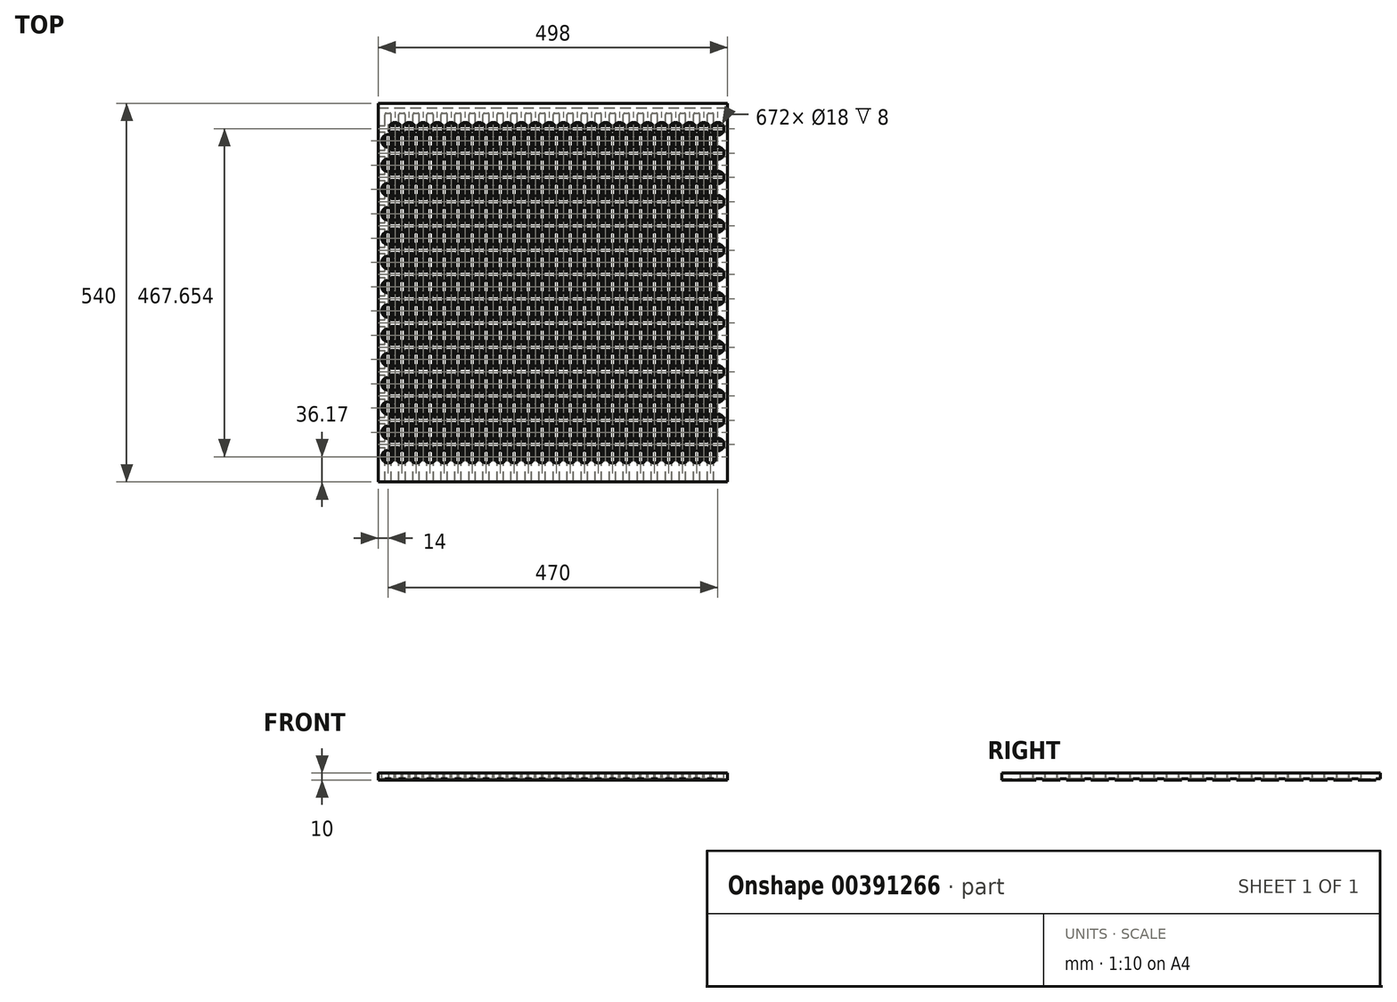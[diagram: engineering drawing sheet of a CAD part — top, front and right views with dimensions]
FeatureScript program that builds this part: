
annotation { "Feature Type Name" : "Feature", "Feature Type Description" : "" }
export const myFeature = defineFeature(function(context is Context, id is Id, definition is map)
    precondition{}
    {
        {
            var Q0;
            Q0=qCreatedBy(makeId("Top.planeOp"),FACE);
            var sketch = newSketch(context, id + "F0", { "sketchPlane" : qUnion([Q0])});
            skCircle(sketch, "E0", {"center": v(0, 0) * mm, "radius": 9 * mm});
            skCircle(sketch, "E1.1.0.0", {"center": v(20, 0) * mm, "radius": 9 * mm});
            skCircle(sketch, "E1.2.0.0", {"center": v(40, 0) * mm, "radius": 9 * mm});
            skCircle(sketch, "E1.3.0.0", {"center": v(60, 0) * mm, "radius": 9 * mm});
            skCircle(sketch, "E1.4.0.0", {"center": v(80, 0) * mm, "radius": 9 * mm});
            skCircle(sketch, "E1.5.0.0", {"center": v(100, 0) * mm, "radius": 9 * mm});
            skCircle(sketch, "E1.6.0.0", {"center": v(120, 0) * mm, "radius": 9 * mm});
            skCircle(sketch, "E1.7.0.0", {"center": v(140, 0) * mm, "radius": 9 * mm});
            skCircle(sketch, "E1.8.0.0", {"center": v(160, 0) * mm, "radius": 9 * mm});
            skCircle(sketch, "E1.9.0.0", {"center": v(180, 0) * mm, "radius": 9 * mm});
            skCircle(sketch, "E1.10.0.0", {"center": v(200, 0) * mm, "radius": 9 * mm});
            skCircle(sketch, "E1.11.0.0", {"center": v(220, 0) * mm, "radius": 9 * mm});
            skCircle(sketch, "E1.12.0.0", {"center": v(240, 0) * mm, "radius": 9 * mm});
            skCircle(sketch, "E1.13.0.0", {"center": v(260, 0) * mm, "radius": 9 * mm});
            skCircle(sketch, "E1.14.0.0", {"center": v(280, 0) * mm, "radius": 9 * mm});
            skCircle(sketch, "E1.15.0.0", {"center": v(300, 0) * mm, "radius": 9 * mm});
            skCircle(sketch, "E1.16.0.0", {"center": v(320, 0) * mm, "radius": 9 * mm});
            skCircle(sketch, "E1.17.0.0", {"center": v(340, 0) * mm, "radius": 9 * mm});
            skCircle(sketch, "E1.18.0.0", {"center": v(360, 0) * mm, "radius": 9 * mm});
            skCircle(sketch, "E1.19.0.0", {"center": v(380, 0) * mm, "radius": 9 * mm});
            skCircle(sketch, "E1.20.0.0", {"center": v(400, 0) * mm, "radius": 9 * mm});
            skCircle(sketch, "E1.21.0.0", {"center": v(420, 0) * mm, "radius": 9 * mm});
            skCircle(sketch, "E1.22.0.0", {"center": v(440, 0) * mm, "radius": 9 * mm});
            skCircle(sketch, "E1.23.0.0", {"center": v(460, 0) * mm, "radius": 9 * mm});
            skLineSegment(sketch, "E1.direction1", {"start": v(0, 0) * mm, "end": v(20, 0) * mm, "construction": true});
            skCircle(sketch, "E2", {"center": v(10, 17.32) * mm, "radius": 9 * mm});
            skCircle(sketch, "E3.1.0.0", {"center": v(30, 17.32) * mm, "radius": 9 * mm});
            skCircle(sketch, "E3.2.0.0", {"center": v(50, 17.32) * mm, "radius": 9 * mm});
            skCircle(sketch, "E3.3.0.0", {"center": v(70, 17.32) * mm, "radius": 9 * mm});
            skCircle(sketch, "E3.4.0.0", {"center": v(90, 17.32) * mm, "radius": 9 * mm});
            skCircle(sketch, "E3.5.0.0", {"center": v(110, 17.32) * mm, "radius": 9 * mm});
            skCircle(sketch, "E3.6.0.0", {"center": v(130, 17.32) * mm, "radius": 9 * mm});
            skCircle(sketch, "E3.7.0.0", {"center": v(150, 17.32) * mm, "radius": 9 * mm});
            skCircle(sketch, "E3.8.0.0", {"center": v(170, 17.32) * mm, "radius": 9 * mm});
            skCircle(sketch, "E3.9.0.0", {"center": v(190, 17.32) * mm, "radius": 9 * mm});
            skCircle(sketch, "E3.10.0.0", {"center": v(210, 17.32) * mm, "radius": 9 * mm});
            skCircle(sketch, "E3.11.0.0", {"center": v(230, 17.32) * mm, "radius": 9 * mm});
            skCircle(sketch, "E3.12.0.0", {"center": v(250, 17.32) * mm, "radius": 9 * mm});
            skCircle(sketch, "E3.13.0.0", {"center": v(270, 17.32) * mm, "radius": 9 * mm});
            skCircle(sketch, "E3.14.0.0", {"center": v(290, 17.32) * mm, "radius": 9 * mm});
            skCircle(sketch, "E3.15.0.0", {"center": v(310, 17.32) * mm, "radius": 9 * mm});
            skCircle(sketch, "E3.16.0.0", {"center": v(330, 17.32) * mm, "radius": 9 * mm});
            skCircle(sketch, "E3.17.0.0", {"center": v(350, 17.32) * mm, "radius": 9 * mm});
            skCircle(sketch, "E3.18.0.0", {"center": v(370, 17.32) * mm, "radius": 9 * mm});
            skCircle(sketch, "E3.19.0.0", {"center": v(390, 17.32) * mm, "radius": 9 * mm});
            skCircle(sketch, "E3.20.0.0", {"center": v(410, 17.32) * mm, "radius": 9 * mm});
            skCircle(sketch, "E3.21.0.0", {"center": v(430, 17.32) * mm, "radius": 9 * mm});
            skCircle(sketch, "E3.22.0.0", {"center": v(450, 17.32) * mm, "radius": 9 * mm});
            skCircle(sketch, "E3.23.0.0", {"center": v(470, 17.32) * mm, "radius": 9 * mm});
            skLineSegment(sketch, "E3.direction1", {"start": v(10, 17.32) * mm, "end": v(30, 17.32) * mm, "construction": true});
            skCircle(sketch, "E4.0.1.0", {"center": v(280, 34.64) * mm, "radius": 9 * mm});
            skCircle(sketch, "E4.0.1.1", {"center": v(260, 34.64) * mm, "radius": 9 * mm});
            skCircle(sketch, "E4.0.1.2", {"center": v(130, 51.96) * mm, "radius": 9 * mm});
            skCircle(sketch, "E4.0.1.3", {"center": v(60, 34.64) * mm, "radius": 9 * mm});
            skCircle(sketch, "E4.0.1.4", {"center": v(80, 34.64) * mm, "radius": 9 * mm});
            skCircle(sketch, "E4.0.1.5", {"center": v(100, 34.64) * mm, "radius": 9 * mm});
            skCircle(sketch, "E4.0.1.6", {"center": v(350, 51.96) * mm, "radius": 9 * mm});
            skCircle(sketch, "E4.0.1.7", {"center": v(0, 34.64) * mm, "radius": 9 * mm});
            skCircle(sketch, "E4.0.1.8", {"center": v(120, 34.64) * mm, "radius": 9 * mm});
            skCircle(sketch, "E4.0.1.9", {"center": v(30, 51.96) * mm, "radius": 9 * mm});
            skCircle(sketch, "E4.0.1.10", {"center": v(380, 34.64) * mm, "radius": 9 * mm});
            skCircle(sketch, "E4.0.1.11", {"center": v(140, 34.64) * mm, "radius": 9 * mm});
            skCircle(sketch, "E4.0.1.12", {"center": v(450, 51.96) * mm, "radius": 9 * mm});
            skCircle(sketch, "E4.0.1.13", {"center": v(160, 34.64) * mm, "radius": 9 * mm});
            skCircle(sketch, "E4.0.1.14", {"center": v(300, 34.64) * mm, "radius": 9 * mm});
            skCircle(sketch, "E4.0.1.15", {"center": v(40, 34.64) * mm, "radius": 9 * mm});
            skCircle(sketch, "E4.0.1.16", {"center": v(210, 51.96) * mm, "radius": 9 * mm});
            skCircle(sketch, "E4.0.1.17", {"center": v(330, 51.96) * mm, "radius": 9 * mm});
            skCircle(sketch, "E4.0.1.18", {"center": v(270, 51.96) * mm, "radius": 9 * mm});
            skCircle(sketch, "E4.0.1.19", {"center": v(440, 34.64) * mm, "radius": 9 * mm});
            skCircle(sketch, "E4.0.1.20", {"center": v(110, 51.96) * mm, "radius": 9 * mm});
            skCircle(sketch, "E4.0.1.21", {"center": v(250, 51.96) * mm, "radius": 9 * mm});
            skCircle(sketch, "E4.0.1.22", {"center": v(180, 34.64) * mm, "radius": 9 * mm});
            skCircle(sketch, "E4.0.1.23", {"center": v(430, 51.96) * mm, "radius": 9 * mm});
            skCircle(sketch, "E4.0.1.24", {"center": v(200, 34.64) * mm, "radius": 9 * mm});
            skCircle(sketch, "E4.0.1.25", {"center": v(420, 34.64) * mm, "radius": 9 * mm});
            skCircle(sketch, "E4.0.1.26", {"center": v(70, 51.96) * mm, "radius": 9 * mm});
            skCircle(sketch, "E4.0.1.27", {"center": v(390, 51.96) * mm, "radius": 9 * mm});
            skCircle(sketch, "E4.0.1.28", {"center": v(220, 34.64) * mm, "radius": 9 * mm});
            skCircle(sketch, "E4.0.1.29", {"center": v(190, 51.96) * mm, "radius": 9 * mm});
            skCircle(sketch, "E4.0.1.30", {"center": v(90, 51.96) * mm, "radius": 9 * mm});
            skCircle(sketch, "E4.0.1.31", {"center": v(230, 51.96) * mm, "radius": 9 * mm});
            skCircle(sketch, "E4.0.1.32", {"center": v(150, 51.96) * mm, "radius": 9 * mm});
            skCircle(sketch, "E4.0.1.33", {"center": v(470, 51.96) * mm, "radius": 9 * mm});
            skCircle(sketch, "E4.0.1.34", {"center": v(410, 51.96) * mm, "radius": 9 * mm});
            skCircle(sketch, "E4.0.1.35", {"center": v(50, 51.96) * mm, "radius": 9 * mm});
            skCircle(sketch, "E4.0.1.36", {"center": v(400, 34.64) * mm, "radius": 9 * mm});
            skCircle(sketch, "E4.0.1.37", {"center": v(240, 34.64) * mm, "radius": 9 * mm});
            skCircle(sketch, "E4.0.1.38", {"center": v(320, 34.64) * mm, "radius": 9 * mm});
            skCircle(sketch, "E4.0.1.39", {"center": v(370, 51.96) * mm, "radius": 9 * mm});
            skCircle(sketch, "E4.0.1.40", {"center": v(10, 51.96) * mm, "radius": 9 * mm});
            skCircle(sketch, "E4.0.1.41", {"center": v(290, 51.96) * mm, "radius": 9 * mm});
            skCircle(sketch, "E4.0.1.42", {"center": v(360, 34.64) * mm, "radius": 9 * mm});
            skCircle(sketch, "E4.0.1.43", {"center": v(460, 34.64) * mm, "radius": 9 * mm});
            skCircle(sketch, "E4.0.1.44", {"center": v(310, 51.96) * mm, "radius": 9 * mm});
            skCircle(sketch, "E4.0.1.45", {"center": v(340, 34.64) * mm, "radius": 9 * mm});
            skCircle(sketch, "E4.0.1.46", {"center": v(170, 51.96) * mm, "radius": 9 * mm});
            skCircle(sketch, "E4.0.1.47", {"center": v(20, 34.64) * mm, "radius": 9 * mm});
            skLineSegment(sketch, "E4.0.1.48", {"start": v(0, 34.64) * mm, "end": v(20, 34.64) * mm, "construction": true});
            skLineSegment(sketch, "E4.0.1.49", {"start": v(10, 51.96) * mm, "end": v(30, 51.96) * mm, "construction": true});
            skCircle(sketch, "E4.0.2.0", {"center": v(280, 69.28) * mm, "radius": 9 * mm});
            skCircle(sketch, "E4.0.2.1", {"center": v(260, 69.28) * mm, "radius": 9 * mm});
            skCircle(sketch, "E4.0.2.2", {"center": v(130, 86.6) * mm, "radius": 9 * mm});
            skCircle(sketch, "E4.0.2.3", {"center": v(60, 69.28) * mm, "radius": 9 * mm});
            skCircle(sketch, "E4.0.2.4", {"center": v(80, 69.28) * mm, "radius": 9 * mm});
            skCircle(sketch, "E4.0.2.5", {"center": v(100, 69.28) * mm, "radius": 9 * mm});
            skCircle(sketch, "E4.0.2.6", {"center": v(350, 86.6) * mm, "radius": 9 * mm});
            skCircle(sketch, "E4.0.2.7", {"center": v(0, 69.28) * mm, "radius": 9 * mm});
            skCircle(sketch, "E4.0.2.8", {"center": v(120, 69.28) * mm, "radius": 9 * mm});
            skCircle(sketch, "E4.0.2.9", {"center": v(30, 86.6) * mm, "radius": 9 * mm});
            skCircle(sketch, "E4.0.2.10", {"center": v(380, 69.28) * mm, "radius": 9 * mm});
            skCircle(sketch, "E4.0.2.11", {"center": v(140, 69.28) * mm, "radius": 9 * mm});
            skCircle(sketch, "E4.0.2.12", {"center": v(450, 86.6) * mm, "radius": 9 * mm});
            skCircle(sketch, "E4.0.2.13", {"center": v(160, 69.28) * mm, "radius": 9 * mm});
            skCircle(sketch, "E4.0.2.14", {"center": v(300, 69.28) * mm, "radius": 9 * mm});
            skCircle(sketch, "E4.0.2.15", {"center": v(40, 69.28) * mm, "radius": 9 * mm});
            skCircle(sketch, "E4.0.2.16", {"center": v(210, 86.6) * mm, "radius": 9 * mm});
            skCircle(sketch, "E4.0.2.17", {"center": v(330, 86.6) * mm, "radius": 9 * mm});
            skCircle(sketch, "E4.0.2.18", {"center": v(270, 86.6) * mm, "radius": 9 * mm});
            skCircle(sketch, "E4.0.2.19", {"center": v(440, 69.28) * mm, "radius": 9 * mm});
            skCircle(sketch, "E4.0.2.20", {"center": v(110, 86.6) * mm, "radius": 9 * mm});
            skCircle(sketch, "E4.0.2.21", {"center": v(250, 86.6) * mm, "radius": 9 * mm});
            skCircle(sketch, "E4.0.2.22", {"center": v(180, 69.28) * mm, "radius": 9 * mm});
            skCircle(sketch, "E4.0.2.23", {"center": v(430, 86.6) * mm, "radius": 9 * mm});
            skCircle(sketch, "E4.0.2.24", {"center": v(200, 69.28) * mm, "radius": 9 * mm});
            skCircle(sketch, "E4.0.2.25", {"center": v(420, 69.28) * mm, "radius": 9 * mm});
            skCircle(sketch, "E4.0.2.26", {"center": v(70, 86.6) * mm, "radius": 9 * mm});
            skCircle(sketch, "E4.0.2.27", {"center": v(390, 86.6) * mm, "radius": 9 * mm});
            skCircle(sketch, "E4.0.2.28", {"center": v(220, 69.28) * mm, "radius": 9 * mm});
            skCircle(sketch, "E4.0.2.29", {"center": v(190, 86.6) * mm, "radius": 9 * mm});
            skCircle(sketch, "E4.0.2.30", {"center": v(90, 86.6) * mm, "radius": 9 * mm});
            skCircle(sketch, "E4.0.2.31", {"center": v(230, 86.6) * mm, "radius": 9 * mm});
            skCircle(sketch, "E4.0.2.32", {"center": v(150, 86.6) * mm, "radius": 9 * mm});
            skCircle(sketch, "E4.0.2.33", {"center": v(470, 86.6) * mm, "radius": 9 * mm});
            skCircle(sketch, "E4.0.2.34", {"center": v(410, 86.6) * mm, "radius": 9 * mm});
            skCircle(sketch, "E4.0.2.35", {"center": v(50, 86.6) * mm, "radius": 9 * mm});
            skCircle(sketch, "E4.0.2.36", {"center": v(400, 69.28) * mm, "radius": 9 * mm});
            skCircle(sketch, "E4.0.2.37", {"center": v(240, 69.28) * mm, "radius": 9 * mm});
            skCircle(sketch, "E4.0.2.38", {"center": v(320, 69.28) * mm, "radius": 9 * mm});
            skCircle(sketch, "E4.0.2.39", {"center": v(370, 86.6) * mm, "radius": 9 * mm});
            skCircle(sketch, "E4.0.2.40", {"center": v(10, 86.6) * mm, "radius": 9 * mm});
            skCircle(sketch, "E4.0.2.41", {"center": v(290, 86.6) * mm, "radius": 9 * mm});
            skCircle(sketch, "E4.0.2.42", {"center": v(360, 69.28) * mm, "radius": 9 * mm});
            skCircle(sketch, "E4.0.2.43", {"center": v(460, 69.28) * mm, "radius": 9 * mm});
            skCircle(sketch, "E4.0.2.44", {"center": v(310, 86.6) * mm, "radius": 9 * mm});
            skCircle(sketch, "E4.0.2.45", {"center": v(340, 69.28) * mm, "radius": 9 * mm});
            skCircle(sketch, "E4.0.2.46", {"center": v(170, 86.6) * mm, "radius": 9 * mm});
            skCircle(sketch, "E4.0.2.47", {"center": v(20, 69.28) * mm, "radius": 9 * mm});
            skLineSegment(sketch, "E4.0.2.48", {"start": v(0, 69.28) * mm, "end": v(20, 69.28) * mm, "construction": true});
            skLineSegment(sketch, "E4.0.2.49", {"start": v(10, 86.6) * mm, "end": v(30, 86.6) * mm, "construction": true});
            skCircle(sketch, "E4.0.3.0", {"center": v(280, 103.92) * mm, "radius": 9 * mm});
            skCircle(sketch, "E4.0.3.1", {"center": v(260, 103.92) * mm, "radius": 9 * mm});
            skCircle(sketch, "E4.0.3.2", {"center": v(130, 121.24) * mm, "radius": 9 * mm});
            skCircle(sketch, "E4.0.3.3", {"center": v(60, 103.92) * mm, "radius": 9 * mm});
            skCircle(sketch, "E4.0.3.4", {"center": v(80, 103.92) * mm, "radius": 9 * mm});
            skCircle(sketch, "E4.0.3.5", {"center": v(100, 103.92) * mm, "radius": 9 * mm});
            skCircle(sketch, "E4.0.3.6", {"center": v(350, 121.24) * mm, "radius": 9 * mm});
            skCircle(sketch, "E4.0.3.7", {"center": v(0, 103.92) * mm, "radius": 9 * mm});
            skCircle(sketch, "E4.0.3.8", {"center": v(120, 103.92) * mm, "radius": 9 * mm});
            skCircle(sketch, "E4.0.3.9", {"center": v(30, 121.24) * mm, "radius": 9 * mm});
            skCircle(sketch, "E4.0.3.10", {"center": v(380, 103.92) * mm, "radius": 9 * mm});
            skCircle(sketch, "E4.0.3.11", {"center": v(140, 103.92) * mm, "radius": 9 * mm});
            skCircle(sketch, "E4.0.3.12", {"center": v(450, 121.24) * mm, "radius": 9 * mm});
            skCircle(sketch, "E4.0.3.13", {"center": v(160, 103.92) * mm, "radius": 9 * mm});
            skCircle(sketch, "E4.0.3.14", {"center": v(300, 103.92) * mm, "radius": 9 * mm});
            skCircle(sketch, "E4.0.3.15", {"center": v(40, 103.92) * mm, "radius": 9 * mm});
            skCircle(sketch, "E4.0.3.16", {"center": v(210, 121.24) * mm, "radius": 9 * mm});
            skCircle(sketch, "E4.0.3.17", {"center": v(330, 121.24) * mm, "radius": 9 * mm});
            skCircle(sketch, "E4.0.3.18", {"center": v(270, 121.24) * mm, "radius": 9 * mm});
            skCircle(sketch, "E4.0.3.19", {"center": v(440, 103.92) * mm, "radius": 9 * mm});
            skCircle(sketch, "E4.0.3.20", {"center": v(110, 121.24) * mm, "radius": 9 * mm});
            skCircle(sketch, "E4.0.3.21", {"center": v(250, 121.24) * mm, "radius": 9 * mm});
            skCircle(sketch, "E4.0.3.22", {"center": v(180, 103.92) * mm, "radius": 9 * mm});
            skCircle(sketch, "E4.0.3.23", {"center": v(430, 121.24) * mm, "radius": 9 * mm});
            skCircle(sketch, "E4.0.3.24", {"center": v(200, 103.92) * mm, "radius": 9 * mm});
            skCircle(sketch, "E4.0.3.25", {"center": v(420, 103.92) * mm, "radius": 9 * mm});
            skCircle(sketch, "E4.0.3.26", {"center": v(70, 121.24) * mm, "radius": 9 * mm});
            skCircle(sketch, "E4.0.3.27", {"center": v(390, 121.24) * mm, "radius": 9 * mm});
            skCircle(sketch, "E4.0.3.28", {"center": v(220, 103.92) * mm, "radius": 9 * mm});
            skCircle(sketch, "E4.0.3.29", {"center": v(190, 121.24) * mm, "radius": 9 * mm});
            skCircle(sketch, "E4.0.3.30", {"center": v(90, 121.24) * mm, "radius": 9 * mm});
            skCircle(sketch, "E4.0.3.31", {"center": v(230, 121.24) * mm, "radius": 9 * mm});
            skCircle(sketch, "E4.0.3.32", {"center": v(150, 121.24) * mm, "radius": 9 * mm});
            skCircle(sketch, "E4.0.3.33", {"center": v(470, 121.24) * mm, "radius": 9 * mm});
            skCircle(sketch, "E4.0.3.34", {"center": v(410, 121.24) * mm, "radius": 9 * mm});
            skCircle(sketch, "E4.0.3.35", {"center": v(50, 121.24) * mm, "radius": 9 * mm});
            skCircle(sketch, "E4.0.3.36", {"center": v(400, 103.92) * mm, "radius": 9 * mm});
            skCircle(sketch, "E4.0.3.37", {"center": v(240, 103.92) * mm, "radius": 9 * mm});
            skCircle(sketch, "E4.0.3.38", {"center": v(320, 103.92) * mm, "radius": 9 * mm});
            skCircle(sketch, "E4.0.3.39", {"center": v(370, 121.24) * mm, "radius": 9 * mm});
            skCircle(sketch, "E4.0.3.40", {"center": v(10, 121.24) * mm, "radius": 9 * mm});
            skCircle(sketch, "E4.0.3.41", {"center": v(290, 121.24) * mm, "radius": 9 * mm});
            skCircle(sketch, "E4.0.3.42", {"center": v(360, 103.92) * mm, "radius": 9 * mm});
            skCircle(sketch, "E4.0.3.43", {"center": v(460, 103.92) * mm, "radius": 9 * mm});
            skCircle(sketch, "E4.0.3.44", {"center": v(310, 121.24) * mm, "radius": 9 * mm});
            skCircle(sketch, "E4.0.3.45", {"center": v(340, 103.92) * mm, "radius": 9 * mm});
            skCircle(sketch, "E4.0.3.46", {"center": v(170, 121.24) * mm, "radius": 9 * mm});
            skCircle(sketch, "E4.0.3.47", {"center": v(20, 103.92) * mm, "radius": 9 * mm});
            skLineSegment(sketch, "E4.0.3.48", {"start": v(0, 103.92) * mm, "end": v(20, 103.92) * mm, "construction": true});
            skLineSegment(sketch, "E4.0.3.49", {"start": v(10, 121.24) * mm, "end": v(30, 121.24) * mm, "construction": true});
            skCircle(sketch, "E4.0.4.0", {"center": v(280, 138.56) * mm, "radius": 9 * mm});
            skCircle(sketch, "E4.0.4.1", {"center": v(260, 138.56) * mm, "radius": 9 * mm});
            skCircle(sketch, "E4.0.4.2", {"center": v(130, 155.88) * mm, "radius": 9 * mm});
            skCircle(sketch, "E4.0.4.3", {"center": v(60, 138.56) * mm, "radius": 9 * mm});
            skCircle(sketch, "E4.0.4.4", {"center": v(80, 138.56) * mm, "radius": 9 * mm});
            skCircle(sketch, "E4.0.4.5", {"center": v(100, 138.56) * mm, "radius": 9 * mm});
            skCircle(sketch, "E4.0.4.6", {"center": v(350, 155.88) * mm, "radius": 9 * mm});
            skCircle(sketch, "E4.0.4.7", {"center": v(0, 138.56) * mm, "radius": 9 * mm});
            skCircle(sketch, "E4.0.4.8", {"center": v(120, 138.56) * mm, "radius": 9 * mm});
            skCircle(sketch, "E4.0.4.9", {"center": v(30, 155.88) * mm, "radius": 9 * mm});
            skCircle(sketch, "E4.0.4.10", {"center": v(380, 138.56) * mm, "radius": 9 * mm});
            skCircle(sketch, "E4.0.4.11", {"center": v(140, 138.56) * mm, "radius": 9 * mm});
            skCircle(sketch, "E4.0.4.12", {"center": v(450, 155.88) * mm, "radius": 9 * mm});
            skCircle(sketch, "E4.0.4.13", {"center": v(160, 138.56) * mm, "radius": 9 * mm});
            skCircle(sketch, "E4.0.4.14", {"center": v(300, 138.56) * mm, "radius": 9 * mm});
            skCircle(sketch, "E4.0.4.15", {"center": v(40, 138.56) * mm, "radius": 9 * mm});
            skCircle(sketch, "E4.0.4.16", {"center": v(210, 155.88) * mm, "radius": 9 * mm});
            skCircle(sketch, "E4.0.4.17", {"center": v(330, 155.88) * mm, "radius": 9 * mm});
            skCircle(sketch, "E4.0.4.18", {"center": v(270, 155.88) * mm, "radius": 9 * mm});
            skCircle(sketch, "E4.0.4.19", {"center": v(440, 138.56) * mm, "radius": 9 * mm});
            skCircle(sketch, "E4.0.4.20", {"center": v(110, 155.88) * mm, "radius": 9 * mm});
            skCircle(sketch, "E4.0.4.21", {"center": v(250, 155.88) * mm, "radius": 9 * mm});
            skCircle(sketch, "E4.0.4.22", {"center": v(180, 138.56) * mm, "radius": 9 * mm});
            skCircle(sketch, "E4.0.4.23", {"center": v(430, 155.88) * mm, "radius": 9 * mm});
            skCircle(sketch, "E4.0.4.24", {"center": v(200, 138.56) * mm, "radius": 9 * mm});
            skCircle(sketch, "E4.0.4.25", {"center": v(420, 138.56) * mm, "radius": 9 * mm});
            skCircle(sketch, "E4.0.4.26", {"center": v(70, 155.88) * mm, "radius": 9 * mm});
            skCircle(sketch, "E4.0.4.27", {"center": v(390, 155.88) * mm, "radius": 9 * mm});
            skCircle(sketch, "E4.0.4.28", {"center": v(220, 138.56) * mm, "radius": 9 * mm});
            skCircle(sketch, "E4.0.4.29", {"center": v(190, 155.88) * mm, "radius": 9 * mm});
            skCircle(sketch, "E4.0.4.30", {"center": v(90, 155.88) * mm, "radius": 9 * mm});
            skCircle(sketch, "E4.0.4.31", {"center": v(230, 155.88) * mm, "radius": 9 * mm});
            skCircle(sketch, "E4.0.4.32", {"center": v(150, 155.88) * mm, "radius": 9 * mm});
            skCircle(sketch, "E4.0.4.33", {"center": v(470, 155.88) * mm, "radius": 9 * mm});
            skCircle(sketch, "E4.0.4.34", {"center": v(410, 155.88) * mm, "radius": 9 * mm});
            skCircle(sketch, "E4.0.4.35", {"center": v(50, 155.88) * mm, "radius": 9 * mm});
            skCircle(sketch, "E4.0.4.36", {"center": v(400, 138.56) * mm, "radius": 9 * mm});
            skCircle(sketch, "E4.0.4.37", {"center": v(240, 138.56) * mm, "radius": 9 * mm});
            skCircle(sketch, "E4.0.4.38", {"center": v(320, 138.56) * mm, "radius": 9 * mm});
            skCircle(sketch, "E4.0.4.39", {"center": v(370, 155.88) * mm, "radius": 9 * mm});
            skCircle(sketch, "E4.0.4.40", {"center": v(10, 155.88) * mm, "radius": 9 * mm});
            skCircle(sketch, "E4.0.4.41", {"center": v(290, 155.88) * mm, "radius": 9 * mm});
            skCircle(sketch, "E4.0.4.42", {"center": v(360, 138.56) * mm, "radius": 9 * mm});
            skCircle(sketch, "E4.0.4.43", {"center": v(460, 138.56) * mm, "radius": 9 * mm});
            skCircle(sketch, "E4.0.4.44", {"center": v(310, 155.88) * mm, "radius": 9 * mm});
            skCircle(sketch, "E4.0.4.45", {"center": v(340, 138.56) * mm, "radius": 9 * mm});
            skCircle(sketch, "E4.0.4.46", {"center": v(170, 155.88) * mm, "radius": 9 * mm});
            skCircle(sketch, "E4.0.4.47", {"center": v(20, 138.56) * mm, "radius": 9 * mm});
            skLineSegment(sketch, "E4.0.4.48", {"start": v(0, 138.56) * mm, "end": v(20, 138.56) * mm, "construction": true});
            skLineSegment(sketch, "E4.0.4.49", {"start": v(10, 155.88) * mm, "end": v(30, 155.88) * mm, "construction": true});
            skCircle(sketch, "E4.0.5.0", {"center": v(280, 173.2) * mm, "radius": 9 * mm});
            skCircle(sketch, "E4.0.5.1", {"center": v(260, 173.2) * mm, "radius": 9 * mm});
            skCircle(sketch, "E4.0.5.2", {"center": v(130, 190.53) * mm, "radius": 9 * mm});
            skCircle(sketch, "E4.0.5.3", {"center": v(60, 173.2) * mm, "radius": 9 * mm});
            skCircle(sketch, "E4.0.5.4", {"center": v(80, 173.2) * mm, "radius": 9 * mm});
            skCircle(sketch, "E4.0.5.5", {"center": v(100, 173.2) * mm, "radius": 9 * mm});
            skCircle(sketch, "E4.0.5.6", {"center": v(350, 190.53) * mm, "radius": 9 * mm});
            skCircle(sketch, "E4.0.5.7", {"center": v(0, 173.2) * mm, "radius": 9 * mm});
            skCircle(sketch, "E4.0.5.8", {"center": v(120, 173.2) * mm, "radius": 9 * mm});
            skCircle(sketch, "E4.0.5.9", {"center": v(30, 190.53) * mm, "radius": 9 * mm});
            skCircle(sketch, "E4.0.5.10", {"center": v(380, 173.2) * mm, "radius": 9 * mm});
            skCircle(sketch, "E4.0.5.11", {"center": v(140, 173.2) * mm, "radius": 9 * mm});
            skCircle(sketch, "E4.0.5.12", {"center": v(450, 190.53) * mm, "radius": 9 * mm});
            skCircle(sketch, "E4.0.5.13", {"center": v(160, 173.2) * mm, "radius": 9 * mm});
            skCircle(sketch, "E4.0.5.14", {"center": v(300, 173.2) * mm, "radius": 9 * mm});
            skCircle(sketch, "E4.0.5.15", {"center": v(40, 173.2) * mm, "radius": 9 * mm});
            skCircle(sketch, "E4.0.5.16", {"center": v(210, 190.53) * mm, "radius": 9 * mm});
            skCircle(sketch, "E4.0.5.17", {"center": v(330, 190.53) * mm, "radius": 9 * mm});
            skCircle(sketch, "E4.0.5.18", {"center": v(270, 190.53) * mm, "radius": 9 * mm});
            skCircle(sketch, "E4.0.5.19", {"center": v(440, 173.2) * mm, "radius": 9 * mm});
            skCircle(sketch, "E4.0.5.20", {"center": v(110, 190.53) * mm, "radius": 9 * mm});
            skCircle(sketch, "E4.0.5.21", {"center": v(250, 190.53) * mm, "radius": 9 * mm});
            skCircle(sketch, "E4.0.5.22", {"center": v(180, 173.2) * mm, "radius": 9 * mm});
            skCircle(sketch, "E4.0.5.23", {"center": v(430, 190.53) * mm, "radius": 9 * mm});
            skCircle(sketch, "E4.0.5.24", {"center": v(200, 173.2) * mm, "radius": 9 * mm});
            skCircle(sketch, "E4.0.5.25", {"center": v(420, 173.2) * mm, "radius": 9 * mm});
            skCircle(sketch, "E4.0.5.26", {"center": v(70, 190.53) * mm, "radius": 9 * mm});
            skCircle(sketch, "E4.0.5.27", {"center": v(390, 190.53) * mm, "radius": 9 * mm});
            skCircle(sketch, "E4.0.5.28", {"center": v(220, 173.2) * mm, "radius": 9 * mm});
            skCircle(sketch, "E4.0.5.29", {"center": v(190, 190.53) * mm, "radius": 9 * mm});
            skCircle(sketch, "E4.0.5.30", {"center": v(90, 190.53) * mm, "radius": 9 * mm});
            skCircle(sketch, "E4.0.5.31", {"center": v(230, 190.53) * mm, "radius": 9 * mm});
            skCircle(sketch, "E4.0.5.32", {"center": v(150, 190.53) * mm, "radius": 9 * mm});
            skCircle(sketch, "E4.0.5.33", {"center": v(470, 190.53) * mm, "radius": 9 * mm});
            skCircle(sketch, "E4.0.5.34", {"center": v(410, 190.53) * mm, "radius": 9 * mm});
            skCircle(sketch, "E4.0.5.35", {"center": v(50, 190.53) * mm, "radius": 9 * mm});
            skCircle(sketch, "E4.0.5.36", {"center": v(400, 173.2) * mm, "radius": 9 * mm});
            skCircle(sketch, "E4.0.5.37", {"center": v(240, 173.2) * mm, "radius": 9 * mm});
            skCircle(sketch, "E4.0.5.38", {"center": v(320, 173.2) * mm, "radius": 9 * mm});
            skCircle(sketch, "E4.0.5.39", {"center": v(370, 190.53) * mm, "radius": 9 * mm});
            skCircle(sketch, "E4.0.5.40", {"center": v(10, 190.53) * mm, "radius": 9 * mm});
            skCircle(sketch, "E4.0.5.41", {"center": v(290, 190.53) * mm, "radius": 9 * mm});
            skCircle(sketch, "E4.0.5.42", {"center": v(360, 173.2) * mm, "radius": 9 * mm});
            skCircle(sketch, "E4.0.5.43", {"center": v(460, 173.2) * mm, "radius": 9 * mm});
            skCircle(sketch, "E4.0.5.44", {"center": v(310, 190.53) * mm, "radius": 9 * mm});
            skCircle(sketch, "E4.0.5.45", {"center": v(340, 173.2) * mm, "radius": 9 * mm});
            skCircle(sketch, "E4.0.5.46", {"center": v(170, 190.53) * mm, "radius": 9 * mm});
            skCircle(sketch, "E4.0.5.47", {"center": v(20, 173.2) * mm, "radius": 9 * mm});
            skLineSegment(sketch, "E4.0.5.48", {"start": v(0, 173.2) * mm, "end": v(20, 173.2) * mm, "construction": true});
            skLineSegment(sketch, "E4.0.5.49", {"start": v(10, 190.53) * mm, "end": v(30, 190.53) * mm, "construction": true});
            skCircle(sketch, "E4.0.6.0", {"center": v(280, 207.85) * mm, "radius": 9 * mm});
            skCircle(sketch, "E4.0.6.1", {"center": v(260, 207.85) * mm, "radius": 9 * mm});
            skCircle(sketch, "E4.0.6.2", {"center": v(130, 225.17) * mm, "radius": 9 * mm});
            skCircle(sketch, "E4.0.6.3", {"center": v(60, 207.85) * mm, "radius": 9 * mm});
            skCircle(sketch, "E4.0.6.4", {"center": v(80, 207.85) * mm, "radius": 9 * mm});
            skCircle(sketch, "E4.0.6.5", {"center": v(100, 207.85) * mm, "radius": 9 * mm});
            skCircle(sketch, "E4.0.6.6", {"center": v(350, 225.17) * mm, "radius": 9 * mm});
            skCircle(sketch, "E4.0.6.7", {"center": v(0, 207.85) * mm, "radius": 9 * mm});
            skCircle(sketch, "E4.0.6.8", {"center": v(120, 207.85) * mm, "radius": 9 * mm});
            skCircle(sketch, "E4.0.6.9", {"center": v(30, 225.17) * mm, "radius": 9 * mm});
            skCircle(sketch, "E4.0.6.10", {"center": v(380, 207.85) * mm, "radius": 9 * mm});
            skCircle(sketch, "E4.0.6.11", {"center": v(140, 207.85) * mm, "radius": 9 * mm});
            skCircle(sketch, "E4.0.6.12", {"center": v(450, 225.17) * mm, "radius": 9 * mm});
            skCircle(sketch, "E4.0.6.13", {"center": v(160, 207.85) * mm, "radius": 9 * mm});
            skCircle(sketch, "E4.0.6.14", {"center": v(300, 207.85) * mm, "radius": 9 * mm});
            skCircle(sketch, "E4.0.6.15", {"center": v(40, 207.85) * mm, "radius": 9 * mm});
            skCircle(sketch, "E4.0.6.16", {"center": v(210, 225.17) * mm, "radius": 9 * mm});
            skCircle(sketch, "E4.0.6.17", {"center": v(330, 225.17) * mm, "radius": 9 * mm});
            skCircle(sketch, "E4.0.6.18", {"center": v(270, 225.17) * mm, "radius": 9 * mm});
            skCircle(sketch, "E4.0.6.19", {"center": v(440, 207.85) * mm, "radius": 9 * mm});
            skCircle(sketch, "E4.0.6.20", {"center": v(110, 225.17) * mm, "radius": 9 * mm});
            skCircle(sketch, "E4.0.6.21", {"center": v(250, 225.17) * mm, "radius": 9 * mm});
            skCircle(sketch, "E4.0.6.22", {"center": v(180, 207.85) * mm, "radius": 9 * mm});
            skCircle(sketch, "E4.0.6.23", {"center": v(430, 225.17) * mm, "radius": 9 * mm});
            skCircle(sketch, "E4.0.6.24", {"center": v(200, 207.85) * mm, "radius": 9 * mm});
            skCircle(sketch, "E4.0.6.25", {"center": v(420, 207.85) * mm, "radius": 9 * mm});
            skCircle(sketch, "E4.0.6.26", {"center": v(70, 225.17) * mm, "radius": 9 * mm});
            skCircle(sketch, "E4.0.6.27", {"center": v(390, 225.17) * mm, "radius": 9 * mm});
            skCircle(sketch, "E4.0.6.28", {"center": v(220, 207.85) * mm, "radius": 9 * mm});
            skCircle(sketch, "E4.0.6.29", {"center": v(190, 225.17) * mm, "radius": 9 * mm});
            skCircle(sketch, "E4.0.6.30", {"center": v(90, 225.17) * mm, "radius": 9 * mm});
            skCircle(sketch, "E4.0.6.31", {"center": v(230, 225.17) * mm, "radius": 9 * mm});
            skCircle(sketch, "E4.0.6.32", {"center": v(150, 225.17) * mm, "radius": 9 * mm});
            skCircle(sketch, "E4.0.6.33", {"center": v(470, 225.17) * mm, "radius": 9 * mm});
            skCircle(sketch, "E4.0.6.34", {"center": v(410, 225.17) * mm, "radius": 9 * mm});
            skCircle(sketch, "E4.0.6.35", {"center": v(50, 225.17) * mm, "radius": 9 * mm});
            skCircle(sketch, "E4.0.6.36", {"center": v(400, 207.85) * mm, "radius": 9 * mm});
            skCircle(sketch, "E4.0.6.37", {"center": v(240, 207.85) * mm, "radius": 9 * mm});
            skCircle(sketch, "E4.0.6.38", {"center": v(320, 207.85) * mm, "radius": 9 * mm});
            skCircle(sketch, "E4.0.6.39", {"center": v(370, 225.17) * mm, "radius": 9 * mm});
            skCircle(sketch, "E4.0.6.40", {"center": v(10, 225.17) * mm, "radius": 9 * mm});
            skCircle(sketch, "E4.0.6.41", {"center": v(290, 225.17) * mm, "radius": 9 * mm});
            skCircle(sketch, "E4.0.6.42", {"center": v(360, 207.85) * mm, "radius": 9 * mm});
            skCircle(sketch, "E4.0.6.43", {"center": v(460, 207.85) * mm, "radius": 9 * mm});
            skCircle(sketch, "E4.0.6.44", {"center": v(310, 225.17) * mm, "radius": 9 * mm});
            skCircle(sketch, "E4.0.6.45", {"center": v(340, 207.85) * mm, "radius": 9 * mm});
            skCircle(sketch, "E4.0.6.46", {"center": v(170, 225.17) * mm, "radius": 9 * mm});
            skCircle(sketch, "E4.0.6.47", {"center": v(20, 207.85) * mm, "radius": 9 * mm});
            skLineSegment(sketch, "E4.0.6.48", {"start": v(0, 207.85) * mm, "end": v(20, 207.85) * mm, "construction": true});
            skLineSegment(sketch, "E4.0.6.49", {"start": v(10, 225.17) * mm, "end": v(30, 225.17) * mm, "construction": true});
            skCircle(sketch, "E4.0.7.0", {"center": v(280, 242.49) * mm, "radius": 9 * mm});
            skCircle(sketch, "E4.0.7.1", {"center": v(260, 242.49) * mm, "radius": 9 * mm});
            skCircle(sketch, "E4.0.7.2", {"center": v(130, 259.8) * mm, "radius": 9 * mm});
            skCircle(sketch, "E4.0.7.3", {"center": v(60, 242.49) * mm, "radius": 9 * mm});
            skCircle(sketch, "E4.0.7.4", {"center": v(80, 242.49) * mm, "radius": 9 * mm});
            skCircle(sketch, "E4.0.7.5", {"center": v(100, 242.49) * mm, "radius": 9 * mm});
            skCircle(sketch, "E4.0.7.6", {"center": v(350, 259.8) * mm, "radius": 9 * mm});
            skCircle(sketch, "E4.0.7.7", {"center": v(0, 242.49) * mm, "radius": 9 * mm});
            skCircle(sketch, "E4.0.7.8", {"center": v(120, 242.49) * mm, "radius": 9 * mm});
            skCircle(sketch, "E4.0.7.9", {"center": v(30, 259.8) * mm, "radius": 9 * mm});
            skCircle(sketch, "E4.0.7.10", {"center": v(380, 242.49) * mm, "radius": 9 * mm});
            skCircle(sketch, "E4.0.7.11", {"center": v(140, 242.49) * mm, "radius": 9 * mm});
            skCircle(sketch, "E4.0.7.12", {"center": v(450, 259.8) * mm, "radius": 9 * mm});
            skCircle(sketch, "E4.0.7.13", {"center": v(160, 242.49) * mm, "radius": 9 * mm});
            skCircle(sketch, "E4.0.7.14", {"center": v(300, 242.49) * mm, "radius": 9 * mm});
            skCircle(sketch, "E4.0.7.15", {"center": v(40, 242.49) * mm, "radius": 9 * mm});
            skCircle(sketch, "E4.0.7.16", {"center": v(210, 259.8) * mm, "radius": 9 * mm});
            skCircle(sketch, "E4.0.7.17", {"center": v(330, 259.8) * mm, "radius": 9 * mm});
            skCircle(sketch, "E4.0.7.18", {"center": v(270, 259.8) * mm, "radius": 9 * mm});
            skCircle(sketch, "E4.0.7.19", {"center": v(440, 242.49) * mm, "radius": 9 * mm});
            skCircle(sketch, "E4.0.7.20", {"center": v(110, 259.8) * mm, "radius": 9 * mm});
            skCircle(sketch, "E4.0.7.21", {"center": v(250, 259.8) * mm, "radius": 9 * mm});
            skCircle(sketch, "E4.0.7.22", {"center": v(180, 242.49) * mm, "radius": 9 * mm});
            skCircle(sketch, "E4.0.7.23", {"center": v(430, 259.8) * mm, "radius": 9 * mm});
            skCircle(sketch, "E4.0.7.24", {"center": v(200, 242.49) * mm, "radius": 9 * mm});
            skCircle(sketch, "E4.0.7.25", {"center": v(420, 242.49) * mm, "radius": 9 * mm});
            skCircle(sketch, "E4.0.7.26", {"center": v(70, 259.8) * mm, "radius": 9 * mm});
            skCircle(sketch, "E4.0.7.27", {"center": v(390, 259.8) * mm, "radius": 9 * mm});
            skCircle(sketch, "E4.0.7.28", {"center": v(220, 242.49) * mm, "radius": 9 * mm});
            skCircle(sketch, "E4.0.7.29", {"center": v(190, 259.8) * mm, "radius": 9 * mm});
            skCircle(sketch, "E4.0.7.30", {"center": v(90, 259.8) * mm, "radius": 9 * mm});
            skCircle(sketch, "E4.0.7.31", {"center": v(230, 259.8) * mm, "radius": 9 * mm});
            skCircle(sketch, "E4.0.7.32", {"center": v(150, 259.8) * mm, "radius": 9 * mm});
            skCircle(sketch, "E4.0.7.33", {"center": v(470, 259.8) * mm, "radius": 9 * mm});
            skCircle(sketch, "E4.0.7.34", {"center": v(410, 259.8) * mm, "radius": 9 * mm});
            skCircle(sketch, "E4.0.7.35", {"center": v(50, 259.8) * mm, "radius": 9 * mm});
            skCircle(sketch, "E4.0.7.36", {"center": v(400, 242.49) * mm, "radius": 9 * mm});
            skCircle(sketch, "E4.0.7.37", {"center": v(240, 242.49) * mm, "radius": 9 * mm});
            skCircle(sketch, "E4.0.7.38", {"center": v(320, 242.49) * mm, "radius": 9 * mm});
            skCircle(sketch, "E4.0.7.39", {"center": v(370, 259.8) * mm, "radius": 9 * mm});
            skCircle(sketch, "E4.0.7.40", {"center": v(10, 259.8) * mm, "radius": 9 * mm});
            skCircle(sketch, "E4.0.7.41", {"center": v(290, 259.8) * mm, "radius": 9 * mm});
            skCircle(sketch, "E4.0.7.42", {"center": v(360, 242.49) * mm, "radius": 9 * mm});
            skCircle(sketch, "E4.0.7.43", {"center": v(460, 242.49) * mm, "radius": 9 * mm});
            skCircle(sketch, "E4.0.7.44", {"center": v(310, 259.8) * mm, "radius": 9 * mm});
            skCircle(sketch, "E4.0.7.45", {"center": v(340, 242.49) * mm, "radius": 9 * mm});
            skCircle(sketch, "E4.0.7.46", {"center": v(170, 259.8) * mm, "radius": 9 * mm});
            skCircle(sketch, "E4.0.7.47", {"center": v(20, 242.49) * mm, "radius": 9 * mm});
            skLineSegment(sketch, "E4.0.7.48", {"start": v(0, 242.49) * mm, "end": v(20, 242.49) * mm, "construction": true});
            skLineSegment(sketch, "E4.0.7.49", {"start": v(10, 259.8) * mm, "end": v(30, 259.8) * mm, "construction": true});
            skCircle(sketch, "E4.0.8.0", {"center": v(280, 277.13) * mm, "radius": 9 * mm});
            skCircle(sketch, "E4.0.8.1", {"center": v(260, 277.13) * mm, "radius": 9 * mm});
            skCircle(sketch, "E4.0.8.2", {"center": v(130, 294.45) * mm, "radius": 9 * mm});
            skCircle(sketch, "E4.0.8.3", {"center": v(60, 277.13) * mm, "radius": 9 * mm});
            skCircle(sketch, "E4.0.8.4", {"center": v(80, 277.13) * mm, "radius": 9 * mm});
            skCircle(sketch, "E4.0.8.5", {"center": v(100, 277.13) * mm, "radius": 9 * mm});
            skCircle(sketch, "E4.0.8.6", {"center": v(350, 294.45) * mm, "radius": 9 * mm});
            skCircle(sketch, "E4.0.8.7", {"center": v(0, 277.13) * mm, "radius": 9 * mm});
            skCircle(sketch, "E4.0.8.8", {"center": v(120, 277.13) * mm, "radius": 9 * mm});
            skCircle(sketch, "E4.0.8.9", {"center": v(30, 294.45) * mm, "radius": 9 * mm});
            skCircle(sketch, "E4.0.8.10", {"center": v(380, 277.13) * mm, "radius": 9 * mm});
            skCircle(sketch, "E4.0.8.11", {"center": v(140, 277.13) * mm, "radius": 9 * mm});
            skCircle(sketch, "E4.0.8.12", {"center": v(450, 294.45) * mm, "radius": 9 * mm});
            skCircle(sketch, "E4.0.8.13", {"center": v(160, 277.13) * mm, "radius": 9 * mm});
            skCircle(sketch, "E4.0.8.14", {"center": v(300, 277.13) * mm, "radius": 9 * mm});
            skCircle(sketch, "E4.0.8.15", {"center": v(40, 277.13) * mm, "radius": 9 * mm});
            skCircle(sketch, "E4.0.8.16", {"center": v(210, 294.45) * mm, "radius": 9 * mm});
            skCircle(sketch, "E4.0.8.17", {"center": v(330, 294.45) * mm, "radius": 9 * mm});
            skCircle(sketch, "E4.0.8.18", {"center": v(270, 294.45) * mm, "radius": 9 * mm});
            skCircle(sketch, "E4.0.8.19", {"center": v(440, 277.13) * mm, "radius": 9 * mm});
            skCircle(sketch, "E4.0.8.20", {"center": v(110, 294.45) * mm, "radius": 9 * mm});
            skCircle(sketch, "E4.0.8.21", {"center": v(250, 294.45) * mm, "radius": 9 * mm});
            skCircle(sketch, "E4.0.8.22", {"center": v(180, 277.13) * mm, "radius": 9 * mm});
            skCircle(sketch, "E4.0.8.23", {"center": v(430, 294.45) * mm, "radius": 9 * mm});
            skCircle(sketch, "E4.0.8.24", {"center": v(200, 277.13) * mm, "radius": 9 * mm});
            skCircle(sketch, "E4.0.8.25", {"center": v(420, 277.13) * mm, "radius": 9 * mm});
            skCircle(sketch, "E4.0.8.26", {"center": v(70, 294.45) * mm, "radius": 9 * mm});
            skCircle(sketch, "E4.0.8.27", {"center": v(390, 294.45) * mm, "radius": 9 * mm});
            skCircle(sketch, "E4.0.8.28", {"center": v(220, 277.13) * mm, "radius": 9 * mm});
            skCircle(sketch, "E4.0.8.29", {"center": v(190, 294.45) * mm, "radius": 9 * mm});
            skCircle(sketch, "E4.0.8.30", {"center": v(90, 294.45) * mm, "radius": 9 * mm});
            skCircle(sketch, "E4.0.8.31", {"center": v(230, 294.45) * mm, "radius": 9 * mm});
            skCircle(sketch, "E4.0.8.32", {"center": v(150, 294.45) * mm, "radius": 9 * mm});
            skCircle(sketch, "E4.0.8.33", {"center": v(470, 294.45) * mm, "radius": 9 * mm});
            skCircle(sketch, "E4.0.8.34", {"center": v(410, 294.45) * mm, "radius": 9 * mm});
            skCircle(sketch, "E4.0.8.35", {"center": v(50, 294.45) * mm, "radius": 9 * mm});
            skCircle(sketch, "E4.0.8.36", {"center": v(400, 277.13) * mm, "radius": 9 * mm});
            skCircle(sketch, "E4.0.8.37", {"center": v(240, 277.13) * mm, "radius": 9 * mm});
            skCircle(sketch, "E4.0.8.38", {"center": v(320, 277.13) * mm, "radius": 9 * mm});
            skCircle(sketch, "E4.0.8.39", {"center": v(370, 294.45) * mm, "radius": 9 * mm});
            skCircle(sketch, "E4.0.8.40", {"center": v(10, 294.45) * mm, "radius": 9 * mm});
            skCircle(sketch, "E4.0.8.41", {"center": v(290, 294.45) * mm, "radius": 9 * mm});
            skCircle(sketch, "E4.0.8.42", {"center": v(360, 277.13) * mm, "radius": 9 * mm});
            skCircle(sketch, "E4.0.8.43", {"center": v(460, 277.13) * mm, "radius": 9 * mm});
            skCircle(sketch, "E4.0.8.44", {"center": v(310, 294.45) * mm, "radius": 9 * mm});
            skCircle(sketch, "E4.0.8.45", {"center": v(340, 277.13) * mm, "radius": 9 * mm});
            skCircle(sketch, "E4.0.8.46", {"center": v(170, 294.45) * mm, "radius": 9 * mm});
            skCircle(sketch, "E4.0.8.47", {"center": v(20, 277.13) * mm, "radius": 9 * mm});
            skLineSegment(sketch, "E4.0.8.48", {"start": v(0, 277.13) * mm, "end": v(20, 277.13) * mm, "construction": true});
            skLineSegment(sketch, "E4.0.8.49", {"start": v(10, 294.45) * mm, "end": v(30, 294.45) * mm, "construction": true});
            skCircle(sketch, "E4.0.9.0", {"center": v(280, 311.77) * mm, "radius": 9 * mm});
            skCircle(sketch, "E4.0.9.1", {"center": v(260, 311.77) * mm, "radius": 9 * mm});
            skCircle(sketch, "E4.0.9.2", {"center": v(130, 329.09) * mm, "radius": 9 * mm});
            skCircle(sketch, "E4.0.9.3", {"center": v(60, 311.77) * mm, "radius": 9 * mm});
            skCircle(sketch, "E4.0.9.4", {"center": v(80, 311.77) * mm, "radius": 9 * mm});
            skCircle(sketch, "E4.0.9.5", {"center": v(100, 311.77) * mm, "radius": 9 * mm});
            skCircle(sketch, "E4.0.9.6", {"center": v(350, 329.09) * mm, "radius": 9 * mm});
            skCircle(sketch, "E4.0.9.7", {"center": v(0, 311.77) * mm, "radius": 9 * mm});
            skCircle(sketch, "E4.0.9.8", {"center": v(120, 311.77) * mm, "radius": 9 * mm});
            skCircle(sketch, "E4.0.9.9", {"center": v(30, 329.09) * mm, "radius": 9 * mm});
            skCircle(sketch, "E4.0.9.10", {"center": v(380, 311.77) * mm, "radius": 9 * mm});
            skCircle(sketch, "E4.0.9.11", {"center": v(140, 311.77) * mm, "radius": 9 * mm});
            skCircle(sketch, "E4.0.9.12", {"center": v(450, 329.09) * mm, "radius": 9 * mm});
            skCircle(sketch, "E4.0.9.13", {"center": v(160, 311.77) * mm, "radius": 9 * mm});
            skCircle(sketch, "E4.0.9.14", {"center": v(300, 311.77) * mm, "radius": 9 * mm});
            skCircle(sketch, "E4.0.9.15", {"center": v(40, 311.77) * mm, "radius": 9 * mm});
            skCircle(sketch, "E4.0.9.16", {"center": v(210, 329.09) * mm, "radius": 9 * mm});
            skCircle(sketch, "E4.0.9.17", {"center": v(330, 329.09) * mm, "radius": 9 * mm});
            skCircle(sketch, "E4.0.9.18", {"center": v(270, 329.09) * mm, "radius": 9 * mm});
            skCircle(sketch, "E4.0.9.19", {"center": v(440, 311.77) * mm, "radius": 9 * mm});
            skCircle(sketch, "E4.0.9.20", {"center": v(110, 329.09) * mm, "radius": 9 * mm});
            skCircle(sketch, "E4.0.9.21", {"center": v(250, 329.09) * mm, "radius": 9 * mm});
            skCircle(sketch, "E4.0.9.22", {"center": v(180, 311.77) * mm, "radius": 9 * mm});
            skCircle(sketch, "E4.0.9.23", {"center": v(430, 329.09) * mm, "radius": 9 * mm});
            skCircle(sketch, "E4.0.9.24", {"center": v(200, 311.77) * mm, "radius": 9 * mm});
            skCircle(sketch, "E4.0.9.25", {"center": v(420, 311.77) * mm, "radius": 9 * mm});
            skCircle(sketch, "E4.0.9.26", {"center": v(70, 329.09) * mm, "radius": 9 * mm});
            skCircle(sketch, "E4.0.9.27", {"center": v(390, 329.09) * mm, "radius": 9 * mm});
            skCircle(sketch, "E4.0.9.28", {"center": v(220, 311.77) * mm, "radius": 9 * mm});
            skCircle(sketch, "E4.0.9.29", {"center": v(190, 329.09) * mm, "radius": 9 * mm});
            skCircle(sketch, "E4.0.9.30", {"center": v(90, 329.09) * mm, "radius": 9 * mm});
            skCircle(sketch, "E4.0.9.31", {"center": v(230, 329.09) * mm, "radius": 9 * mm});
            skCircle(sketch, "E4.0.9.32", {"center": v(150, 329.09) * mm, "radius": 9 * mm});
            skCircle(sketch, "E4.0.9.33", {"center": v(470, 329.09) * mm, "radius": 9 * mm});
            skCircle(sketch, "E4.0.9.34", {"center": v(410, 329.09) * mm, "radius": 9 * mm});
            skCircle(sketch, "E4.0.9.35", {"center": v(50, 329.09) * mm, "radius": 9 * mm});
            skCircle(sketch, "E4.0.9.36", {"center": v(400, 311.77) * mm, "radius": 9 * mm});
            skCircle(sketch, "E4.0.9.37", {"center": v(240, 311.77) * mm, "radius": 9 * mm});
            skCircle(sketch, "E4.0.9.38", {"center": v(320, 311.77) * mm, "radius": 9 * mm});
            skCircle(sketch, "E4.0.9.39", {"center": v(370, 329.09) * mm, "radius": 9 * mm});
            skCircle(sketch, "E4.0.9.40", {"center": v(10, 329.09) * mm, "radius": 9 * mm});
            skCircle(sketch, "E4.0.9.41", {"center": v(290, 329.09) * mm, "radius": 9 * mm});
            skCircle(sketch, "E4.0.9.42", {"center": v(360, 311.77) * mm, "radius": 9 * mm});
            skCircle(sketch, "E4.0.9.43", {"center": v(460, 311.77) * mm, "radius": 9 * mm});
            skCircle(sketch, "E4.0.9.44", {"center": v(310, 329.09) * mm, "radius": 9 * mm});
            skCircle(sketch, "E4.0.9.45", {"center": v(340, 311.77) * mm, "radius": 9 * mm});
            skCircle(sketch, "E4.0.9.46", {"center": v(170, 329.09) * mm, "radius": 9 * mm});
            skCircle(sketch, "E4.0.9.47", {"center": v(20, 311.77) * mm, "radius": 9 * mm});
            skLineSegment(sketch, "E4.0.9.48", {"start": v(0, 311.77) * mm, "end": v(20, 311.77) * mm, "construction": true});
            skLineSegment(sketch, "E4.0.9.49", {"start": v(10, 329.09) * mm, "end": v(30, 329.09) * mm, "construction": true});
            skCircle(sketch, "E4.0.10.0", {"center": v(280, 346.41) * mm, "radius": 9 * mm});
            skCircle(sketch, "E4.0.10.1", {"center": v(260, 346.41) * mm, "radius": 9 * mm});
            skCircle(sketch, "E4.0.10.2", {"center": v(130, 363.73) * mm, "radius": 9 * mm});
            skCircle(sketch, "E4.0.10.3", {"center": v(60, 346.41) * mm, "radius": 9 * mm});
            skCircle(sketch, "E4.0.10.4", {"center": v(80, 346.41) * mm, "radius": 9 * mm});
            skCircle(sketch, "E4.0.10.5", {"center": v(100, 346.41) * mm, "radius": 9 * mm});
            skCircle(sketch, "E4.0.10.6", {"center": v(350, 363.73) * mm, "radius": 9 * mm});
            skCircle(sketch, "E4.0.10.7", {"center": v(0, 346.41) * mm, "radius": 9 * mm});
            skCircle(sketch, "E4.0.10.8", {"center": v(120, 346.41) * mm, "radius": 9 * mm});
            skCircle(sketch, "E4.0.10.9", {"center": v(30, 363.73) * mm, "radius": 9 * mm});
            skCircle(sketch, "E4.0.10.10", {"center": v(380, 346.41) * mm, "radius": 9 * mm});
            skCircle(sketch, "E4.0.10.11", {"center": v(140, 346.41) * mm, "radius": 9 * mm});
            skCircle(sketch, "E4.0.10.12", {"center": v(450, 363.73) * mm, "radius": 9 * mm});
            skCircle(sketch, "E4.0.10.13", {"center": v(160, 346.41) * mm, "radius": 9 * mm});
            skCircle(sketch, "E4.0.10.14", {"center": v(300, 346.41) * mm, "radius": 9 * mm});
            skCircle(sketch, "E4.0.10.15", {"center": v(40, 346.41) * mm, "radius": 9 * mm});
            skCircle(sketch, "E4.0.10.16", {"center": v(210, 363.73) * mm, "radius": 9 * mm});
            skCircle(sketch, "E4.0.10.17", {"center": v(330, 363.73) * mm, "radius": 9 * mm});
            skCircle(sketch, "E4.0.10.18", {"center": v(270, 363.73) * mm, "radius": 9 * mm});
            skCircle(sketch, "E4.0.10.19", {"center": v(440, 346.41) * mm, "radius": 9 * mm});
            skCircle(sketch, "E4.0.10.20", {"center": v(110, 363.73) * mm, "radius": 9 * mm});
            skCircle(sketch, "E4.0.10.21", {"center": v(250, 363.73) * mm, "radius": 9 * mm});
            skCircle(sketch, "E4.0.10.22", {"center": v(180, 346.41) * mm, "radius": 9 * mm});
            skCircle(sketch, "E4.0.10.23", {"center": v(430, 363.73) * mm, "radius": 9 * mm});
            skCircle(sketch, "E4.0.10.24", {"center": v(200, 346.41) * mm, "radius": 9 * mm});
            skCircle(sketch, "E4.0.10.25", {"center": v(420, 346.41) * mm, "radius": 9 * mm});
            skCircle(sketch, "E4.0.10.26", {"center": v(70, 363.73) * mm, "radius": 9 * mm});
            skCircle(sketch, "E4.0.10.27", {"center": v(390, 363.73) * mm, "radius": 9 * mm});
            skCircle(sketch, "E4.0.10.28", {"center": v(220, 346.41) * mm, "radius": 9 * mm});
            skCircle(sketch, "E4.0.10.29", {"center": v(190, 363.73) * mm, "radius": 9 * mm});
            skCircle(sketch, "E4.0.10.30", {"center": v(90, 363.73) * mm, "radius": 9 * mm});
            skCircle(sketch, "E4.0.10.31", {"center": v(230, 363.73) * mm, "radius": 9 * mm});
            skCircle(sketch, "E4.0.10.32", {"center": v(150, 363.73) * mm, "radius": 9 * mm});
            skCircle(sketch, "E4.0.10.33", {"center": v(470, 363.73) * mm, "radius": 9 * mm});
            skCircle(sketch, "E4.0.10.34", {"center": v(410, 363.73) * mm, "radius": 9 * mm});
            skCircle(sketch, "E4.0.10.35", {"center": v(50, 363.73) * mm, "radius": 9 * mm});
            skCircle(sketch, "E4.0.10.36", {"center": v(400, 346.41) * mm, "radius": 9 * mm});
            skCircle(sketch, "E4.0.10.37", {"center": v(240, 346.41) * mm, "radius": 9 * mm});
            skCircle(sketch, "E4.0.10.38", {"center": v(320, 346.41) * mm, "radius": 9 * mm});
            skCircle(sketch, "E4.0.10.39", {"center": v(370, 363.73) * mm, "radius": 9 * mm});
            skCircle(sketch, "E4.0.10.40", {"center": v(10, 363.73) * mm, "radius": 9 * mm});
            skCircle(sketch, "E4.0.10.41", {"center": v(290, 363.73) * mm, "radius": 9 * mm});
            skCircle(sketch, "E4.0.10.42", {"center": v(360, 346.41) * mm, "radius": 9 * mm});
            skCircle(sketch, "E4.0.10.43", {"center": v(460, 346.41) * mm, "radius": 9 * mm});
            skCircle(sketch, "E4.0.10.44", {"center": v(310, 363.73) * mm, "radius": 9 * mm});
            skCircle(sketch, "E4.0.10.45", {"center": v(340, 346.41) * mm, "radius": 9 * mm});
            skCircle(sketch, "E4.0.10.46", {"center": v(170, 363.73) * mm, "radius": 9 * mm});
            skCircle(sketch, "E4.0.10.47", {"center": v(20, 346.41) * mm, "radius": 9 * mm});
            skLineSegment(sketch, "E4.0.10.48", {"start": v(0, 346.41) * mm, "end": v(20, 346.41) * mm, "construction": true});
            skLineSegment(sketch, "E4.0.10.49", {"start": v(10, 363.73) * mm, "end": v(30, 363.73) * mm, "construction": true});
            skCircle(sketch, "E4.0.11.0", {"center": v(280, 381.05) * mm, "radius": 9 * mm});
            skCircle(sketch, "E4.0.11.1", {"center": v(260, 381.05) * mm, "radius": 9 * mm});
            skCircle(sketch, "E4.0.11.2", {"center": v(130, 398.37) * mm, "radius": 9 * mm});
            skCircle(sketch, "E4.0.11.3", {"center": v(60, 381.05) * mm, "radius": 9 * mm});
            skCircle(sketch, "E4.0.11.4", {"center": v(80, 381.05) * mm, "radius": 9 * mm});
            skCircle(sketch, "E4.0.11.5", {"center": v(100, 381.05) * mm, "radius": 9 * mm});
            skCircle(sketch, "E4.0.11.6", {"center": v(350, 398.37) * mm, "radius": 9 * mm});
            skCircle(sketch, "E4.0.11.7", {"center": v(0, 381.05) * mm, "radius": 9 * mm});
            skCircle(sketch, "E4.0.11.8", {"center": v(120, 381.05) * mm, "radius": 9 * mm});
            skCircle(sketch, "E4.0.11.9", {"center": v(30, 398.37) * mm, "radius": 9 * mm});
            skCircle(sketch, "E4.0.11.10", {"center": v(380, 381.05) * mm, "radius": 9 * mm});
            skCircle(sketch, "E4.0.11.11", {"center": v(140, 381.05) * mm, "radius": 9 * mm});
            skCircle(sketch, "E4.0.11.12", {"center": v(450, 398.37) * mm, "radius": 9 * mm});
            skCircle(sketch, "E4.0.11.13", {"center": v(160, 381.05) * mm, "radius": 9 * mm});
            skCircle(sketch, "E4.0.11.14", {"center": v(300, 381.05) * mm, "radius": 9 * mm});
            skCircle(sketch, "E4.0.11.15", {"center": v(40, 381.05) * mm, "radius": 9 * mm});
            skCircle(sketch, "E4.0.11.16", {"center": v(210, 398.37) * mm, "radius": 9 * mm});
            skCircle(sketch, "E4.0.11.17", {"center": v(330, 398.37) * mm, "radius": 9 * mm});
            skCircle(sketch, "E4.0.11.18", {"center": v(270, 398.37) * mm, "radius": 9 * mm});
            skCircle(sketch, "E4.0.11.19", {"center": v(440, 381.05) * mm, "radius": 9 * mm});
            skCircle(sketch, "E4.0.11.20", {"center": v(110, 398.37) * mm, "radius": 9 * mm});
            skCircle(sketch, "E4.0.11.21", {"center": v(250, 398.37) * mm, "radius": 9 * mm});
            skCircle(sketch, "E4.0.11.22", {"center": v(180, 381.05) * mm, "radius": 9 * mm});
            skCircle(sketch, "E4.0.11.23", {"center": v(430, 398.37) * mm, "radius": 9 * mm});
            skCircle(sketch, "E4.0.11.24", {"center": v(200, 381.05) * mm, "radius": 9 * mm});
            skCircle(sketch, "E4.0.11.25", {"center": v(420, 381.05) * mm, "radius": 9 * mm});
            skCircle(sketch, "E4.0.11.26", {"center": v(70, 398.37) * mm, "radius": 9 * mm});
            skCircle(sketch, "E4.0.11.27", {"center": v(390, 398.37) * mm, "radius": 9 * mm});
            skCircle(sketch, "E4.0.11.28", {"center": v(220, 381.05) * mm, "radius": 9 * mm});
            skCircle(sketch, "E4.0.11.29", {"center": v(190, 398.37) * mm, "radius": 9 * mm});
            skCircle(sketch, "E4.0.11.30", {"center": v(90, 398.37) * mm, "radius": 9 * mm});
            skCircle(sketch, "E4.0.11.31", {"center": v(230, 398.37) * mm, "radius": 9 * mm});
            skCircle(sketch, "E4.0.11.32", {"center": v(150, 398.37) * mm, "radius": 9 * mm});
            skCircle(sketch, "E4.0.11.33", {"center": v(470, 398.37) * mm, "radius": 9 * mm});
            skCircle(sketch, "E4.0.11.34", {"center": v(410, 398.37) * mm, "radius": 9 * mm});
            skCircle(sketch, "E4.0.11.35", {"center": v(50, 398.37) * mm, "radius": 9 * mm});
            skCircle(sketch, "E4.0.11.36", {"center": v(400, 381.05) * mm, "radius": 9 * mm});
            skCircle(sketch, "E4.0.11.37", {"center": v(240, 381.05) * mm, "radius": 9 * mm});
            skCircle(sketch, "E4.0.11.38", {"center": v(320, 381.05) * mm, "radius": 9 * mm});
            skCircle(sketch, "E4.0.11.39", {"center": v(370, 398.37) * mm, "radius": 9 * mm});
            skCircle(sketch, "E4.0.11.40", {"center": v(10, 398.37) * mm, "radius": 9 * mm});
            skCircle(sketch, "E4.0.11.41", {"center": v(290, 398.37) * mm, "radius": 9 * mm});
            skCircle(sketch, "E4.0.11.42", {"center": v(360, 381.05) * mm, "radius": 9 * mm});
            skCircle(sketch, "E4.0.11.43", {"center": v(460, 381.05) * mm, "radius": 9 * mm});
            skCircle(sketch, "E4.0.11.44", {"center": v(310, 398.37) * mm, "radius": 9 * mm});
            skCircle(sketch, "E4.0.11.45", {"center": v(340, 381.05) * mm, "radius": 9 * mm});
            skCircle(sketch, "E4.0.11.46", {"center": v(170, 398.37) * mm, "radius": 9 * mm});
            skCircle(sketch, "E4.0.11.47", {"center": v(20, 381.05) * mm, "radius": 9 * mm});
            skLineSegment(sketch, "E4.0.11.48", {"start": v(0, 381.05) * mm, "end": v(20, 381.05) * mm, "construction": true});
            skLineSegment(sketch, "E4.0.11.49", {"start": v(10, 398.37) * mm, "end": v(30, 398.37) * mm, "construction": true});
            skCircle(sketch, "E4.0.12.0", {"center": v(280, 415.7) * mm, "radius": 9 * mm});
            skCircle(sketch, "E4.0.12.1", {"center": v(260, 415.7) * mm, "radius": 9 * mm});
            skCircle(sketch, "E4.0.12.2", {"center": v(130, 433.01) * mm, "radius": 9 * mm});
            skCircle(sketch, "E4.0.12.3", {"center": v(60, 415.7) * mm, "radius": 9 * mm});
            skCircle(sketch, "E4.0.12.4", {"center": v(80, 415.7) * mm, "radius": 9 * mm});
            skCircle(sketch, "E4.0.12.5", {"center": v(100, 415.7) * mm, "radius": 9 * mm});
            skCircle(sketch, "E4.0.12.6", {"center": v(350, 433.01) * mm, "radius": 9 * mm});
            skCircle(sketch, "E4.0.12.7", {"center": v(0, 415.7) * mm, "radius": 9 * mm});
            skCircle(sketch, "E4.0.12.8", {"center": v(120, 415.7) * mm, "radius": 9 * mm});
            skCircle(sketch, "E4.0.12.9", {"center": v(30, 433.01) * mm, "radius": 9 * mm});
            skCircle(sketch, "E4.0.12.10", {"center": v(380, 415.7) * mm, "radius": 9 * mm});
            skCircle(sketch, "E4.0.12.11", {"center": v(140, 415.7) * mm, "radius": 9 * mm});
            skCircle(sketch, "E4.0.12.12", {"center": v(450, 433.01) * mm, "radius": 9 * mm});
            skCircle(sketch, "E4.0.12.13", {"center": v(160, 415.7) * mm, "radius": 9 * mm});
            skCircle(sketch, "E4.0.12.14", {"center": v(300, 415.7) * mm, "radius": 9 * mm});
            skCircle(sketch, "E4.0.12.15", {"center": v(40, 415.7) * mm, "radius": 9 * mm});
            skCircle(sketch, "E4.0.12.16", {"center": v(210, 433.01) * mm, "radius": 9 * mm});
            skCircle(sketch, "E4.0.12.17", {"center": v(330, 433.01) * mm, "radius": 9 * mm});
            skCircle(sketch, "E4.0.12.18", {"center": v(270, 433.01) * mm, "radius": 9 * mm});
            skCircle(sketch, "E4.0.12.19", {"center": v(440, 415.7) * mm, "radius": 9 * mm});
            skCircle(sketch, "E4.0.12.20", {"center": v(110, 433.01) * mm, "radius": 9 * mm});
            skCircle(sketch, "E4.0.12.21", {"center": v(250, 433.01) * mm, "radius": 9 * mm});
            skCircle(sketch, "E4.0.12.22", {"center": v(180, 415.7) * mm, "radius": 9 * mm});
            skCircle(sketch, "E4.0.12.23", {"center": v(430, 433.01) * mm, "radius": 9 * mm});
            skCircle(sketch, "E4.0.12.24", {"center": v(200, 415.7) * mm, "radius": 9 * mm});
            skCircle(sketch, "E4.0.12.25", {"center": v(420, 415.7) * mm, "radius": 9 * mm});
            skCircle(sketch, "E4.0.12.26", {"center": v(70, 433.01) * mm, "radius": 9 * mm});
            skCircle(sketch, "E4.0.12.27", {"center": v(390, 433.01) * mm, "radius": 9 * mm});
            skCircle(sketch, "E4.0.12.28", {"center": v(220, 415.7) * mm, "radius": 9 * mm});
            skCircle(sketch, "E4.0.12.29", {"center": v(190, 433.01) * mm, "radius": 9 * mm});
            skCircle(sketch, "E4.0.12.30", {"center": v(90, 433.01) * mm, "radius": 9 * mm});
            skCircle(sketch, "E4.0.12.31", {"center": v(230, 433.01) * mm, "radius": 9 * mm});
            skCircle(sketch, "E4.0.12.32", {"center": v(150, 433.01) * mm, "radius": 9 * mm});
            skCircle(sketch, "E4.0.12.33", {"center": v(470, 433.01) * mm, "radius": 9 * mm});
            skCircle(sketch, "E4.0.12.34", {"center": v(410, 433.01) * mm, "radius": 9 * mm});
            skCircle(sketch, "E4.0.12.35", {"center": v(50, 433.01) * mm, "radius": 9 * mm});
            skCircle(sketch, "E4.0.12.36", {"center": v(400, 415.7) * mm, "radius": 9 * mm});
            skCircle(sketch, "E4.0.12.37", {"center": v(240, 415.7) * mm, "radius": 9 * mm});
            skCircle(sketch, "E4.0.12.38", {"center": v(320, 415.7) * mm, "radius": 9 * mm});
            skCircle(sketch, "E4.0.12.39", {"center": v(370, 433.01) * mm, "radius": 9 * mm});
            skCircle(sketch, "E4.0.12.40", {"center": v(10, 433.01) * mm, "radius": 9 * mm});
            skCircle(sketch, "E4.0.12.41", {"center": v(290, 433.01) * mm, "radius": 9 * mm});
            skCircle(sketch, "E4.0.12.42", {"center": v(360, 415.7) * mm, "radius": 9 * mm});
            skCircle(sketch, "E4.0.12.43", {"center": v(460, 415.7) * mm, "radius": 9 * mm});
            skCircle(sketch, "E4.0.12.44", {"center": v(310, 433.01) * mm, "radius": 9 * mm});
            skCircle(sketch, "E4.0.12.45", {"center": v(340, 415.7) * mm, "radius": 9 * mm});
            skCircle(sketch, "E4.0.12.46", {"center": v(170, 433.01) * mm, "radius": 9 * mm});
            skCircle(sketch, "E4.0.12.47", {"center": v(20, 415.7) * mm, "radius": 9 * mm});
            skLineSegment(sketch, "E4.0.12.48", {"start": v(0, 415.7) * mm, "end": v(20, 415.7) * mm, "construction": true});
            skLineSegment(sketch, "E4.0.12.49", {"start": v(10, 433.01) * mm, "end": v(30, 433.01) * mm, "construction": true});
            skCircle(sketch, "E4.0.13.0", {"center": v(280, 450.33) * mm, "radius": 9 * mm});
            skCircle(sketch, "E4.0.13.1", {"center": v(260, 450.33) * mm, "radius": 9 * mm});
            skCircle(sketch, "E4.0.13.2", {"center": v(130, 467.65) * mm, "radius": 9 * mm});
            skCircle(sketch, "E4.0.13.3", {"center": v(60, 450.33) * mm, "radius": 9 * mm});
            skCircle(sketch, "E4.0.13.4", {"center": v(80, 450.33) * mm, "radius": 9 * mm});
            skCircle(sketch, "E4.0.13.5", {"center": v(100, 450.33) * mm, "radius": 9 * mm});
            skCircle(sketch, "E4.0.13.6", {"center": v(350, 467.65) * mm, "radius": 9 * mm});
            skCircle(sketch, "E4.0.13.7", {"center": v(0, 450.33) * mm, "radius": 9 * mm});
            skCircle(sketch, "E4.0.13.8", {"center": v(120, 450.33) * mm, "radius": 9 * mm});
            skCircle(sketch, "E4.0.13.9", {"center": v(30, 467.65) * mm, "radius": 9 * mm});
            skCircle(sketch, "E4.0.13.10", {"center": v(380, 450.33) * mm, "radius": 9 * mm});
            skCircle(sketch, "E4.0.13.11", {"center": v(140, 450.33) * mm, "radius": 9 * mm});
            skCircle(sketch, "E4.0.13.12", {"center": v(450, 467.65) * mm, "radius": 9 * mm});
            skCircle(sketch, "E4.0.13.13", {"center": v(160, 450.33) * mm, "radius": 9 * mm});
            skCircle(sketch, "E4.0.13.14", {"center": v(300, 450.33) * mm, "radius": 9 * mm});
            skCircle(sketch, "E4.0.13.15", {"center": v(40, 450.33) * mm, "radius": 9 * mm});
            skCircle(sketch, "E4.0.13.16", {"center": v(210, 467.65) * mm, "radius": 9 * mm});
            skCircle(sketch, "E4.0.13.17", {"center": v(330, 467.65) * mm, "radius": 9 * mm});
            skCircle(sketch, "E4.0.13.18", {"center": v(270, 467.65) * mm, "radius": 9 * mm});
            skCircle(sketch, "E4.0.13.19", {"center": v(440, 450.33) * mm, "radius": 9 * mm});
            skCircle(sketch, "E4.0.13.20", {"center": v(110, 467.65) * mm, "radius": 9 * mm});
            skCircle(sketch, "E4.0.13.21", {"center": v(250, 467.65) * mm, "radius": 9 * mm});
            skCircle(sketch, "E4.0.13.22", {"center": v(180, 450.33) * mm, "radius": 9 * mm});
            skCircle(sketch, "E4.0.13.23", {"center": v(430, 467.65) * mm, "radius": 9 * mm});
            skCircle(sketch, "E4.0.13.24", {"center": v(200, 450.33) * mm, "radius": 9 * mm});
            skCircle(sketch, "E4.0.13.25", {"center": v(420, 450.33) * mm, "radius": 9 * mm});
            skCircle(sketch, "E4.0.13.26", {"center": v(70, 467.65) * mm, "radius": 9 * mm});
            skCircle(sketch, "E4.0.13.27", {"center": v(390, 467.65) * mm, "radius": 9 * mm});
            skCircle(sketch, "E4.0.13.28", {"center": v(220, 450.33) * mm, "radius": 9 * mm});
            skCircle(sketch, "E4.0.13.29", {"center": v(190, 467.65) * mm, "radius": 9 * mm});
            skCircle(sketch, "E4.0.13.30", {"center": v(90, 467.65) * mm, "radius": 9 * mm});
            skCircle(sketch, "E4.0.13.31", {"center": v(230, 467.65) * mm, "radius": 9 * mm});
            skCircle(sketch, "E4.0.13.32", {"center": v(150, 467.65) * mm, "radius": 9 * mm});
            skCircle(sketch, "E4.0.13.33", {"center": v(470, 467.65) * mm, "radius": 9 * mm});
            skCircle(sketch, "E4.0.13.34", {"center": v(410, 467.65) * mm, "radius": 9 * mm});
            skCircle(sketch, "E4.0.13.35", {"center": v(50, 467.65) * mm, "radius": 9 * mm});
            skCircle(sketch, "E4.0.13.36", {"center": v(400, 450.33) * mm, "radius": 9 * mm});
            skCircle(sketch, "E4.0.13.37", {"center": v(240, 450.33) * mm, "radius": 9 * mm});
            skCircle(sketch, "E4.0.13.38", {"center": v(320, 450.33) * mm, "radius": 9 * mm});
            skCircle(sketch, "E4.0.13.39", {"center": v(370, 467.65) * mm, "radius": 9 * mm});
            skCircle(sketch, "E4.0.13.40", {"center": v(10, 467.65) * mm, "radius": 9 * mm});
            skCircle(sketch, "E4.0.13.41", {"center": v(290, 467.65) * mm, "radius": 9 * mm});
            skCircle(sketch, "E4.0.13.42", {"center": v(360, 450.33) * mm, "radius": 9 * mm});
            skCircle(sketch, "E4.0.13.43", {"center": v(460, 450.33) * mm, "radius": 9 * mm});
            skCircle(sketch, "E4.0.13.44", {"center": v(310, 467.65) * mm, "radius": 9 * mm});
            skCircle(sketch, "E4.0.13.45", {"center": v(340, 450.33) * mm, "radius": 9 * mm});
            skCircle(sketch, "E4.0.13.46", {"center": v(170, 467.65) * mm, "radius": 9 * mm});
            skCircle(sketch, "E4.0.13.47", {"center": v(20, 450.33) * mm, "radius": 9 * mm});
            skLineSegment(sketch, "E4.0.13.48", {"start": v(0, 450.33) * mm, "end": v(20, 450.33) * mm, "construction": true});
            skLineSegment(sketch, "E4.0.13.49", {"start": v(10, 467.65) * mm, "end": v(30, 467.65) * mm, "construction": true});
            skLineSegment(sketch, "E4.direction1", {"start": v(0, 0) * mm, "end": v(25, 0) * mm, "construction": true});
            skLineSegment(sketch, "E4.direction2", {"start": v(0, 0) * mm, "end": v(0, 34.64) * mm, "construction": true});
            skLineSegment(sketch, "E5.bottom", {"start": v(470, 467.65) * mm, "end": v(0, 467.65) * mm, "construction": true});
            skLineSegment(sketch, "E5.top", {"start": v(470, 0) * mm, "end": v(0, 0) * mm, "construction": true});
            skLineSegment(sketch, "E5.left", {"start": v(470, 467.65) * mm, "end": v(470, 0) * mm, "construction": true});
            skLineSegment(sketch, "E5.right", {"start": v(0, 467.65) * mm, "end": v(0, 0) * mm, "construction": true});
            skLineSegment(sketch, "E6", {"start": v(0, 0) * mm, "end": v(470, 467.65) * mm, "construction": true});
            skLineSegment(sketch, "E7", {"start": v(0, 467.65) * mm, "end": v(470, 0) * mm, "construction": true});
            skPoint(sketch, "E8", {"position": v(235, 233.83) * mm});
            skSolve(sketch);
        }
        {
            var Q0;
            Q0=qCreatedBy(makeId("Top.planeOp"),FACE);
            var sketch = newSketch(context, id + "F1", { "sketchPlane" : qUnion([Q0])});
            skLineSegment(sketch, "E9.bottom", {"start": v(-14, 503.83) * mm, "end": v(484, 503.83) * mm});
            skLineSegment(sketch, "E9.top", {"start": v(-14, -36.17) * mm, "end": v(484, -36.17) * mm});
            skLineSegment(sketch, "E9.left", {"start": v(-14, 503.83) * mm, "end": v(-14, -36.17) * mm});
            skLineSegment(sketch, "E9.right", {"start": v(484, 503.83) * mm, "end": v(484, -36.17) * mm});
            skLineSegment(sketch, "E10", {"start": v(-14, 503.83) * mm, "end": v(484, -36.17) * mm, "construction": true});
            skLineSegment(sketch, "E11", {"start": v(484, 503.83) * mm, "end": v(-14, -36.17) * mm, "construction": true});
            skPoint(sketch, "E12", {"position": v(235, 233.83) * mm});
            skSolve(sketch);
        }
        {
            var Q0;
            Q0=qSketchRegion(id+"F1",true);
            extrude(context, id + "F2", {"entities" : qUnion([Q0]), "oppositeDirection" : true, "depth" : 10 * mm});
        }
        {
            var Q0;
            Q0=qSketchRegion(id+"F0",true);
            extrude(context, id + "F3", {"entities" : qUnion([Q0]), "operationType" : NewBodyOperationType.REMOVE, "oppositeDirection" : true, "depth" : 8 * mm});
        }
        {
            var Q0;
            Q0=makeQuery(id+"F2.opExtrude","CAP_FACE",FACE,{"disambiguationData":[OSD([sQuery(id+"F1.wireOp",EDGE,"E9.bottom"),sQuery(id+"F1.wireOp",EDGE,"E9.top"),sQuery(id+"F1.wireOp",EDGE,"E9.left"),sQuery(id+"F1.wireOp",EDGE,"E9.right")])],"isStart":false});
            var sketch = newSketch(context, id + "F4", { "sketchPlane" : qUnion([Q0])});
            skLineSegment(sketch, "E13.bottom", {"start": v(-14, -12.82) * mm, "end": v(484, -12.82) * mm});
            skLineSegment(sketch, "E13.top", {"start": v(-14, -21.82) * mm, "end": v(484, -21.82) * mm});
            skLineSegment(sketch, "E13.left", {"start": v(-14, -12.82) * mm, "end": v(-14, -21.82) * mm});
            skLineSegment(sketch, "E13.right", {"start": v(484, -12.82) * mm, "end": v(484, -21.82) * mm});
            skLineSegment(sketch, "E14.0.1.0", {"start": v(-14, -47.46) * mm, "end": v(484, -47.46) * mm});
            skLineSegment(sketch, "E14.0.1.1", {"start": v(-14, -56.46) * mm, "end": v(484, -56.46) * mm});
            skLineSegment(sketch, "E14.0.1.2", {"start": v(-14, -47.46) * mm, "end": v(-14, -56.46) * mm});
            skLineSegment(sketch, "E14.0.1.3", {"start": v(484, -47.46) * mm, "end": v(484, -56.46) * mm});
            skLineSegment(sketch, "E14.0.2.0", {"start": v(-14, -82.1) * mm, "end": v(484, -82.1) * mm});
            skLineSegment(sketch, "E14.0.2.1", {"start": v(-14, -91.1) * mm, "end": v(484, -91.1) * mm});
            skLineSegment(sketch, "E14.0.2.2", {"start": v(-14, -82.1) * mm, "end": v(-14, -91.1) * mm});
            skLineSegment(sketch, "E14.0.2.3", {"start": v(484, -82.1) * mm, "end": v(484, -91.1) * mm});
            skLineSegment(sketch, "E14.0.3.0", {"start": v(-14, -116.74) * mm, "end": v(484, -116.74) * mm});
            skLineSegment(sketch, "E14.0.3.1", {"start": v(-14, -125.74) * mm, "end": v(484, -125.74) * mm});
            skLineSegment(sketch, "E14.0.3.2", {"start": v(-14, -116.74) * mm, "end": v(-14, -125.74) * mm});
            skLineSegment(sketch, "E14.0.3.3", {"start": v(484, -116.74) * mm, "end": v(484, -125.74) * mm});
            skLineSegment(sketch, "E14.0.4.0", {"start": v(-14, -151.38) * mm, "end": v(484, -151.38) * mm});
            skLineSegment(sketch, "E14.0.4.1", {"start": v(-14, -160.38) * mm, "end": v(484, -160.38) * mm});
            skLineSegment(sketch, "E14.0.4.2", {"start": v(-14, -151.38) * mm, "end": v(-14, -160.38) * mm});
            skLineSegment(sketch, "E14.0.4.3", {"start": v(484, -151.38) * mm, "end": v(484, -160.38) * mm});
            skLineSegment(sketch, "E14.0.5.0", {"start": v(-14, -186.03) * mm, "end": v(484, -186.03) * mm});
            skLineSegment(sketch, "E14.0.5.1", {"start": v(-14, -195.03) * mm, "end": v(484, -195.03) * mm});
            skLineSegment(sketch, "E14.0.5.2", {"start": v(-14, -186.03) * mm, "end": v(-14, -195.03) * mm});
            skLineSegment(sketch, "E14.0.5.3", {"start": v(484, -186.03) * mm, "end": v(484, -195.03) * mm});
            skLineSegment(sketch, "E14.0.6.0", {"start": v(-14, -220.67) * mm, "end": v(484, -220.67) * mm});
            skLineSegment(sketch, "E14.0.6.1", {"start": v(-14, -229.67) * mm, "end": v(484, -229.67) * mm});
            skLineSegment(sketch, "E14.0.6.2", {"start": v(-14, -220.67) * mm, "end": v(-14, -229.67) * mm});
            skLineSegment(sketch, "E14.0.6.3", {"start": v(484, -220.67) * mm, "end": v(484, -229.67) * mm});
            skLineSegment(sketch, "E14.0.7.0", {"start": v(-14, -255.3) * mm, "end": v(484, -255.3) * mm});
            skLineSegment(sketch, "E14.0.7.1", {"start": v(-14, -264.3) * mm, "end": v(484, -264.3) * mm});
            skLineSegment(sketch, "E14.0.7.2", {"start": v(-14, -255.3) * mm, "end": v(-14, -264.3) * mm});
            skLineSegment(sketch, "E14.0.7.3", {"start": v(484, -255.3) * mm, "end": v(484, -264.3) * mm});
            skLineSegment(sketch, "E14.0.8.0", {"start": v(-14, -289.95) * mm, "end": v(484, -289.95) * mm});
            skLineSegment(sketch, "E14.0.8.1", {"start": v(-14, -298.95) * mm, "end": v(484, -298.95) * mm});
            skLineSegment(sketch, "E14.0.8.2", {"start": v(-14, -289.95) * mm, "end": v(-14, -298.95) * mm});
            skLineSegment(sketch, "E14.0.8.3", {"start": v(484, -289.95) * mm, "end": v(484, -298.95) * mm});
            skLineSegment(sketch, "E14.0.9.0", {"start": v(-14, -324.59) * mm, "end": v(484, -324.59) * mm});
            skLineSegment(sketch, "E14.0.9.1", {"start": v(-14, -333.59) * mm, "end": v(484, -333.59) * mm});
            skLineSegment(sketch, "E14.0.9.2", {"start": v(-14, -324.59) * mm, "end": v(-14, -333.59) * mm});
            skLineSegment(sketch, "E14.0.9.3", {"start": v(484, -324.59) * mm, "end": v(484, -333.59) * mm});
            skLineSegment(sketch, "E14.0.10.0", {"start": v(-14, -359.23) * mm, "end": v(484, -359.23) * mm});
            skLineSegment(sketch, "E14.0.10.1", {"start": v(-14, -368.23) * mm, "end": v(484, -368.23) * mm});
            skLineSegment(sketch, "E14.0.10.2", {"start": v(-14, -359.23) * mm, "end": v(-14, -368.23) * mm});
            skLineSegment(sketch, "E14.0.10.3", {"start": v(484, -359.23) * mm, "end": v(484, -368.23) * mm});
            skLineSegment(sketch, "E14.0.11.0", {"start": v(-14, -393.87) * mm, "end": v(484, -393.87) * mm});
            skLineSegment(sketch, "E14.0.11.1", {"start": v(-14, -402.87) * mm, "end": v(484, -402.87) * mm});
            skLineSegment(sketch, "E14.0.11.2", {"start": v(-14, -393.87) * mm, "end": v(-14, -402.87) * mm});
            skLineSegment(sketch, "E14.0.11.3", {"start": v(484, -393.87) * mm, "end": v(484, -402.87) * mm});
            skLineSegment(sketch, "E14.0.12.0", {"start": v(-14, -428.51) * mm, "end": v(484, -428.51) * mm});
            skLineSegment(sketch, "E14.0.12.1", {"start": v(-14, -437.51) * mm, "end": v(484, -437.51) * mm});
            skLineSegment(sketch, "E14.0.12.2", {"start": v(-14, -428.51) * mm, "end": v(-14, -437.51) * mm});
            skLineSegment(sketch, "E14.0.12.3", {"start": v(484, -428.51) * mm, "end": v(484, -437.51) * mm});
            skLineSegment(sketch, "E14.0.13.0", {"start": v(-14, -463.15) * mm, "end": v(484, -463.15) * mm});
            skLineSegment(sketch, "E14.0.13.1", {"start": v(-14, -472.15) * mm, "end": v(484, -472.15) * mm});
            skLineSegment(sketch, "E14.0.13.2", {"start": v(-14, -463.15) * mm, "end": v(-14, -472.15) * mm});
            skLineSegment(sketch, "E14.0.13.3", {"start": v(484, -463.15) * mm, "end": v(484, -472.15) * mm});
            skLineSegment(sketch, "E14.0.14.0", {"start": v(-14, -497.8) * mm, "end": v(484, -497.8) * mm});
            skLineSegment(sketch, "E14.0.14.1", {"start": v(-14, -506.8) * mm, "end": v(484, -506.8) * mm});
            skLineSegment(sketch, "E14.0.14.2", {"start": v(-14, -497.8) * mm, "end": v(-14, -506.8) * mm});
            skLineSegment(sketch, "E14.0.14.3", {"start": v(484, -497.8) * mm, "end": v(484, -506.8) * mm});
            skLineSegment(sketch, "E14.direction1", {"start": v(-14, -21.82) * mm, "end": v(5, -21.82) * mm, "construction": true});
            skLineSegment(sketch, "E14.direction2", {"start": v(-14, -21.82) * mm, "end": v(-14, -56.46) * mm, "construction": true});
            skSolve(sketch);
        }
        {
            var Q0;
            Q0=qSketchRegion(id+"F4",true);
            extrude(context, id + "F5", {"entities" : qUnion([Q0]), "operationType" : NewBodyOperationType.REMOVE, "oppositeDirection" : true, "depth" : 2 * mm});
        }
        {
            var Q0;
            {var subQ0=sQuery(id+"F1.wireOp",EDGE,"E9.top");var subQ1=sQuery(id+"F1.wireOp",EDGE,"E9.left");var subQ2=sQuery(id+"F1.wireOp",EDGE,"E9.right");Q0=makeQuery(id+"F5.boolean.opBoolean","SPLIT",FACE,{"disambiguationData":[TD([makeQuery(id+"F2.opExtrude","SWEPT_FACE",FACE,{"disambiguationData":[OSD([subQ0])]})])],"derivedFrom":makeQuery(id+"F2.opExtrude","CAP_FACE",FACE,{"disambiguationData":[OSD([sQuery(id+"F1.wireOp",EDGE,"E9.bottom"),subQ0,subQ1,subQ2])],"isStart":false})});}
            var sketch = newSketch(context, id + "F6", { "sketchPlane" : qUnion([Q0])});
            skLineSegment(sketch, "E15.bottom", {"start": v(-4.5, 36.17) * mm, "end": v(4.5, 36.17) * mm});
            skLineSegment(sketch, "E15.top", {"start": v(-2.5, -5) * mm, "end": v(2.5, -5) * mm});
            skLineSegment(sketch, "E15.left", {"start": v(-4.5, 36.17) * mm, "end": v(-4.5, -3) * mm});
            skLineSegment(sketch, "E15.right", {"start": v(4.5, 36.17) * mm, "end": v(4.5, -3) * mm});
            skPoint(sketch, "E16.visualSharp", {"position": v(-4.5, -5) * mm});
            skArc(sketch, "E16.filletArc", {"start": v(-4.5, -3) * mm, "mid": v(-3.91, -4.41) * mm, "end": v(-2.5, -5) * mm});
            skPoint(sketch, "E17.visualSharp", {"position": v(4.5, -5) * mm});
            skArc(sketch, "E17.filletArc", {"start": v(2.5, -5) * mm, "mid": v(3.91, -4.41) * mm, "end": v(4.5, -3) * mm});
            skPoint(sketch, "E18.0.1.0", {"position": v(-4.5, -39.64) * mm});
            skLineSegment(sketch, "E18.0.1.1", {"start": v(4.5, 1.53) * mm, "end": v(4.5, -37.64) * mm});
            skPoint(sketch, "E18.0.1.2", {"position": v(4.5, -39.64) * mm});
            skLineSegment(sketch, "E18.0.1.3", {"start": v(-4.5, 1.53) * mm, "end": v(4.5, 1.53) * mm});
            skLineSegment(sketch, "E18.0.1.4", {"start": v(-2.5, -39.64) * mm, "end": v(2.5, -39.64) * mm});
            skLineSegment(sketch, "E18.0.1.5", {"start": v(-4.5, 1.53) * mm, "end": v(-4.5, -37.64) * mm});
            skArc(sketch, "E18.0.1.6", {"start": v(2.5, -39.64) * mm, "mid": v(3.91, -39.06) * mm, "end": v(4.5, -37.64) * mm});
            skArc(sketch, "E18.0.1.7", {"start": v(-4.5, -37.64) * mm, "mid": v(-3.91, -39.06) * mm, "end": v(-2.5, -39.64) * mm});
            skPoint(sketch, "E18.0.2.0", {"position": v(-4.5, -74.28) * mm});
            skLineSegment(sketch, "E18.0.2.1", {"start": v(4.5, -33.1) * mm, "end": v(4.5, -72.28) * mm});
            skPoint(sketch, "E18.0.2.2", {"position": v(4.5, -74.28) * mm});
            skLineSegment(sketch, "E18.0.2.3", {"start": v(-4.5, -33.1) * mm, "end": v(4.5, -33.1) * mm});
            skLineSegment(sketch, "E18.0.2.4", {"start": v(-2.5, -74.28) * mm, "end": v(2.5, -74.28) * mm});
            skLineSegment(sketch, "E18.0.2.5", {"start": v(-4.5, -33.1) * mm, "end": v(-4.5, -72.28) * mm});
            skArc(sketch, "E18.0.2.6", {"start": v(2.5, -74.28) * mm, "mid": v(3.91, -73.7) * mm, "end": v(4.5, -72.28) * mm});
            skArc(sketch, "E18.0.2.7", {"start": v(-4.5, -72.28) * mm, "mid": v(-3.91, -73.7) * mm, "end": v(-2.5, -74.28) * mm});
            skPoint(sketch, "E18.0.3.0", {"position": v(-4.5, -108.92) * mm});
            skLineSegment(sketch, "E18.0.3.1", {"start": v(4.5, -67.75) * mm, "end": v(4.5, -106.92) * mm});
            skPoint(sketch, "E18.0.3.2", {"position": v(4.5, -108.92) * mm});
            skLineSegment(sketch, "E18.0.3.3", {"start": v(-4.5, -67.75) * mm, "end": v(4.5, -67.75) * mm});
            skLineSegment(sketch, "E18.0.3.4", {"start": v(-2.5, -108.92) * mm, "end": v(2.5, -108.92) * mm});
            skLineSegment(sketch, "E18.0.3.5", {"start": v(-4.5, -67.75) * mm, "end": v(-4.5, -106.92) * mm});
            skArc(sketch, "E18.0.3.6", {"start": v(2.5, -108.92) * mm, "mid": v(3.91, -108.34) * mm, "end": v(4.5, -106.92) * mm});
            skArc(sketch, "E18.0.3.7", {"start": v(-4.5, -106.92) * mm, "mid": v(-3.91, -108.34) * mm, "end": v(-2.5, -108.92) * mm});
            skPoint(sketch, "E18.0.4.0", {"position": v(-4.5, -143.56) * mm});
            skLineSegment(sketch, "E18.0.4.1", {"start": v(4.5, -102.4) * mm, "end": v(4.5, -141.56) * mm});
            skPoint(sketch, "E18.0.4.2", {"position": v(4.5, -143.56) * mm});
            skLineSegment(sketch, "E18.0.4.3", {"start": v(-4.5, -102.4) * mm, "end": v(4.5, -102.4) * mm});
            skLineSegment(sketch, "E18.0.4.4", {"start": v(-2.5, -143.56) * mm, "end": v(2.5, -143.56) * mm});
            skLineSegment(sketch, "E18.0.4.5", {"start": v(-4.5, -102.4) * mm, "end": v(-4.5, -141.56) * mm});
            skArc(sketch, "E18.0.4.6", {"start": v(2.5, -143.56) * mm, "mid": v(3.91, -142.98) * mm, "end": v(4.5, -141.56) * mm});
            skArc(sketch, "E18.0.4.7", {"start": v(-4.5, -141.56) * mm, "mid": v(-3.91, -142.98) * mm, "end": v(-2.5, -143.56) * mm});
            skPoint(sketch, "E18.0.5.0", {"position": v(-4.5, -178.2) * mm});
            skLineSegment(sketch, "E18.0.5.1", {"start": v(4.5, -137.03) * mm, "end": v(4.5, -176.2) * mm});
            skPoint(sketch, "E18.0.5.2", {"position": v(4.5, -178.2) * mm});
            skLineSegment(sketch, "E18.0.5.3", {"start": v(-4.5, -137.03) * mm, "end": v(4.5, -137.03) * mm});
            skLineSegment(sketch, "E18.0.5.4", {"start": v(-2.5, -178.2) * mm, "end": v(2.5, -178.2) * mm});
            skLineSegment(sketch, "E18.0.5.5", {"start": v(-4.5, -137.03) * mm, "end": v(-4.5, -176.2) * mm});
            skArc(sketch, "E18.0.5.6", {"start": v(2.5, -178.2) * mm, "mid": v(3.91, -177.62) * mm, "end": v(4.5, -176.2) * mm});
            skArc(sketch, "E18.0.5.7", {"start": v(-4.5, -176.2) * mm, "mid": v(-3.91, -177.62) * mm, "end": v(-2.5, -178.2) * mm});
            skPoint(sketch, "E18.0.6.0", {"position": v(-4.5, -212.85) * mm});
            skLineSegment(sketch, "E18.0.6.1", {"start": v(4.5, -171.67) * mm, "end": v(4.5, -210.85) * mm});
            skPoint(sketch, "E18.0.6.2", {"position": v(4.5, -212.85) * mm});
            skLineSegment(sketch, "E18.0.6.3", {"start": v(-4.5, -171.67) * mm, "end": v(4.5, -171.67) * mm});
            skLineSegment(sketch, "E18.0.6.4", {"start": v(-2.5, -212.85) * mm, "end": v(2.5, -212.85) * mm});
            skLineSegment(sketch, "E18.0.6.5", {"start": v(-4.5, -171.67) * mm, "end": v(-4.5, -210.85) * mm});
            skArc(sketch, "E18.0.6.6", {"start": v(2.5, -212.85) * mm, "mid": v(3.91, -212.26) * mm, "end": v(4.5, -210.85) * mm});
            skArc(sketch, "E18.0.6.7", {"start": v(-4.5, -210.85) * mm, "mid": v(-3.91, -212.26) * mm, "end": v(-2.5, -212.85) * mm});
            skPoint(sketch, "E18.0.7.0", {"position": v(-4.5, -247.49) * mm});
            skLineSegment(sketch, "E18.0.7.1", {"start": v(4.5, -206.31) * mm, "end": v(4.5, -245.49) * mm});
            skPoint(sketch, "E18.0.7.2", {"position": v(4.5, -247.49) * mm});
            skLineSegment(sketch, "E18.0.7.3", {"start": v(-4.5, -206.31) * mm, "end": v(4.5, -206.31) * mm});
            skLineSegment(sketch, "E18.0.7.4", {"start": v(-2.5, -247.49) * mm, "end": v(2.5, -247.49) * mm});
            skLineSegment(sketch, "E18.0.7.5", {"start": v(-4.5, -206.31) * mm, "end": v(-4.5, -245.49) * mm});
            skArc(sketch, "E18.0.7.6", {"start": v(2.5, -247.49) * mm, "mid": v(3.91, -246.9) * mm, "end": v(4.5, -245.49) * mm});
            skArc(sketch, "E18.0.7.7", {"start": v(-4.5, -245.49) * mm, "mid": v(-3.91, -246.9) * mm, "end": v(-2.5, -247.49) * mm});
            skPoint(sketch, "E18.0.8.0", {"position": v(-4.5, -282.13) * mm});
            skLineSegment(sketch, "E18.0.8.1", {"start": v(4.5, -240.95) * mm, "end": v(4.5, -280.13) * mm});
            skPoint(sketch, "E18.0.8.2", {"position": v(4.5, -282.13) * mm});
            skLineSegment(sketch, "E18.0.8.3", {"start": v(-4.5, -240.95) * mm, "end": v(4.5, -240.95) * mm});
            skLineSegment(sketch, "E18.0.8.4", {"start": v(-2.5, -282.13) * mm, "end": v(2.5, -282.13) * mm});
            skLineSegment(sketch, "E18.0.8.5", {"start": v(-4.5, -240.95) * mm, "end": v(-4.5, -280.13) * mm});
            skArc(sketch, "E18.0.8.6", {"start": v(2.5, -282.13) * mm, "mid": v(3.91, -281.54) * mm, "end": v(4.5, -280.13) * mm});
            skArc(sketch, "E18.0.8.7", {"start": v(-4.5, -280.13) * mm, "mid": v(-3.91, -281.54) * mm, "end": v(-2.5, -282.13) * mm});
            skPoint(sketch, "E18.0.9.0", {"position": v(-4.5, -316.77) * mm});
            skLineSegment(sketch, "E18.0.9.1", {"start": v(4.5, -275.6) * mm, "end": v(4.5, -314.77) * mm});
            skPoint(sketch, "E18.0.9.2", {"position": v(4.5, -316.77) * mm});
            skLineSegment(sketch, "E18.0.9.3", {"start": v(-4.5, -275.6) * mm, "end": v(4.5, -275.6) * mm});
            skLineSegment(sketch, "E18.0.9.4", {"start": v(-2.5, -316.77) * mm, "end": v(2.5, -316.77) * mm});
            skLineSegment(sketch, "E18.0.9.5", {"start": v(-4.5, -275.6) * mm, "end": v(-4.5, -314.77) * mm});
            skArc(sketch, "E18.0.9.6", {"start": v(2.5, -316.77) * mm, "mid": v(3.91, -316.18) * mm, "end": v(4.5, -314.77) * mm});
            skArc(sketch, "E18.0.9.7", {"start": v(-4.5, -314.77) * mm, "mid": v(-3.91, -316.18) * mm, "end": v(-2.5, -316.77) * mm});
            skPoint(sketch, "E18.0.10.0", {"position": v(-4.5, -351.41) * mm});
            skLineSegment(sketch, "E18.0.10.1", {"start": v(4.5, -310.24) * mm, "end": v(4.5, -349.41) * mm});
            skPoint(sketch, "E18.0.10.2", {"position": v(4.5, -351.41) * mm});
            skLineSegment(sketch, "E18.0.10.3", {"start": v(-4.5, -310.24) * mm, "end": v(4.5, -310.24) * mm});
            skLineSegment(sketch, "E18.0.10.4", {"start": v(-2.5, -351.41) * mm, "end": v(2.5, -351.41) * mm});
            skLineSegment(sketch, "E18.0.10.5", {"start": v(-4.5, -310.24) * mm, "end": v(-4.5, -349.41) * mm});
            skArc(sketch, "E18.0.10.6", {"start": v(2.5, -351.41) * mm, "mid": v(3.91, -350.82) * mm, "end": v(4.5, -349.41) * mm});
            skArc(sketch, "E18.0.10.7", {"start": v(-4.5, -349.41) * mm, "mid": v(-3.91, -350.82) * mm, "end": v(-2.5, -351.41) * mm});
            skPoint(sketch, "E18.0.11.0", {"position": v(-4.5, -386.05) * mm});
            skLineSegment(sketch, "E18.0.11.1", {"start": v(4.5, -344.88) * mm, "end": v(4.5, -384.05) * mm});
            skPoint(sketch, "E18.0.11.2", {"position": v(4.5, -386.05) * mm});
            skLineSegment(sketch, "E18.0.11.3", {"start": v(-4.5, -344.88) * mm, "end": v(4.5, -344.88) * mm});
            skLineSegment(sketch, "E18.0.11.4", {"start": v(-2.5, -386.05) * mm, "end": v(2.5, -386.05) * mm});
            skLineSegment(sketch, "E18.0.11.5", {"start": v(-4.5, -344.88) * mm, "end": v(-4.5, -384.05) * mm});
            skArc(sketch, "E18.0.11.6", {"start": v(2.5, -386.05) * mm, "mid": v(3.91, -385.47) * mm, "end": v(4.5, -384.05) * mm});
            skArc(sketch, "E18.0.11.7", {"start": v(-4.5, -384.05) * mm, "mid": v(-3.91, -385.47) * mm, "end": v(-2.5, -386.05) * mm});
            skPoint(sketch, "E18.0.12.0", {"position": v(-4.5, -420.7) * mm});
            skLineSegment(sketch, "E18.0.12.1", {"start": v(4.5, -379.52) * mm, "end": v(4.5, -418.7) * mm});
            skPoint(sketch, "E18.0.12.2", {"position": v(4.5, -420.7) * mm});
            skLineSegment(sketch, "E18.0.12.3", {"start": v(-4.5, -379.52) * mm, "end": v(4.5, -379.52) * mm});
            skLineSegment(sketch, "E18.0.12.4", {"start": v(-2.5, -420.7) * mm, "end": v(2.5, -420.7) * mm});
            skLineSegment(sketch, "E18.0.12.5", {"start": v(-4.5, -379.52) * mm, "end": v(-4.5, -418.7) * mm});
            skArc(sketch, "E18.0.12.6", {"start": v(2.5, -420.7) * mm, "mid": v(3.91, -420.1) * mm, "end": v(4.5, -418.7) * mm});
            skArc(sketch, "E18.0.12.7", {"start": v(-4.5, -418.7) * mm, "mid": v(-3.91, -420.1) * mm, "end": v(-2.5, -420.7) * mm});
            skPoint(sketch, "E18.0.13.0", {"position": v(-4.5, -455.33) * mm});
            skLineSegment(sketch, "E18.0.13.1", {"start": v(4.5, -414.16) * mm, "end": v(4.5, -453.33) * mm});
            skPoint(sketch, "E18.0.13.2", {"position": v(4.5, -455.33) * mm});
            skLineSegment(sketch, "E18.0.13.3", {"start": v(-4.5, -414.16) * mm, "end": v(4.5, -414.16) * mm});
            skLineSegment(sketch, "E18.0.13.4", {"start": v(-2.5, -455.33) * mm, "end": v(2.5, -455.33) * mm});
            skLineSegment(sketch, "E18.0.13.5", {"start": v(-4.5, -414.16) * mm, "end": v(-4.5, -453.33) * mm});
            skArc(sketch, "E18.0.13.6", {"start": v(2.5, -455.33) * mm, "mid": v(3.91, -454.75) * mm, "end": v(4.5, -453.33) * mm});
            skArc(sketch, "E18.0.13.7", {"start": v(-4.5, -453.33) * mm, "mid": v(-3.91, -454.75) * mm, "end": v(-2.5, -455.33) * mm});
            skPoint(sketch, "E18.0.14.0", {"position": v(-4.5, -489.97) * mm});
            skLineSegment(sketch, "E18.0.14.1", {"start": v(4.5, -448.8) * mm, "end": v(4.5, -487.97) * mm});
            skPoint(sketch, "E18.0.14.2", {"position": v(4.5, -489.97) * mm});
            skLineSegment(sketch, "E18.0.14.3", {"start": v(-4.5, -448.8) * mm, "end": v(4.5, -448.8) * mm});
            skLineSegment(sketch, "E18.0.14.4", {"start": v(-2.5, -489.97) * mm, "end": v(2.5, -489.97) * mm});
            skLineSegment(sketch, "E18.0.14.5", {"start": v(-4.5, -448.8) * mm, "end": v(-4.5, -487.97) * mm});
            skArc(sketch, "E18.0.14.6", {"start": v(2.5, -489.97) * mm, "mid": v(3.91, -489.39) * mm, "end": v(4.5, -487.97) * mm});
            skArc(sketch, "E18.0.14.7", {"start": v(-4.5, -487.97) * mm, "mid": v(-3.91, -489.39) * mm, "end": v(-2.5, -489.97) * mm});
            skPoint(sketch, "E18.1.0.0", {"position": v(15.5, -5) * mm});
            skLineSegment(sketch, "E18.1.0.1", {"start": v(24.5, 36.17) * mm, "end": v(24.5, -3) * mm});
            skPoint(sketch, "E18.1.0.2", {"position": v(24.5, -5) * mm});
            skLineSegment(sketch, "E18.1.0.3", {"start": v(15.5, 36.17) * mm, "end": v(24.5, 36.17) * mm});
            skLineSegment(sketch, "E18.1.0.4", {"start": v(17.5, -5) * mm, "end": v(22.5, -5) * mm});
            skLineSegment(sketch, "E18.1.0.5", {"start": v(15.5, 36.17) * mm, "end": v(15.5, -3) * mm});
            skArc(sketch, "E18.1.0.6", {"start": v(22.5, -5) * mm, "mid": v(23.91, -4.41) * mm, "end": v(24.5, -3) * mm});
            skArc(sketch, "E18.1.0.7", {"start": v(15.5, -3) * mm, "mid": v(16.09, -4.41) * mm, "end": v(17.5, -5) * mm});
            skPoint(sketch, "E18.1.1.0", {"position": v(15.5, -39.64) * mm});
            skLineSegment(sketch, "E18.1.1.1", {"start": v(24.5, 1.53) * mm, "end": v(24.5, -37.64) * mm});
            skPoint(sketch, "E18.1.1.2", {"position": v(24.5, -39.64) * mm});
            skLineSegment(sketch, "E18.1.1.3", {"start": v(15.5, 1.53) * mm, "end": v(24.5, 1.53) * mm});
            skLineSegment(sketch, "E18.1.1.4", {"start": v(17.5, -39.64) * mm, "end": v(22.5, -39.64) * mm});
            skLineSegment(sketch, "E18.1.1.5", {"start": v(15.5, 1.53) * mm, "end": v(15.5, -37.64) * mm});
            skArc(sketch, "E18.1.1.6", {"start": v(22.5, -39.64) * mm, "mid": v(23.91, -39.06) * mm, "end": v(24.5, -37.64) * mm});
            skArc(sketch, "E18.1.1.7", {"start": v(15.5, -37.64) * mm, "mid": v(16.09, -39.06) * mm, "end": v(17.5, -39.64) * mm});
            skPoint(sketch, "E18.1.2.0", {"position": v(15.5, -74.28) * mm});
            skLineSegment(sketch, "E18.1.2.1", {"start": v(24.5, -33.1) * mm, "end": v(24.5, -72.28) * mm});
            skPoint(sketch, "E18.1.2.2", {"position": v(24.5, -74.28) * mm});
            skLineSegment(sketch, "E18.1.2.3", {"start": v(15.5, -33.1) * mm, "end": v(24.5, -33.1) * mm});
            skLineSegment(sketch, "E18.1.2.4", {"start": v(17.5, -74.28) * mm, "end": v(22.5, -74.28) * mm});
            skLineSegment(sketch, "E18.1.2.5", {"start": v(15.5, -33.1) * mm, "end": v(15.5, -72.28) * mm});
            skArc(sketch, "E18.1.2.6", {"start": v(22.5, -74.28) * mm, "mid": v(23.91, -73.7) * mm, "end": v(24.5, -72.28) * mm});
            skArc(sketch, "E18.1.2.7", {"start": v(15.5, -72.28) * mm, "mid": v(16.09, -73.7) * mm, "end": v(17.5, -74.28) * mm});
            skPoint(sketch, "E18.1.3.0", {"position": v(15.5, -108.92) * mm});
            skLineSegment(sketch, "E18.1.3.1", {"start": v(24.5, -67.75) * mm, "end": v(24.5, -106.92) * mm});
            skPoint(sketch, "E18.1.3.2", {"position": v(24.5, -108.92) * mm});
            skLineSegment(sketch, "E18.1.3.3", {"start": v(15.5, -67.75) * mm, "end": v(24.5, -67.75) * mm});
            skLineSegment(sketch, "E18.1.3.4", {"start": v(17.5, -108.92) * mm, "end": v(22.5, -108.92) * mm});
            skLineSegment(sketch, "E18.1.3.5", {"start": v(15.5, -67.75) * mm, "end": v(15.5, -106.92) * mm});
            skArc(sketch, "E18.1.3.6", {"start": v(22.5, -108.92) * mm, "mid": v(23.91, -108.34) * mm, "end": v(24.5, -106.92) * mm});
            skArc(sketch, "E18.1.3.7", {"start": v(15.5, -106.92) * mm, "mid": v(16.09, -108.34) * mm, "end": v(17.5, -108.92) * mm});
            skPoint(sketch, "E18.1.4.0", {"position": v(15.5, -143.56) * mm});
            skLineSegment(sketch, "E18.1.4.1", {"start": v(24.5, -102.4) * mm, "end": v(24.5, -141.56) * mm});
            skPoint(sketch, "E18.1.4.2", {"position": v(24.5, -143.56) * mm});
            skLineSegment(sketch, "E18.1.4.3", {"start": v(15.5, -102.4) * mm, "end": v(24.5, -102.4) * mm});
            skLineSegment(sketch, "E18.1.4.4", {"start": v(17.5, -143.56) * mm, "end": v(22.5, -143.56) * mm});
            skLineSegment(sketch, "E18.1.4.5", {"start": v(15.5, -102.4) * mm, "end": v(15.5, -141.56) * mm});
            skArc(sketch, "E18.1.4.6", {"start": v(22.5, -143.56) * mm, "mid": v(23.91, -142.98) * mm, "end": v(24.5, -141.56) * mm});
            skArc(sketch, "E18.1.4.7", {"start": v(15.5, -141.56) * mm, "mid": v(16.09, -142.98) * mm, "end": v(17.5, -143.56) * mm});
            skPoint(sketch, "E18.1.5.0", {"position": v(15.5, -178.2) * mm});
            skLineSegment(sketch, "E18.1.5.1", {"start": v(24.5, -137.03) * mm, "end": v(24.5, -176.2) * mm});
            skPoint(sketch, "E18.1.5.2", {"position": v(24.5, -178.2) * mm});
            skLineSegment(sketch, "E18.1.5.3", {"start": v(15.5, -137.03) * mm, "end": v(24.5, -137.03) * mm});
            skLineSegment(sketch, "E18.1.5.4", {"start": v(17.5, -178.2) * mm, "end": v(22.5, -178.2) * mm});
            skLineSegment(sketch, "E18.1.5.5", {"start": v(15.5, -137.03) * mm, "end": v(15.5, -176.2) * mm});
            skArc(sketch, "E18.1.5.6", {"start": v(22.5, -178.2) * mm, "mid": v(23.91, -177.62) * mm, "end": v(24.5, -176.2) * mm});
            skArc(sketch, "E18.1.5.7", {"start": v(15.5, -176.2) * mm, "mid": v(16.09, -177.62) * mm, "end": v(17.5, -178.2) * mm});
            skPoint(sketch, "E18.1.6.0", {"position": v(15.5, -212.85) * mm});
            skLineSegment(sketch, "E18.1.6.1", {"start": v(24.5, -171.67) * mm, "end": v(24.5, -210.85) * mm});
            skPoint(sketch, "E18.1.6.2", {"position": v(24.5, -212.85) * mm});
            skLineSegment(sketch, "E18.1.6.3", {"start": v(15.5, -171.67) * mm, "end": v(24.5, -171.67) * mm});
            skLineSegment(sketch, "E18.1.6.4", {"start": v(17.5, -212.85) * mm, "end": v(22.5, -212.85) * mm});
            skLineSegment(sketch, "E18.1.6.5", {"start": v(15.5, -171.67) * mm, "end": v(15.5, -210.85) * mm});
            skArc(sketch, "E18.1.6.6", {"start": v(22.5, -212.85) * mm, "mid": v(23.91, -212.26) * mm, "end": v(24.5, -210.85) * mm});
            skArc(sketch, "E18.1.6.7", {"start": v(15.5, -210.85) * mm, "mid": v(16.09, -212.26) * mm, "end": v(17.5, -212.85) * mm});
            skPoint(sketch, "E18.1.7.0", {"position": v(15.5, -247.49) * mm});
            skLineSegment(sketch, "E18.1.7.1", {"start": v(24.5, -206.31) * mm, "end": v(24.5, -245.49) * mm});
            skPoint(sketch, "E18.1.7.2", {"position": v(24.5, -247.49) * mm});
            skLineSegment(sketch, "E18.1.7.3", {"start": v(15.5, -206.31) * mm, "end": v(24.5, -206.31) * mm});
            skLineSegment(sketch, "E18.1.7.4", {"start": v(17.5, -247.49) * mm, "end": v(22.5, -247.49) * mm});
            skLineSegment(sketch, "E18.1.7.5", {"start": v(15.5, -206.31) * mm, "end": v(15.5, -245.49) * mm});
            skArc(sketch, "E18.1.7.6", {"start": v(22.5, -247.49) * mm, "mid": v(23.91, -246.9) * mm, "end": v(24.5, -245.49) * mm});
            skArc(sketch, "E18.1.7.7", {"start": v(15.5, -245.49) * mm, "mid": v(16.09, -246.9) * mm, "end": v(17.5, -247.49) * mm});
            skPoint(sketch, "E18.1.8.0", {"position": v(15.5, -282.13) * mm});
            skLineSegment(sketch, "E18.1.8.1", {"start": v(24.5, -240.95) * mm, "end": v(24.5, -280.13) * mm});
            skPoint(sketch, "E18.1.8.2", {"position": v(24.5, -282.13) * mm});
            skLineSegment(sketch, "E18.1.8.3", {"start": v(15.5, -240.95) * mm, "end": v(24.5, -240.95) * mm});
            skLineSegment(sketch, "E18.1.8.4", {"start": v(17.5, -282.13) * mm, "end": v(22.5, -282.13) * mm});
            skLineSegment(sketch, "E18.1.8.5", {"start": v(15.5, -240.95) * mm, "end": v(15.5, -280.13) * mm});
            skArc(sketch, "E18.1.8.6", {"start": v(22.5, -282.13) * mm, "mid": v(23.91, -281.54) * mm, "end": v(24.5, -280.13) * mm});
            skArc(sketch, "E18.1.8.7", {"start": v(15.5, -280.13) * mm, "mid": v(16.09, -281.54) * mm, "end": v(17.5, -282.13) * mm});
            skPoint(sketch, "E18.1.9.0", {"position": v(15.5, -316.77) * mm});
            skLineSegment(sketch, "E18.1.9.1", {"start": v(24.5, -275.6) * mm, "end": v(24.5, -314.77) * mm});
            skPoint(sketch, "E18.1.9.2", {"position": v(24.5, -316.77) * mm});
            skLineSegment(sketch, "E18.1.9.3", {"start": v(15.5, -275.6) * mm, "end": v(24.5, -275.6) * mm});
            skLineSegment(sketch, "E18.1.9.4", {"start": v(17.5, -316.77) * mm, "end": v(22.5, -316.77) * mm});
            skLineSegment(sketch, "E18.1.9.5", {"start": v(15.5, -275.6) * mm, "end": v(15.5, -314.77) * mm});
            skArc(sketch, "E18.1.9.6", {"start": v(22.5, -316.77) * mm, "mid": v(23.91, -316.18) * mm, "end": v(24.5, -314.77) * mm});
            skArc(sketch, "E18.1.9.7", {"start": v(15.5, -314.77) * mm, "mid": v(16.09, -316.18) * mm, "end": v(17.5, -316.77) * mm});
            skPoint(sketch, "E18.1.10.0", {"position": v(15.5, -351.41) * mm});
            skLineSegment(sketch, "E18.1.10.1", {"start": v(24.5, -310.24) * mm, "end": v(24.5, -349.41) * mm});
            skPoint(sketch, "E18.1.10.2", {"position": v(24.5, -351.41) * mm});
            skLineSegment(sketch, "E18.1.10.3", {"start": v(15.5, -310.24) * mm, "end": v(24.5, -310.24) * mm});
            skLineSegment(sketch, "E18.1.10.4", {"start": v(17.5, -351.41) * mm, "end": v(22.5, -351.41) * mm});
            skLineSegment(sketch, "E18.1.10.5", {"start": v(15.5, -310.24) * mm, "end": v(15.5, -349.41) * mm});
            skArc(sketch, "E18.1.10.6", {"start": v(22.5, -351.41) * mm, "mid": v(23.91, -350.82) * mm, "end": v(24.5, -349.41) * mm});
            skArc(sketch, "E18.1.10.7", {"start": v(15.5, -349.41) * mm, "mid": v(16.09, -350.82) * mm, "end": v(17.5, -351.41) * mm});
            skPoint(sketch, "E18.1.11.0", {"position": v(15.5, -386.05) * mm});
            skLineSegment(sketch, "E18.1.11.1", {"start": v(24.5, -344.88) * mm, "end": v(24.5, -384.05) * mm});
            skPoint(sketch, "E18.1.11.2", {"position": v(24.5, -386.05) * mm});
            skLineSegment(sketch, "E18.1.11.3", {"start": v(15.5, -344.88) * mm, "end": v(24.5, -344.88) * mm});
            skLineSegment(sketch, "E18.1.11.4", {"start": v(17.5, -386.05) * mm, "end": v(22.5, -386.05) * mm});
            skLineSegment(sketch, "E18.1.11.5", {"start": v(15.5, -344.88) * mm, "end": v(15.5, -384.05) * mm});
            skArc(sketch, "E18.1.11.6", {"start": v(22.5, -386.05) * mm, "mid": v(23.91, -385.47) * mm, "end": v(24.5, -384.05) * mm});
            skArc(sketch, "E18.1.11.7", {"start": v(15.5, -384.05) * mm, "mid": v(16.09, -385.47) * mm, "end": v(17.5, -386.05) * mm});
            skPoint(sketch, "E18.1.12.0", {"position": v(15.5, -420.7) * mm});
            skLineSegment(sketch, "E18.1.12.1", {"start": v(24.5, -379.52) * mm, "end": v(24.5, -418.7) * mm});
            skPoint(sketch, "E18.1.12.2", {"position": v(24.5, -420.7) * mm});
            skLineSegment(sketch, "E18.1.12.3", {"start": v(15.5, -379.52) * mm, "end": v(24.5, -379.52) * mm});
            skLineSegment(sketch, "E18.1.12.4", {"start": v(17.5, -420.7) * mm, "end": v(22.5, -420.7) * mm});
            skLineSegment(sketch, "E18.1.12.5", {"start": v(15.5, -379.52) * mm, "end": v(15.5, -418.7) * mm});
            skArc(sketch, "E18.1.12.6", {"start": v(22.5, -420.7) * mm, "mid": v(23.91, -420.1) * mm, "end": v(24.5, -418.7) * mm});
            skArc(sketch, "E18.1.12.7", {"start": v(15.5, -418.7) * mm, "mid": v(16.09, -420.1) * mm, "end": v(17.5, -420.7) * mm});
            skPoint(sketch, "E18.1.13.0", {"position": v(15.5, -455.33) * mm});
            skLineSegment(sketch, "E18.1.13.1", {"start": v(24.5, -414.16) * mm, "end": v(24.5, -453.33) * mm});
            skPoint(sketch, "E18.1.13.2", {"position": v(24.5, -455.33) * mm});
            skLineSegment(sketch, "E18.1.13.3", {"start": v(15.5, -414.16) * mm, "end": v(24.5, -414.16) * mm});
            skLineSegment(sketch, "E18.1.13.4", {"start": v(17.5, -455.33) * mm, "end": v(22.5, -455.33) * mm});
            skLineSegment(sketch, "E18.1.13.5", {"start": v(15.5, -414.16) * mm, "end": v(15.5, -453.33) * mm});
            skArc(sketch, "E18.1.13.6", {"start": v(22.5, -455.33) * mm, "mid": v(23.91, -454.75) * mm, "end": v(24.5, -453.33) * mm});
            skArc(sketch, "E18.1.13.7", {"start": v(15.5, -453.33) * mm, "mid": v(16.09, -454.75) * mm, "end": v(17.5, -455.33) * mm});
            skPoint(sketch, "E18.1.14.0", {"position": v(15.5, -489.97) * mm});
            skLineSegment(sketch, "E18.1.14.1", {"start": v(24.5, -448.8) * mm, "end": v(24.5, -487.97) * mm});
            skPoint(sketch, "E18.1.14.2", {"position": v(24.5, -489.97) * mm});
            skLineSegment(sketch, "E18.1.14.3", {"start": v(15.5, -448.8) * mm, "end": v(24.5, -448.8) * mm});
            skLineSegment(sketch, "E18.1.14.4", {"start": v(17.5, -489.97) * mm, "end": v(22.5, -489.97) * mm});
            skLineSegment(sketch, "E18.1.14.5", {"start": v(15.5, -448.8) * mm, "end": v(15.5, -487.97) * mm});
            skArc(sketch, "E18.1.14.6", {"start": v(22.5, -489.97) * mm, "mid": v(23.91, -489.39) * mm, "end": v(24.5, -487.97) * mm});
            skArc(sketch, "E18.1.14.7", {"start": v(15.5, -487.97) * mm, "mid": v(16.09, -489.39) * mm, "end": v(17.5, -489.97) * mm});
            skPoint(sketch, "E18.2.0.0", {"position": v(35.5, -5) * mm});
            skLineSegment(sketch, "E18.2.0.1", {"start": v(44.5, 36.17) * mm, "end": v(44.5, -3) * mm});
            skPoint(sketch, "E18.2.0.2", {"position": v(44.5, -5) * mm});
            skLineSegment(sketch, "E18.2.0.3", {"start": v(35.5, 36.17) * mm, "end": v(44.5, 36.17) * mm});
            skLineSegment(sketch, "E18.2.0.4", {"start": v(37.5, -5) * mm, "end": v(42.5, -5) * mm});
            skLineSegment(sketch, "E18.2.0.5", {"start": v(35.5, 36.17) * mm, "end": v(35.5, -3) * mm});
            skArc(sketch, "E18.2.0.6", {"start": v(42.5, -5) * mm, "mid": v(43.91, -4.41) * mm, "end": v(44.5, -3) * mm});
            skArc(sketch, "E18.2.0.7", {"start": v(35.5, -3) * mm, "mid": v(36.09, -4.41) * mm, "end": v(37.5, -5) * mm});
            skPoint(sketch, "E18.2.1.0", {"position": v(35.5, -39.64) * mm});
            skLineSegment(sketch, "E18.2.1.1", {"start": v(44.5, 1.53) * mm, "end": v(44.5, -37.64) * mm});
            skPoint(sketch, "E18.2.1.2", {"position": v(44.5, -39.64) * mm});
            skLineSegment(sketch, "E18.2.1.3", {"start": v(35.5, 1.53) * mm, "end": v(44.5, 1.53) * mm});
            skLineSegment(sketch, "E18.2.1.4", {"start": v(37.5, -39.64) * mm, "end": v(42.5, -39.64) * mm});
            skLineSegment(sketch, "E18.2.1.5", {"start": v(35.5, 1.53) * mm, "end": v(35.5, -37.64) * mm});
            skArc(sketch, "E18.2.1.6", {"start": v(42.5, -39.64) * mm, "mid": v(43.91, -39.06) * mm, "end": v(44.5, -37.64) * mm});
            skArc(sketch, "E18.2.1.7", {"start": v(35.5, -37.64) * mm, "mid": v(36.09, -39.06) * mm, "end": v(37.5, -39.64) * mm});
            skPoint(sketch, "E18.2.2.0", {"position": v(35.5, -74.28) * mm});
            skLineSegment(sketch, "E18.2.2.1", {"start": v(44.5, -33.1) * mm, "end": v(44.5, -72.28) * mm});
            skPoint(sketch, "E18.2.2.2", {"position": v(44.5, -74.28) * mm});
            skLineSegment(sketch, "E18.2.2.3", {"start": v(35.5, -33.1) * mm, "end": v(44.5, -33.1) * mm});
            skLineSegment(sketch, "E18.2.2.4", {"start": v(37.5, -74.28) * mm, "end": v(42.5, -74.28) * mm});
            skLineSegment(sketch, "E18.2.2.5", {"start": v(35.5, -33.1) * mm, "end": v(35.5, -72.28) * mm});
            skArc(sketch, "E18.2.2.6", {"start": v(42.5, -74.28) * mm, "mid": v(43.91, -73.7) * mm, "end": v(44.5, -72.28) * mm});
            skArc(sketch, "E18.2.2.7", {"start": v(35.5, -72.28) * mm, "mid": v(36.09, -73.7) * mm, "end": v(37.5, -74.28) * mm});
            skPoint(sketch, "E18.2.3.0", {"position": v(35.5, -108.92) * mm});
            skLineSegment(sketch, "E18.2.3.1", {"start": v(44.5, -67.75) * mm, "end": v(44.5, -106.92) * mm});
            skPoint(sketch, "E18.2.3.2", {"position": v(44.5, -108.92) * mm});
            skLineSegment(sketch, "E18.2.3.3", {"start": v(35.5, -67.75) * mm, "end": v(44.5, -67.75) * mm});
            skLineSegment(sketch, "E18.2.3.4", {"start": v(37.5, -108.92) * mm, "end": v(42.5, -108.92) * mm});
            skLineSegment(sketch, "E18.2.3.5", {"start": v(35.5, -67.75) * mm, "end": v(35.5, -106.92) * mm});
            skArc(sketch, "E18.2.3.6", {"start": v(42.5, -108.92) * mm, "mid": v(43.91, -108.34) * mm, "end": v(44.5, -106.92) * mm});
            skArc(sketch, "E18.2.3.7", {"start": v(35.5, -106.92) * mm, "mid": v(36.09, -108.34) * mm, "end": v(37.5, -108.92) * mm});
            skPoint(sketch, "E18.2.4.0", {"position": v(35.5, -143.56) * mm});
            skLineSegment(sketch, "E18.2.4.1", {"start": v(44.5, -102.4) * mm, "end": v(44.5, -141.56) * mm});
            skPoint(sketch, "E18.2.4.2", {"position": v(44.5, -143.56) * mm});
            skLineSegment(sketch, "E18.2.4.3", {"start": v(35.5, -102.4) * mm, "end": v(44.5, -102.4) * mm});
            skLineSegment(sketch, "E18.2.4.4", {"start": v(37.5, -143.56) * mm, "end": v(42.5, -143.56) * mm});
            skLineSegment(sketch, "E18.2.4.5", {"start": v(35.5, -102.4) * mm, "end": v(35.5, -141.56) * mm});
            skArc(sketch, "E18.2.4.6", {"start": v(42.5, -143.56) * mm, "mid": v(43.91, -142.98) * mm, "end": v(44.5, -141.56) * mm});
            skArc(sketch, "E18.2.4.7", {"start": v(35.5, -141.56) * mm, "mid": v(36.09, -142.98) * mm, "end": v(37.5, -143.56) * mm});
            skPoint(sketch, "E18.2.5.0", {"position": v(35.5, -178.2) * mm});
            skLineSegment(sketch, "E18.2.5.1", {"start": v(44.5, -137.03) * mm, "end": v(44.5, -176.2) * mm});
            skPoint(sketch, "E18.2.5.2", {"position": v(44.5, -178.2) * mm});
            skLineSegment(sketch, "E18.2.5.3", {"start": v(35.5, -137.03) * mm, "end": v(44.5, -137.03) * mm});
            skLineSegment(sketch, "E18.2.5.4", {"start": v(37.5, -178.2) * mm, "end": v(42.5, -178.2) * mm});
            skLineSegment(sketch, "E18.2.5.5", {"start": v(35.5, -137.03) * mm, "end": v(35.5, -176.2) * mm});
            skArc(sketch, "E18.2.5.6", {"start": v(42.5, -178.2) * mm, "mid": v(43.91, -177.62) * mm, "end": v(44.5, -176.2) * mm});
            skArc(sketch, "E18.2.5.7", {"start": v(35.5, -176.2) * mm, "mid": v(36.09, -177.62) * mm, "end": v(37.5, -178.2) * mm});
            skPoint(sketch, "E18.2.6.0", {"position": v(35.5, -212.85) * mm});
            skLineSegment(sketch, "E18.2.6.1", {"start": v(44.5, -171.67) * mm, "end": v(44.5, -210.85) * mm});
            skPoint(sketch, "E18.2.6.2", {"position": v(44.5, -212.85) * mm});
            skLineSegment(sketch, "E18.2.6.3", {"start": v(35.5, -171.67) * mm, "end": v(44.5, -171.67) * mm});
            skLineSegment(sketch, "E18.2.6.4", {"start": v(37.5, -212.85) * mm, "end": v(42.5, -212.85) * mm});
            skLineSegment(sketch, "E18.2.6.5", {"start": v(35.5, -171.67) * mm, "end": v(35.5, -210.85) * mm});
            skArc(sketch, "E18.2.6.6", {"start": v(42.5, -212.85) * mm, "mid": v(43.91, -212.26) * mm, "end": v(44.5, -210.85) * mm});
            skArc(sketch, "E18.2.6.7", {"start": v(35.5, -210.85) * mm, "mid": v(36.09, -212.26) * mm, "end": v(37.5, -212.85) * mm});
            skPoint(sketch, "E18.2.7.0", {"position": v(35.5, -247.49) * mm});
            skLineSegment(sketch, "E18.2.7.1", {"start": v(44.5, -206.31) * mm, "end": v(44.5, -245.49) * mm});
            skPoint(sketch, "E18.2.7.2", {"position": v(44.5, -247.49) * mm});
            skLineSegment(sketch, "E18.2.7.3", {"start": v(35.5, -206.31) * mm, "end": v(44.5, -206.31) * mm});
            skLineSegment(sketch, "E18.2.7.4", {"start": v(37.5, -247.49) * mm, "end": v(42.5, -247.49) * mm});
            skLineSegment(sketch, "E18.2.7.5", {"start": v(35.5, -206.31) * mm, "end": v(35.5, -245.49) * mm});
            skArc(sketch, "E18.2.7.6", {"start": v(42.5, -247.49) * mm, "mid": v(43.91, -246.9) * mm, "end": v(44.5, -245.49) * mm});
            skArc(sketch, "E18.2.7.7", {"start": v(35.5, -245.49) * mm, "mid": v(36.09, -246.9) * mm, "end": v(37.5, -247.49) * mm});
            skPoint(sketch, "E18.2.8.0", {"position": v(35.5, -282.13) * mm});
            skLineSegment(sketch, "E18.2.8.1", {"start": v(44.5, -240.95) * mm, "end": v(44.5, -280.13) * mm});
            skPoint(sketch, "E18.2.8.2", {"position": v(44.5, -282.13) * mm});
            skLineSegment(sketch, "E18.2.8.3", {"start": v(35.5, -240.95) * mm, "end": v(44.5, -240.95) * mm});
            skLineSegment(sketch, "E18.2.8.4", {"start": v(37.5, -282.13) * mm, "end": v(42.5, -282.13) * mm});
            skLineSegment(sketch, "E18.2.8.5", {"start": v(35.5, -240.95) * mm, "end": v(35.5, -280.13) * mm});
            skArc(sketch, "E18.2.8.6", {"start": v(42.5, -282.13) * mm, "mid": v(43.91, -281.54) * mm, "end": v(44.5, -280.13) * mm});
            skArc(sketch, "E18.2.8.7", {"start": v(35.5, -280.13) * mm, "mid": v(36.09, -281.54) * mm, "end": v(37.5, -282.13) * mm});
            skPoint(sketch, "E18.2.9.0", {"position": v(35.5, -316.77) * mm});
            skLineSegment(sketch, "E18.2.9.1", {"start": v(44.5, -275.6) * mm, "end": v(44.5, -314.77) * mm});
            skPoint(sketch, "E18.2.9.2", {"position": v(44.5, -316.77) * mm});
            skLineSegment(sketch, "E18.2.9.3", {"start": v(35.5, -275.6) * mm, "end": v(44.5, -275.6) * mm});
            skLineSegment(sketch, "E18.2.9.4", {"start": v(37.5, -316.77) * mm, "end": v(42.5, -316.77) * mm});
            skLineSegment(sketch, "E18.2.9.5", {"start": v(35.5, -275.6) * mm, "end": v(35.5, -314.77) * mm});
            skArc(sketch, "E18.2.9.6", {"start": v(42.5, -316.77) * mm, "mid": v(43.91, -316.18) * mm, "end": v(44.5, -314.77) * mm});
            skArc(sketch, "E18.2.9.7", {"start": v(35.5, -314.77) * mm, "mid": v(36.09, -316.18) * mm, "end": v(37.5, -316.77) * mm});
            skPoint(sketch, "E18.2.10.0", {"position": v(35.5, -351.41) * mm});
            skLineSegment(sketch, "E18.2.10.1", {"start": v(44.5, -310.24) * mm, "end": v(44.5, -349.41) * mm});
            skPoint(sketch, "E18.2.10.2", {"position": v(44.5, -351.41) * mm});
            skLineSegment(sketch, "E18.2.10.3", {"start": v(35.5, -310.24) * mm, "end": v(44.5, -310.24) * mm});
            skLineSegment(sketch, "E18.2.10.4", {"start": v(37.5, -351.41) * mm, "end": v(42.5, -351.41) * mm});
            skLineSegment(sketch, "E18.2.10.5", {"start": v(35.5, -310.24) * mm, "end": v(35.5, -349.41) * mm});
            skArc(sketch, "E18.2.10.6", {"start": v(42.5, -351.41) * mm, "mid": v(43.91, -350.82) * mm, "end": v(44.5, -349.41) * mm});
            skArc(sketch, "E18.2.10.7", {"start": v(35.5, -349.41) * mm, "mid": v(36.09, -350.82) * mm, "end": v(37.5, -351.41) * mm});
            skPoint(sketch, "E18.2.11.0", {"position": v(35.5, -386.05) * mm});
            skLineSegment(sketch, "E18.2.11.1", {"start": v(44.5, -344.88) * mm, "end": v(44.5, -384.05) * mm});
            skPoint(sketch, "E18.2.11.2", {"position": v(44.5, -386.05) * mm});
            skLineSegment(sketch, "E18.2.11.3", {"start": v(35.5, -344.88) * mm, "end": v(44.5, -344.88) * mm});
            skLineSegment(sketch, "E18.2.11.4", {"start": v(37.5, -386.05) * mm, "end": v(42.5, -386.05) * mm});
            skLineSegment(sketch, "E18.2.11.5", {"start": v(35.5, -344.88) * mm, "end": v(35.5, -384.05) * mm});
            skArc(sketch, "E18.2.11.6", {"start": v(42.5, -386.05) * mm, "mid": v(43.91, -385.47) * mm, "end": v(44.5, -384.05) * mm});
            skArc(sketch, "E18.2.11.7", {"start": v(35.5, -384.05) * mm, "mid": v(36.09, -385.47) * mm, "end": v(37.5, -386.05) * mm});
            skPoint(sketch, "E18.2.12.0", {"position": v(35.5, -420.7) * mm});
            skLineSegment(sketch, "E18.2.12.1", {"start": v(44.5, -379.52) * mm, "end": v(44.5, -418.7) * mm});
            skPoint(sketch, "E18.2.12.2", {"position": v(44.5, -420.7) * mm});
            skLineSegment(sketch, "E18.2.12.3", {"start": v(35.5, -379.52) * mm, "end": v(44.5, -379.52) * mm});
            skLineSegment(sketch, "E18.2.12.4", {"start": v(37.5, -420.7) * mm, "end": v(42.5, -420.7) * mm});
            skLineSegment(sketch, "E18.2.12.5", {"start": v(35.5, -379.52) * mm, "end": v(35.5, -418.7) * mm});
            skArc(sketch, "E18.2.12.6", {"start": v(42.5, -420.7) * mm, "mid": v(43.91, -420.1) * mm, "end": v(44.5, -418.7) * mm});
            skArc(sketch, "E18.2.12.7", {"start": v(35.5, -418.7) * mm, "mid": v(36.09, -420.1) * mm, "end": v(37.5, -420.7) * mm});
            skPoint(sketch, "E18.2.13.0", {"position": v(35.5, -455.33) * mm});
            skLineSegment(sketch, "E18.2.13.1", {"start": v(44.5, -414.16) * mm, "end": v(44.5, -453.33) * mm});
            skPoint(sketch, "E18.2.13.2", {"position": v(44.5, -455.33) * mm});
            skLineSegment(sketch, "E18.2.13.3", {"start": v(35.5, -414.16) * mm, "end": v(44.5, -414.16) * mm});
            skLineSegment(sketch, "E18.2.13.4", {"start": v(37.5, -455.33) * mm, "end": v(42.5, -455.33) * mm});
            skLineSegment(sketch, "E18.2.13.5", {"start": v(35.5, -414.16) * mm, "end": v(35.5, -453.33) * mm});
            skArc(sketch, "E18.2.13.6", {"start": v(42.5, -455.33) * mm, "mid": v(43.91, -454.75) * mm, "end": v(44.5, -453.33) * mm});
            skArc(sketch, "E18.2.13.7", {"start": v(35.5, -453.33) * mm, "mid": v(36.09, -454.75) * mm, "end": v(37.5, -455.33) * mm});
            skPoint(sketch, "E18.2.14.0", {"position": v(35.5, -489.97) * mm});
            skLineSegment(sketch, "E18.2.14.1", {"start": v(44.5, -448.8) * mm, "end": v(44.5, -487.97) * mm});
            skPoint(sketch, "E18.2.14.2", {"position": v(44.5, -489.97) * mm});
            skLineSegment(sketch, "E18.2.14.3", {"start": v(35.5, -448.8) * mm, "end": v(44.5, -448.8) * mm});
            skLineSegment(sketch, "E18.2.14.4", {"start": v(37.5, -489.97) * mm, "end": v(42.5, -489.97) * mm});
            skLineSegment(sketch, "E18.2.14.5", {"start": v(35.5, -448.8) * mm, "end": v(35.5, -487.97) * mm});
            skArc(sketch, "E18.2.14.6", {"start": v(42.5, -489.97) * mm, "mid": v(43.91, -489.39) * mm, "end": v(44.5, -487.97) * mm});
            skArc(sketch, "E18.2.14.7", {"start": v(35.5, -487.97) * mm, "mid": v(36.09, -489.39) * mm, "end": v(37.5, -489.97) * mm});
            skLineSegment(sketch, "E18.direction1", {"start": v(-4.5, -5) * mm, "end": v(15.5, -5) * mm, "construction": true});
            skLineSegment(sketch, "E18.direction2", {"start": v(-4.5, -5) * mm, "end": v(-4.5, -39.64) * mm, "construction": true});
            skPoint(sketch, "E19.0.3.0", {"position": v(55.5, -5) * mm});
            skLineSegment(sketch, "E19.1.3.0", {"start": v(64.5, 36.17) * mm, "end": v(64.5, -3) * mm});
            skPoint(sketch, "E19.4.3.0", {"position": v(64.5, -5) * mm});
            skLineSegment(sketch, "E19.5.3.0", {"start": v(55.5, 36.17) * mm, "end": v(64.5, 36.17) * mm});
            skLineSegment(sketch, "E19.8.3.0", {"start": v(57.5, -5) * mm, "end": v(62.5, -5) * mm});
            skLineSegment(sketch, "E19.11.3.0", {"start": v(55.5, 36.17) * mm, "end": v(55.5, -3) * mm});
            skArc(sketch, "E19.14.3.0", {"start": v(62.5, -5) * mm, "mid": v(63.91, -4.41) * mm, "end": v(64.5, -3) * mm});
            skArc(sketch, "E19.18.3.0", {"start": v(55.5, -3) * mm, "mid": v(56.09, -4.41) * mm, "end": v(57.5, -5) * mm});
            skPoint(sketch, "E19.0.3.1", {"position": v(55.5, -39.64) * mm});
            skLineSegment(sketch, "E19.1.3.1", {"start": v(64.5, 1.53) * mm, "end": v(64.5, -37.64) * mm});
            skPoint(sketch, "E19.4.3.1", {"position": v(64.5, -39.64) * mm});
            skLineSegment(sketch, "E19.5.3.1", {"start": v(55.5, 1.53) * mm, "end": v(64.5, 1.53) * mm});
            skLineSegment(sketch, "E19.8.3.1", {"start": v(57.5, -39.64) * mm, "end": v(62.5, -39.64) * mm});
            skLineSegment(sketch, "E19.11.3.1", {"start": v(55.5, 1.53) * mm, "end": v(55.5, -37.64) * mm});
            skArc(sketch, "E19.14.3.1", {"start": v(62.5, -39.64) * mm, "mid": v(63.91, -39.06) * mm, "end": v(64.5, -37.64) * mm});
            skArc(sketch, "E19.18.3.1", {"start": v(55.5, -37.64) * mm, "mid": v(56.09, -39.06) * mm, "end": v(57.5, -39.64) * mm});
            skPoint(sketch, "E19.0.3.2", {"position": v(55.5, -74.28) * mm});
            skLineSegment(sketch, "E19.1.3.2", {"start": v(64.5, -33.1) * mm, "end": v(64.5, -72.28) * mm});
            skPoint(sketch, "E19.4.3.2", {"position": v(64.5, -74.28) * mm});
            skLineSegment(sketch, "E19.5.3.2", {"start": v(55.5, -33.1) * mm, "end": v(64.5, -33.1) * mm});
            skLineSegment(sketch, "E19.8.3.2", {"start": v(57.5, -74.28) * mm, "end": v(62.5, -74.28) * mm});
            skLineSegment(sketch, "E19.11.3.2", {"start": v(55.5, -33.1) * mm, "end": v(55.5, -72.28) * mm});
            skArc(sketch, "E19.14.3.2", {"start": v(62.5, -74.28) * mm, "mid": v(63.91, -73.7) * mm, "end": v(64.5, -72.28) * mm});
            skArc(sketch, "E19.18.3.2", {"start": v(55.5, -72.28) * mm, "mid": v(56.09, -73.7) * mm, "end": v(57.5, -74.28) * mm});
            skPoint(sketch, "E19.0.3.3", {"position": v(55.5, -108.92) * mm});
            skLineSegment(sketch, "E19.1.3.3", {"start": v(64.5, -67.75) * mm, "end": v(64.5, -106.92) * mm});
            skPoint(sketch, "E19.4.3.3", {"position": v(64.5, -108.92) * mm});
            skLineSegment(sketch, "E19.5.3.3", {"start": v(55.5, -67.75) * mm, "end": v(64.5, -67.75) * mm});
            skLineSegment(sketch, "E19.8.3.3", {"start": v(57.5, -108.92) * mm, "end": v(62.5, -108.92) * mm});
            skLineSegment(sketch, "E19.11.3.3", {"start": v(55.5, -67.75) * mm, "end": v(55.5, -106.92) * mm});
            skArc(sketch, "E19.14.3.3", {"start": v(62.5, -108.92) * mm, "mid": v(63.91, -108.34) * mm, "end": v(64.5, -106.92) * mm});
            skArc(sketch, "E19.18.3.3", {"start": v(55.5, -106.92) * mm, "mid": v(56.09, -108.34) * mm, "end": v(57.5, -108.92) * mm});
            skPoint(sketch, "E19.0.3.4", {"position": v(55.5, -143.56) * mm});
            skLineSegment(sketch, "E19.1.3.4", {"start": v(64.5, -102.4) * mm, "end": v(64.5, -141.56) * mm});
            skPoint(sketch, "E19.4.3.4", {"position": v(64.5, -143.56) * mm});
            skLineSegment(sketch, "E19.5.3.4", {"start": v(55.5, -102.4) * mm, "end": v(64.5, -102.4) * mm});
            skLineSegment(sketch, "E19.8.3.4", {"start": v(57.5, -143.56) * mm, "end": v(62.5, -143.56) * mm});
            skLineSegment(sketch, "E19.11.3.4", {"start": v(55.5, -102.4) * mm, "end": v(55.5, -141.56) * mm});
            skArc(sketch, "E19.14.3.4", {"start": v(62.5, -143.56) * mm, "mid": v(63.91, -142.98) * mm, "end": v(64.5, -141.56) * mm});
            skArc(sketch, "E19.18.3.4", {"start": v(55.5, -141.56) * mm, "mid": v(56.09, -142.98) * mm, "end": v(57.5, -143.56) * mm});
            skPoint(sketch, "E19.0.3.5", {"position": v(55.5, -178.2) * mm});
            skLineSegment(sketch, "E19.1.3.5", {"start": v(64.5, -137.03) * mm, "end": v(64.5, -176.2) * mm});
            skPoint(sketch, "E19.4.3.5", {"position": v(64.5, -178.2) * mm});
            skLineSegment(sketch, "E19.5.3.5", {"start": v(55.5, -137.03) * mm, "end": v(64.5, -137.03) * mm});
            skLineSegment(sketch, "E19.8.3.5", {"start": v(57.5, -178.2) * mm, "end": v(62.5, -178.2) * mm});
            skLineSegment(sketch, "E19.11.3.5", {"start": v(55.5, -137.03) * mm, "end": v(55.5, -176.2) * mm});
            skArc(sketch, "E19.14.3.5", {"start": v(62.5, -178.2) * mm, "mid": v(63.91, -177.62) * mm, "end": v(64.5, -176.2) * mm});
            skArc(sketch, "E19.18.3.5", {"start": v(55.5, -176.2) * mm, "mid": v(56.09, -177.62) * mm, "end": v(57.5, -178.2) * mm});
            skPoint(sketch, "E19.0.3.6", {"position": v(55.5, -212.85) * mm});
            skLineSegment(sketch, "E19.1.3.6", {"start": v(64.5, -171.67) * mm, "end": v(64.5, -210.85) * mm});
            skPoint(sketch, "E19.4.3.6", {"position": v(64.5, -212.85) * mm});
            skLineSegment(sketch, "E19.5.3.6", {"start": v(55.5, -171.67) * mm, "end": v(64.5, -171.67) * mm});
            skLineSegment(sketch, "E19.8.3.6", {"start": v(57.5, -212.85) * mm, "end": v(62.5, -212.85) * mm});
            skLineSegment(sketch, "E19.11.3.6", {"start": v(55.5, -171.67) * mm, "end": v(55.5, -210.85) * mm});
            skArc(sketch, "E19.14.3.6", {"start": v(62.5, -212.85) * mm, "mid": v(63.91, -212.26) * mm, "end": v(64.5, -210.85) * mm});
            skArc(sketch, "E19.18.3.6", {"start": v(55.5, -210.85) * mm, "mid": v(56.09, -212.26) * mm, "end": v(57.5, -212.85) * mm});
            skPoint(sketch, "E19.0.3.7", {"position": v(55.5, -247.49) * mm});
            skLineSegment(sketch, "E19.1.3.7", {"start": v(64.5, -206.31) * mm, "end": v(64.5, -245.49) * mm});
            skPoint(sketch, "E19.4.3.7", {"position": v(64.5, -247.49) * mm});
            skLineSegment(sketch, "E19.5.3.7", {"start": v(55.5, -206.31) * mm, "end": v(64.5, -206.31) * mm});
            skLineSegment(sketch, "E19.8.3.7", {"start": v(57.5, -247.49) * mm, "end": v(62.5, -247.49) * mm});
            skLineSegment(sketch, "E19.11.3.7", {"start": v(55.5, -206.31) * mm, "end": v(55.5, -245.49) * mm});
            skArc(sketch, "E19.14.3.7", {"start": v(62.5, -247.49) * mm, "mid": v(63.91, -246.9) * mm, "end": v(64.5, -245.49) * mm});
            skArc(sketch, "E19.18.3.7", {"start": v(55.5, -245.49) * mm, "mid": v(56.09, -246.9) * mm, "end": v(57.5, -247.49) * mm});
            skPoint(sketch, "E19.0.3.8", {"position": v(55.5, -282.13) * mm});
            skLineSegment(sketch, "E19.1.3.8", {"start": v(64.5, -240.95) * mm, "end": v(64.5, -280.13) * mm});
            skPoint(sketch, "E19.4.3.8", {"position": v(64.5, -282.13) * mm});
            skLineSegment(sketch, "E19.5.3.8", {"start": v(55.5, -240.95) * mm, "end": v(64.5, -240.95) * mm});
            skLineSegment(sketch, "E19.8.3.8", {"start": v(57.5, -282.13) * mm, "end": v(62.5, -282.13) * mm});
            skLineSegment(sketch, "E19.11.3.8", {"start": v(55.5, -240.95) * mm, "end": v(55.5, -280.13) * mm});
            skArc(sketch, "E19.14.3.8", {"start": v(62.5, -282.13) * mm, "mid": v(63.91, -281.54) * mm, "end": v(64.5, -280.13) * mm});
            skArc(sketch, "E19.18.3.8", {"start": v(55.5, -280.13) * mm, "mid": v(56.09, -281.54) * mm, "end": v(57.5, -282.13) * mm});
            skPoint(sketch, "E19.0.3.9", {"position": v(55.5, -316.77) * mm});
            skLineSegment(sketch, "E19.1.3.9", {"start": v(64.5, -275.6) * mm, "end": v(64.5, -314.77) * mm});
            skPoint(sketch, "E19.4.3.9", {"position": v(64.5, -316.77) * mm});
            skLineSegment(sketch, "E19.5.3.9", {"start": v(55.5, -275.6) * mm, "end": v(64.5, -275.6) * mm});
            skLineSegment(sketch, "E19.8.3.9", {"start": v(57.5, -316.77) * mm, "end": v(62.5, -316.77) * mm});
            skLineSegment(sketch, "E19.11.3.9", {"start": v(55.5, -275.6) * mm, "end": v(55.5, -314.77) * mm});
            skArc(sketch, "E19.14.3.9", {"start": v(62.5, -316.77) * mm, "mid": v(63.91, -316.18) * mm, "end": v(64.5, -314.77) * mm});
            skArc(sketch, "E19.18.3.9", {"start": v(55.5, -314.77) * mm, "mid": v(56.09, -316.18) * mm, "end": v(57.5, -316.77) * mm});
            skPoint(sketch, "E19.0.3.10", {"position": v(55.5, -351.41) * mm});
            skLineSegment(sketch, "E19.1.3.10", {"start": v(64.5, -310.24) * mm, "end": v(64.5, -349.41) * mm});
            skPoint(sketch, "E19.4.3.10", {"position": v(64.5, -351.41) * mm});
            skLineSegment(sketch, "E19.5.3.10", {"start": v(55.5, -310.24) * mm, "end": v(64.5, -310.24) * mm});
            skLineSegment(sketch, "E19.8.3.10", {"start": v(57.5, -351.41) * mm, "end": v(62.5, -351.41) * mm});
            skLineSegment(sketch, "E19.11.3.10", {"start": v(55.5, -310.24) * mm, "end": v(55.5, -349.41) * mm});
            skArc(sketch, "E19.14.3.10", {"start": v(62.5, -351.41) * mm, "mid": v(63.91, -350.82) * mm, "end": v(64.5, -349.41) * mm});
            skArc(sketch, "E19.18.3.10", {"start": v(55.5, -349.41) * mm, "mid": v(56.09, -350.82) * mm, "end": v(57.5, -351.41) * mm});
            skPoint(sketch, "E19.0.3.11", {"position": v(55.5, -386.05) * mm});
            skLineSegment(sketch, "E19.1.3.11", {"start": v(64.5, -344.88) * mm, "end": v(64.5, -384.05) * mm});
            skPoint(sketch, "E19.4.3.11", {"position": v(64.5, -386.05) * mm});
            skLineSegment(sketch, "E19.5.3.11", {"start": v(55.5, -344.88) * mm, "end": v(64.5, -344.88) * mm});
            skLineSegment(sketch, "E19.8.3.11", {"start": v(57.5, -386.05) * mm, "end": v(62.5, -386.05) * mm});
            skLineSegment(sketch, "E19.11.3.11", {"start": v(55.5, -344.88) * mm, "end": v(55.5, -384.05) * mm});
            skArc(sketch, "E19.14.3.11", {"start": v(62.5, -386.05) * mm, "mid": v(63.91, -385.47) * mm, "end": v(64.5, -384.05) * mm});
            skArc(sketch, "E19.18.3.11", {"start": v(55.5, -384.05) * mm, "mid": v(56.09, -385.47) * mm, "end": v(57.5, -386.05) * mm});
            skPoint(sketch, "E19.0.3.12", {"position": v(55.5, -420.7) * mm});
            skLineSegment(sketch, "E19.1.3.12", {"start": v(64.5, -379.52) * mm, "end": v(64.5, -418.7) * mm});
            skPoint(sketch, "E19.4.3.12", {"position": v(64.5, -420.7) * mm});
            skLineSegment(sketch, "E19.5.3.12", {"start": v(55.5, -379.52) * mm, "end": v(64.5, -379.52) * mm});
            skLineSegment(sketch, "E19.8.3.12", {"start": v(57.5, -420.7) * mm, "end": v(62.5, -420.7) * mm});
            skLineSegment(sketch, "E19.11.3.12", {"start": v(55.5, -379.52) * mm, "end": v(55.5, -418.7) * mm});
            skArc(sketch, "E19.14.3.12", {"start": v(62.5, -420.7) * mm, "mid": v(63.91, -420.1) * mm, "end": v(64.5, -418.7) * mm});
            skArc(sketch, "E19.18.3.12", {"start": v(55.5, -418.7) * mm, "mid": v(56.09, -420.1) * mm, "end": v(57.5, -420.7) * mm});
            skPoint(sketch, "E19.0.3.13", {"position": v(55.5, -455.33) * mm});
            skLineSegment(sketch, "E19.1.3.13", {"start": v(64.5, -414.16) * mm, "end": v(64.5, -453.33) * mm});
            skPoint(sketch, "E19.4.3.13", {"position": v(64.5, -455.33) * mm});
            skLineSegment(sketch, "E19.5.3.13", {"start": v(55.5, -414.16) * mm, "end": v(64.5, -414.16) * mm});
            skLineSegment(sketch, "E19.8.3.13", {"start": v(57.5, -455.33) * mm, "end": v(62.5, -455.33) * mm});
            skLineSegment(sketch, "E19.11.3.13", {"start": v(55.5, -414.16) * mm, "end": v(55.5, -453.33) * mm});
            skArc(sketch, "E19.14.3.13", {"start": v(62.5, -455.33) * mm, "mid": v(63.91, -454.75) * mm, "end": v(64.5, -453.33) * mm});
            skArc(sketch, "E19.18.3.13", {"start": v(55.5, -453.33) * mm, "mid": v(56.09, -454.75) * mm, "end": v(57.5, -455.33) * mm});
            skPoint(sketch, "E19.0.3.14", {"position": v(55.5, -489.97) * mm});
            skLineSegment(sketch, "E19.1.3.14", {"start": v(64.5, -448.8) * mm, "end": v(64.5, -487.97) * mm});
            skPoint(sketch, "E19.4.3.14", {"position": v(64.5, -489.97) * mm});
            skLineSegment(sketch, "E19.5.3.14", {"start": v(55.5, -448.8) * mm, "end": v(64.5, -448.8) * mm});
            skLineSegment(sketch, "E19.8.3.14", {"start": v(57.5, -489.97) * mm, "end": v(62.5, -489.97) * mm});
            skLineSegment(sketch, "E19.11.3.14", {"start": v(55.5, -448.8) * mm, "end": v(55.5, -487.97) * mm});
            skArc(sketch, "E19.14.3.14", {"start": v(62.5, -489.97) * mm, "mid": v(63.91, -489.39) * mm, "end": v(64.5, -487.97) * mm});
            skArc(sketch, "E19.18.3.14", {"start": v(55.5, -487.97) * mm, "mid": v(56.09, -489.39) * mm, "end": v(57.5, -489.97) * mm});
            skPoint(sketch, "E19.0.4.0", {"position": v(75.5, -5) * mm});
            skLineSegment(sketch, "E19.1.4.0", {"start": v(84.5, 36.17) * mm, "end": v(84.5, -3) * mm});
            skPoint(sketch, "E19.4.4.0", {"position": v(84.5, -5) * mm});
            skLineSegment(sketch, "E19.5.4.0", {"start": v(75.5, 36.17) * mm, "end": v(84.5, 36.17) * mm});
            skLineSegment(sketch, "E19.8.4.0", {"start": v(77.5, -5) * mm, "end": v(82.5, -5) * mm});
            skLineSegment(sketch, "E19.11.4.0", {"start": v(75.5, 36.17) * mm, "end": v(75.5, -3) * mm});
            skArc(sketch, "E19.14.4.0", {"start": v(82.5, -5) * mm, "mid": v(83.91, -4.41) * mm, "end": v(84.5, -3) * mm});
            skArc(sketch, "E19.18.4.0", {"start": v(75.5, -3) * mm, "mid": v(76.09, -4.41) * mm, "end": v(77.5, -5) * mm});
            skPoint(sketch, "E19.0.4.1", {"position": v(75.5, -39.64) * mm});
            skLineSegment(sketch, "E19.1.4.1", {"start": v(84.5, 1.53) * mm, "end": v(84.5, -37.64) * mm});
            skPoint(sketch, "E19.4.4.1", {"position": v(84.5, -39.64) * mm});
            skLineSegment(sketch, "E19.5.4.1", {"start": v(75.5, 1.53) * mm, "end": v(84.5, 1.53) * mm});
            skLineSegment(sketch, "E19.8.4.1", {"start": v(77.5, -39.64) * mm, "end": v(82.5, -39.64) * mm});
            skLineSegment(sketch, "E19.11.4.1", {"start": v(75.5, 1.53) * mm, "end": v(75.5, -37.64) * mm});
            skArc(sketch, "E19.14.4.1", {"start": v(82.5, -39.64) * mm, "mid": v(83.91, -39.06) * mm, "end": v(84.5, -37.64) * mm});
            skArc(sketch, "E19.18.4.1", {"start": v(75.5, -37.64) * mm, "mid": v(76.09, -39.06) * mm, "end": v(77.5, -39.64) * mm});
            skPoint(sketch, "E19.0.4.2", {"position": v(75.5, -74.28) * mm});
            skLineSegment(sketch, "E19.1.4.2", {"start": v(84.5, -33.1) * mm, "end": v(84.5, -72.28) * mm});
            skPoint(sketch, "E19.4.4.2", {"position": v(84.5, -74.28) * mm});
            skLineSegment(sketch, "E19.5.4.2", {"start": v(75.5, -33.1) * mm, "end": v(84.5, -33.1) * mm});
            skLineSegment(sketch, "E19.8.4.2", {"start": v(77.5, -74.28) * mm, "end": v(82.5, -74.28) * mm});
            skLineSegment(sketch, "E19.11.4.2", {"start": v(75.5, -33.1) * mm, "end": v(75.5, -72.28) * mm});
            skArc(sketch, "E19.14.4.2", {"start": v(82.5, -74.28) * mm, "mid": v(83.91, -73.7) * mm, "end": v(84.5, -72.28) * mm});
            skArc(sketch, "E19.18.4.2", {"start": v(75.5, -72.28) * mm, "mid": v(76.09, -73.7) * mm, "end": v(77.5, -74.28) * mm});
            skPoint(sketch, "E19.0.4.3", {"position": v(75.5, -108.92) * mm});
            skLineSegment(sketch, "E19.1.4.3", {"start": v(84.5, -67.75) * mm, "end": v(84.5, -106.92) * mm});
            skPoint(sketch, "E19.4.4.3", {"position": v(84.5, -108.92) * mm});
            skLineSegment(sketch, "E19.5.4.3", {"start": v(75.5, -67.75) * mm, "end": v(84.5, -67.75) * mm});
            skLineSegment(sketch, "E19.8.4.3", {"start": v(77.5, -108.92) * mm, "end": v(82.5, -108.92) * mm});
            skLineSegment(sketch, "E19.11.4.3", {"start": v(75.5, -67.75) * mm, "end": v(75.5, -106.92) * mm});
            skArc(sketch, "E19.14.4.3", {"start": v(82.5, -108.92) * mm, "mid": v(83.91, -108.34) * mm, "end": v(84.5, -106.92) * mm});
            skArc(sketch, "E19.18.4.3", {"start": v(75.5, -106.92) * mm, "mid": v(76.09, -108.34) * mm, "end": v(77.5, -108.92) * mm});
            skPoint(sketch, "E19.0.4.4", {"position": v(75.5, -143.56) * mm});
            skLineSegment(sketch, "E19.1.4.4", {"start": v(84.5, -102.4) * mm, "end": v(84.5, -141.56) * mm});
            skPoint(sketch, "E19.4.4.4", {"position": v(84.5, -143.56) * mm});
            skLineSegment(sketch, "E19.5.4.4", {"start": v(75.5, -102.4) * mm, "end": v(84.5, -102.4) * mm});
            skLineSegment(sketch, "E19.8.4.4", {"start": v(77.5, -143.56) * mm, "end": v(82.5, -143.56) * mm});
            skLineSegment(sketch, "E19.11.4.4", {"start": v(75.5, -102.4) * mm, "end": v(75.5, -141.56) * mm});
            skArc(sketch, "E19.14.4.4", {"start": v(82.5, -143.56) * mm, "mid": v(83.91, -142.98) * mm, "end": v(84.5, -141.56) * mm});
            skArc(sketch, "E19.18.4.4", {"start": v(75.5, -141.56) * mm, "mid": v(76.09, -142.98) * mm, "end": v(77.5, -143.56) * mm});
            skPoint(sketch, "E19.0.4.5", {"position": v(75.5, -178.2) * mm});
            skLineSegment(sketch, "E19.1.4.5", {"start": v(84.5, -137.03) * mm, "end": v(84.5, -176.2) * mm});
            skPoint(sketch, "E19.4.4.5", {"position": v(84.5, -178.2) * mm});
            skLineSegment(sketch, "E19.5.4.5", {"start": v(75.5, -137.03) * mm, "end": v(84.5, -137.03) * mm});
            skLineSegment(sketch, "E19.8.4.5", {"start": v(77.5, -178.2) * mm, "end": v(82.5, -178.2) * mm});
            skLineSegment(sketch, "E19.11.4.5", {"start": v(75.5, -137.03) * mm, "end": v(75.5, -176.2) * mm});
            skArc(sketch, "E19.14.4.5", {"start": v(82.5, -178.2) * mm, "mid": v(83.91, -177.62) * mm, "end": v(84.5, -176.2) * mm});
            skArc(sketch, "E19.18.4.5", {"start": v(75.5, -176.2) * mm, "mid": v(76.09, -177.62) * mm, "end": v(77.5, -178.2) * mm});
            skPoint(sketch, "E19.0.4.6", {"position": v(75.5, -212.85) * mm});
            skLineSegment(sketch, "E19.1.4.6", {"start": v(84.5, -171.67) * mm, "end": v(84.5, -210.85) * mm});
            skPoint(sketch, "E19.4.4.6", {"position": v(84.5, -212.85) * mm});
            skLineSegment(sketch, "E19.5.4.6", {"start": v(75.5, -171.67) * mm, "end": v(84.5, -171.67) * mm});
            skLineSegment(sketch, "E19.8.4.6", {"start": v(77.5, -212.85) * mm, "end": v(82.5, -212.85) * mm});
            skLineSegment(sketch, "E19.11.4.6", {"start": v(75.5, -171.67) * mm, "end": v(75.5, -210.85) * mm});
            skArc(sketch, "E19.14.4.6", {"start": v(82.5, -212.85) * mm, "mid": v(83.91, -212.26) * mm, "end": v(84.5, -210.85) * mm});
            skArc(sketch, "E19.18.4.6", {"start": v(75.5, -210.85) * mm, "mid": v(76.09, -212.26) * mm, "end": v(77.5, -212.85) * mm});
            skPoint(sketch, "E19.0.4.7", {"position": v(75.5, -247.49) * mm});
            skLineSegment(sketch, "E19.1.4.7", {"start": v(84.5, -206.31) * mm, "end": v(84.5, -245.49) * mm});
            skPoint(sketch, "E19.4.4.7", {"position": v(84.5, -247.49) * mm});
            skLineSegment(sketch, "E19.5.4.7", {"start": v(75.5, -206.31) * mm, "end": v(84.5, -206.31) * mm});
            skLineSegment(sketch, "E19.8.4.7", {"start": v(77.5, -247.49) * mm, "end": v(82.5, -247.49) * mm});
            skLineSegment(sketch, "E19.11.4.7", {"start": v(75.5, -206.31) * mm, "end": v(75.5, -245.49) * mm});
            skArc(sketch, "E19.14.4.7", {"start": v(82.5, -247.49) * mm, "mid": v(83.91, -246.9) * mm, "end": v(84.5, -245.49) * mm});
            skArc(sketch, "E19.18.4.7", {"start": v(75.5, -245.49) * mm, "mid": v(76.09, -246.9) * mm, "end": v(77.5, -247.49) * mm});
            skPoint(sketch, "E19.0.4.8", {"position": v(75.5, -282.13) * mm});
            skLineSegment(sketch, "E19.1.4.8", {"start": v(84.5, -240.95) * mm, "end": v(84.5, -280.13) * mm});
            skPoint(sketch, "E19.4.4.8", {"position": v(84.5, -282.13) * mm});
            skLineSegment(sketch, "E19.5.4.8", {"start": v(75.5, -240.95) * mm, "end": v(84.5, -240.95) * mm});
            skLineSegment(sketch, "E19.8.4.8", {"start": v(77.5, -282.13) * mm, "end": v(82.5, -282.13) * mm});
            skLineSegment(sketch, "E19.11.4.8", {"start": v(75.5, -240.95) * mm, "end": v(75.5, -280.13) * mm});
            skArc(sketch, "E19.14.4.8", {"start": v(82.5, -282.13) * mm, "mid": v(83.91, -281.54) * mm, "end": v(84.5, -280.13) * mm});
            skArc(sketch, "E19.18.4.8", {"start": v(75.5, -280.13) * mm, "mid": v(76.09, -281.54) * mm, "end": v(77.5, -282.13) * mm});
            skPoint(sketch, "E19.0.4.9", {"position": v(75.5, -316.77) * mm});
            skLineSegment(sketch, "E19.1.4.9", {"start": v(84.5, -275.6) * mm, "end": v(84.5, -314.77) * mm});
            skPoint(sketch, "E19.4.4.9", {"position": v(84.5, -316.77) * mm});
            skLineSegment(sketch, "E19.5.4.9", {"start": v(75.5, -275.6) * mm, "end": v(84.5, -275.6) * mm});
            skLineSegment(sketch, "E19.8.4.9", {"start": v(77.5, -316.77) * mm, "end": v(82.5, -316.77) * mm});
            skLineSegment(sketch, "E19.11.4.9", {"start": v(75.5, -275.6) * mm, "end": v(75.5, -314.77) * mm});
            skArc(sketch, "E19.14.4.9", {"start": v(82.5, -316.77) * mm, "mid": v(83.91, -316.18) * mm, "end": v(84.5, -314.77) * mm});
            skArc(sketch, "E19.18.4.9", {"start": v(75.5, -314.77) * mm, "mid": v(76.09, -316.18) * mm, "end": v(77.5, -316.77) * mm});
            skPoint(sketch, "E19.0.4.10", {"position": v(75.5, -351.41) * mm});
            skLineSegment(sketch, "E19.1.4.10", {"start": v(84.5, -310.24) * mm, "end": v(84.5, -349.41) * mm});
            skPoint(sketch, "E19.4.4.10", {"position": v(84.5, -351.41) * mm});
            skLineSegment(sketch, "E19.5.4.10", {"start": v(75.5, -310.24) * mm, "end": v(84.5, -310.24) * mm});
            skLineSegment(sketch, "E19.8.4.10", {"start": v(77.5, -351.41) * mm, "end": v(82.5, -351.41) * mm});
            skLineSegment(sketch, "E19.11.4.10", {"start": v(75.5, -310.24) * mm, "end": v(75.5, -349.41) * mm});
            skArc(sketch, "E19.14.4.10", {"start": v(82.5, -351.41) * mm, "mid": v(83.91, -350.82) * mm, "end": v(84.5, -349.41) * mm});
            skArc(sketch, "E19.18.4.10", {"start": v(75.5, -349.41) * mm, "mid": v(76.09, -350.82) * mm, "end": v(77.5, -351.41) * mm});
            skPoint(sketch, "E19.0.4.11", {"position": v(75.5, -386.05) * mm});
            skLineSegment(sketch, "E19.1.4.11", {"start": v(84.5, -344.88) * mm, "end": v(84.5, -384.05) * mm});
            skPoint(sketch, "E19.4.4.11", {"position": v(84.5, -386.05) * mm});
            skLineSegment(sketch, "E19.5.4.11", {"start": v(75.5, -344.88) * mm, "end": v(84.5, -344.88) * mm});
            skLineSegment(sketch, "E19.8.4.11", {"start": v(77.5, -386.05) * mm, "end": v(82.5, -386.05) * mm});
            skLineSegment(sketch, "E19.11.4.11", {"start": v(75.5, -344.88) * mm, "end": v(75.5, -384.05) * mm});
            skArc(sketch, "E19.14.4.11", {"start": v(82.5, -386.05) * mm, "mid": v(83.91, -385.47) * mm, "end": v(84.5, -384.05) * mm});
            skArc(sketch, "E19.18.4.11", {"start": v(75.5, -384.05) * mm, "mid": v(76.09, -385.47) * mm, "end": v(77.5, -386.05) * mm});
            skPoint(sketch, "E19.0.4.12", {"position": v(75.5, -420.7) * mm});
            skLineSegment(sketch, "E19.1.4.12", {"start": v(84.5, -379.52) * mm, "end": v(84.5, -418.7) * mm});
            skPoint(sketch, "E19.4.4.12", {"position": v(84.5, -420.7) * mm});
            skLineSegment(sketch, "E19.5.4.12", {"start": v(75.5, -379.52) * mm, "end": v(84.5, -379.52) * mm});
            skLineSegment(sketch, "E19.8.4.12", {"start": v(77.5, -420.7) * mm, "end": v(82.5, -420.7) * mm});
            skLineSegment(sketch, "E19.11.4.12", {"start": v(75.5, -379.52) * mm, "end": v(75.5, -418.7) * mm});
            skArc(sketch, "E19.14.4.12", {"start": v(82.5, -420.7) * mm, "mid": v(83.91, -420.1) * mm, "end": v(84.5, -418.7) * mm});
            skArc(sketch, "E19.18.4.12", {"start": v(75.5, -418.7) * mm, "mid": v(76.09, -420.1) * mm, "end": v(77.5, -420.7) * mm});
            skPoint(sketch, "E19.0.4.13", {"position": v(75.5, -455.33) * mm});
            skLineSegment(sketch, "E19.1.4.13", {"start": v(84.5, -414.16) * mm, "end": v(84.5, -453.33) * mm});
            skPoint(sketch, "E19.4.4.13", {"position": v(84.5, -455.33) * mm});
            skLineSegment(sketch, "E19.5.4.13", {"start": v(75.5, -414.16) * mm, "end": v(84.5, -414.16) * mm});
            skLineSegment(sketch, "E19.8.4.13", {"start": v(77.5, -455.33) * mm, "end": v(82.5, -455.33) * mm});
            skLineSegment(sketch, "E19.11.4.13", {"start": v(75.5, -414.16) * mm, "end": v(75.5, -453.33) * mm});
            skArc(sketch, "E19.14.4.13", {"start": v(82.5, -455.33) * mm, "mid": v(83.91, -454.75) * mm, "end": v(84.5, -453.33) * mm});
            skArc(sketch, "E19.18.4.13", {"start": v(75.5, -453.33) * mm, "mid": v(76.09, -454.75) * mm, "end": v(77.5, -455.33) * mm});
            skPoint(sketch, "E19.0.4.14", {"position": v(75.5, -489.97) * mm});
            skLineSegment(sketch, "E19.1.4.14", {"start": v(84.5, -448.8) * mm, "end": v(84.5, -487.97) * mm});
            skPoint(sketch, "E19.4.4.14", {"position": v(84.5, -489.97) * mm});
            skLineSegment(sketch, "E19.5.4.14", {"start": v(75.5, -448.8) * mm, "end": v(84.5, -448.8) * mm});
            skLineSegment(sketch, "E19.8.4.14", {"start": v(77.5, -489.97) * mm, "end": v(82.5, -489.97) * mm});
            skLineSegment(sketch, "E19.11.4.14", {"start": v(75.5, -448.8) * mm, "end": v(75.5, -487.97) * mm});
            skArc(sketch, "E19.14.4.14", {"start": v(82.5, -489.97) * mm, "mid": v(83.91, -489.39) * mm, "end": v(84.5, -487.97) * mm});
            skArc(sketch, "E19.18.4.14", {"start": v(75.5, -487.97) * mm, "mid": v(76.09, -489.39) * mm, "end": v(77.5, -489.97) * mm});
            skPoint(sketch, "E19.0.5.0", {"position": v(95.5, -5) * mm});
            skLineSegment(sketch, "E19.1.5.0", {"start": v(104.5, 36.17) * mm, "end": v(104.5, -3) * mm});
            skPoint(sketch, "E19.4.5.0", {"position": v(104.5, -5) * mm});
            skLineSegment(sketch, "E19.5.5.0", {"start": v(95.5, 36.17) * mm, "end": v(104.5, 36.17) * mm});
            skLineSegment(sketch, "E19.8.5.0", {"start": v(97.5, -5) * mm, "end": v(102.5, -5) * mm});
            skLineSegment(sketch, "E19.11.5.0", {"start": v(95.5, 36.17) * mm, "end": v(95.5, -3) * mm});
            skArc(sketch, "E19.14.5.0", {"start": v(102.5, -5) * mm, "mid": v(103.91, -4.41) * mm, "end": v(104.5, -3) * mm});
            skArc(sketch, "E19.18.5.0", {"start": v(95.5, -3) * mm, "mid": v(96.09, -4.41) * mm, "end": v(97.5, -5) * mm});
            skPoint(sketch, "E19.0.5.1", {"position": v(95.5, -39.64) * mm});
            skLineSegment(sketch, "E19.1.5.1", {"start": v(104.5, 1.53) * mm, "end": v(104.5, -37.64) * mm});
            skPoint(sketch, "E19.4.5.1", {"position": v(104.5, -39.64) * mm});
            skLineSegment(sketch, "E19.5.5.1", {"start": v(95.5, 1.53) * mm, "end": v(104.5, 1.53) * mm});
            skLineSegment(sketch, "E19.8.5.1", {"start": v(97.5, -39.64) * mm, "end": v(102.5, -39.64) * mm});
            skLineSegment(sketch, "E19.11.5.1", {"start": v(95.5, 1.53) * mm, "end": v(95.5, -37.64) * mm});
            skArc(sketch, "E19.14.5.1", {"start": v(102.5, -39.64) * mm, "mid": v(103.91, -39.06) * mm, "end": v(104.5, -37.64) * mm});
            skArc(sketch, "E19.18.5.1", {"start": v(95.5, -37.64) * mm, "mid": v(96.09, -39.06) * mm, "end": v(97.5, -39.64) * mm});
            skPoint(sketch, "E19.0.5.2", {"position": v(95.5, -74.28) * mm});
            skLineSegment(sketch, "E19.1.5.2", {"start": v(104.5, -33.1) * mm, "end": v(104.5, -72.28) * mm});
            skPoint(sketch, "E19.4.5.2", {"position": v(104.5, -74.28) * mm});
            skLineSegment(sketch, "E19.5.5.2", {"start": v(95.5, -33.1) * mm, "end": v(104.5, -33.1) * mm});
            skLineSegment(sketch, "E19.8.5.2", {"start": v(97.5, -74.28) * mm, "end": v(102.5, -74.28) * mm});
            skLineSegment(sketch, "E19.11.5.2", {"start": v(95.5, -33.1) * mm, "end": v(95.5, -72.28) * mm});
            skArc(sketch, "E19.14.5.2", {"start": v(102.5, -74.28) * mm, "mid": v(103.91, -73.7) * mm, "end": v(104.5, -72.28) * mm});
            skArc(sketch, "E19.18.5.2", {"start": v(95.5, -72.28) * mm, "mid": v(96.09, -73.7) * mm, "end": v(97.5, -74.28) * mm});
            skPoint(sketch, "E19.0.5.3", {"position": v(95.5, -108.92) * mm});
            skLineSegment(sketch, "E19.1.5.3", {"start": v(104.5, -67.75) * mm, "end": v(104.5, -106.92) * mm});
            skPoint(sketch, "E19.4.5.3", {"position": v(104.5, -108.92) * mm});
            skLineSegment(sketch, "E19.5.5.3", {"start": v(95.5, -67.75) * mm, "end": v(104.5, -67.75) * mm});
            skLineSegment(sketch, "E19.8.5.3", {"start": v(97.5, -108.92) * mm, "end": v(102.5, -108.92) * mm});
            skLineSegment(sketch, "E19.11.5.3", {"start": v(95.5, -67.75) * mm, "end": v(95.5, -106.92) * mm});
            skArc(sketch, "E19.14.5.3", {"start": v(102.5, -108.92) * mm, "mid": v(103.91, -108.34) * mm, "end": v(104.5, -106.92) * mm});
            skArc(sketch, "E19.18.5.3", {"start": v(95.5, -106.92) * mm, "mid": v(96.09, -108.34) * mm, "end": v(97.5, -108.92) * mm});
            skPoint(sketch, "E19.0.5.4", {"position": v(95.5, -143.56) * mm});
            skLineSegment(sketch, "E19.1.5.4", {"start": v(104.5, -102.4) * mm, "end": v(104.5, -141.56) * mm});
            skPoint(sketch, "E19.4.5.4", {"position": v(104.5, -143.56) * mm});
            skLineSegment(sketch, "E19.5.5.4", {"start": v(95.5, -102.4) * mm, "end": v(104.5, -102.4) * mm});
            skLineSegment(sketch, "E19.8.5.4", {"start": v(97.5, -143.56) * mm, "end": v(102.5, -143.56) * mm});
            skLineSegment(sketch, "E19.11.5.4", {"start": v(95.5, -102.4) * mm, "end": v(95.5, -141.56) * mm});
            skArc(sketch, "E19.14.5.4", {"start": v(102.5, -143.56) * mm, "mid": v(103.91, -142.98) * mm, "end": v(104.5, -141.56) * mm});
            skArc(sketch, "E19.18.5.4", {"start": v(95.5, -141.56) * mm, "mid": v(96.09, -142.98) * mm, "end": v(97.5, -143.56) * mm});
            skPoint(sketch, "E19.0.5.5", {"position": v(95.5, -178.2) * mm});
            skLineSegment(sketch, "E19.1.5.5", {"start": v(104.5, -137.03) * mm, "end": v(104.5, -176.2) * mm});
            skPoint(sketch, "E19.4.5.5", {"position": v(104.5, -178.2) * mm});
            skLineSegment(sketch, "E19.5.5.5", {"start": v(95.5, -137.03) * mm, "end": v(104.5, -137.03) * mm});
            skLineSegment(sketch, "E19.8.5.5", {"start": v(97.5, -178.2) * mm, "end": v(102.5, -178.2) * mm});
            skLineSegment(sketch, "E19.11.5.5", {"start": v(95.5, -137.03) * mm, "end": v(95.5, -176.2) * mm});
            skArc(sketch, "E19.14.5.5", {"start": v(102.5, -178.2) * mm, "mid": v(103.91, -177.62) * mm, "end": v(104.5, -176.2) * mm});
            skArc(sketch, "E19.18.5.5", {"start": v(95.5, -176.2) * mm, "mid": v(96.09, -177.62) * mm, "end": v(97.5, -178.2) * mm});
            skPoint(sketch, "E19.0.5.6", {"position": v(95.5, -212.85) * mm});
            skLineSegment(sketch, "E19.1.5.6", {"start": v(104.5, -171.67) * mm, "end": v(104.5, -210.85) * mm});
            skPoint(sketch, "E19.4.5.6", {"position": v(104.5, -212.85) * mm});
            skLineSegment(sketch, "E19.5.5.6", {"start": v(95.5, -171.67) * mm, "end": v(104.5, -171.67) * mm});
            skLineSegment(sketch, "E19.8.5.6", {"start": v(97.5, -212.85) * mm, "end": v(102.5, -212.85) * mm});
            skLineSegment(sketch, "E19.11.5.6", {"start": v(95.5, -171.67) * mm, "end": v(95.5, -210.85) * mm});
            skArc(sketch, "E19.14.5.6", {"start": v(102.5, -212.85) * mm, "mid": v(103.91, -212.26) * mm, "end": v(104.5, -210.85) * mm});
            skArc(sketch, "E19.18.5.6", {"start": v(95.5, -210.85) * mm, "mid": v(96.09, -212.26) * mm, "end": v(97.5, -212.85) * mm});
            skPoint(sketch, "E19.0.5.7", {"position": v(95.5, -247.49) * mm});
            skLineSegment(sketch, "E19.1.5.7", {"start": v(104.5, -206.31) * mm, "end": v(104.5, -245.49) * mm});
            skPoint(sketch, "E19.4.5.7", {"position": v(104.5, -247.49) * mm});
            skLineSegment(sketch, "E19.5.5.7", {"start": v(95.5, -206.31) * mm, "end": v(104.5, -206.31) * mm});
            skLineSegment(sketch, "E19.8.5.7", {"start": v(97.5, -247.49) * mm, "end": v(102.5, -247.49) * mm});
            skLineSegment(sketch, "E19.11.5.7", {"start": v(95.5, -206.31) * mm, "end": v(95.5, -245.49) * mm});
            skArc(sketch, "E19.14.5.7", {"start": v(102.5, -247.49) * mm, "mid": v(103.91, -246.9) * mm, "end": v(104.5, -245.49) * mm});
            skArc(sketch, "E19.18.5.7", {"start": v(95.5, -245.49) * mm, "mid": v(96.09, -246.9) * mm, "end": v(97.5, -247.49) * mm});
            skPoint(sketch, "E19.0.5.8", {"position": v(95.5, -282.13) * mm});
            skLineSegment(sketch, "E19.1.5.8", {"start": v(104.5, -240.95) * mm, "end": v(104.5, -280.13) * mm});
            skPoint(sketch, "E19.4.5.8", {"position": v(104.5, -282.13) * mm});
            skLineSegment(sketch, "E19.5.5.8", {"start": v(95.5, -240.95) * mm, "end": v(104.5, -240.95) * mm});
            skLineSegment(sketch, "E19.8.5.8", {"start": v(97.5, -282.13) * mm, "end": v(102.5, -282.13) * mm});
            skLineSegment(sketch, "E19.11.5.8", {"start": v(95.5, -240.95) * mm, "end": v(95.5, -280.13) * mm});
            skArc(sketch, "E19.14.5.8", {"start": v(102.5, -282.13) * mm, "mid": v(103.91, -281.54) * mm, "end": v(104.5, -280.13) * mm});
            skArc(sketch, "E19.18.5.8", {"start": v(95.5, -280.13) * mm, "mid": v(96.09, -281.54) * mm, "end": v(97.5, -282.13) * mm});
            skPoint(sketch, "E19.0.5.9", {"position": v(95.5, -316.77) * mm});
            skLineSegment(sketch, "E19.1.5.9", {"start": v(104.5, -275.6) * mm, "end": v(104.5, -314.77) * mm});
            skPoint(sketch, "E19.4.5.9", {"position": v(104.5, -316.77) * mm});
            skLineSegment(sketch, "E19.5.5.9", {"start": v(95.5, -275.6) * mm, "end": v(104.5, -275.6) * mm});
            skLineSegment(sketch, "E19.8.5.9", {"start": v(97.5, -316.77) * mm, "end": v(102.5, -316.77) * mm});
            skLineSegment(sketch, "E19.11.5.9", {"start": v(95.5, -275.6) * mm, "end": v(95.5, -314.77) * mm});
            skArc(sketch, "E19.14.5.9", {"start": v(102.5, -316.77) * mm, "mid": v(103.91, -316.18) * mm, "end": v(104.5, -314.77) * mm});
            skArc(sketch, "E19.18.5.9", {"start": v(95.5, -314.77) * mm, "mid": v(96.09, -316.18) * mm, "end": v(97.5, -316.77) * mm});
            skPoint(sketch, "E19.0.5.10", {"position": v(95.5, -351.41) * mm});
            skLineSegment(sketch, "E19.1.5.10", {"start": v(104.5, -310.24) * mm, "end": v(104.5, -349.41) * mm});
            skPoint(sketch, "E19.4.5.10", {"position": v(104.5, -351.41) * mm});
            skLineSegment(sketch, "E19.5.5.10", {"start": v(95.5, -310.24) * mm, "end": v(104.5, -310.24) * mm});
            skLineSegment(sketch, "E19.8.5.10", {"start": v(97.5, -351.41) * mm, "end": v(102.5, -351.41) * mm});
            skLineSegment(sketch, "E19.11.5.10", {"start": v(95.5, -310.24) * mm, "end": v(95.5, -349.41) * mm});
            skArc(sketch, "E19.14.5.10", {"start": v(102.5, -351.41) * mm, "mid": v(103.91, -350.82) * mm, "end": v(104.5, -349.41) * mm});
            skArc(sketch, "E19.18.5.10", {"start": v(95.5, -349.41) * mm, "mid": v(96.09, -350.82) * mm, "end": v(97.5, -351.41) * mm});
            skPoint(sketch, "E19.0.5.11", {"position": v(95.5, -386.05) * mm});
            skLineSegment(sketch, "E19.1.5.11", {"start": v(104.5, -344.88) * mm, "end": v(104.5, -384.05) * mm});
            skPoint(sketch, "E19.4.5.11", {"position": v(104.5, -386.05) * mm});
            skLineSegment(sketch, "E19.5.5.11", {"start": v(95.5, -344.88) * mm, "end": v(104.5, -344.88) * mm});
            skLineSegment(sketch, "E19.8.5.11", {"start": v(97.5, -386.05) * mm, "end": v(102.5, -386.05) * mm});
            skLineSegment(sketch, "E19.11.5.11", {"start": v(95.5, -344.88) * mm, "end": v(95.5, -384.05) * mm});
            skArc(sketch, "E19.14.5.11", {"start": v(102.5, -386.05) * mm, "mid": v(103.91, -385.47) * mm, "end": v(104.5, -384.05) * mm});
            skArc(sketch, "E19.18.5.11", {"start": v(95.5, -384.05) * mm, "mid": v(96.09, -385.47) * mm, "end": v(97.5, -386.05) * mm});
            skPoint(sketch, "E19.0.5.12", {"position": v(95.5, -420.7) * mm});
            skLineSegment(sketch, "E19.1.5.12", {"start": v(104.5, -379.52) * mm, "end": v(104.5, -418.7) * mm});
            skPoint(sketch, "E19.4.5.12", {"position": v(104.5, -420.7) * mm});
            skLineSegment(sketch, "E19.5.5.12", {"start": v(95.5, -379.52) * mm, "end": v(104.5, -379.52) * mm});
            skLineSegment(sketch, "E19.8.5.12", {"start": v(97.5, -420.7) * mm, "end": v(102.5, -420.7) * mm});
            skLineSegment(sketch, "E19.11.5.12", {"start": v(95.5, -379.52) * mm, "end": v(95.5, -418.7) * mm});
            skArc(sketch, "E19.14.5.12", {"start": v(102.5, -420.7) * mm, "mid": v(103.91, -420.1) * mm, "end": v(104.5, -418.7) * mm});
            skArc(sketch, "E19.18.5.12", {"start": v(95.5, -418.7) * mm, "mid": v(96.09, -420.1) * mm, "end": v(97.5, -420.7) * mm});
            skPoint(sketch, "E19.0.5.13", {"position": v(95.5, -455.33) * mm});
            skLineSegment(sketch, "E19.1.5.13", {"start": v(104.5, -414.16) * mm, "end": v(104.5, -453.33) * mm});
            skPoint(sketch, "E19.4.5.13", {"position": v(104.5, -455.33) * mm});
            skLineSegment(sketch, "E19.5.5.13", {"start": v(95.5, -414.16) * mm, "end": v(104.5, -414.16) * mm});
            skLineSegment(sketch, "E19.8.5.13", {"start": v(97.5, -455.33) * mm, "end": v(102.5, -455.33) * mm});
            skLineSegment(sketch, "E19.11.5.13", {"start": v(95.5, -414.16) * mm, "end": v(95.5, -453.33) * mm});
            skArc(sketch, "E19.14.5.13", {"start": v(102.5, -455.33) * mm, "mid": v(103.91, -454.75) * mm, "end": v(104.5, -453.33) * mm});
            skArc(sketch, "E19.18.5.13", {"start": v(95.5, -453.33) * mm, "mid": v(96.09, -454.75) * mm, "end": v(97.5, -455.33) * mm});
            skPoint(sketch, "E19.0.5.14", {"position": v(95.5, -489.97) * mm});
            skLineSegment(sketch, "E19.1.5.14", {"start": v(104.5, -448.8) * mm, "end": v(104.5, -487.97) * mm});
            skPoint(sketch, "E19.4.5.14", {"position": v(104.5, -489.97) * mm});
            skLineSegment(sketch, "E19.5.5.14", {"start": v(95.5, -448.8) * mm, "end": v(104.5, -448.8) * mm});
            skLineSegment(sketch, "E19.8.5.14", {"start": v(97.5, -489.97) * mm, "end": v(102.5, -489.97) * mm});
            skLineSegment(sketch, "E19.11.5.14", {"start": v(95.5, -448.8) * mm, "end": v(95.5, -487.97) * mm});
            skArc(sketch, "E19.14.5.14", {"start": v(102.5, -489.97) * mm, "mid": v(103.91, -489.39) * mm, "end": v(104.5, -487.97) * mm});
            skArc(sketch, "E19.18.5.14", {"start": v(95.5, -487.97) * mm, "mid": v(96.09, -489.39) * mm, "end": v(97.5, -489.97) * mm});
            skPoint(sketch, "E19.0.6.0", {"position": v(115.5, -5) * mm});
            skLineSegment(sketch, "E19.1.6.0", {"start": v(124.5, 36.17) * mm, "end": v(124.5, -3) * mm});
            skPoint(sketch, "E19.4.6.0", {"position": v(124.5, -5) * mm});
            skLineSegment(sketch, "E19.5.6.0", {"start": v(115.5, 36.17) * mm, "end": v(124.5, 36.17) * mm});
            skLineSegment(sketch, "E19.8.6.0", {"start": v(117.5, -5) * mm, "end": v(122.5, -5) * mm});
            skLineSegment(sketch, "E19.11.6.0", {"start": v(115.5, 36.17) * mm, "end": v(115.5, -3) * mm});
            skArc(sketch, "E19.14.6.0", {"start": v(122.5, -5) * mm, "mid": v(123.91, -4.41) * mm, "end": v(124.5, -3) * mm});
            skArc(sketch, "E19.18.6.0", {"start": v(115.5, -3) * mm, "mid": v(116.09, -4.41) * mm, "end": v(117.5, -5) * mm});
            skPoint(sketch, "E19.0.6.1", {"position": v(115.5, -39.64) * mm});
            skLineSegment(sketch, "E19.1.6.1", {"start": v(124.5, 1.53) * mm, "end": v(124.5, -37.64) * mm});
            skPoint(sketch, "E19.4.6.1", {"position": v(124.5, -39.64) * mm});
            skLineSegment(sketch, "E19.5.6.1", {"start": v(115.5, 1.53) * mm, "end": v(124.5, 1.53) * mm});
            skLineSegment(sketch, "E19.8.6.1", {"start": v(117.5, -39.64) * mm, "end": v(122.5, -39.64) * mm});
            skLineSegment(sketch, "E19.11.6.1", {"start": v(115.5, 1.53) * mm, "end": v(115.5, -37.64) * mm});
            skArc(sketch, "E19.14.6.1", {"start": v(122.5, -39.64) * mm, "mid": v(123.91, -39.06) * mm, "end": v(124.5, -37.64) * mm});
            skArc(sketch, "E19.18.6.1", {"start": v(115.5, -37.64) * mm, "mid": v(116.09, -39.06) * mm, "end": v(117.5, -39.64) * mm});
            skPoint(sketch, "E19.0.6.2", {"position": v(115.5, -74.28) * mm});
            skLineSegment(sketch, "E19.1.6.2", {"start": v(124.5, -33.1) * mm, "end": v(124.5, -72.28) * mm});
            skPoint(sketch, "E19.4.6.2", {"position": v(124.5, -74.28) * mm});
            skLineSegment(sketch, "E19.5.6.2", {"start": v(115.5, -33.1) * mm, "end": v(124.5, -33.1) * mm});
            skLineSegment(sketch, "E19.8.6.2", {"start": v(117.5, -74.28) * mm, "end": v(122.5, -74.28) * mm});
            skLineSegment(sketch, "E19.11.6.2", {"start": v(115.5, -33.1) * mm, "end": v(115.5, -72.28) * mm});
            skArc(sketch, "E19.14.6.2", {"start": v(122.5, -74.28) * mm, "mid": v(123.91, -73.7) * mm, "end": v(124.5, -72.28) * mm});
            skArc(sketch, "E19.18.6.2", {"start": v(115.5, -72.28) * mm, "mid": v(116.09, -73.7) * mm, "end": v(117.5, -74.28) * mm});
            skPoint(sketch, "E19.0.6.3", {"position": v(115.5, -108.92) * mm});
            skLineSegment(sketch, "E19.1.6.3", {"start": v(124.5, -67.75) * mm, "end": v(124.5, -106.92) * mm});
            skPoint(sketch, "E19.4.6.3", {"position": v(124.5, -108.92) * mm});
            skLineSegment(sketch, "E19.5.6.3", {"start": v(115.5, -67.75) * mm, "end": v(124.5, -67.75) * mm});
            skLineSegment(sketch, "E19.8.6.3", {"start": v(117.5, -108.92) * mm, "end": v(122.5, -108.92) * mm});
            skLineSegment(sketch, "E19.11.6.3", {"start": v(115.5, -67.75) * mm, "end": v(115.5, -106.92) * mm});
            skArc(sketch, "E19.14.6.3", {"start": v(122.5, -108.92) * mm, "mid": v(123.91, -108.34) * mm, "end": v(124.5, -106.92) * mm});
            skArc(sketch, "E19.18.6.3", {"start": v(115.5, -106.92) * mm, "mid": v(116.09, -108.34) * mm, "end": v(117.5, -108.92) * mm});
            skPoint(sketch, "E19.0.6.4", {"position": v(115.5, -143.56) * mm});
            skLineSegment(sketch, "E19.1.6.4", {"start": v(124.5, -102.4) * mm, "end": v(124.5, -141.56) * mm});
            skPoint(sketch, "E19.4.6.4", {"position": v(124.5, -143.56) * mm});
            skLineSegment(sketch, "E19.5.6.4", {"start": v(115.5, -102.4) * mm, "end": v(124.5, -102.4) * mm});
            skLineSegment(sketch, "E19.8.6.4", {"start": v(117.5, -143.56) * mm, "end": v(122.5, -143.56) * mm});
            skLineSegment(sketch, "E19.11.6.4", {"start": v(115.5, -102.4) * mm, "end": v(115.5, -141.56) * mm});
            skArc(sketch, "E19.14.6.4", {"start": v(122.5, -143.56) * mm, "mid": v(123.91, -142.98) * mm, "end": v(124.5, -141.56) * mm});
            skArc(sketch, "E19.18.6.4", {"start": v(115.5, -141.56) * mm, "mid": v(116.09, -142.98) * mm, "end": v(117.5, -143.56) * mm});
            skPoint(sketch, "E19.0.6.5", {"position": v(115.5, -178.2) * mm});
            skLineSegment(sketch, "E19.1.6.5", {"start": v(124.5, -137.03) * mm, "end": v(124.5, -176.2) * mm});
            skPoint(sketch, "E19.4.6.5", {"position": v(124.5, -178.2) * mm});
            skLineSegment(sketch, "E19.5.6.5", {"start": v(115.5, -137.03) * mm, "end": v(124.5, -137.03) * mm});
            skLineSegment(sketch, "E19.8.6.5", {"start": v(117.5, -178.2) * mm, "end": v(122.5, -178.2) * mm});
            skLineSegment(sketch, "E19.11.6.5", {"start": v(115.5, -137.03) * mm, "end": v(115.5, -176.2) * mm});
            skArc(sketch, "E19.14.6.5", {"start": v(122.5, -178.2) * mm, "mid": v(123.91, -177.62) * mm, "end": v(124.5, -176.2) * mm});
            skArc(sketch, "E19.18.6.5", {"start": v(115.5, -176.2) * mm, "mid": v(116.09, -177.62) * mm, "end": v(117.5, -178.2) * mm});
            skPoint(sketch, "E19.0.6.6", {"position": v(115.5, -212.85) * mm});
            skLineSegment(sketch, "E19.1.6.6", {"start": v(124.5, -171.67) * mm, "end": v(124.5, -210.85) * mm});
            skPoint(sketch, "E19.4.6.6", {"position": v(124.5, -212.85) * mm});
            skLineSegment(sketch, "E19.5.6.6", {"start": v(115.5, -171.67) * mm, "end": v(124.5, -171.67) * mm});
            skLineSegment(sketch, "E19.8.6.6", {"start": v(117.5, -212.85) * mm, "end": v(122.5, -212.85) * mm});
            skLineSegment(sketch, "E19.11.6.6", {"start": v(115.5, -171.67) * mm, "end": v(115.5, -210.85) * mm});
            skArc(sketch, "E19.14.6.6", {"start": v(122.5, -212.85) * mm, "mid": v(123.91, -212.26) * mm, "end": v(124.5, -210.85) * mm});
            skArc(sketch, "E19.18.6.6", {"start": v(115.5, -210.85) * mm, "mid": v(116.09, -212.26) * mm, "end": v(117.5, -212.85) * mm});
            skPoint(sketch, "E19.0.6.7", {"position": v(115.5, -247.49) * mm});
            skLineSegment(sketch, "E19.1.6.7", {"start": v(124.5, -206.31) * mm, "end": v(124.5, -245.49) * mm});
            skPoint(sketch, "E19.4.6.7", {"position": v(124.5, -247.49) * mm});
            skLineSegment(sketch, "E19.5.6.7", {"start": v(115.5, -206.31) * mm, "end": v(124.5, -206.31) * mm});
            skLineSegment(sketch, "E19.8.6.7", {"start": v(117.5, -247.49) * mm, "end": v(122.5, -247.49) * mm});
            skLineSegment(sketch, "E19.11.6.7", {"start": v(115.5, -206.31) * mm, "end": v(115.5, -245.49) * mm});
            skArc(sketch, "E19.14.6.7", {"start": v(122.5, -247.49) * mm, "mid": v(123.91, -246.9) * mm, "end": v(124.5, -245.49) * mm});
            skArc(sketch, "E19.18.6.7", {"start": v(115.5, -245.49) * mm, "mid": v(116.09, -246.9) * mm, "end": v(117.5, -247.49) * mm});
            skPoint(sketch, "E19.0.6.8", {"position": v(115.5, -282.13) * mm});
            skLineSegment(sketch, "E19.1.6.8", {"start": v(124.5, -240.95) * mm, "end": v(124.5, -280.13) * mm});
            skPoint(sketch, "E19.4.6.8", {"position": v(124.5, -282.13) * mm});
            skLineSegment(sketch, "E19.5.6.8", {"start": v(115.5, -240.95) * mm, "end": v(124.5, -240.95) * mm});
            skLineSegment(sketch, "E19.8.6.8", {"start": v(117.5, -282.13) * mm, "end": v(122.5, -282.13) * mm});
            skLineSegment(sketch, "E19.11.6.8", {"start": v(115.5, -240.95) * mm, "end": v(115.5, -280.13) * mm});
            skArc(sketch, "E19.14.6.8", {"start": v(122.5, -282.13) * mm, "mid": v(123.91, -281.54) * mm, "end": v(124.5, -280.13) * mm});
            skArc(sketch, "E19.18.6.8", {"start": v(115.5, -280.13) * mm, "mid": v(116.09, -281.54) * mm, "end": v(117.5, -282.13) * mm});
            skPoint(sketch, "E19.0.6.9", {"position": v(115.5, -316.77) * mm});
            skLineSegment(sketch, "E19.1.6.9", {"start": v(124.5, -275.6) * mm, "end": v(124.5, -314.77) * mm});
            skPoint(sketch, "E19.4.6.9", {"position": v(124.5, -316.77) * mm});
            skLineSegment(sketch, "E19.5.6.9", {"start": v(115.5, -275.6) * mm, "end": v(124.5, -275.6) * mm});
            skLineSegment(sketch, "E19.8.6.9", {"start": v(117.5, -316.77) * mm, "end": v(122.5, -316.77) * mm});
            skLineSegment(sketch, "E19.11.6.9", {"start": v(115.5, -275.6) * mm, "end": v(115.5, -314.77) * mm});
            skArc(sketch, "E19.14.6.9", {"start": v(122.5, -316.77) * mm, "mid": v(123.91, -316.18) * mm, "end": v(124.5, -314.77) * mm});
            skArc(sketch, "E19.18.6.9", {"start": v(115.5, -314.77) * mm, "mid": v(116.09, -316.18) * mm, "end": v(117.5, -316.77) * mm});
            skPoint(sketch, "E19.0.6.10", {"position": v(115.5, -351.41) * mm});
            skLineSegment(sketch, "E19.1.6.10", {"start": v(124.5, -310.24) * mm, "end": v(124.5, -349.41) * mm});
            skPoint(sketch, "E19.4.6.10", {"position": v(124.5, -351.41) * mm});
            skLineSegment(sketch, "E19.5.6.10", {"start": v(115.5, -310.24) * mm, "end": v(124.5, -310.24) * mm});
            skLineSegment(sketch, "E19.8.6.10", {"start": v(117.5, -351.41) * mm, "end": v(122.5, -351.41) * mm});
            skLineSegment(sketch, "E19.11.6.10", {"start": v(115.5, -310.24) * mm, "end": v(115.5, -349.41) * mm});
            skArc(sketch, "E19.14.6.10", {"start": v(122.5, -351.41) * mm, "mid": v(123.91, -350.82) * mm, "end": v(124.5, -349.41) * mm});
            skArc(sketch, "E19.18.6.10", {"start": v(115.5, -349.41) * mm, "mid": v(116.09, -350.82) * mm, "end": v(117.5, -351.41) * mm});
            skPoint(sketch, "E19.0.6.11", {"position": v(115.5, -386.05) * mm});
            skLineSegment(sketch, "E19.1.6.11", {"start": v(124.5, -344.88) * mm, "end": v(124.5, -384.05) * mm});
            skPoint(sketch, "E19.4.6.11", {"position": v(124.5, -386.05) * mm});
            skLineSegment(sketch, "E19.5.6.11", {"start": v(115.5, -344.88) * mm, "end": v(124.5, -344.88) * mm});
            skLineSegment(sketch, "E19.8.6.11", {"start": v(117.5, -386.05) * mm, "end": v(122.5, -386.05) * mm});
            skLineSegment(sketch, "E19.11.6.11", {"start": v(115.5, -344.88) * mm, "end": v(115.5, -384.05) * mm});
            skArc(sketch, "E19.14.6.11", {"start": v(122.5, -386.05) * mm, "mid": v(123.91, -385.47) * mm, "end": v(124.5, -384.05) * mm});
            skArc(sketch, "E19.18.6.11", {"start": v(115.5, -384.05) * mm, "mid": v(116.09, -385.47) * mm, "end": v(117.5, -386.05) * mm});
            skPoint(sketch, "E19.0.6.12", {"position": v(115.5, -420.7) * mm});
            skLineSegment(sketch, "E19.1.6.12", {"start": v(124.5, -379.52) * mm, "end": v(124.5, -418.7) * mm});
            skPoint(sketch, "E19.4.6.12", {"position": v(124.5, -420.7) * mm});
            skLineSegment(sketch, "E19.5.6.12", {"start": v(115.5, -379.52) * mm, "end": v(124.5, -379.52) * mm});
            skLineSegment(sketch, "E19.8.6.12", {"start": v(117.5, -420.7) * mm, "end": v(122.5, -420.7) * mm});
            skLineSegment(sketch, "E19.11.6.12", {"start": v(115.5, -379.52) * mm, "end": v(115.5, -418.7) * mm});
            skArc(sketch, "E19.14.6.12", {"start": v(122.5, -420.7) * mm, "mid": v(123.91, -420.1) * mm, "end": v(124.5, -418.7) * mm});
            skArc(sketch, "E19.18.6.12", {"start": v(115.5, -418.7) * mm, "mid": v(116.09, -420.1) * mm, "end": v(117.5, -420.7) * mm});
            skPoint(sketch, "E19.0.6.13", {"position": v(115.5, -455.33) * mm});
            skLineSegment(sketch, "E19.1.6.13", {"start": v(124.5, -414.16) * mm, "end": v(124.5, -453.33) * mm});
            skPoint(sketch, "E19.4.6.13", {"position": v(124.5, -455.33) * mm});
            skLineSegment(sketch, "E19.5.6.13", {"start": v(115.5, -414.16) * mm, "end": v(124.5, -414.16) * mm});
            skLineSegment(sketch, "E19.8.6.13", {"start": v(117.5, -455.33) * mm, "end": v(122.5, -455.33) * mm});
            skLineSegment(sketch, "E19.11.6.13", {"start": v(115.5, -414.16) * mm, "end": v(115.5, -453.33) * mm});
            skArc(sketch, "E19.14.6.13", {"start": v(122.5, -455.33) * mm, "mid": v(123.91, -454.75) * mm, "end": v(124.5, -453.33) * mm});
            skArc(sketch, "E19.18.6.13", {"start": v(115.5, -453.33) * mm, "mid": v(116.09, -454.75) * mm, "end": v(117.5, -455.33) * mm});
            skPoint(sketch, "E19.0.6.14", {"position": v(115.5, -489.97) * mm});
            skLineSegment(sketch, "E19.1.6.14", {"start": v(124.5, -448.8) * mm, "end": v(124.5, -487.97) * mm});
            skPoint(sketch, "E19.4.6.14", {"position": v(124.5, -489.97) * mm});
            skLineSegment(sketch, "E19.5.6.14", {"start": v(115.5, -448.8) * mm, "end": v(124.5, -448.8) * mm});
            skLineSegment(sketch, "E19.8.6.14", {"start": v(117.5, -489.97) * mm, "end": v(122.5, -489.97) * mm});
            skLineSegment(sketch, "E19.11.6.14", {"start": v(115.5, -448.8) * mm, "end": v(115.5, -487.97) * mm});
            skArc(sketch, "E19.14.6.14", {"start": v(122.5, -489.97) * mm, "mid": v(123.91, -489.39) * mm, "end": v(124.5, -487.97) * mm});
            skArc(sketch, "E19.18.6.14", {"start": v(115.5, -487.97) * mm, "mid": v(116.09, -489.39) * mm, "end": v(117.5, -489.97) * mm});
            skPoint(sketch, "E19.0.7.0", {"position": v(135.5, -5) * mm});
            skLineSegment(sketch, "E19.1.7.0", {"start": v(144.5, 36.17) * mm, "end": v(144.5, -3) * mm});
            skPoint(sketch, "E19.4.7.0", {"position": v(144.5, -5) * mm});
            skLineSegment(sketch, "E19.5.7.0", {"start": v(135.5, 36.17) * mm, "end": v(144.5, 36.17) * mm});
            skLineSegment(sketch, "E19.8.7.0", {"start": v(137.5, -5) * mm, "end": v(142.5, -5) * mm});
            skLineSegment(sketch, "E19.11.7.0", {"start": v(135.5, 36.17) * mm, "end": v(135.5, -3) * mm});
            skArc(sketch, "E19.14.7.0", {"start": v(142.5, -5) * mm, "mid": v(143.91, -4.41) * mm, "end": v(144.5, -3) * mm});
            skArc(sketch, "E19.18.7.0", {"start": v(135.5, -3) * mm, "mid": v(136.09, -4.41) * mm, "end": v(137.5, -5) * mm});
            skPoint(sketch, "E19.0.7.1", {"position": v(135.5, -39.64) * mm});
            skLineSegment(sketch, "E19.1.7.1", {"start": v(144.5, 1.53) * mm, "end": v(144.5, -37.64) * mm});
            skPoint(sketch, "E19.4.7.1", {"position": v(144.5, -39.64) * mm});
            skLineSegment(sketch, "E19.5.7.1", {"start": v(135.5, 1.53) * mm, "end": v(144.5, 1.53) * mm});
            skLineSegment(sketch, "E19.8.7.1", {"start": v(137.5, -39.64) * mm, "end": v(142.5, -39.64) * mm});
            skLineSegment(sketch, "E19.11.7.1", {"start": v(135.5, 1.53) * mm, "end": v(135.5, -37.64) * mm});
            skArc(sketch, "E19.14.7.1", {"start": v(142.5, -39.64) * mm, "mid": v(143.91, -39.06) * mm, "end": v(144.5, -37.64) * mm});
            skArc(sketch, "E19.18.7.1", {"start": v(135.5, -37.64) * mm, "mid": v(136.09, -39.06) * mm, "end": v(137.5, -39.64) * mm});
            skPoint(sketch, "E19.0.7.2", {"position": v(135.5, -74.28) * mm});
            skLineSegment(sketch, "E19.1.7.2", {"start": v(144.5, -33.1) * mm, "end": v(144.5, -72.28) * mm});
            skPoint(sketch, "E19.4.7.2", {"position": v(144.5, -74.28) * mm});
            skLineSegment(sketch, "E19.5.7.2", {"start": v(135.5, -33.1) * mm, "end": v(144.5, -33.1) * mm});
            skLineSegment(sketch, "E19.8.7.2", {"start": v(137.5, -74.28) * mm, "end": v(142.5, -74.28) * mm});
            skLineSegment(sketch, "E19.11.7.2", {"start": v(135.5, -33.1) * mm, "end": v(135.5, -72.28) * mm});
            skArc(sketch, "E19.14.7.2", {"start": v(142.5, -74.28) * mm, "mid": v(143.91, -73.7) * mm, "end": v(144.5, -72.28) * mm});
            skArc(sketch, "E19.18.7.2", {"start": v(135.5, -72.28) * mm, "mid": v(136.09, -73.7) * mm, "end": v(137.5, -74.28) * mm});
            skPoint(sketch, "E19.0.7.3", {"position": v(135.5, -108.92) * mm});
            skLineSegment(sketch, "E19.1.7.3", {"start": v(144.5, -67.75) * mm, "end": v(144.5, -106.92) * mm});
            skPoint(sketch, "E19.4.7.3", {"position": v(144.5, -108.92) * mm});
            skLineSegment(sketch, "E19.5.7.3", {"start": v(135.5, -67.75) * mm, "end": v(144.5, -67.75) * mm});
            skLineSegment(sketch, "E19.8.7.3", {"start": v(137.5, -108.92) * mm, "end": v(142.5, -108.92) * mm});
            skLineSegment(sketch, "E19.11.7.3", {"start": v(135.5, -67.75) * mm, "end": v(135.5, -106.92) * mm});
            skArc(sketch, "E19.14.7.3", {"start": v(142.5, -108.92) * mm, "mid": v(143.91, -108.34) * mm, "end": v(144.5, -106.92) * mm});
            skArc(sketch, "E19.18.7.3", {"start": v(135.5, -106.92) * mm, "mid": v(136.09, -108.34) * mm, "end": v(137.5, -108.92) * mm});
            skPoint(sketch, "E19.0.7.4", {"position": v(135.5, -143.56) * mm});
            skLineSegment(sketch, "E19.1.7.4", {"start": v(144.5, -102.4) * mm, "end": v(144.5, -141.56) * mm});
            skPoint(sketch, "E19.4.7.4", {"position": v(144.5, -143.56) * mm});
            skLineSegment(sketch, "E19.5.7.4", {"start": v(135.5, -102.4) * mm, "end": v(144.5, -102.4) * mm});
            skLineSegment(sketch, "E19.8.7.4", {"start": v(137.5, -143.56) * mm, "end": v(142.5, -143.56) * mm});
            skLineSegment(sketch, "E19.11.7.4", {"start": v(135.5, -102.4) * mm, "end": v(135.5, -141.56) * mm});
            skArc(sketch, "E19.14.7.4", {"start": v(142.5, -143.56) * mm, "mid": v(143.91, -142.98) * mm, "end": v(144.5, -141.56) * mm});
            skArc(sketch, "E19.18.7.4", {"start": v(135.5, -141.56) * mm, "mid": v(136.09, -142.98) * mm, "end": v(137.5, -143.56) * mm});
            skPoint(sketch, "E19.0.7.5", {"position": v(135.5, -178.2) * mm});
            skLineSegment(sketch, "E19.1.7.5", {"start": v(144.5, -137.03) * mm, "end": v(144.5, -176.2) * mm});
            skPoint(sketch, "E19.4.7.5", {"position": v(144.5, -178.2) * mm});
            skLineSegment(sketch, "E19.5.7.5", {"start": v(135.5, -137.03) * mm, "end": v(144.5, -137.03) * mm});
            skLineSegment(sketch, "E19.8.7.5", {"start": v(137.5, -178.2) * mm, "end": v(142.5, -178.2) * mm});
            skLineSegment(sketch, "E19.11.7.5", {"start": v(135.5, -137.03) * mm, "end": v(135.5, -176.2) * mm});
            skArc(sketch, "E19.14.7.5", {"start": v(142.5, -178.2) * mm, "mid": v(143.91, -177.62) * mm, "end": v(144.5, -176.2) * mm});
            skArc(sketch, "E19.18.7.5", {"start": v(135.5, -176.2) * mm, "mid": v(136.09, -177.62) * mm, "end": v(137.5, -178.2) * mm});
            skPoint(sketch, "E19.0.7.6", {"position": v(135.5, -212.85) * mm});
            skLineSegment(sketch, "E19.1.7.6", {"start": v(144.5, -171.67) * mm, "end": v(144.5, -210.85) * mm});
            skPoint(sketch, "E19.4.7.6", {"position": v(144.5, -212.85) * mm});
            skLineSegment(sketch, "E19.5.7.6", {"start": v(135.5, -171.67) * mm, "end": v(144.5, -171.67) * mm});
            skLineSegment(sketch, "E19.8.7.6", {"start": v(137.5, -212.85) * mm, "end": v(142.5, -212.85) * mm});
            skLineSegment(sketch, "E19.11.7.6", {"start": v(135.5, -171.67) * mm, "end": v(135.5, -210.85) * mm});
            skArc(sketch, "E19.14.7.6", {"start": v(142.5, -212.85) * mm, "mid": v(143.91, -212.26) * mm, "end": v(144.5, -210.85) * mm});
            skArc(sketch, "E19.18.7.6", {"start": v(135.5, -210.85) * mm, "mid": v(136.09, -212.26) * mm, "end": v(137.5, -212.85) * mm});
            skPoint(sketch, "E19.0.7.7", {"position": v(135.5, -247.49) * mm});
            skLineSegment(sketch, "E19.1.7.7", {"start": v(144.5, -206.31) * mm, "end": v(144.5, -245.49) * mm});
            skPoint(sketch, "E19.4.7.7", {"position": v(144.5, -247.49) * mm});
            skLineSegment(sketch, "E19.5.7.7", {"start": v(135.5, -206.31) * mm, "end": v(144.5, -206.31) * mm});
            skLineSegment(sketch, "E19.8.7.7", {"start": v(137.5, -247.49) * mm, "end": v(142.5, -247.49) * mm});
            skLineSegment(sketch, "E19.11.7.7", {"start": v(135.5, -206.31) * mm, "end": v(135.5, -245.49) * mm});
            skArc(sketch, "E19.14.7.7", {"start": v(142.5, -247.49) * mm, "mid": v(143.91, -246.9) * mm, "end": v(144.5, -245.49) * mm});
            skArc(sketch, "E19.18.7.7", {"start": v(135.5, -245.49) * mm, "mid": v(136.09, -246.9) * mm, "end": v(137.5, -247.49) * mm});
            skPoint(sketch, "E19.0.7.8", {"position": v(135.5, -282.13) * mm});
            skLineSegment(sketch, "E19.1.7.8", {"start": v(144.5, -240.95) * mm, "end": v(144.5, -280.13) * mm});
            skPoint(sketch, "E19.4.7.8", {"position": v(144.5, -282.13) * mm});
            skLineSegment(sketch, "E19.5.7.8", {"start": v(135.5, -240.95) * mm, "end": v(144.5, -240.95) * mm});
            skLineSegment(sketch, "E19.8.7.8", {"start": v(137.5, -282.13) * mm, "end": v(142.5, -282.13) * mm});
            skLineSegment(sketch, "E19.11.7.8", {"start": v(135.5, -240.95) * mm, "end": v(135.5, -280.13) * mm});
            skArc(sketch, "E19.14.7.8", {"start": v(142.5, -282.13) * mm, "mid": v(143.91, -281.54) * mm, "end": v(144.5, -280.13) * mm});
            skArc(sketch, "E19.18.7.8", {"start": v(135.5, -280.13) * mm, "mid": v(136.09, -281.54) * mm, "end": v(137.5, -282.13) * mm});
            skPoint(sketch, "E19.0.7.9", {"position": v(135.5, -316.77) * mm});
            skLineSegment(sketch, "E19.1.7.9", {"start": v(144.5, -275.6) * mm, "end": v(144.5, -314.77) * mm});
            skPoint(sketch, "E19.4.7.9", {"position": v(144.5, -316.77) * mm});
            skLineSegment(sketch, "E19.5.7.9", {"start": v(135.5, -275.6) * mm, "end": v(144.5, -275.6) * mm});
            skLineSegment(sketch, "E19.8.7.9", {"start": v(137.5, -316.77) * mm, "end": v(142.5, -316.77) * mm});
            skLineSegment(sketch, "E19.11.7.9", {"start": v(135.5, -275.6) * mm, "end": v(135.5, -314.77) * mm});
            skArc(sketch, "E19.14.7.9", {"start": v(142.5, -316.77) * mm, "mid": v(143.91, -316.18) * mm, "end": v(144.5, -314.77) * mm});
            skArc(sketch, "E19.18.7.9", {"start": v(135.5, -314.77) * mm, "mid": v(136.09, -316.18) * mm, "end": v(137.5, -316.77) * mm});
            skPoint(sketch, "E19.0.7.10", {"position": v(135.5, -351.41) * mm});
            skLineSegment(sketch, "E19.1.7.10", {"start": v(144.5, -310.24) * mm, "end": v(144.5, -349.41) * mm});
            skPoint(sketch, "E19.4.7.10", {"position": v(144.5, -351.41) * mm});
            skLineSegment(sketch, "E19.5.7.10", {"start": v(135.5, -310.24) * mm, "end": v(144.5, -310.24) * mm});
            skLineSegment(sketch, "E19.8.7.10", {"start": v(137.5, -351.41) * mm, "end": v(142.5, -351.41) * mm});
            skLineSegment(sketch, "E19.11.7.10", {"start": v(135.5, -310.24) * mm, "end": v(135.5, -349.41) * mm});
            skArc(sketch, "E19.14.7.10", {"start": v(142.5, -351.41) * mm, "mid": v(143.91, -350.82) * mm, "end": v(144.5, -349.41) * mm});
            skArc(sketch, "E19.18.7.10", {"start": v(135.5, -349.41) * mm, "mid": v(136.09, -350.82) * mm, "end": v(137.5, -351.41) * mm});
            skPoint(sketch, "E19.0.7.11", {"position": v(135.5, -386.05) * mm});
            skLineSegment(sketch, "E19.1.7.11", {"start": v(144.5, -344.88) * mm, "end": v(144.5, -384.05) * mm});
            skPoint(sketch, "E19.4.7.11", {"position": v(144.5, -386.05) * mm});
            skLineSegment(sketch, "E19.5.7.11", {"start": v(135.5, -344.88) * mm, "end": v(144.5, -344.88) * mm});
            skLineSegment(sketch, "E19.8.7.11", {"start": v(137.5, -386.05) * mm, "end": v(142.5, -386.05) * mm});
            skLineSegment(sketch, "E19.11.7.11", {"start": v(135.5, -344.88) * mm, "end": v(135.5, -384.05) * mm});
            skArc(sketch, "E19.14.7.11", {"start": v(142.5, -386.05) * mm, "mid": v(143.91, -385.47) * mm, "end": v(144.5, -384.05) * mm});
            skArc(sketch, "E19.18.7.11", {"start": v(135.5, -384.05) * mm, "mid": v(136.09, -385.47) * mm, "end": v(137.5, -386.05) * mm});
            skPoint(sketch, "E19.0.7.12", {"position": v(135.5, -420.7) * mm});
            skLineSegment(sketch, "E19.1.7.12", {"start": v(144.5, -379.52) * mm, "end": v(144.5, -418.7) * mm});
            skPoint(sketch, "E19.4.7.12", {"position": v(144.5, -420.7) * mm});
            skLineSegment(sketch, "E19.5.7.12", {"start": v(135.5, -379.52) * mm, "end": v(144.5, -379.52) * mm});
            skLineSegment(sketch, "E19.8.7.12", {"start": v(137.5, -420.7) * mm, "end": v(142.5, -420.7) * mm});
            skLineSegment(sketch, "E19.11.7.12", {"start": v(135.5, -379.52) * mm, "end": v(135.5, -418.7) * mm});
            skArc(sketch, "E19.14.7.12", {"start": v(142.5, -420.7) * mm, "mid": v(143.91, -420.1) * mm, "end": v(144.5, -418.7) * mm});
            skArc(sketch, "E19.18.7.12", {"start": v(135.5, -418.7) * mm, "mid": v(136.09, -420.1) * mm, "end": v(137.5, -420.7) * mm});
            skPoint(sketch, "E19.0.7.13", {"position": v(135.5, -455.33) * mm});
            skLineSegment(sketch, "E19.1.7.13", {"start": v(144.5, -414.16) * mm, "end": v(144.5, -453.33) * mm});
            skPoint(sketch, "E19.4.7.13", {"position": v(144.5, -455.33) * mm});
            skLineSegment(sketch, "E19.5.7.13", {"start": v(135.5, -414.16) * mm, "end": v(144.5, -414.16) * mm});
            skLineSegment(sketch, "E19.8.7.13", {"start": v(137.5, -455.33) * mm, "end": v(142.5, -455.33) * mm});
            skLineSegment(sketch, "E19.11.7.13", {"start": v(135.5, -414.16) * mm, "end": v(135.5, -453.33) * mm});
            skArc(sketch, "E19.14.7.13", {"start": v(142.5, -455.33) * mm, "mid": v(143.91, -454.75) * mm, "end": v(144.5, -453.33) * mm});
            skArc(sketch, "E19.18.7.13", {"start": v(135.5, -453.33) * mm, "mid": v(136.09, -454.75) * mm, "end": v(137.5, -455.33) * mm});
            skPoint(sketch, "E19.0.7.14", {"position": v(135.5, -489.97) * mm});
            skLineSegment(sketch, "E19.1.7.14", {"start": v(144.5, -448.8) * mm, "end": v(144.5, -487.97) * mm});
            skPoint(sketch, "E19.4.7.14", {"position": v(144.5, -489.97) * mm});
            skLineSegment(sketch, "E19.5.7.14", {"start": v(135.5, -448.8) * mm, "end": v(144.5, -448.8) * mm});
            skLineSegment(sketch, "E19.8.7.14", {"start": v(137.5, -489.97) * mm, "end": v(142.5, -489.97) * mm});
            skLineSegment(sketch, "E19.11.7.14", {"start": v(135.5, -448.8) * mm, "end": v(135.5, -487.97) * mm});
            skArc(sketch, "E19.14.7.14", {"start": v(142.5, -489.97) * mm, "mid": v(143.91, -489.39) * mm, "end": v(144.5, -487.97) * mm});
            skArc(sketch, "E19.18.7.14", {"start": v(135.5, -487.97) * mm, "mid": v(136.09, -489.39) * mm, "end": v(137.5, -489.97) * mm});
            skPoint(sketch, "E19.0.8.0", {"position": v(155.5, -5) * mm});
            skLineSegment(sketch, "E19.1.8.0", {"start": v(164.5, 36.17) * mm, "end": v(164.5, -3) * mm});
            skPoint(sketch, "E19.4.8.0", {"position": v(164.5, -5) * mm});
            skLineSegment(sketch, "E19.5.8.0", {"start": v(155.5, 36.17) * mm, "end": v(164.5, 36.17) * mm});
            skLineSegment(sketch, "E19.8.8.0", {"start": v(157.5, -5) * mm, "end": v(162.5, -5) * mm});
            skLineSegment(sketch, "E19.11.8.0", {"start": v(155.5, 36.17) * mm, "end": v(155.5, -3) * mm});
            skArc(sketch, "E19.14.8.0", {"start": v(162.5, -5) * mm, "mid": v(163.91, -4.41) * mm, "end": v(164.5, -3) * mm});
            skArc(sketch, "E19.18.8.0", {"start": v(155.5, -3) * mm, "mid": v(156.09, -4.41) * mm, "end": v(157.5, -5) * mm});
            skPoint(sketch, "E19.0.8.1", {"position": v(155.5, -39.64) * mm});
            skLineSegment(sketch, "E19.1.8.1", {"start": v(164.5, 1.53) * mm, "end": v(164.5, -37.64) * mm});
            skPoint(sketch, "E19.4.8.1", {"position": v(164.5, -39.64) * mm});
            skLineSegment(sketch, "E19.5.8.1", {"start": v(155.5, 1.53) * mm, "end": v(164.5, 1.53) * mm});
            skLineSegment(sketch, "E19.8.8.1", {"start": v(157.5, -39.64) * mm, "end": v(162.5, -39.64) * mm});
            skLineSegment(sketch, "E19.11.8.1", {"start": v(155.5, 1.53) * mm, "end": v(155.5, -37.64) * mm});
            skArc(sketch, "E19.14.8.1", {"start": v(162.5, -39.64) * mm, "mid": v(163.91, -39.06) * mm, "end": v(164.5, -37.64) * mm});
            skArc(sketch, "E19.18.8.1", {"start": v(155.5, -37.64) * mm, "mid": v(156.09, -39.06) * mm, "end": v(157.5, -39.64) * mm});
            skPoint(sketch, "E19.0.8.2", {"position": v(155.5, -74.28) * mm});
            skLineSegment(sketch, "E19.1.8.2", {"start": v(164.5, -33.1) * mm, "end": v(164.5, -72.28) * mm});
            skPoint(sketch, "E19.4.8.2", {"position": v(164.5, -74.28) * mm});
            skLineSegment(sketch, "E19.5.8.2", {"start": v(155.5, -33.1) * mm, "end": v(164.5, -33.1) * mm});
            skLineSegment(sketch, "E19.8.8.2", {"start": v(157.5, -74.28) * mm, "end": v(162.5, -74.28) * mm});
            skLineSegment(sketch, "E19.11.8.2", {"start": v(155.5, -33.1) * mm, "end": v(155.5, -72.28) * mm});
            skArc(sketch, "E19.14.8.2", {"start": v(162.5, -74.28) * mm, "mid": v(163.91, -73.7) * mm, "end": v(164.5, -72.28) * mm});
            skArc(sketch, "E19.18.8.2", {"start": v(155.5, -72.28) * mm, "mid": v(156.09, -73.7) * mm, "end": v(157.5, -74.28) * mm});
            skPoint(sketch, "E19.0.8.3", {"position": v(155.5, -108.92) * mm});
            skLineSegment(sketch, "E19.1.8.3", {"start": v(164.5, -67.75) * mm, "end": v(164.5, -106.92) * mm});
            skPoint(sketch, "E19.4.8.3", {"position": v(164.5, -108.92) * mm});
            skLineSegment(sketch, "E19.5.8.3", {"start": v(155.5, -67.75) * mm, "end": v(164.5, -67.75) * mm});
            skLineSegment(sketch, "E19.8.8.3", {"start": v(157.5, -108.92) * mm, "end": v(162.5, -108.92) * mm});
            skLineSegment(sketch, "E19.11.8.3", {"start": v(155.5, -67.75) * mm, "end": v(155.5, -106.92) * mm});
            skArc(sketch, "E19.14.8.3", {"start": v(162.5, -108.92) * mm, "mid": v(163.91, -108.34) * mm, "end": v(164.5, -106.92) * mm});
            skArc(sketch, "E19.18.8.3", {"start": v(155.5, -106.92) * mm, "mid": v(156.09, -108.34) * mm, "end": v(157.5, -108.92) * mm});
            skPoint(sketch, "E19.0.8.4", {"position": v(155.5, -143.56) * mm});
            skLineSegment(sketch, "E19.1.8.4", {"start": v(164.5, -102.4) * mm, "end": v(164.5, -141.56) * mm});
            skPoint(sketch, "E19.4.8.4", {"position": v(164.5, -143.56) * mm});
            skLineSegment(sketch, "E19.5.8.4", {"start": v(155.5, -102.4) * mm, "end": v(164.5, -102.4) * mm});
            skLineSegment(sketch, "E19.8.8.4", {"start": v(157.5, -143.56) * mm, "end": v(162.5, -143.56) * mm});
            skLineSegment(sketch, "E19.11.8.4", {"start": v(155.5, -102.4) * mm, "end": v(155.5, -141.56) * mm});
            skArc(sketch, "E19.14.8.4", {"start": v(162.5, -143.56) * mm, "mid": v(163.91, -142.98) * mm, "end": v(164.5, -141.56) * mm});
            skArc(sketch, "E19.18.8.4", {"start": v(155.5, -141.56) * mm, "mid": v(156.09, -142.98) * mm, "end": v(157.5, -143.56) * mm});
            skPoint(sketch, "E19.0.8.5", {"position": v(155.5, -178.2) * mm});
            skLineSegment(sketch, "E19.1.8.5", {"start": v(164.5, -137.03) * mm, "end": v(164.5, -176.2) * mm});
            skPoint(sketch, "E19.4.8.5", {"position": v(164.5, -178.2) * mm});
            skLineSegment(sketch, "E19.5.8.5", {"start": v(155.5, -137.03) * mm, "end": v(164.5, -137.03) * mm});
            skLineSegment(sketch, "E19.8.8.5", {"start": v(157.5, -178.2) * mm, "end": v(162.5, -178.2) * mm});
            skLineSegment(sketch, "E19.11.8.5", {"start": v(155.5, -137.03) * mm, "end": v(155.5, -176.2) * mm});
            skArc(sketch, "E19.14.8.5", {"start": v(162.5, -178.2) * mm, "mid": v(163.91, -177.62) * mm, "end": v(164.5, -176.2) * mm});
            skArc(sketch, "E19.18.8.5", {"start": v(155.5, -176.2) * mm, "mid": v(156.09, -177.62) * mm, "end": v(157.5, -178.2) * mm});
            skPoint(sketch, "E19.0.8.6", {"position": v(155.5, -212.85) * mm});
            skLineSegment(sketch, "E19.1.8.6", {"start": v(164.5, -171.67) * mm, "end": v(164.5, -210.85) * mm});
            skPoint(sketch, "E19.4.8.6", {"position": v(164.5, -212.85) * mm});
            skLineSegment(sketch, "E19.5.8.6", {"start": v(155.5, -171.67) * mm, "end": v(164.5, -171.67) * mm});
            skLineSegment(sketch, "E19.8.8.6", {"start": v(157.5, -212.85) * mm, "end": v(162.5, -212.85) * mm});
            skLineSegment(sketch, "E19.11.8.6", {"start": v(155.5, -171.67) * mm, "end": v(155.5, -210.85) * mm});
            skArc(sketch, "E19.14.8.6", {"start": v(162.5, -212.85) * mm, "mid": v(163.91, -212.26) * mm, "end": v(164.5, -210.85) * mm});
            skArc(sketch, "E19.18.8.6", {"start": v(155.5, -210.85) * mm, "mid": v(156.09, -212.26) * mm, "end": v(157.5, -212.85) * mm});
            skPoint(sketch, "E19.0.8.7", {"position": v(155.5, -247.49) * mm});
            skLineSegment(sketch, "E19.1.8.7", {"start": v(164.5, -206.31) * mm, "end": v(164.5, -245.49) * mm});
            skPoint(sketch, "E19.4.8.7", {"position": v(164.5, -247.49) * mm});
            skLineSegment(sketch, "E19.5.8.7", {"start": v(155.5, -206.31) * mm, "end": v(164.5, -206.31) * mm});
            skLineSegment(sketch, "E19.8.8.7", {"start": v(157.5, -247.49) * mm, "end": v(162.5, -247.49) * mm});
            skLineSegment(sketch, "E19.11.8.7", {"start": v(155.5, -206.31) * mm, "end": v(155.5, -245.49) * mm});
            skArc(sketch, "E19.14.8.7", {"start": v(162.5, -247.49) * mm, "mid": v(163.91, -246.9) * mm, "end": v(164.5, -245.49) * mm});
            skArc(sketch, "E19.18.8.7", {"start": v(155.5, -245.49) * mm, "mid": v(156.09, -246.9) * mm, "end": v(157.5, -247.49) * mm});
            skPoint(sketch, "E19.0.8.8", {"position": v(155.5, -282.13) * mm});
            skLineSegment(sketch, "E19.1.8.8", {"start": v(164.5, -240.95) * mm, "end": v(164.5, -280.13) * mm});
            skPoint(sketch, "E19.4.8.8", {"position": v(164.5, -282.13) * mm});
            skLineSegment(sketch, "E19.5.8.8", {"start": v(155.5, -240.95) * mm, "end": v(164.5, -240.95) * mm});
            skLineSegment(sketch, "E19.8.8.8", {"start": v(157.5, -282.13) * mm, "end": v(162.5, -282.13) * mm});
            skLineSegment(sketch, "E19.11.8.8", {"start": v(155.5, -240.95) * mm, "end": v(155.5, -280.13) * mm});
            skArc(sketch, "E19.14.8.8", {"start": v(162.5, -282.13) * mm, "mid": v(163.91, -281.54) * mm, "end": v(164.5, -280.13) * mm});
            skArc(sketch, "E19.18.8.8", {"start": v(155.5, -280.13) * mm, "mid": v(156.09, -281.54) * mm, "end": v(157.5, -282.13) * mm});
            skPoint(sketch, "E19.0.8.9", {"position": v(155.5, -316.77) * mm});
            skLineSegment(sketch, "E19.1.8.9", {"start": v(164.5, -275.6) * mm, "end": v(164.5, -314.77) * mm});
            skPoint(sketch, "E19.4.8.9", {"position": v(164.5, -316.77) * mm});
            skLineSegment(sketch, "E19.5.8.9", {"start": v(155.5, -275.6) * mm, "end": v(164.5, -275.6) * mm});
            skLineSegment(sketch, "E19.8.8.9", {"start": v(157.5, -316.77) * mm, "end": v(162.5, -316.77) * mm});
            skLineSegment(sketch, "E19.11.8.9", {"start": v(155.5, -275.6) * mm, "end": v(155.5, -314.77) * mm});
            skArc(sketch, "E19.14.8.9", {"start": v(162.5, -316.77) * mm, "mid": v(163.91, -316.18) * mm, "end": v(164.5, -314.77) * mm});
            skArc(sketch, "E19.18.8.9", {"start": v(155.5, -314.77) * mm, "mid": v(156.09, -316.18) * mm, "end": v(157.5, -316.77) * mm});
            skPoint(sketch, "E19.0.8.10", {"position": v(155.5, -351.41) * mm});
            skLineSegment(sketch, "E19.1.8.10", {"start": v(164.5, -310.24) * mm, "end": v(164.5, -349.41) * mm});
            skPoint(sketch, "E19.4.8.10", {"position": v(164.5, -351.41) * mm});
            skLineSegment(sketch, "E19.5.8.10", {"start": v(155.5, -310.24) * mm, "end": v(164.5, -310.24) * mm});
            skLineSegment(sketch, "E19.8.8.10", {"start": v(157.5, -351.41) * mm, "end": v(162.5, -351.41) * mm});
            skLineSegment(sketch, "E19.11.8.10", {"start": v(155.5, -310.24) * mm, "end": v(155.5, -349.41) * mm});
            skArc(sketch, "E19.14.8.10", {"start": v(162.5, -351.41) * mm, "mid": v(163.91, -350.82) * mm, "end": v(164.5, -349.41) * mm});
            skArc(sketch, "E19.18.8.10", {"start": v(155.5, -349.41) * mm, "mid": v(156.09, -350.82) * mm, "end": v(157.5, -351.41) * mm});
            skPoint(sketch, "E19.0.8.11", {"position": v(155.5, -386.05) * mm});
            skLineSegment(sketch, "E19.1.8.11", {"start": v(164.5, -344.88) * mm, "end": v(164.5, -384.05) * mm});
            skPoint(sketch, "E19.4.8.11", {"position": v(164.5, -386.05) * mm});
            skLineSegment(sketch, "E19.5.8.11", {"start": v(155.5, -344.88) * mm, "end": v(164.5, -344.88) * mm});
            skLineSegment(sketch, "E19.8.8.11", {"start": v(157.5, -386.05) * mm, "end": v(162.5, -386.05) * mm});
            skLineSegment(sketch, "E19.11.8.11", {"start": v(155.5, -344.88) * mm, "end": v(155.5, -384.05) * mm});
            skArc(sketch, "E19.14.8.11", {"start": v(162.5, -386.05) * mm, "mid": v(163.91, -385.47) * mm, "end": v(164.5, -384.05) * mm});
            skArc(sketch, "E19.18.8.11", {"start": v(155.5, -384.05) * mm, "mid": v(156.09, -385.47) * mm, "end": v(157.5, -386.05) * mm});
            skPoint(sketch, "E19.0.8.12", {"position": v(155.5, -420.7) * mm});
            skLineSegment(sketch, "E19.1.8.12", {"start": v(164.5, -379.52) * mm, "end": v(164.5, -418.7) * mm});
            skPoint(sketch, "E19.4.8.12", {"position": v(164.5, -420.7) * mm});
            skLineSegment(sketch, "E19.5.8.12", {"start": v(155.5, -379.52) * mm, "end": v(164.5, -379.52) * mm});
            skLineSegment(sketch, "E19.8.8.12", {"start": v(157.5, -420.7) * mm, "end": v(162.5, -420.7) * mm});
            skLineSegment(sketch, "E19.11.8.12", {"start": v(155.5, -379.52) * mm, "end": v(155.5, -418.7) * mm});
            skArc(sketch, "E19.14.8.12", {"start": v(162.5, -420.7) * mm, "mid": v(163.91, -420.1) * mm, "end": v(164.5, -418.7) * mm});
            skArc(sketch, "E19.18.8.12", {"start": v(155.5, -418.7) * mm, "mid": v(156.09, -420.1) * mm, "end": v(157.5, -420.7) * mm});
            skPoint(sketch, "E19.0.8.13", {"position": v(155.5, -455.33) * mm});
            skLineSegment(sketch, "E19.1.8.13", {"start": v(164.5, -414.16) * mm, "end": v(164.5, -453.33) * mm});
            skPoint(sketch, "E19.4.8.13", {"position": v(164.5, -455.33) * mm});
            skLineSegment(sketch, "E19.5.8.13", {"start": v(155.5, -414.16) * mm, "end": v(164.5, -414.16) * mm});
            skLineSegment(sketch, "E19.8.8.13", {"start": v(157.5, -455.33) * mm, "end": v(162.5, -455.33) * mm});
            skLineSegment(sketch, "E19.11.8.13", {"start": v(155.5, -414.16) * mm, "end": v(155.5, -453.33) * mm});
            skArc(sketch, "E19.14.8.13", {"start": v(162.5, -455.33) * mm, "mid": v(163.91, -454.75) * mm, "end": v(164.5, -453.33) * mm});
            skArc(sketch, "E19.18.8.13", {"start": v(155.5, -453.33) * mm, "mid": v(156.09, -454.75) * mm, "end": v(157.5, -455.33) * mm});
            skPoint(sketch, "E19.0.8.14", {"position": v(155.5, -489.97) * mm});
            skLineSegment(sketch, "E19.1.8.14", {"start": v(164.5, -448.8) * mm, "end": v(164.5, -487.97) * mm});
            skPoint(sketch, "E19.4.8.14", {"position": v(164.5, -489.97) * mm});
            skLineSegment(sketch, "E19.5.8.14", {"start": v(155.5, -448.8) * mm, "end": v(164.5, -448.8) * mm});
            skLineSegment(sketch, "E19.8.8.14", {"start": v(157.5, -489.97) * mm, "end": v(162.5, -489.97) * mm});
            skLineSegment(sketch, "E19.11.8.14", {"start": v(155.5, -448.8) * mm, "end": v(155.5, -487.97) * mm});
            skArc(sketch, "E19.14.8.14", {"start": v(162.5, -489.97) * mm, "mid": v(163.91, -489.39) * mm, "end": v(164.5, -487.97) * mm});
            skArc(sketch, "E19.18.8.14", {"start": v(155.5, -487.97) * mm, "mid": v(156.09, -489.39) * mm, "end": v(157.5, -489.97) * mm});
            skPoint(sketch, "E19.0.9.0", {"position": v(175.5, -5) * mm});
            skLineSegment(sketch, "E19.1.9.0", {"start": v(184.5, 36.17) * mm, "end": v(184.5, -3) * mm});
            skPoint(sketch, "E19.4.9.0", {"position": v(184.5, -5) * mm});
            skLineSegment(sketch, "E19.5.9.0", {"start": v(175.5, 36.17) * mm, "end": v(184.5, 36.17) * mm});
            skLineSegment(sketch, "E19.8.9.0", {"start": v(177.5, -5) * mm, "end": v(182.5, -5) * mm});
            skLineSegment(sketch, "E19.11.9.0", {"start": v(175.5, 36.17) * mm, "end": v(175.5, -3) * mm});
            skArc(sketch, "E19.14.9.0", {"start": v(182.5, -5) * mm, "mid": v(183.91, -4.41) * mm, "end": v(184.5, -3) * mm});
            skArc(sketch, "E19.18.9.0", {"start": v(175.5, -3) * mm, "mid": v(176.09, -4.41) * mm, "end": v(177.5, -5) * mm});
            skPoint(sketch, "E19.0.9.1", {"position": v(175.5, -39.64) * mm});
            skLineSegment(sketch, "E19.1.9.1", {"start": v(184.5, 1.53) * mm, "end": v(184.5, -37.64) * mm});
            skPoint(sketch, "E19.4.9.1", {"position": v(184.5, -39.64) * mm});
            skLineSegment(sketch, "E19.5.9.1", {"start": v(175.5, 1.53) * mm, "end": v(184.5, 1.53) * mm});
            skLineSegment(sketch, "E19.8.9.1", {"start": v(177.5, -39.64) * mm, "end": v(182.5, -39.64) * mm});
            skLineSegment(sketch, "E19.11.9.1", {"start": v(175.5, 1.53) * mm, "end": v(175.5, -37.64) * mm});
            skArc(sketch, "E19.14.9.1", {"start": v(182.5, -39.64) * mm, "mid": v(183.91, -39.06) * mm, "end": v(184.5, -37.64) * mm});
            skArc(sketch, "E19.18.9.1", {"start": v(175.5, -37.64) * mm, "mid": v(176.09, -39.06) * mm, "end": v(177.5, -39.64) * mm});
            skPoint(sketch, "E19.0.9.2", {"position": v(175.5, -74.28) * mm});
            skLineSegment(sketch, "E19.1.9.2", {"start": v(184.5, -33.1) * mm, "end": v(184.5, -72.28) * mm});
            skPoint(sketch, "E19.4.9.2", {"position": v(184.5, -74.28) * mm});
            skLineSegment(sketch, "E19.5.9.2", {"start": v(175.5, -33.1) * mm, "end": v(184.5, -33.1) * mm});
            skLineSegment(sketch, "E19.8.9.2", {"start": v(177.5, -74.28) * mm, "end": v(182.5, -74.28) * mm});
            skLineSegment(sketch, "E19.11.9.2", {"start": v(175.5, -33.1) * mm, "end": v(175.5, -72.28) * mm});
            skArc(sketch, "E19.14.9.2", {"start": v(182.5, -74.28) * mm, "mid": v(183.91, -73.7) * mm, "end": v(184.5, -72.28) * mm});
            skArc(sketch, "E19.18.9.2", {"start": v(175.5, -72.28) * mm, "mid": v(176.09, -73.7) * mm, "end": v(177.5, -74.28) * mm});
            skPoint(sketch, "E19.0.9.3", {"position": v(175.5, -108.92) * mm});
            skLineSegment(sketch, "E19.1.9.3", {"start": v(184.5, -67.75) * mm, "end": v(184.5, -106.92) * mm});
            skPoint(sketch, "E19.4.9.3", {"position": v(184.5, -108.92) * mm});
            skLineSegment(sketch, "E19.5.9.3", {"start": v(175.5, -67.75) * mm, "end": v(184.5, -67.75) * mm});
            skLineSegment(sketch, "E19.8.9.3", {"start": v(177.5, -108.92) * mm, "end": v(182.5, -108.92) * mm});
            skLineSegment(sketch, "E19.11.9.3", {"start": v(175.5, -67.75) * mm, "end": v(175.5, -106.92) * mm});
            skArc(sketch, "E19.14.9.3", {"start": v(182.5, -108.92) * mm, "mid": v(183.91, -108.34) * mm, "end": v(184.5, -106.92) * mm});
            skArc(sketch, "E19.18.9.3", {"start": v(175.5, -106.92) * mm, "mid": v(176.09, -108.34) * mm, "end": v(177.5, -108.92) * mm});
            skPoint(sketch, "E19.0.9.4", {"position": v(175.5, -143.56) * mm});
            skLineSegment(sketch, "E19.1.9.4", {"start": v(184.5, -102.4) * mm, "end": v(184.5, -141.56) * mm});
            skPoint(sketch, "E19.4.9.4", {"position": v(184.5, -143.56) * mm});
            skLineSegment(sketch, "E19.5.9.4", {"start": v(175.5, -102.4) * mm, "end": v(184.5, -102.4) * mm});
            skLineSegment(sketch, "E19.8.9.4", {"start": v(177.5, -143.56) * mm, "end": v(182.5, -143.56) * mm});
            skLineSegment(sketch, "E19.11.9.4", {"start": v(175.5, -102.4) * mm, "end": v(175.5, -141.56) * mm});
            skArc(sketch, "E19.14.9.4", {"start": v(182.5, -143.56) * mm, "mid": v(183.91, -142.98) * mm, "end": v(184.5, -141.56) * mm});
            skArc(sketch, "E19.18.9.4", {"start": v(175.5, -141.56) * mm, "mid": v(176.09, -142.98) * mm, "end": v(177.5, -143.56) * mm});
            skPoint(sketch, "E19.0.9.5", {"position": v(175.5, -178.2) * mm});
            skLineSegment(sketch, "E19.1.9.5", {"start": v(184.5, -137.03) * mm, "end": v(184.5, -176.2) * mm});
            skPoint(sketch, "E19.4.9.5", {"position": v(184.5, -178.2) * mm});
            skLineSegment(sketch, "E19.5.9.5", {"start": v(175.5, -137.03) * mm, "end": v(184.5, -137.03) * mm});
            skLineSegment(sketch, "E19.8.9.5", {"start": v(177.5, -178.2) * mm, "end": v(182.5, -178.2) * mm});
            skLineSegment(sketch, "E19.11.9.5", {"start": v(175.5, -137.03) * mm, "end": v(175.5, -176.2) * mm});
            skArc(sketch, "E19.14.9.5", {"start": v(182.5, -178.2) * mm, "mid": v(183.91, -177.62) * mm, "end": v(184.5, -176.2) * mm});
            skArc(sketch, "E19.18.9.5", {"start": v(175.5, -176.2) * mm, "mid": v(176.09, -177.62) * mm, "end": v(177.5, -178.2) * mm});
            skPoint(sketch, "E19.0.9.6", {"position": v(175.5, -212.85) * mm});
            skLineSegment(sketch, "E19.1.9.6", {"start": v(184.5, -171.67) * mm, "end": v(184.5, -210.85) * mm});
            skPoint(sketch, "E19.4.9.6", {"position": v(184.5, -212.85) * mm});
            skLineSegment(sketch, "E19.5.9.6", {"start": v(175.5, -171.67) * mm, "end": v(184.5, -171.67) * mm});
            skLineSegment(sketch, "E19.8.9.6", {"start": v(177.5, -212.85) * mm, "end": v(182.5, -212.85) * mm});
            skLineSegment(sketch, "E19.11.9.6", {"start": v(175.5, -171.67) * mm, "end": v(175.5, -210.85) * mm});
            skArc(sketch, "E19.14.9.6", {"start": v(182.5, -212.85) * mm, "mid": v(183.91, -212.26) * mm, "end": v(184.5, -210.85) * mm});
            skArc(sketch, "E19.18.9.6", {"start": v(175.5, -210.85) * mm, "mid": v(176.09, -212.26) * mm, "end": v(177.5, -212.85) * mm});
            skPoint(sketch, "E19.0.9.7", {"position": v(175.5, -247.49) * mm});
            skLineSegment(sketch, "E19.1.9.7", {"start": v(184.5, -206.31) * mm, "end": v(184.5, -245.49) * mm});
            skPoint(sketch, "E19.4.9.7", {"position": v(184.5, -247.49) * mm});
            skLineSegment(sketch, "E19.5.9.7", {"start": v(175.5, -206.31) * mm, "end": v(184.5, -206.31) * mm});
            skLineSegment(sketch, "E19.8.9.7", {"start": v(177.5, -247.49) * mm, "end": v(182.5, -247.49) * mm});
            skLineSegment(sketch, "E19.11.9.7", {"start": v(175.5, -206.31) * mm, "end": v(175.5, -245.49) * mm});
            skArc(sketch, "E19.14.9.7", {"start": v(182.5, -247.49) * mm, "mid": v(183.91, -246.9) * mm, "end": v(184.5, -245.49) * mm});
            skArc(sketch, "E19.18.9.7", {"start": v(175.5, -245.49) * mm, "mid": v(176.09, -246.9) * mm, "end": v(177.5, -247.49) * mm});
            skPoint(sketch, "E19.0.9.8", {"position": v(175.5, -282.13) * mm});
            skLineSegment(sketch, "E19.1.9.8", {"start": v(184.5, -240.95) * mm, "end": v(184.5, -280.13) * mm});
            skPoint(sketch, "E19.4.9.8", {"position": v(184.5, -282.13) * mm});
            skLineSegment(sketch, "E19.5.9.8", {"start": v(175.5, -240.95) * mm, "end": v(184.5, -240.95) * mm});
            skLineSegment(sketch, "E19.8.9.8", {"start": v(177.5, -282.13) * mm, "end": v(182.5, -282.13) * mm});
            skLineSegment(sketch, "E19.11.9.8", {"start": v(175.5, -240.95) * mm, "end": v(175.5, -280.13) * mm});
            skArc(sketch, "E19.14.9.8", {"start": v(182.5, -282.13) * mm, "mid": v(183.91, -281.54) * mm, "end": v(184.5, -280.13) * mm});
            skArc(sketch, "E19.18.9.8", {"start": v(175.5, -280.13) * mm, "mid": v(176.09, -281.54) * mm, "end": v(177.5, -282.13) * mm});
            skPoint(sketch, "E19.0.9.9", {"position": v(175.5, -316.77) * mm});
            skLineSegment(sketch, "E19.1.9.9", {"start": v(184.5, -275.6) * mm, "end": v(184.5, -314.77) * mm});
            skPoint(sketch, "E19.4.9.9", {"position": v(184.5, -316.77) * mm});
            skLineSegment(sketch, "E19.5.9.9", {"start": v(175.5, -275.6) * mm, "end": v(184.5, -275.6) * mm});
            skLineSegment(sketch, "E19.8.9.9", {"start": v(177.5, -316.77) * mm, "end": v(182.5, -316.77) * mm});
            skLineSegment(sketch, "E19.11.9.9", {"start": v(175.5, -275.6) * mm, "end": v(175.5, -314.77) * mm});
            skArc(sketch, "E19.14.9.9", {"start": v(182.5, -316.77) * mm, "mid": v(183.91, -316.18) * mm, "end": v(184.5, -314.77) * mm});
            skArc(sketch, "E19.18.9.9", {"start": v(175.5, -314.77) * mm, "mid": v(176.09, -316.18) * mm, "end": v(177.5, -316.77) * mm});
            skPoint(sketch, "E19.0.9.10", {"position": v(175.5, -351.41) * mm});
            skLineSegment(sketch, "E19.1.9.10", {"start": v(184.5, -310.24) * mm, "end": v(184.5, -349.41) * mm});
            skPoint(sketch, "E19.4.9.10", {"position": v(184.5, -351.41) * mm});
            skLineSegment(sketch, "E19.5.9.10", {"start": v(175.5, -310.24) * mm, "end": v(184.5, -310.24) * mm});
            skLineSegment(sketch, "E19.8.9.10", {"start": v(177.5, -351.41) * mm, "end": v(182.5, -351.41) * mm});
            skLineSegment(sketch, "E19.11.9.10", {"start": v(175.5, -310.24) * mm, "end": v(175.5, -349.41) * mm});
            skArc(sketch, "E19.14.9.10", {"start": v(182.5, -351.41) * mm, "mid": v(183.91, -350.82) * mm, "end": v(184.5, -349.41) * mm});
            skArc(sketch, "E19.18.9.10", {"start": v(175.5, -349.41) * mm, "mid": v(176.09, -350.82) * mm, "end": v(177.5, -351.41) * mm});
            skPoint(sketch, "E19.0.9.11", {"position": v(175.5, -386.05) * mm});
            skLineSegment(sketch, "E19.1.9.11", {"start": v(184.5, -344.88) * mm, "end": v(184.5, -384.05) * mm});
            skPoint(sketch, "E19.4.9.11", {"position": v(184.5, -386.05) * mm});
            skLineSegment(sketch, "E19.5.9.11", {"start": v(175.5, -344.88) * mm, "end": v(184.5, -344.88) * mm});
            skLineSegment(sketch, "E19.8.9.11", {"start": v(177.5, -386.05) * mm, "end": v(182.5, -386.05) * mm});
            skLineSegment(sketch, "E19.11.9.11", {"start": v(175.5, -344.88) * mm, "end": v(175.5, -384.05) * mm});
            skArc(sketch, "E19.14.9.11", {"start": v(182.5, -386.05) * mm, "mid": v(183.91, -385.47) * mm, "end": v(184.5, -384.05) * mm});
            skArc(sketch, "E19.18.9.11", {"start": v(175.5, -384.05) * mm, "mid": v(176.09, -385.47) * mm, "end": v(177.5, -386.05) * mm});
            skPoint(sketch, "E19.0.9.12", {"position": v(175.5, -420.7) * mm});
            skLineSegment(sketch, "E19.1.9.12", {"start": v(184.5, -379.52) * mm, "end": v(184.5, -418.7) * mm});
            skPoint(sketch, "E19.4.9.12", {"position": v(184.5, -420.7) * mm});
            skLineSegment(sketch, "E19.5.9.12", {"start": v(175.5, -379.52) * mm, "end": v(184.5, -379.52) * mm});
            skLineSegment(sketch, "E19.8.9.12", {"start": v(177.5, -420.7) * mm, "end": v(182.5, -420.7) * mm});
            skLineSegment(sketch, "E19.11.9.12", {"start": v(175.5, -379.52) * mm, "end": v(175.5, -418.7) * mm});
            skArc(sketch, "E19.14.9.12", {"start": v(182.5, -420.7) * mm, "mid": v(183.91, -420.1) * mm, "end": v(184.5, -418.7) * mm});
            skArc(sketch, "E19.18.9.12", {"start": v(175.5, -418.7) * mm, "mid": v(176.09, -420.1) * mm, "end": v(177.5, -420.7) * mm});
            skPoint(sketch, "E19.0.9.13", {"position": v(175.5, -455.33) * mm});
            skLineSegment(sketch, "E19.1.9.13", {"start": v(184.5, -414.16) * mm, "end": v(184.5, -453.33) * mm});
            skPoint(sketch, "E19.4.9.13", {"position": v(184.5, -455.33) * mm});
            skLineSegment(sketch, "E19.5.9.13", {"start": v(175.5, -414.16) * mm, "end": v(184.5, -414.16) * mm});
            skLineSegment(sketch, "E19.8.9.13", {"start": v(177.5, -455.33) * mm, "end": v(182.5, -455.33) * mm});
            skLineSegment(sketch, "E19.11.9.13", {"start": v(175.5, -414.16) * mm, "end": v(175.5, -453.33) * mm});
            skArc(sketch, "E19.14.9.13", {"start": v(182.5, -455.33) * mm, "mid": v(183.91, -454.75) * mm, "end": v(184.5, -453.33) * mm});
            skArc(sketch, "E19.18.9.13", {"start": v(175.5, -453.33) * mm, "mid": v(176.09, -454.75) * mm, "end": v(177.5, -455.33) * mm});
            skPoint(sketch, "E19.0.9.14", {"position": v(175.5, -489.97) * mm});
            skLineSegment(sketch, "E19.1.9.14", {"start": v(184.5, -448.8) * mm, "end": v(184.5, -487.97) * mm});
            skPoint(sketch, "E19.4.9.14", {"position": v(184.5, -489.97) * mm});
            skLineSegment(sketch, "E19.5.9.14", {"start": v(175.5, -448.8) * mm, "end": v(184.5, -448.8) * mm});
            skLineSegment(sketch, "E19.8.9.14", {"start": v(177.5, -489.97) * mm, "end": v(182.5, -489.97) * mm});
            skLineSegment(sketch, "E19.11.9.14", {"start": v(175.5, -448.8) * mm, "end": v(175.5, -487.97) * mm});
            skArc(sketch, "E19.14.9.14", {"start": v(182.5, -489.97) * mm, "mid": v(183.91, -489.39) * mm, "end": v(184.5, -487.97) * mm});
            skArc(sketch, "E19.18.9.14", {"start": v(175.5, -487.97) * mm, "mid": v(176.09, -489.39) * mm, "end": v(177.5, -489.97) * mm});
            skPoint(sketch, "E19.0.10.0", {"position": v(195.5, -5) * mm});
            skLineSegment(sketch, "E19.1.10.0", {"start": v(204.5, 36.17) * mm, "end": v(204.5, -3) * mm});
            skPoint(sketch, "E19.4.10.0", {"position": v(204.5, -5) * mm});
            skLineSegment(sketch, "E19.5.10.0", {"start": v(195.5, 36.17) * mm, "end": v(204.5, 36.17) * mm});
            skLineSegment(sketch, "E19.8.10.0", {"start": v(197.5, -5) * mm, "end": v(202.5, -5) * mm});
            skLineSegment(sketch, "E19.11.10.0", {"start": v(195.5, 36.17) * mm, "end": v(195.5, -3) * mm});
            skArc(sketch, "E19.14.10.0", {"start": v(202.5, -5) * mm, "mid": v(203.91, -4.41) * mm, "end": v(204.5, -3) * mm});
            skArc(sketch, "E19.18.10.0", {"start": v(195.5, -3) * mm, "mid": v(196.09, -4.41) * mm, "end": v(197.5, -5) * mm});
            skPoint(sketch, "E19.0.10.1", {"position": v(195.5, -39.64) * mm});
            skLineSegment(sketch, "E19.1.10.1", {"start": v(204.5, 1.53) * mm, "end": v(204.5, -37.64) * mm});
            skPoint(sketch, "E19.4.10.1", {"position": v(204.5, -39.64) * mm});
            skLineSegment(sketch, "E19.5.10.1", {"start": v(195.5, 1.53) * mm, "end": v(204.5, 1.53) * mm});
            skLineSegment(sketch, "E19.8.10.1", {"start": v(197.5, -39.64) * mm, "end": v(202.5, -39.64) * mm});
            skLineSegment(sketch, "E19.11.10.1", {"start": v(195.5, 1.53) * mm, "end": v(195.5, -37.64) * mm});
            skArc(sketch, "E19.14.10.1", {"start": v(202.5, -39.64) * mm, "mid": v(203.91, -39.06) * mm, "end": v(204.5, -37.64) * mm});
            skArc(sketch, "E19.18.10.1", {"start": v(195.5, -37.64) * mm, "mid": v(196.09, -39.06) * mm, "end": v(197.5, -39.64) * mm});
            skPoint(sketch, "E19.0.10.2", {"position": v(195.5, -74.28) * mm});
            skLineSegment(sketch, "E19.1.10.2", {"start": v(204.5, -33.1) * mm, "end": v(204.5, -72.28) * mm});
            skPoint(sketch, "E19.4.10.2", {"position": v(204.5, -74.28) * mm});
            skLineSegment(sketch, "E19.5.10.2", {"start": v(195.5, -33.1) * mm, "end": v(204.5, -33.1) * mm});
            skLineSegment(sketch, "E19.8.10.2", {"start": v(197.5, -74.28) * mm, "end": v(202.5, -74.28) * mm});
            skLineSegment(sketch, "E19.11.10.2", {"start": v(195.5, -33.1) * mm, "end": v(195.5, -72.28) * mm});
            skArc(sketch, "E19.14.10.2", {"start": v(202.5, -74.28) * mm, "mid": v(203.91, -73.7) * mm, "end": v(204.5, -72.28) * mm});
            skArc(sketch, "E19.18.10.2", {"start": v(195.5, -72.28) * mm, "mid": v(196.09, -73.7) * mm, "end": v(197.5, -74.28) * mm});
            skPoint(sketch, "E19.0.10.3", {"position": v(195.5, -108.92) * mm});
            skLineSegment(sketch, "E19.1.10.3", {"start": v(204.5, -67.75) * mm, "end": v(204.5, -106.92) * mm});
            skPoint(sketch, "E19.4.10.3", {"position": v(204.5, -108.92) * mm});
            skLineSegment(sketch, "E19.5.10.3", {"start": v(195.5, -67.75) * mm, "end": v(204.5, -67.75) * mm});
            skLineSegment(sketch, "E19.8.10.3", {"start": v(197.5, -108.92) * mm, "end": v(202.5, -108.92) * mm});
            skLineSegment(sketch, "E19.11.10.3", {"start": v(195.5, -67.75) * mm, "end": v(195.5, -106.92) * mm});
            skArc(sketch, "E19.14.10.3", {"start": v(202.5, -108.92) * mm, "mid": v(203.91, -108.34) * mm, "end": v(204.5, -106.92) * mm});
            skArc(sketch, "E19.18.10.3", {"start": v(195.5, -106.92) * mm, "mid": v(196.09, -108.34) * mm, "end": v(197.5, -108.92) * mm});
            skPoint(sketch, "E19.0.10.4", {"position": v(195.5, -143.56) * mm});
            skLineSegment(sketch, "E19.1.10.4", {"start": v(204.5, -102.4) * mm, "end": v(204.5, -141.56) * mm});
            skPoint(sketch, "E19.4.10.4", {"position": v(204.5, -143.56) * mm});
            skLineSegment(sketch, "E19.5.10.4", {"start": v(195.5, -102.4) * mm, "end": v(204.5, -102.4) * mm});
            skLineSegment(sketch, "E19.8.10.4", {"start": v(197.5, -143.56) * mm, "end": v(202.5, -143.56) * mm});
            skLineSegment(sketch, "E19.11.10.4", {"start": v(195.5, -102.4) * mm, "end": v(195.5, -141.56) * mm});
            skArc(sketch, "E19.14.10.4", {"start": v(202.5, -143.56) * mm, "mid": v(203.91, -142.98) * mm, "end": v(204.5, -141.56) * mm});
            skArc(sketch, "E19.18.10.4", {"start": v(195.5, -141.56) * mm, "mid": v(196.09, -142.98) * mm, "end": v(197.5, -143.56) * mm});
            skPoint(sketch, "E19.0.10.5", {"position": v(195.5, -178.2) * mm});
            skLineSegment(sketch, "E19.1.10.5", {"start": v(204.5, -137.03) * mm, "end": v(204.5, -176.2) * mm});
            skPoint(sketch, "E19.4.10.5", {"position": v(204.5, -178.2) * mm});
            skLineSegment(sketch, "E19.5.10.5", {"start": v(195.5, -137.03) * mm, "end": v(204.5, -137.03) * mm});
            skLineSegment(sketch, "E19.8.10.5", {"start": v(197.5, -178.2) * mm, "end": v(202.5, -178.2) * mm});
            skLineSegment(sketch, "E19.11.10.5", {"start": v(195.5, -137.03) * mm, "end": v(195.5, -176.2) * mm});
            skArc(sketch, "E19.14.10.5", {"start": v(202.5, -178.2) * mm, "mid": v(203.91, -177.62) * mm, "end": v(204.5, -176.2) * mm});
            skArc(sketch, "E19.18.10.5", {"start": v(195.5, -176.2) * mm, "mid": v(196.09, -177.62) * mm, "end": v(197.5, -178.2) * mm});
            skPoint(sketch, "E19.0.10.6", {"position": v(195.5, -212.85) * mm});
            skLineSegment(sketch, "E19.1.10.6", {"start": v(204.5, -171.67) * mm, "end": v(204.5, -210.85) * mm});
            skPoint(sketch, "E19.4.10.6", {"position": v(204.5, -212.85) * mm});
            skLineSegment(sketch, "E19.5.10.6", {"start": v(195.5, -171.67) * mm, "end": v(204.5, -171.67) * mm});
            skLineSegment(sketch, "E19.8.10.6", {"start": v(197.5, -212.85) * mm, "end": v(202.5, -212.85) * mm});
            skLineSegment(sketch, "E19.11.10.6", {"start": v(195.5, -171.67) * mm, "end": v(195.5, -210.85) * mm});
            skArc(sketch, "E19.14.10.6", {"start": v(202.5, -212.85) * mm, "mid": v(203.91, -212.26) * mm, "end": v(204.5, -210.85) * mm});
            skArc(sketch, "E19.18.10.6", {"start": v(195.5, -210.85) * mm, "mid": v(196.09, -212.26) * mm, "end": v(197.5, -212.85) * mm});
            skPoint(sketch, "E19.0.10.7", {"position": v(195.5, -247.49) * mm});
            skLineSegment(sketch, "E19.1.10.7", {"start": v(204.5, -206.31) * mm, "end": v(204.5, -245.49) * mm});
            skPoint(sketch, "E19.4.10.7", {"position": v(204.5, -247.49) * mm});
            skLineSegment(sketch, "E19.5.10.7", {"start": v(195.5, -206.31) * mm, "end": v(204.5, -206.31) * mm});
            skLineSegment(sketch, "E19.8.10.7", {"start": v(197.5, -247.49) * mm, "end": v(202.5, -247.49) * mm});
            skLineSegment(sketch, "E19.11.10.7", {"start": v(195.5, -206.31) * mm, "end": v(195.5, -245.49) * mm});
            skArc(sketch, "E19.14.10.7", {"start": v(202.5, -247.49) * mm, "mid": v(203.91, -246.9) * mm, "end": v(204.5, -245.49) * mm});
            skArc(sketch, "E19.18.10.7", {"start": v(195.5, -245.49) * mm, "mid": v(196.09, -246.9) * mm, "end": v(197.5, -247.49) * mm});
            skPoint(sketch, "E19.0.10.8", {"position": v(195.5, -282.13) * mm});
            skLineSegment(sketch, "E19.1.10.8", {"start": v(204.5, -240.95) * mm, "end": v(204.5, -280.13) * mm});
            skPoint(sketch, "E19.4.10.8", {"position": v(204.5, -282.13) * mm});
            skLineSegment(sketch, "E19.5.10.8", {"start": v(195.5, -240.95) * mm, "end": v(204.5, -240.95) * mm});
            skLineSegment(sketch, "E19.8.10.8", {"start": v(197.5, -282.13) * mm, "end": v(202.5, -282.13) * mm});
            skLineSegment(sketch, "E19.11.10.8", {"start": v(195.5, -240.95) * mm, "end": v(195.5, -280.13) * mm});
            skArc(sketch, "E19.14.10.8", {"start": v(202.5, -282.13) * mm, "mid": v(203.91, -281.54) * mm, "end": v(204.5, -280.13) * mm});
            skArc(sketch, "E19.18.10.8", {"start": v(195.5, -280.13) * mm, "mid": v(196.09, -281.54) * mm, "end": v(197.5, -282.13) * mm});
            skPoint(sketch, "E19.0.10.9", {"position": v(195.5, -316.77) * mm});
            skLineSegment(sketch, "E19.1.10.9", {"start": v(204.5, -275.6) * mm, "end": v(204.5, -314.77) * mm});
            skPoint(sketch, "E19.4.10.9", {"position": v(204.5, -316.77) * mm});
            skLineSegment(sketch, "E19.5.10.9", {"start": v(195.5, -275.6) * mm, "end": v(204.5, -275.6) * mm});
            skLineSegment(sketch, "E19.8.10.9", {"start": v(197.5, -316.77) * mm, "end": v(202.5, -316.77) * mm});
            skLineSegment(sketch, "E19.11.10.9", {"start": v(195.5, -275.6) * mm, "end": v(195.5, -314.77) * mm});
            skArc(sketch, "E19.14.10.9", {"start": v(202.5, -316.77) * mm, "mid": v(203.91, -316.18) * mm, "end": v(204.5, -314.77) * mm});
            skArc(sketch, "E19.18.10.9", {"start": v(195.5, -314.77) * mm, "mid": v(196.09, -316.18) * mm, "end": v(197.5, -316.77) * mm});
            skPoint(sketch, "E19.0.10.10", {"position": v(195.5, -351.41) * mm});
            skLineSegment(sketch, "E19.1.10.10", {"start": v(204.5, -310.24) * mm, "end": v(204.5, -349.41) * mm});
            skPoint(sketch, "E19.4.10.10", {"position": v(204.5, -351.41) * mm});
            skLineSegment(sketch, "E19.5.10.10", {"start": v(195.5, -310.24) * mm, "end": v(204.5, -310.24) * mm});
            skLineSegment(sketch, "E19.8.10.10", {"start": v(197.5, -351.41) * mm, "end": v(202.5, -351.41) * mm});
            skLineSegment(sketch, "E19.11.10.10", {"start": v(195.5, -310.24) * mm, "end": v(195.5, -349.41) * mm});
            skArc(sketch, "E19.14.10.10", {"start": v(202.5, -351.41) * mm, "mid": v(203.91, -350.82) * mm, "end": v(204.5, -349.41) * mm});
            skArc(sketch, "E19.18.10.10", {"start": v(195.5, -349.41) * mm, "mid": v(196.09, -350.82) * mm, "end": v(197.5, -351.41) * mm});
            skPoint(sketch, "E19.0.10.11", {"position": v(195.5, -386.05) * mm});
            skLineSegment(sketch, "E19.1.10.11", {"start": v(204.5, -344.88) * mm, "end": v(204.5, -384.05) * mm});
            skPoint(sketch, "E19.4.10.11", {"position": v(204.5, -386.05) * mm});
            skLineSegment(sketch, "E19.5.10.11", {"start": v(195.5, -344.88) * mm, "end": v(204.5, -344.88) * mm});
            skLineSegment(sketch, "E19.8.10.11", {"start": v(197.5, -386.05) * mm, "end": v(202.5, -386.05) * mm});
            skLineSegment(sketch, "E19.11.10.11", {"start": v(195.5, -344.88) * mm, "end": v(195.5, -384.05) * mm});
            skArc(sketch, "E19.14.10.11", {"start": v(202.5, -386.05) * mm, "mid": v(203.91, -385.47) * mm, "end": v(204.5, -384.05) * mm});
            skArc(sketch, "E19.18.10.11", {"start": v(195.5, -384.05) * mm, "mid": v(196.09, -385.47) * mm, "end": v(197.5, -386.05) * mm});
            skPoint(sketch, "E19.0.10.12", {"position": v(195.5, -420.7) * mm});
            skLineSegment(sketch, "E19.1.10.12", {"start": v(204.5, -379.52) * mm, "end": v(204.5, -418.7) * mm});
            skPoint(sketch, "E19.4.10.12", {"position": v(204.5, -420.7) * mm});
            skLineSegment(sketch, "E19.5.10.12", {"start": v(195.5, -379.52) * mm, "end": v(204.5, -379.52) * mm});
            skLineSegment(sketch, "E19.8.10.12", {"start": v(197.5, -420.7) * mm, "end": v(202.5, -420.7) * mm});
            skLineSegment(sketch, "E19.11.10.12", {"start": v(195.5, -379.52) * mm, "end": v(195.5, -418.7) * mm});
            skArc(sketch, "E19.14.10.12", {"start": v(202.5, -420.7) * mm, "mid": v(203.91, -420.1) * mm, "end": v(204.5, -418.7) * mm});
            skArc(sketch, "E19.18.10.12", {"start": v(195.5, -418.7) * mm, "mid": v(196.09, -420.1) * mm, "end": v(197.5, -420.7) * mm});
            skPoint(sketch, "E19.0.10.13", {"position": v(195.5, -455.33) * mm});
            skLineSegment(sketch, "E19.1.10.13", {"start": v(204.5, -414.16) * mm, "end": v(204.5, -453.33) * mm});
            skPoint(sketch, "E19.4.10.13", {"position": v(204.5, -455.33) * mm});
            skLineSegment(sketch, "E19.5.10.13", {"start": v(195.5, -414.16) * mm, "end": v(204.5, -414.16) * mm});
            skLineSegment(sketch, "E19.8.10.13", {"start": v(197.5, -455.33) * mm, "end": v(202.5, -455.33) * mm});
            skLineSegment(sketch, "E19.11.10.13", {"start": v(195.5, -414.16) * mm, "end": v(195.5, -453.33) * mm});
            skArc(sketch, "E19.14.10.13", {"start": v(202.5, -455.33) * mm, "mid": v(203.91, -454.75) * mm, "end": v(204.5, -453.33) * mm});
            skArc(sketch, "E19.18.10.13", {"start": v(195.5, -453.33) * mm, "mid": v(196.09, -454.75) * mm, "end": v(197.5, -455.33) * mm});
            skPoint(sketch, "E19.0.10.14", {"position": v(195.5, -489.97) * mm});
            skLineSegment(sketch, "E19.1.10.14", {"start": v(204.5, -448.8) * mm, "end": v(204.5, -487.97) * mm});
            skPoint(sketch, "E19.4.10.14", {"position": v(204.5, -489.97) * mm});
            skLineSegment(sketch, "E19.5.10.14", {"start": v(195.5, -448.8) * mm, "end": v(204.5, -448.8) * mm});
            skLineSegment(sketch, "E19.8.10.14", {"start": v(197.5, -489.97) * mm, "end": v(202.5, -489.97) * mm});
            skLineSegment(sketch, "E19.11.10.14", {"start": v(195.5, -448.8) * mm, "end": v(195.5, -487.97) * mm});
            skArc(sketch, "E19.14.10.14", {"start": v(202.5, -489.97) * mm, "mid": v(203.91, -489.39) * mm, "end": v(204.5, -487.97) * mm});
            skArc(sketch, "E19.18.10.14", {"start": v(195.5, -487.97) * mm, "mid": v(196.09, -489.39) * mm, "end": v(197.5, -489.97) * mm});
            skPoint(sketch, "E19.0.11.0", {"position": v(215.5, -5) * mm});
            skLineSegment(sketch, "E19.1.11.0", {"start": v(224.5, 36.17) * mm, "end": v(224.5, -3) * mm});
            skPoint(sketch, "E19.4.11.0", {"position": v(224.5, -5) * mm});
            skLineSegment(sketch, "E19.5.11.0", {"start": v(215.5, 36.17) * mm, "end": v(224.5, 36.17) * mm});
            skLineSegment(sketch, "E19.8.11.0", {"start": v(217.5, -5) * mm, "end": v(222.5, -5) * mm});
            skLineSegment(sketch, "E19.11.11.0", {"start": v(215.5, 36.17) * mm, "end": v(215.5, -3) * mm});
            skArc(sketch, "E19.14.11.0", {"start": v(222.5, -5) * mm, "mid": v(223.91, -4.41) * mm, "end": v(224.5, -3) * mm});
            skArc(sketch, "E19.18.11.0", {"start": v(215.5, -3) * mm, "mid": v(216.09, -4.41) * mm, "end": v(217.5, -5) * mm});
            skPoint(sketch, "E19.0.11.1", {"position": v(215.5, -39.64) * mm});
            skLineSegment(sketch, "E19.1.11.1", {"start": v(224.5, 1.53) * mm, "end": v(224.5, -37.64) * mm});
            skPoint(sketch, "E19.4.11.1", {"position": v(224.5, -39.64) * mm});
            skLineSegment(sketch, "E19.5.11.1", {"start": v(215.5, 1.53) * mm, "end": v(224.5, 1.53) * mm});
            skLineSegment(sketch, "E19.8.11.1", {"start": v(217.5, -39.64) * mm, "end": v(222.5, -39.64) * mm});
            skLineSegment(sketch, "E19.11.11.1", {"start": v(215.5, 1.53) * mm, "end": v(215.5, -37.64) * mm});
            skArc(sketch, "E19.14.11.1", {"start": v(222.5, -39.64) * mm, "mid": v(223.91, -39.06) * mm, "end": v(224.5, -37.64) * mm});
            skArc(sketch, "E19.18.11.1", {"start": v(215.5, -37.64) * mm, "mid": v(216.09, -39.06) * mm, "end": v(217.5, -39.64) * mm});
            skPoint(sketch, "E19.0.11.2", {"position": v(215.5, -74.28) * mm});
            skLineSegment(sketch, "E19.1.11.2", {"start": v(224.5, -33.1) * mm, "end": v(224.5, -72.28) * mm});
            skPoint(sketch, "E19.4.11.2", {"position": v(224.5, -74.28) * mm});
            skLineSegment(sketch, "E19.5.11.2", {"start": v(215.5, -33.1) * mm, "end": v(224.5, -33.1) * mm});
            skLineSegment(sketch, "E19.8.11.2", {"start": v(217.5, -74.28) * mm, "end": v(222.5, -74.28) * mm});
            skLineSegment(sketch, "E19.11.11.2", {"start": v(215.5, -33.1) * mm, "end": v(215.5, -72.28) * mm});
            skArc(sketch, "E19.14.11.2", {"start": v(222.5, -74.28) * mm, "mid": v(223.91, -73.7) * mm, "end": v(224.5, -72.28) * mm});
            skArc(sketch, "E19.18.11.2", {"start": v(215.5, -72.28) * mm, "mid": v(216.09, -73.7) * mm, "end": v(217.5, -74.28) * mm});
            skPoint(sketch, "E19.0.11.3", {"position": v(215.5, -108.92) * mm});
            skLineSegment(sketch, "E19.1.11.3", {"start": v(224.5, -67.75) * mm, "end": v(224.5, -106.92) * mm});
            skPoint(sketch, "E19.4.11.3", {"position": v(224.5, -108.92) * mm});
            skLineSegment(sketch, "E19.5.11.3", {"start": v(215.5, -67.75) * mm, "end": v(224.5, -67.75) * mm});
            skLineSegment(sketch, "E19.8.11.3", {"start": v(217.5, -108.92) * mm, "end": v(222.5, -108.92) * mm});
            skLineSegment(sketch, "E19.11.11.3", {"start": v(215.5, -67.75) * mm, "end": v(215.5, -106.92) * mm});
            skArc(sketch, "E19.14.11.3", {"start": v(222.5, -108.92) * mm, "mid": v(223.91, -108.34) * mm, "end": v(224.5, -106.92) * mm});
            skArc(sketch, "E19.18.11.3", {"start": v(215.5, -106.92) * mm, "mid": v(216.09, -108.34) * mm, "end": v(217.5, -108.92) * mm});
            skPoint(sketch, "E19.0.11.4", {"position": v(215.5, -143.56) * mm});
            skLineSegment(sketch, "E19.1.11.4", {"start": v(224.5, -102.4) * mm, "end": v(224.5, -141.56) * mm});
            skPoint(sketch, "E19.4.11.4", {"position": v(224.5, -143.56) * mm});
            skLineSegment(sketch, "E19.5.11.4", {"start": v(215.5, -102.4) * mm, "end": v(224.5, -102.4) * mm});
            skLineSegment(sketch, "E19.8.11.4", {"start": v(217.5, -143.56) * mm, "end": v(222.5, -143.56) * mm});
            skLineSegment(sketch, "E19.11.11.4", {"start": v(215.5, -102.4) * mm, "end": v(215.5, -141.56) * mm});
            skArc(sketch, "E19.14.11.4", {"start": v(222.5, -143.56) * mm, "mid": v(223.91, -142.98) * mm, "end": v(224.5, -141.56) * mm});
            skArc(sketch, "E19.18.11.4", {"start": v(215.5, -141.56) * mm, "mid": v(216.09, -142.98) * mm, "end": v(217.5, -143.56) * mm});
            skPoint(sketch, "E19.0.11.5", {"position": v(215.5, -178.2) * mm});
            skLineSegment(sketch, "E19.1.11.5", {"start": v(224.5, -137.03) * mm, "end": v(224.5, -176.2) * mm});
            skPoint(sketch, "E19.4.11.5", {"position": v(224.5, -178.2) * mm});
            skLineSegment(sketch, "E19.5.11.5", {"start": v(215.5, -137.03) * mm, "end": v(224.5, -137.03) * mm});
            skLineSegment(sketch, "E19.8.11.5", {"start": v(217.5, -178.2) * mm, "end": v(222.5, -178.2) * mm});
            skLineSegment(sketch, "E19.11.11.5", {"start": v(215.5, -137.03) * mm, "end": v(215.5, -176.2) * mm});
            skArc(sketch, "E19.14.11.5", {"start": v(222.5, -178.2) * mm, "mid": v(223.91, -177.62) * mm, "end": v(224.5, -176.2) * mm});
            skArc(sketch, "E19.18.11.5", {"start": v(215.5, -176.2) * mm, "mid": v(216.09, -177.62) * mm, "end": v(217.5, -178.2) * mm});
            skPoint(sketch, "E19.0.11.6", {"position": v(215.5, -212.85) * mm});
            skLineSegment(sketch, "E19.1.11.6", {"start": v(224.5, -171.67) * mm, "end": v(224.5, -210.85) * mm});
            skPoint(sketch, "E19.4.11.6", {"position": v(224.5, -212.85) * mm});
            skLineSegment(sketch, "E19.5.11.6", {"start": v(215.5, -171.67) * mm, "end": v(224.5, -171.67) * mm});
            skLineSegment(sketch, "E19.8.11.6", {"start": v(217.5, -212.85) * mm, "end": v(222.5, -212.85) * mm});
            skLineSegment(sketch, "E19.11.11.6", {"start": v(215.5, -171.67) * mm, "end": v(215.5, -210.85) * mm});
            skArc(sketch, "E19.14.11.6", {"start": v(222.5, -212.85) * mm, "mid": v(223.91, -212.26) * mm, "end": v(224.5, -210.85) * mm});
            skArc(sketch, "E19.18.11.6", {"start": v(215.5, -210.85) * mm, "mid": v(216.09, -212.26) * mm, "end": v(217.5, -212.85) * mm});
            skPoint(sketch, "E19.0.11.7", {"position": v(215.5, -247.49) * mm});
            skLineSegment(sketch, "E19.1.11.7", {"start": v(224.5, -206.31) * mm, "end": v(224.5, -245.49) * mm});
            skPoint(sketch, "E19.4.11.7", {"position": v(224.5, -247.49) * mm});
            skLineSegment(sketch, "E19.5.11.7", {"start": v(215.5, -206.31) * mm, "end": v(224.5, -206.31) * mm});
            skLineSegment(sketch, "E19.8.11.7", {"start": v(217.5, -247.49) * mm, "end": v(222.5, -247.49) * mm});
            skLineSegment(sketch, "E19.11.11.7", {"start": v(215.5, -206.31) * mm, "end": v(215.5, -245.49) * mm});
            skArc(sketch, "E19.14.11.7", {"start": v(222.5, -247.49) * mm, "mid": v(223.91, -246.9) * mm, "end": v(224.5, -245.49) * mm});
            skArc(sketch, "E19.18.11.7", {"start": v(215.5, -245.49) * mm, "mid": v(216.09, -246.9) * mm, "end": v(217.5, -247.49) * mm});
            skPoint(sketch, "E19.0.11.8", {"position": v(215.5, -282.13) * mm});
            skLineSegment(sketch, "E19.1.11.8", {"start": v(224.5, -240.95) * mm, "end": v(224.5, -280.13) * mm});
            skPoint(sketch, "E19.4.11.8", {"position": v(224.5, -282.13) * mm});
            skLineSegment(sketch, "E19.5.11.8", {"start": v(215.5, -240.95) * mm, "end": v(224.5, -240.95) * mm});
            skLineSegment(sketch, "E19.8.11.8", {"start": v(217.5, -282.13) * mm, "end": v(222.5, -282.13) * mm});
            skLineSegment(sketch, "E19.11.11.8", {"start": v(215.5, -240.95) * mm, "end": v(215.5, -280.13) * mm});
            skArc(sketch, "E19.14.11.8", {"start": v(222.5, -282.13) * mm, "mid": v(223.91, -281.54) * mm, "end": v(224.5, -280.13) * mm});
            skArc(sketch, "E19.18.11.8", {"start": v(215.5, -280.13) * mm, "mid": v(216.09, -281.54) * mm, "end": v(217.5, -282.13) * mm});
            skPoint(sketch, "E19.0.11.9", {"position": v(215.5, -316.77) * mm});
            skLineSegment(sketch, "E19.1.11.9", {"start": v(224.5, -275.6) * mm, "end": v(224.5, -314.77) * mm});
            skPoint(sketch, "E19.4.11.9", {"position": v(224.5, -316.77) * mm});
            skLineSegment(sketch, "E19.5.11.9", {"start": v(215.5, -275.6) * mm, "end": v(224.5, -275.6) * mm});
            skLineSegment(sketch, "E19.8.11.9", {"start": v(217.5, -316.77) * mm, "end": v(222.5, -316.77) * mm});
            skLineSegment(sketch, "E19.11.11.9", {"start": v(215.5, -275.6) * mm, "end": v(215.5, -314.77) * mm});
            skArc(sketch, "E19.14.11.9", {"start": v(222.5, -316.77) * mm, "mid": v(223.91, -316.18) * mm, "end": v(224.5, -314.77) * mm});
            skArc(sketch, "E19.18.11.9", {"start": v(215.5, -314.77) * mm, "mid": v(216.09, -316.18) * mm, "end": v(217.5, -316.77) * mm});
            skPoint(sketch, "E19.0.11.10", {"position": v(215.5, -351.41) * mm});
            skLineSegment(sketch, "E19.1.11.10", {"start": v(224.5, -310.24) * mm, "end": v(224.5, -349.41) * mm});
            skPoint(sketch, "E19.4.11.10", {"position": v(224.5, -351.41) * mm});
            skLineSegment(sketch, "E19.5.11.10", {"start": v(215.5, -310.24) * mm, "end": v(224.5, -310.24) * mm});
            skLineSegment(sketch, "E19.8.11.10", {"start": v(217.5, -351.41) * mm, "end": v(222.5, -351.41) * mm});
            skLineSegment(sketch, "E19.11.11.10", {"start": v(215.5, -310.24) * mm, "end": v(215.5, -349.41) * mm});
            skArc(sketch, "E19.14.11.10", {"start": v(222.5, -351.41) * mm, "mid": v(223.91, -350.82) * mm, "end": v(224.5, -349.41) * mm});
            skArc(sketch, "E19.18.11.10", {"start": v(215.5, -349.41) * mm, "mid": v(216.09, -350.82) * mm, "end": v(217.5, -351.41) * mm});
            skPoint(sketch, "E19.0.11.11", {"position": v(215.5, -386.05) * mm});
            skLineSegment(sketch, "E19.1.11.11", {"start": v(224.5, -344.88) * mm, "end": v(224.5, -384.05) * mm});
            skPoint(sketch, "E19.4.11.11", {"position": v(224.5, -386.05) * mm});
            skLineSegment(sketch, "E19.5.11.11", {"start": v(215.5, -344.88) * mm, "end": v(224.5, -344.88) * mm});
            skLineSegment(sketch, "E19.8.11.11", {"start": v(217.5, -386.05) * mm, "end": v(222.5, -386.05) * mm});
            skLineSegment(sketch, "E19.11.11.11", {"start": v(215.5, -344.88) * mm, "end": v(215.5, -384.05) * mm});
            skArc(sketch, "E19.14.11.11", {"start": v(222.5, -386.05) * mm, "mid": v(223.91, -385.47) * mm, "end": v(224.5, -384.05) * mm});
            skArc(sketch, "E19.18.11.11", {"start": v(215.5, -384.05) * mm, "mid": v(216.09, -385.47) * mm, "end": v(217.5, -386.05) * mm});
            skPoint(sketch, "E19.0.11.12", {"position": v(215.5, -420.7) * mm});
            skLineSegment(sketch, "E19.1.11.12", {"start": v(224.5, -379.52) * mm, "end": v(224.5, -418.7) * mm});
            skPoint(sketch, "E19.4.11.12", {"position": v(224.5, -420.7) * mm});
            skLineSegment(sketch, "E19.5.11.12", {"start": v(215.5, -379.52) * mm, "end": v(224.5, -379.52) * mm});
            skLineSegment(sketch, "E19.8.11.12", {"start": v(217.5, -420.7) * mm, "end": v(222.5, -420.7) * mm});
            skLineSegment(sketch, "E19.11.11.12", {"start": v(215.5, -379.52) * mm, "end": v(215.5, -418.7) * mm});
            skArc(sketch, "E19.14.11.12", {"start": v(222.5, -420.7) * mm, "mid": v(223.91, -420.1) * mm, "end": v(224.5, -418.7) * mm});
            skArc(sketch, "E19.18.11.12", {"start": v(215.5, -418.7) * mm, "mid": v(216.09, -420.1) * mm, "end": v(217.5, -420.7) * mm});
            skPoint(sketch, "E19.0.11.13", {"position": v(215.5, -455.33) * mm});
            skLineSegment(sketch, "E19.1.11.13", {"start": v(224.5, -414.16) * mm, "end": v(224.5, -453.33) * mm});
            skPoint(sketch, "E19.4.11.13", {"position": v(224.5, -455.33) * mm});
            skLineSegment(sketch, "E19.5.11.13", {"start": v(215.5, -414.16) * mm, "end": v(224.5, -414.16) * mm});
            skLineSegment(sketch, "E19.8.11.13", {"start": v(217.5, -455.33) * mm, "end": v(222.5, -455.33) * mm});
            skLineSegment(sketch, "E19.11.11.13", {"start": v(215.5, -414.16) * mm, "end": v(215.5, -453.33) * mm});
            skArc(sketch, "E19.14.11.13", {"start": v(222.5, -455.33) * mm, "mid": v(223.91, -454.75) * mm, "end": v(224.5, -453.33) * mm});
            skArc(sketch, "E19.18.11.13", {"start": v(215.5, -453.33) * mm, "mid": v(216.09, -454.75) * mm, "end": v(217.5, -455.33) * mm});
            skPoint(sketch, "E19.0.11.14", {"position": v(215.5, -489.97) * mm});
            skLineSegment(sketch, "E19.1.11.14", {"start": v(224.5, -448.8) * mm, "end": v(224.5, -487.97) * mm});
            skPoint(sketch, "E19.4.11.14", {"position": v(224.5, -489.97) * mm});
            skLineSegment(sketch, "E19.5.11.14", {"start": v(215.5, -448.8) * mm, "end": v(224.5, -448.8) * mm});
            skLineSegment(sketch, "E19.8.11.14", {"start": v(217.5, -489.97) * mm, "end": v(222.5, -489.97) * mm});
            skLineSegment(sketch, "E19.11.11.14", {"start": v(215.5, -448.8) * mm, "end": v(215.5, -487.97) * mm});
            skArc(sketch, "E19.14.11.14", {"start": v(222.5, -489.97) * mm, "mid": v(223.91, -489.39) * mm, "end": v(224.5, -487.97) * mm});
            skArc(sketch, "E19.18.11.14", {"start": v(215.5, -487.97) * mm, "mid": v(216.09, -489.39) * mm, "end": v(217.5, -489.97) * mm});
            skPoint(sketch, "E19.0.12.0", {"position": v(235.5, -5) * mm});
            skLineSegment(sketch, "E19.1.12.0", {"start": v(244.5, 36.17) * mm, "end": v(244.5, -3) * mm});
            skPoint(sketch, "E19.4.12.0", {"position": v(244.5, -5) * mm});
            skLineSegment(sketch, "E19.5.12.0", {"start": v(235.5, 36.17) * mm, "end": v(244.5, 36.17) * mm});
            skLineSegment(sketch, "E19.8.12.0", {"start": v(237.5, -5) * mm, "end": v(242.5, -5) * mm});
            skLineSegment(sketch, "E19.11.12.0", {"start": v(235.5, 36.17) * mm, "end": v(235.5, -3) * mm});
            skArc(sketch, "E19.14.12.0", {"start": v(242.5, -5) * mm, "mid": v(243.91, -4.41) * mm, "end": v(244.5, -3) * mm});
            skArc(sketch, "E19.18.12.0", {"start": v(235.5, -3) * mm, "mid": v(236.09, -4.41) * mm, "end": v(237.5, -5) * mm});
            skPoint(sketch, "E19.0.12.1", {"position": v(235.5, -39.64) * mm});
            skLineSegment(sketch, "E19.1.12.1", {"start": v(244.5, 1.53) * mm, "end": v(244.5, -37.64) * mm});
            skPoint(sketch, "E19.4.12.1", {"position": v(244.5, -39.64) * mm});
            skLineSegment(sketch, "E19.5.12.1", {"start": v(235.5, 1.53) * mm, "end": v(244.5, 1.53) * mm});
            skLineSegment(sketch, "E19.8.12.1", {"start": v(237.5, -39.64) * mm, "end": v(242.5, -39.64) * mm});
            skLineSegment(sketch, "E19.11.12.1", {"start": v(235.5, 1.53) * mm, "end": v(235.5, -37.64) * mm});
            skArc(sketch, "E19.14.12.1", {"start": v(242.5, -39.64) * mm, "mid": v(243.91, -39.06) * mm, "end": v(244.5, -37.64) * mm});
            skArc(sketch, "E19.18.12.1", {"start": v(235.5, -37.64) * mm, "mid": v(236.09, -39.06) * mm, "end": v(237.5, -39.64) * mm});
            skPoint(sketch, "E19.0.12.2", {"position": v(235.5, -74.28) * mm});
            skLineSegment(sketch, "E19.1.12.2", {"start": v(244.5, -33.1) * mm, "end": v(244.5, -72.28) * mm});
            skPoint(sketch, "E19.4.12.2", {"position": v(244.5, -74.28) * mm});
            skLineSegment(sketch, "E19.5.12.2", {"start": v(235.5, -33.1) * mm, "end": v(244.5, -33.1) * mm});
            skLineSegment(sketch, "E19.8.12.2", {"start": v(237.5, -74.28) * mm, "end": v(242.5, -74.28) * mm});
            skLineSegment(sketch, "E19.11.12.2", {"start": v(235.5, -33.1) * mm, "end": v(235.5, -72.28) * mm});
            skArc(sketch, "E19.14.12.2", {"start": v(242.5, -74.28) * mm, "mid": v(243.91, -73.7) * mm, "end": v(244.5, -72.28) * mm});
            skArc(sketch, "E19.18.12.2", {"start": v(235.5, -72.28) * mm, "mid": v(236.09, -73.7) * mm, "end": v(237.5, -74.28) * mm});
            skPoint(sketch, "E19.0.12.3", {"position": v(235.5, -108.92) * mm});
            skLineSegment(sketch, "E19.1.12.3", {"start": v(244.5, -67.75) * mm, "end": v(244.5, -106.92) * mm});
            skPoint(sketch, "E19.4.12.3", {"position": v(244.5, -108.92) * mm});
            skLineSegment(sketch, "E19.5.12.3", {"start": v(235.5, -67.75) * mm, "end": v(244.5, -67.75) * mm});
            skLineSegment(sketch, "E19.8.12.3", {"start": v(237.5, -108.92) * mm, "end": v(242.5, -108.92) * mm});
            skLineSegment(sketch, "E19.11.12.3", {"start": v(235.5, -67.75) * mm, "end": v(235.5, -106.92) * mm});
            skArc(sketch, "E19.14.12.3", {"start": v(242.5, -108.92) * mm, "mid": v(243.91, -108.34) * mm, "end": v(244.5, -106.92) * mm});
            skArc(sketch, "E19.18.12.3", {"start": v(235.5, -106.92) * mm, "mid": v(236.09, -108.34) * mm, "end": v(237.5, -108.92) * mm});
            skPoint(sketch, "E19.0.12.4", {"position": v(235.5, -143.56) * mm});
            skLineSegment(sketch, "E19.1.12.4", {"start": v(244.5, -102.4) * mm, "end": v(244.5, -141.56) * mm});
            skPoint(sketch, "E19.4.12.4", {"position": v(244.5, -143.56) * mm});
            skLineSegment(sketch, "E19.5.12.4", {"start": v(235.5, -102.4) * mm, "end": v(244.5, -102.4) * mm});
            skLineSegment(sketch, "E19.8.12.4", {"start": v(237.5, -143.56) * mm, "end": v(242.5, -143.56) * mm});
            skLineSegment(sketch, "E19.11.12.4", {"start": v(235.5, -102.4) * mm, "end": v(235.5, -141.56) * mm});
            skArc(sketch, "E19.14.12.4", {"start": v(242.5, -143.56) * mm, "mid": v(243.91, -142.98) * mm, "end": v(244.5, -141.56) * mm});
            skArc(sketch, "E19.18.12.4", {"start": v(235.5, -141.56) * mm, "mid": v(236.09, -142.98) * mm, "end": v(237.5, -143.56) * mm});
            skPoint(sketch, "E19.0.12.5", {"position": v(235.5, -178.2) * mm});
            skLineSegment(sketch, "E19.1.12.5", {"start": v(244.5, -137.03) * mm, "end": v(244.5, -176.2) * mm});
            skPoint(sketch, "E19.4.12.5", {"position": v(244.5, -178.2) * mm});
            skLineSegment(sketch, "E19.5.12.5", {"start": v(235.5, -137.03) * mm, "end": v(244.5, -137.03) * mm});
            skLineSegment(sketch, "E19.8.12.5", {"start": v(237.5, -178.2) * mm, "end": v(242.5, -178.2) * mm});
            skLineSegment(sketch, "E19.11.12.5", {"start": v(235.5, -137.03) * mm, "end": v(235.5, -176.2) * mm});
            skArc(sketch, "E19.14.12.5", {"start": v(242.5, -178.2) * mm, "mid": v(243.91, -177.62) * mm, "end": v(244.5, -176.2) * mm});
            skArc(sketch, "E19.18.12.5", {"start": v(235.5, -176.2) * mm, "mid": v(236.09, -177.62) * mm, "end": v(237.5, -178.2) * mm});
            skPoint(sketch, "E19.0.12.6", {"position": v(235.5, -212.85) * mm});
            skLineSegment(sketch, "E19.1.12.6", {"start": v(244.5, -171.67) * mm, "end": v(244.5, -210.85) * mm});
            skPoint(sketch, "E19.4.12.6", {"position": v(244.5, -212.85) * mm});
            skLineSegment(sketch, "E19.5.12.6", {"start": v(235.5, -171.67) * mm, "end": v(244.5, -171.67) * mm});
            skLineSegment(sketch, "E19.8.12.6", {"start": v(237.5, -212.85) * mm, "end": v(242.5, -212.85) * mm});
            skLineSegment(sketch, "E19.11.12.6", {"start": v(235.5, -171.67) * mm, "end": v(235.5, -210.85) * mm});
            skArc(sketch, "E19.14.12.6", {"start": v(242.5, -212.85) * mm, "mid": v(243.91, -212.26) * mm, "end": v(244.5, -210.85) * mm});
            skArc(sketch, "E19.18.12.6", {"start": v(235.5, -210.85) * mm, "mid": v(236.09, -212.26) * mm, "end": v(237.5, -212.85) * mm});
            skPoint(sketch, "E19.0.12.7", {"position": v(235.5, -247.49) * mm});
            skLineSegment(sketch, "E19.1.12.7", {"start": v(244.5, -206.31) * mm, "end": v(244.5, -245.49) * mm});
            skPoint(sketch, "E19.4.12.7", {"position": v(244.5, -247.49) * mm});
            skLineSegment(sketch, "E19.5.12.7", {"start": v(235.5, -206.31) * mm, "end": v(244.5, -206.31) * mm});
            skLineSegment(sketch, "E19.8.12.7", {"start": v(237.5, -247.49) * mm, "end": v(242.5, -247.49) * mm});
            skLineSegment(sketch, "E19.11.12.7", {"start": v(235.5, -206.31) * mm, "end": v(235.5, -245.49) * mm});
            skArc(sketch, "E19.14.12.7", {"start": v(242.5, -247.49) * mm, "mid": v(243.91, -246.9) * mm, "end": v(244.5, -245.49) * mm});
            skArc(sketch, "E19.18.12.7", {"start": v(235.5, -245.49) * mm, "mid": v(236.09, -246.9) * mm, "end": v(237.5, -247.49) * mm});
            skPoint(sketch, "E19.0.12.8", {"position": v(235.5, -282.13) * mm});
            skLineSegment(sketch, "E19.1.12.8", {"start": v(244.5, -240.95) * mm, "end": v(244.5, -280.13) * mm});
            skPoint(sketch, "E19.4.12.8", {"position": v(244.5, -282.13) * mm});
            skLineSegment(sketch, "E19.5.12.8", {"start": v(235.5, -240.95) * mm, "end": v(244.5, -240.95) * mm});
            skLineSegment(sketch, "E19.8.12.8", {"start": v(237.5, -282.13) * mm, "end": v(242.5, -282.13) * mm});
            skLineSegment(sketch, "E19.11.12.8", {"start": v(235.5, -240.95) * mm, "end": v(235.5, -280.13) * mm});
            skArc(sketch, "E19.14.12.8", {"start": v(242.5, -282.13) * mm, "mid": v(243.91, -281.54) * mm, "end": v(244.5, -280.13) * mm});
            skArc(sketch, "E19.18.12.8", {"start": v(235.5, -280.13) * mm, "mid": v(236.09, -281.54) * mm, "end": v(237.5, -282.13) * mm});
            skPoint(sketch, "E19.0.12.9", {"position": v(235.5, -316.77) * mm});
            skLineSegment(sketch, "E19.1.12.9", {"start": v(244.5, -275.6) * mm, "end": v(244.5, -314.77) * mm});
            skPoint(sketch, "E19.4.12.9", {"position": v(244.5, -316.77) * mm});
            skLineSegment(sketch, "E19.5.12.9", {"start": v(235.5, -275.6) * mm, "end": v(244.5, -275.6) * mm});
            skLineSegment(sketch, "E19.8.12.9", {"start": v(237.5, -316.77) * mm, "end": v(242.5, -316.77) * mm});
            skLineSegment(sketch, "E19.11.12.9", {"start": v(235.5, -275.6) * mm, "end": v(235.5, -314.77) * mm});
            skArc(sketch, "E19.14.12.9", {"start": v(242.5, -316.77) * mm, "mid": v(243.91, -316.18) * mm, "end": v(244.5, -314.77) * mm});
            skArc(sketch, "E19.18.12.9", {"start": v(235.5, -314.77) * mm, "mid": v(236.09, -316.18) * mm, "end": v(237.5, -316.77) * mm});
            skPoint(sketch, "E19.0.12.10", {"position": v(235.5, -351.41) * mm});
            skLineSegment(sketch, "E19.1.12.10", {"start": v(244.5, -310.24) * mm, "end": v(244.5, -349.41) * mm});
            skPoint(sketch, "E19.4.12.10", {"position": v(244.5, -351.41) * mm});
            skLineSegment(sketch, "E19.5.12.10", {"start": v(235.5, -310.24) * mm, "end": v(244.5, -310.24) * mm});
            skLineSegment(sketch, "E19.8.12.10", {"start": v(237.5, -351.41) * mm, "end": v(242.5, -351.41) * mm});
            skLineSegment(sketch, "E19.11.12.10", {"start": v(235.5, -310.24) * mm, "end": v(235.5, -349.41) * mm});
            skArc(sketch, "E19.14.12.10", {"start": v(242.5, -351.41) * mm, "mid": v(243.91, -350.82) * mm, "end": v(244.5, -349.41) * mm});
            skArc(sketch, "E19.18.12.10", {"start": v(235.5, -349.41) * mm, "mid": v(236.09, -350.82) * mm, "end": v(237.5, -351.41) * mm});
            skPoint(sketch, "E19.0.12.11", {"position": v(235.5, -386.05) * mm});
            skLineSegment(sketch, "E19.1.12.11", {"start": v(244.5, -344.88) * mm, "end": v(244.5, -384.05) * mm});
            skPoint(sketch, "E19.4.12.11", {"position": v(244.5, -386.05) * mm});
            skLineSegment(sketch, "E19.5.12.11", {"start": v(235.5, -344.88) * mm, "end": v(244.5, -344.88) * mm});
            skLineSegment(sketch, "E19.8.12.11", {"start": v(237.5, -386.05) * mm, "end": v(242.5, -386.05) * mm});
            skLineSegment(sketch, "E19.11.12.11", {"start": v(235.5, -344.88) * mm, "end": v(235.5, -384.05) * mm});
            skArc(sketch, "E19.14.12.11", {"start": v(242.5, -386.05) * mm, "mid": v(243.91, -385.47) * mm, "end": v(244.5, -384.05) * mm});
            skArc(sketch, "E19.18.12.11", {"start": v(235.5, -384.05) * mm, "mid": v(236.09, -385.47) * mm, "end": v(237.5, -386.05) * mm});
            skPoint(sketch, "E19.0.12.12", {"position": v(235.5, -420.7) * mm});
            skLineSegment(sketch, "E19.1.12.12", {"start": v(244.5, -379.52) * mm, "end": v(244.5, -418.7) * mm});
            skPoint(sketch, "E19.4.12.12", {"position": v(244.5, -420.7) * mm});
            skLineSegment(sketch, "E19.5.12.12", {"start": v(235.5, -379.52) * mm, "end": v(244.5, -379.52) * mm});
            skLineSegment(sketch, "E19.8.12.12", {"start": v(237.5, -420.7) * mm, "end": v(242.5, -420.7) * mm});
            skLineSegment(sketch, "E19.11.12.12", {"start": v(235.5, -379.52) * mm, "end": v(235.5, -418.7) * mm});
            skArc(sketch, "E19.14.12.12", {"start": v(242.5, -420.7) * mm, "mid": v(243.91, -420.1) * mm, "end": v(244.5, -418.7) * mm});
            skArc(sketch, "E19.18.12.12", {"start": v(235.5, -418.7) * mm, "mid": v(236.09, -420.1) * mm, "end": v(237.5, -420.7) * mm});
            skPoint(sketch, "E19.0.12.13", {"position": v(235.5, -455.33) * mm});
            skLineSegment(sketch, "E19.1.12.13", {"start": v(244.5, -414.16) * mm, "end": v(244.5, -453.33) * mm});
            skPoint(sketch, "E19.4.12.13", {"position": v(244.5, -455.33) * mm});
            skLineSegment(sketch, "E19.5.12.13", {"start": v(235.5, -414.16) * mm, "end": v(244.5, -414.16) * mm});
            skLineSegment(sketch, "E19.8.12.13", {"start": v(237.5, -455.33) * mm, "end": v(242.5, -455.33) * mm});
            skLineSegment(sketch, "E19.11.12.13", {"start": v(235.5, -414.16) * mm, "end": v(235.5, -453.33) * mm});
            skArc(sketch, "E19.14.12.13", {"start": v(242.5, -455.33) * mm, "mid": v(243.91, -454.75) * mm, "end": v(244.5, -453.33) * mm});
            skArc(sketch, "E19.18.12.13", {"start": v(235.5, -453.33) * mm, "mid": v(236.09, -454.75) * mm, "end": v(237.5, -455.33) * mm});
            skPoint(sketch, "E19.0.12.14", {"position": v(235.5, -489.97) * mm});
            skLineSegment(sketch, "E19.1.12.14", {"start": v(244.5, -448.8) * mm, "end": v(244.5, -487.97) * mm});
            skPoint(sketch, "E19.4.12.14", {"position": v(244.5, -489.97) * mm});
            skLineSegment(sketch, "E19.5.12.14", {"start": v(235.5, -448.8) * mm, "end": v(244.5, -448.8) * mm});
            skLineSegment(sketch, "E19.8.12.14", {"start": v(237.5, -489.97) * mm, "end": v(242.5, -489.97) * mm});
            skLineSegment(sketch, "E19.11.12.14", {"start": v(235.5, -448.8) * mm, "end": v(235.5, -487.97) * mm});
            skArc(sketch, "E19.14.12.14", {"start": v(242.5, -489.97) * mm, "mid": v(243.91, -489.39) * mm, "end": v(244.5, -487.97) * mm});
            skArc(sketch, "E19.18.12.14", {"start": v(235.5, -487.97) * mm, "mid": v(236.09, -489.39) * mm, "end": v(237.5, -489.97) * mm});
            skPoint(sketch, "E19.0.13.0", {"position": v(255.5, -5) * mm});
            skLineSegment(sketch, "E19.1.13.0", {"start": v(264.5, 36.17) * mm, "end": v(264.5, -3) * mm});
            skPoint(sketch, "E19.4.13.0", {"position": v(264.5, -5) * mm});
            skLineSegment(sketch, "E19.5.13.0", {"start": v(255.5, 36.17) * mm, "end": v(264.5, 36.17) * mm});
            skLineSegment(sketch, "E19.8.13.0", {"start": v(257.5, -5) * mm, "end": v(262.5, -5) * mm});
            skLineSegment(sketch, "E19.11.13.0", {"start": v(255.5, 36.17) * mm, "end": v(255.5, -3) * mm});
            skArc(sketch, "E19.14.13.0", {"start": v(262.5, -5) * mm, "mid": v(263.91, -4.41) * mm, "end": v(264.5, -3) * mm});
            skArc(sketch, "E19.18.13.0", {"start": v(255.5, -3) * mm, "mid": v(256.09, -4.41) * mm, "end": v(257.5, -5) * mm});
            skPoint(sketch, "E19.0.13.1", {"position": v(255.5, -39.64) * mm});
            skLineSegment(sketch, "E19.1.13.1", {"start": v(264.5, 1.53) * mm, "end": v(264.5, -37.64) * mm});
            skPoint(sketch, "E19.4.13.1", {"position": v(264.5, -39.64) * mm});
            skLineSegment(sketch, "E19.5.13.1", {"start": v(255.5, 1.53) * mm, "end": v(264.5, 1.53) * mm});
            skLineSegment(sketch, "E19.8.13.1", {"start": v(257.5, -39.64) * mm, "end": v(262.5, -39.64) * mm});
            skLineSegment(sketch, "E19.11.13.1", {"start": v(255.5, 1.53) * mm, "end": v(255.5, -37.64) * mm});
            skArc(sketch, "E19.14.13.1", {"start": v(262.5, -39.64) * mm, "mid": v(263.91, -39.06) * mm, "end": v(264.5, -37.64) * mm});
            skArc(sketch, "E19.18.13.1", {"start": v(255.5, -37.64) * mm, "mid": v(256.09, -39.06) * mm, "end": v(257.5, -39.64) * mm});
            skPoint(sketch, "E19.0.13.2", {"position": v(255.5, -74.28) * mm});
            skLineSegment(sketch, "E19.1.13.2", {"start": v(264.5, -33.1) * mm, "end": v(264.5, -72.28) * mm});
            skPoint(sketch, "E19.4.13.2", {"position": v(264.5, -74.28) * mm});
            skLineSegment(sketch, "E19.5.13.2", {"start": v(255.5, -33.1) * mm, "end": v(264.5, -33.1) * mm});
            skLineSegment(sketch, "E19.8.13.2", {"start": v(257.5, -74.28) * mm, "end": v(262.5, -74.28) * mm});
            skLineSegment(sketch, "E19.11.13.2", {"start": v(255.5, -33.1) * mm, "end": v(255.5, -72.28) * mm});
            skArc(sketch, "E19.14.13.2", {"start": v(262.5, -74.28) * mm, "mid": v(263.91, -73.7) * mm, "end": v(264.5, -72.28) * mm});
            skArc(sketch, "E19.18.13.2", {"start": v(255.5, -72.28) * mm, "mid": v(256.09, -73.7) * mm, "end": v(257.5, -74.28) * mm});
            skPoint(sketch, "E19.0.13.3", {"position": v(255.5, -108.92) * mm});
            skLineSegment(sketch, "E19.1.13.3", {"start": v(264.5, -67.75) * mm, "end": v(264.5, -106.92) * mm});
            skPoint(sketch, "E19.4.13.3", {"position": v(264.5, -108.92) * mm});
            skLineSegment(sketch, "E19.5.13.3", {"start": v(255.5, -67.75) * mm, "end": v(264.5, -67.75) * mm});
            skLineSegment(sketch, "E19.8.13.3", {"start": v(257.5, -108.92) * mm, "end": v(262.5, -108.92) * mm});
            skLineSegment(sketch, "E19.11.13.3", {"start": v(255.5, -67.75) * mm, "end": v(255.5, -106.92) * mm});
            skArc(sketch, "E19.14.13.3", {"start": v(262.5, -108.92) * mm, "mid": v(263.91, -108.34) * mm, "end": v(264.5, -106.92) * mm});
            skArc(sketch, "E19.18.13.3", {"start": v(255.5, -106.92) * mm, "mid": v(256.09, -108.34) * mm, "end": v(257.5, -108.92) * mm});
            skPoint(sketch, "E19.0.13.4", {"position": v(255.5, -143.56) * mm});
            skLineSegment(sketch, "E19.1.13.4", {"start": v(264.5, -102.4) * mm, "end": v(264.5, -141.56) * mm});
            skPoint(sketch, "E19.4.13.4", {"position": v(264.5, -143.56) * mm});
            skLineSegment(sketch, "E19.5.13.4", {"start": v(255.5, -102.4) * mm, "end": v(264.5, -102.4) * mm});
            skLineSegment(sketch, "E19.8.13.4", {"start": v(257.5, -143.56) * mm, "end": v(262.5, -143.56) * mm});
            skLineSegment(sketch, "E19.11.13.4", {"start": v(255.5, -102.4) * mm, "end": v(255.5, -141.56) * mm});
            skArc(sketch, "E19.14.13.4", {"start": v(262.5, -143.56) * mm, "mid": v(263.91, -142.98) * mm, "end": v(264.5, -141.56) * mm});
            skArc(sketch, "E19.18.13.4", {"start": v(255.5, -141.56) * mm, "mid": v(256.09, -142.98) * mm, "end": v(257.5, -143.56) * mm});
            skPoint(sketch, "E19.0.13.5", {"position": v(255.5, -178.2) * mm});
            skLineSegment(sketch, "E19.1.13.5", {"start": v(264.5, -137.03) * mm, "end": v(264.5, -176.2) * mm});
            skPoint(sketch, "E19.4.13.5", {"position": v(264.5, -178.2) * mm});
            skLineSegment(sketch, "E19.5.13.5", {"start": v(255.5, -137.03) * mm, "end": v(264.5, -137.03) * mm});
            skLineSegment(sketch, "E19.8.13.5", {"start": v(257.5, -178.2) * mm, "end": v(262.5, -178.2) * mm});
            skLineSegment(sketch, "E19.11.13.5", {"start": v(255.5, -137.03) * mm, "end": v(255.5, -176.2) * mm});
            skArc(sketch, "E19.14.13.5", {"start": v(262.5, -178.2) * mm, "mid": v(263.91, -177.62) * mm, "end": v(264.5, -176.2) * mm});
            skArc(sketch, "E19.18.13.5", {"start": v(255.5, -176.2) * mm, "mid": v(256.09, -177.62) * mm, "end": v(257.5, -178.2) * mm});
            skPoint(sketch, "E19.0.13.6", {"position": v(255.5, -212.85) * mm});
            skLineSegment(sketch, "E19.1.13.6", {"start": v(264.5, -171.67) * mm, "end": v(264.5, -210.85) * mm});
            skPoint(sketch, "E19.4.13.6", {"position": v(264.5, -212.85) * mm});
            skLineSegment(sketch, "E19.5.13.6", {"start": v(255.5, -171.67) * mm, "end": v(264.5, -171.67) * mm});
            skLineSegment(sketch, "E19.8.13.6", {"start": v(257.5, -212.85) * mm, "end": v(262.5, -212.85) * mm});
            skLineSegment(sketch, "E19.11.13.6", {"start": v(255.5, -171.67) * mm, "end": v(255.5, -210.85) * mm});
            skArc(sketch, "E19.14.13.6", {"start": v(262.5, -212.85) * mm, "mid": v(263.91, -212.26) * mm, "end": v(264.5, -210.85) * mm});
            skArc(sketch, "E19.18.13.6", {"start": v(255.5, -210.85) * mm, "mid": v(256.09, -212.26) * mm, "end": v(257.5, -212.85) * mm});
            skPoint(sketch, "E19.0.13.7", {"position": v(255.5, -247.49) * mm});
            skLineSegment(sketch, "E19.1.13.7", {"start": v(264.5, -206.31) * mm, "end": v(264.5, -245.49) * mm});
            skPoint(sketch, "E19.4.13.7", {"position": v(264.5, -247.49) * mm});
            skLineSegment(sketch, "E19.5.13.7", {"start": v(255.5, -206.31) * mm, "end": v(264.5, -206.31) * mm});
            skLineSegment(sketch, "E19.8.13.7", {"start": v(257.5, -247.49) * mm, "end": v(262.5, -247.49) * mm});
            skLineSegment(sketch, "E19.11.13.7", {"start": v(255.5, -206.31) * mm, "end": v(255.5, -245.49) * mm});
            skArc(sketch, "E19.14.13.7", {"start": v(262.5, -247.49) * mm, "mid": v(263.91, -246.9) * mm, "end": v(264.5, -245.49) * mm});
            skArc(sketch, "E19.18.13.7", {"start": v(255.5, -245.49) * mm, "mid": v(256.09, -246.9) * mm, "end": v(257.5, -247.49) * mm});
            skPoint(sketch, "E19.0.13.8", {"position": v(255.5, -282.13) * mm});
            skLineSegment(sketch, "E19.1.13.8", {"start": v(264.5, -240.95) * mm, "end": v(264.5, -280.13) * mm});
            skPoint(sketch, "E19.4.13.8", {"position": v(264.5, -282.13) * mm});
            skLineSegment(sketch, "E19.5.13.8", {"start": v(255.5, -240.95) * mm, "end": v(264.5, -240.95) * mm});
            skLineSegment(sketch, "E19.8.13.8", {"start": v(257.5, -282.13) * mm, "end": v(262.5, -282.13) * mm});
            skLineSegment(sketch, "E19.11.13.8", {"start": v(255.5, -240.95) * mm, "end": v(255.5, -280.13) * mm});
            skArc(sketch, "E19.14.13.8", {"start": v(262.5, -282.13) * mm, "mid": v(263.91, -281.54) * mm, "end": v(264.5, -280.13) * mm});
            skArc(sketch, "E19.18.13.8", {"start": v(255.5, -280.13) * mm, "mid": v(256.09, -281.54) * mm, "end": v(257.5, -282.13) * mm});
            skPoint(sketch, "E19.0.13.9", {"position": v(255.5, -316.77) * mm});
            skLineSegment(sketch, "E19.1.13.9", {"start": v(264.5, -275.6) * mm, "end": v(264.5, -314.77) * mm});
            skPoint(sketch, "E19.4.13.9", {"position": v(264.5, -316.77) * mm});
            skLineSegment(sketch, "E19.5.13.9", {"start": v(255.5, -275.6) * mm, "end": v(264.5, -275.6) * mm});
            skLineSegment(sketch, "E19.8.13.9", {"start": v(257.5, -316.77) * mm, "end": v(262.5, -316.77) * mm});
            skLineSegment(sketch, "E19.11.13.9", {"start": v(255.5, -275.6) * mm, "end": v(255.5, -314.77) * mm});
            skArc(sketch, "E19.14.13.9", {"start": v(262.5, -316.77) * mm, "mid": v(263.91, -316.18) * mm, "end": v(264.5, -314.77) * mm});
            skArc(sketch, "E19.18.13.9", {"start": v(255.5, -314.77) * mm, "mid": v(256.09, -316.18) * mm, "end": v(257.5, -316.77) * mm});
            skPoint(sketch, "E19.0.13.10", {"position": v(255.5, -351.41) * mm});
            skLineSegment(sketch, "E19.1.13.10", {"start": v(264.5, -310.24) * mm, "end": v(264.5, -349.41) * mm});
            skPoint(sketch, "E19.4.13.10", {"position": v(264.5, -351.41) * mm});
            skLineSegment(sketch, "E19.5.13.10", {"start": v(255.5, -310.24) * mm, "end": v(264.5, -310.24) * mm});
            skLineSegment(sketch, "E19.8.13.10", {"start": v(257.5, -351.41) * mm, "end": v(262.5, -351.41) * mm});
            skLineSegment(sketch, "E19.11.13.10", {"start": v(255.5, -310.24) * mm, "end": v(255.5, -349.41) * mm});
            skArc(sketch, "E19.14.13.10", {"start": v(262.5, -351.41) * mm, "mid": v(263.91, -350.82) * mm, "end": v(264.5, -349.41) * mm});
            skArc(sketch, "E19.18.13.10", {"start": v(255.5, -349.41) * mm, "mid": v(256.09, -350.82) * mm, "end": v(257.5, -351.41) * mm});
            skPoint(sketch, "E19.0.13.11", {"position": v(255.5, -386.05) * mm});
            skLineSegment(sketch, "E19.1.13.11", {"start": v(264.5, -344.88) * mm, "end": v(264.5, -384.05) * mm});
            skPoint(sketch, "E19.4.13.11", {"position": v(264.5, -386.05) * mm});
            skLineSegment(sketch, "E19.5.13.11", {"start": v(255.5, -344.88) * mm, "end": v(264.5, -344.88) * mm});
            skLineSegment(sketch, "E19.8.13.11", {"start": v(257.5, -386.05) * mm, "end": v(262.5, -386.05) * mm});
            skLineSegment(sketch, "E19.11.13.11", {"start": v(255.5, -344.88) * mm, "end": v(255.5, -384.05) * mm});
            skArc(sketch, "E19.14.13.11", {"start": v(262.5, -386.05) * mm, "mid": v(263.91, -385.47) * mm, "end": v(264.5, -384.05) * mm});
            skArc(sketch, "E19.18.13.11", {"start": v(255.5, -384.05) * mm, "mid": v(256.09, -385.47) * mm, "end": v(257.5, -386.05) * mm});
            skPoint(sketch, "E19.0.13.12", {"position": v(255.5, -420.7) * mm});
            skLineSegment(sketch, "E19.1.13.12", {"start": v(264.5, -379.52) * mm, "end": v(264.5, -418.7) * mm});
            skPoint(sketch, "E19.4.13.12", {"position": v(264.5, -420.7) * mm});
            skLineSegment(sketch, "E19.5.13.12", {"start": v(255.5, -379.52) * mm, "end": v(264.5, -379.52) * mm});
            skLineSegment(sketch, "E19.8.13.12", {"start": v(257.5, -420.7) * mm, "end": v(262.5, -420.7) * mm});
            skLineSegment(sketch, "E19.11.13.12", {"start": v(255.5, -379.52) * mm, "end": v(255.5, -418.7) * mm});
            skArc(sketch, "E19.14.13.12", {"start": v(262.5, -420.7) * mm, "mid": v(263.91, -420.1) * mm, "end": v(264.5, -418.7) * mm});
            skArc(sketch, "E19.18.13.12", {"start": v(255.5, -418.7) * mm, "mid": v(256.09, -420.1) * mm, "end": v(257.5, -420.7) * mm});
            skPoint(sketch, "E19.0.13.13", {"position": v(255.5, -455.33) * mm});
            skLineSegment(sketch, "E19.1.13.13", {"start": v(264.5, -414.16) * mm, "end": v(264.5, -453.33) * mm});
            skPoint(sketch, "E19.4.13.13", {"position": v(264.5, -455.33) * mm});
            skLineSegment(sketch, "E19.5.13.13", {"start": v(255.5, -414.16) * mm, "end": v(264.5, -414.16) * mm});
            skLineSegment(sketch, "E19.8.13.13", {"start": v(257.5, -455.33) * mm, "end": v(262.5, -455.33) * mm});
            skLineSegment(sketch, "E19.11.13.13", {"start": v(255.5, -414.16) * mm, "end": v(255.5, -453.33) * mm});
            skArc(sketch, "E19.14.13.13", {"start": v(262.5, -455.33) * mm, "mid": v(263.91, -454.75) * mm, "end": v(264.5, -453.33) * mm});
            skArc(sketch, "E19.18.13.13", {"start": v(255.5, -453.33) * mm, "mid": v(256.09, -454.75) * mm, "end": v(257.5, -455.33) * mm});
            skPoint(sketch, "E19.0.13.14", {"position": v(255.5, -489.97) * mm});
            skLineSegment(sketch, "E19.1.13.14", {"start": v(264.5, -448.8) * mm, "end": v(264.5, -487.97) * mm});
            skPoint(sketch, "E19.4.13.14", {"position": v(264.5, -489.97) * mm});
            skLineSegment(sketch, "E19.5.13.14", {"start": v(255.5, -448.8) * mm, "end": v(264.5, -448.8) * mm});
            skLineSegment(sketch, "E19.8.13.14", {"start": v(257.5, -489.97) * mm, "end": v(262.5, -489.97) * mm});
            skLineSegment(sketch, "E19.11.13.14", {"start": v(255.5, -448.8) * mm, "end": v(255.5, -487.97) * mm});
            skArc(sketch, "E19.14.13.14", {"start": v(262.5, -489.97) * mm, "mid": v(263.91, -489.39) * mm, "end": v(264.5, -487.97) * mm});
            skArc(sketch, "E19.18.13.14", {"start": v(255.5, -487.97) * mm, "mid": v(256.09, -489.39) * mm, "end": v(257.5, -489.97) * mm});
            skPoint(sketch, "E19.0.14.0", {"position": v(275.5, -5) * mm});
            skLineSegment(sketch, "E19.1.14.0", {"start": v(284.5, 36.17) * mm, "end": v(284.5, -3) * mm});
            skPoint(sketch, "E19.4.14.0", {"position": v(284.5, -5) * mm});
            skLineSegment(sketch, "E19.5.14.0", {"start": v(275.5, 36.17) * mm, "end": v(284.5, 36.17) * mm});
            skLineSegment(sketch, "E19.8.14.0", {"start": v(277.5, -5) * mm, "end": v(282.5, -5) * mm});
            skLineSegment(sketch, "E19.11.14.0", {"start": v(275.5, 36.17) * mm, "end": v(275.5, -3) * mm});
            skArc(sketch, "E19.14.14.0", {"start": v(282.5, -5) * mm, "mid": v(283.91, -4.41) * mm, "end": v(284.5, -3) * mm});
            skArc(sketch, "E19.18.14.0", {"start": v(275.5, -3) * mm, "mid": v(276.09, -4.41) * mm, "end": v(277.5, -5) * mm});
            skPoint(sketch, "E19.0.14.1", {"position": v(275.5, -39.64) * mm});
            skLineSegment(sketch, "E19.1.14.1", {"start": v(284.5, 1.53) * mm, "end": v(284.5, -37.64) * mm});
            skPoint(sketch, "E19.4.14.1", {"position": v(284.5, -39.64) * mm});
            skLineSegment(sketch, "E19.5.14.1", {"start": v(275.5, 1.53) * mm, "end": v(284.5, 1.53) * mm});
            skLineSegment(sketch, "E19.8.14.1", {"start": v(277.5, -39.64) * mm, "end": v(282.5, -39.64) * mm});
            skLineSegment(sketch, "E19.11.14.1", {"start": v(275.5, 1.53) * mm, "end": v(275.5, -37.64) * mm});
            skArc(sketch, "E19.14.14.1", {"start": v(282.5, -39.64) * mm, "mid": v(283.91, -39.06) * mm, "end": v(284.5, -37.64) * mm});
            skArc(sketch, "E19.18.14.1", {"start": v(275.5, -37.64) * mm, "mid": v(276.09, -39.06) * mm, "end": v(277.5, -39.64) * mm});
            skPoint(sketch, "E19.0.14.2", {"position": v(275.5, -74.28) * mm});
            skLineSegment(sketch, "E19.1.14.2", {"start": v(284.5, -33.1) * mm, "end": v(284.5, -72.28) * mm});
            skPoint(sketch, "E19.4.14.2", {"position": v(284.5, -74.28) * mm});
            skLineSegment(sketch, "E19.5.14.2", {"start": v(275.5, -33.1) * mm, "end": v(284.5, -33.1) * mm});
            skLineSegment(sketch, "E19.8.14.2", {"start": v(277.5, -74.28) * mm, "end": v(282.5, -74.28) * mm});
            skLineSegment(sketch, "E19.11.14.2", {"start": v(275.5, -33.1) * mm, "end": v(275.5, -72.28) * mm});
            skArc(sketch, "E19.14.14.2", {"start": v(282.5, -74.28) * mm, "mid": v(283.91, -73.7) * mm, "end": v(284.5, -72.28) * mm});
            skArc(sketch, "E19.18.14.2", {"start": v(275.5, -72.28) * mm, "mid": v(276.09, -73.7) * mm, "end": v(277.5, -74.28) * mm});
            skPoint(sketch, "E19.0.14.3", {"position": v(275.5, -108.92) * mm});
            skLineSegment(sketch, "E19.1.14.3", {"start": v(284.5, -67.75) * mm, "end": v(284.5, -106.92) * mm});
            skPoint(sketch, "E19.4.14.3", {"position": v(284.5, -108.92) * mm});
            skLineSegment(sketch, "E19.5.14.3", {"start": v(275.5, -67.75) * mm, "end": v(284.5, -67.75) * mm});
            skLineSegment(sketch, "E19.8.14.3", {"start": v(277.5, -108.92) * mm, "end": v(282.5, -108.92) * mm});
            skLineSegment(sketch, "E19.11.14.3", {"start": v(275.5, -67.75) * mm, "end": v(275.5, -106.92) * mm});
            skArc(sketch, "E19.14.14.3", {"start": v(282.5, -108.92) * mm, "mid": v(283.91, -108.34) * mm, "end": v(284.5, -106.92) * mm});
            skArc(sketch, "E19.18.14.3", {"start": v(275.5, -106.92) * mm, "mid": v(276.09, -108.34) * mm, "end": v(277.5, -108.92) * mm});
            skPoint(sketch, "E19.0.14.4", {"position": v(275.5, -143.56) * mm});
            skLineSegment(sketch, "E19.1.14.4", {"start": v(284.5, -102.4) * mm, "end": v(284.5, -141.56) * mm});
            skPoint(sketch, "E19.4.14.4", {"position": v(284.5, -143.56) * mm});
            skLineSegment(sketch, "E19.5.14.4", {"start": v(275.5, -102.4) * mm, "end": v(284.5, -102.4) * mm});
            skLineSegment(sketch, "E19.8.14.4", {"start": v(277.5, -143.56) * mm, "end": v(282.5, -143.56) * mm});
            skLineSegment(sketch, "E19.11.14.4", {"start": v(275.5, -102.4) * mm, "end": v(275.5, -141.56) * mm});
            skArc(sketch, "E19.14.14.4", {"start": v(282.5, -143.56) * mm, "mid": v(283.91, -142.98) * mm, "end": v(284.5, -141.56) * mm});
            skArc(sketch, "E19.18.14.4", {"start": v(275.5, -141.56) * mm, "mid": v(276.09, -142.98) * mm, "end": v(277.5, -143.56) * mm});
            skPoint(sketch, "E19.0.14.5", {"position": v(275.5, -178.2) * mm});
            skLineSegment(sketch, "E19.1.14.5", {"start": v(284.5, -137.03) * mm, "end": v(284.5, -176.2) * mm});
            skPoint(sketch, "E19.4.14.5", {"position": v(284.5, -178.2) * mm});
            skLineSegment(sketch, "E19.5.14.5", {"start": v(275.5, -137.03) * mm, "end": v(284.5, -137.03) * mm});
            skLineSegment(sketch, "E19.8.14.5", {"start": v(277.5, -178.2) * mm, "end": v(282.5, -178.2) * mm});
            skLineSegment(sketch, "E19.11.14.5", {"start": v(275.5, -137.03) * mm, "end": v(275.5, -176.2) * mm});
            skArc(sketch, "E19.14.14.5", {"start": v(282.5, -178.2) * mm, "mid": v(283.91, -177.62) * mm, "end": v(284.5, -176.2) * mm});
            skArc(sketch, "E19.18.14.5", {"start": v(275.5, -176.2) * mm, "mid": v(276.09, -177.62) * mm, "end": v(277.5, -178.2) * mm});
            skPoint(sketch, "E19.0.14.6", {"position": v(275.5, -212.85) * mm});
            skLineSegment(sketch, "E19.1.14.6", {"start": v(284.5, -171.67) * mm, "end": v(284.5, -210.85) * mm});
            skPoint(sketch, "E19.4.14.6", {"position": v(284.5, -212.85) * mm});
            skLineSegment(sketch, "E19.5.14.6", {"start": v(275.5, -171.67) * mm, "end": v(284.5, -171.67) * mm});
            skLineSegment(sketch, "E19.8.14.6", {"start": v(277.5, -212.85) * mm, "end": v(282.5, -212.85) * mm});
            skLineSegment(sketch, "E19.11.14.6", {"start": v(275.5, -171.67) * mm, "end": v(275.5, -210.85) * mm});
            skArc(sketch, "E19.14.14.6", {"start": v(282.5, -212.85) * mm, "mid": v(283.91, -212.26) * mm, "end": v(284.5, -210.85) * mm});
            skArc(sketch, "E19.18.14.6", {"start": v(275.5, -210.85) * mm, "mid": v(276.09, -212.26) * mm, "end": v(277.5, -212.85) * mm});
            skPoint(sketch, "E19.0.14.7", {"position": v(275.5, -247.49) * mm});
            skLineSegment(sketch, "E19.1.14.7", {"start": v(284.5, -206.31) * mm, "end": v(284.5, -245.49) * mm});
            skPoint(sketch, "E19.4.14.7", {"position": v(284.5, -247.49) * mm});
            skLineSegment(sketch, "E19.5.14.7", {"start": v(275.5, -206.31) * mm, "end": v(284.5, -206.31) * mm});
            skLineSegment(sketch, "E19.8.14.7", {"start": v(277.5, -247.49) * mm, "end": v(282.5, -247.49) * mm});
            skLineSegment(sketch, "E19.11.14.7", {"start": v(275.5, -206.31) * mm, "end": v(275.5, -245.49) * mm});
            skArc(sketch, "E19.14.14.7", {"start": v(282.5, -247.49) * mm, "mid": v(283.91, -246.9) * mm, "end": v(284.5, -245.49) * mm});
            skArc(sketch, "E19.18.14.7", {"start": v(275.5, -245.49) * mm, "mid": v(276.09, -246.9) * mm, "end": v(277.5, -247.49) * mm});
            skPoint(sketch, "E19.0.14.8", {"position": v(275.5, -282.13) * mm});
            skLineSegment(sketch, "E19.1.14.8", {"start": v(284.5, -240.95) * mm, "end": v(284.5, -280.13) * mm});
            skPoint(sketch, "E19.4.14.8", {"position": v(284.5, -282.13) * mm});
            skLineSegment(sketch, "E19.5.14.8", {"start": v(275.5, -240.95) * mm, "end": v(284.5, -240.95) * mm});
            skLineSegment(sketch, "E19.8.14.8", {"start": v(277.5, -282.13) * mm, "end": v(282.5, -282.13) * mm});
            skLineSegment(sketch, "E19.11.14.8", {"start": v(275.5, -240.95) * mm, "end": v(275.5, -280.13) * mm});
            skArc(sketch, "E19.14.14.8", {"start": v(282.5, -282.13) * mm, "mid": v(283.91, -281.54) * mm, "end": v(284.5, -280.13) * mm});
            skArc(sketch, "E19.18.14.8", {"start": v(275.5, -280.13) * mm, "mid": v(276.09, -281.54) * mm, "end": v(277.5, -282.13) * mm});
            skPoint(sketch, "E19.0.14.9", {"position": v(275.5, -316.77) * mm});
            skLineSegment(sketch, "E19.1.14.9", {"start": v(284.5, -275.6) * mm, "end": v(284.5, -314.77) * mm});
            skPoint(sketch, "E19.4.14.9", {"position": v(284.5, -316.77) * mm});
            skLineSegment(sketch, "E19.5.14.9", {"start": v(275.5, -275.6) * mm, "end": v(284.5, -275.6) * mm});
            skLineSegment(sketch, "E19.8.14.9", {"start": v(277.5, -316.77) * mm, "end": v(282.5, -316.77) * mm});
            skLineSegment(sketch, "E19.11.14.9", {"start": v(275.5, -275.6) * mm, "end": v(275.5, -314.77) * mm});
            skArc(sketch, "E19.14.14.9", {"start": v(282.5, -316.77) * mm, "mid": v(283.91, -316.18) * mm, "end": v(284.5, -314.77) * mm});
            skArc(sketch, "E19.18.14.9", {"start": v(275.5, -314.77) * mm, "mid": v(276.09, -316.18) * mm, "end": v(277.5, -316.77) * mm});
            skPoint(sketch, "E19.0.14.10", {"position": v(275.5, -351.41) * mm});
            skLineSegment(sketch, "E19.1.14.10", {"start": v(284.5, -310.24) * mm, "end": v(284.5, -349.41) * mm});
            skPoint(sketch, "E19.4.14.10", {"position": v(284.5, -351.41) * mm});
            skLineSegment(sketch, "E19.5.14.10", {"start": v(275.5, -310.24) * mm, "end": v(284.5, -310.24) * mm});
            skLineSegment(sketch, "E19.8.14.10", {"start": v(277.5, -351.41) * mm, "end": v(282.5, -351.41) * mm});
            skLineSegment(sketch, "E19.11.14.10", {"start": v(275.5, -310.24) * mm, "end": v(275.5, -349.41) * mm});
            skArc(sketch, "E19.14.14.10", {"start": v(282.5, -351.41) * mm, "mid": v(283.91, -350.82) * mm, "end": v(284.5, -349.41) * mm});
            skArc(sketch, "E19.18.14.10", {"start": v(275.5, -349.41) * mm, "mid": v(276.09, -350.82) * mm, "end": v(277.5, -351.41) * mm});
            skPoint(sketch, "E19.0.14.11", {"position": v(275.5, -386.05) * mm});
            skLineSegment(sketch, "E19.1.14.11", {"start": v(284.5, -344.88) * mm, "end": v(284.5, -384.05) * mm});
            skPoint(sketch, "E19.4.14.11", {"position": v(284.5, -386.05) * mm});
            skLineSegment(sketch, "E19.5.14.11", {"start": v(275.5, -344.88) * mm, "end": v(284.5, -344.88) * mm});
            skLineSegment(sketch, "E19.8.14.11", {"start": v(277.5, -386.05) * mm, "end": v(282.5, -386.05) * mm});
            skLineSegment(sketch, "E19.11.14.11", {"start": v(275.5, -344.88) * mm, "end": v(275.5, -384.05) * mm});
            skArc(sketch, "E19.14.14.11", {"start": v(282.5, -386.05) * mm, "mid": v(283.91, -385.47) * mm, "end": v(284.5, -384.05) * mm});
            skArc(sketch, "E19.18.14.11", {"start": v(275.5, -384.05) * mm, "mid": v(276.09, -385.47) * mm, "end": v(277.5, -386.05) * mm});
            skPoint(sketch, "E19.0.14.12", {"position": v(275.5, -420.7) * mm});
            skLineSegment(sketch, "E19.1.14.12", {"start": v(284.5, -379.52) * mm, "end": v(284.5, -418.7) * mm});
            skPoint(sketch, "E19.4.14.12", {"position": v(284.5, -420.7) * mm});
            skLineSegment(sketch, "E19.5.14.12", {"start": v(275.5, -379.52) * mm, "end": v(284.5, -379.52) * mm});
            skLineSegment(sketch, "E19.8.14.12", {"start": v(277.5, -420.7) * mm, "end": v(282.5, -420.7) * mm});
            skLineSegment(sketch, "E19.11.14.12", {"start": v(275.5, -379.52) * mm, "end": v(275.5, -418.7) * mm});
            skArc(sketch, "E19.14.14.12", {"start": v(282.5, -420.7) * mm, "mid": v(283.91, -420.1) * mm, "end": v(284.5, -418.7) * mm});
            skArc(sketch, "E19.18.14.12", {"start": v(275.5, -418.7) * mm, "mid": v(276.09, -420.1) * mm, "end": v(277.5, -420.7) * mm});
            skPoint(sketch, "E19.0.14.13", {"position": v(275.5, -455.33) * mm});
            skLineSegment(sketch, "E19.1.14.13", {"start": v(284.5, -414.16) * mm, "end": v(284.5, -453.33) * mm});
            skPoint(sketch, "E19.4.14.13", {"position": v(284.5, -455.33) * mm});
            skLineSegment(sketch, "E19.5.14.13", {"start": v(275.5, -414.16) * mm, "end": v(284.5, -414.16) * mm});
            skLineSegment(sketch, "E19.8.14.13", {"start": v(277.5, -455.33) * mm, "end": v(282.5, -455.33) * mm});
            skLineSegment(sketch, "E19.11.14.13", {"start": v(275.5, -414.16) * mm, "end": v(275.5, -453.33) * mm});
            skArc(sketch, "E19.14.14.13", {"start": v(282.5, -455.33) * mm, "mid": v(283.91, -454.75) * mm, "end": v(284.5, -453.33) * mm});
            skArc(sketch, "E19.18.14.13", {"start": v(275.5, -453.33) * mm, "mid": v(276.09, -454.75) * mm, "end": v(277.5, -455.33) * mm});
            skPoint(sketch, "E19.0.14.14", {"position": v(275.5, -489.97) * mm});
            skLineSegment(sketch, "E19.1.14.14", {"start": v(284.5, -448.8) * mm, "end": v(284.5, -487.97) * mm});
            skPoint(sketch, "E19.4.14.14", {"position": v(284.5, -489.97) * mm});
            skLineSegment(sketch, "E19.5.14.14", {"start": v(275.5, -448.8) * mm, "end": v(284.5, -448.8) * mm});
            skLineSegment(sketch, "E19.8.14.14", {"start": v(277.5, -489.97) * mm, "end": v(282.5, -489.97) * mm});
            skLineSegment(sketch, "E19.11.14.14", {"start": v(275.5, -448.8) * mm, "end": v(275.5, -487.97) * mm});
            skArc(sketch, "E19.14.14.14", {"start": v(282.5, -489.97) * mm, "mid": v(283.91, -489.39) * mm, "end": v(284.5, -487.97) * mm});
            skArc(sketch, "E19.18.14.14", {"start": v(275.5, -487.97) * mm, "mid": v(276.09, -489.39) * mm, "end": v(277.5, -489.97) * mm});
            skPoint(sketch, "E19.0.15.0", {"position": v(295.5, -5) * mm});
            skLineSegment(sketch, "E19.1.15.0", {"start": v(304.5, 36.17) * mm, "end": v(304.5, -3) * mm});
            skPoint(sketch, "E19.4.15.0", {"position": v(304.5, -5) * mm});
            skLineSegment(sketch, "E19.5.15.0", {"start": v(295.5, 36.17) * mm, "end": v(304.5, 36.17) * mm});
            skLineSegment(sketch, "E19.8.15.0", {"start": v(297.5, -5) * mm, "end": v(302.5, -5) * mm});
            skLineSegment(sketch, "E19.11.15.0", {"start": v(295.5, 36.17) * mm, "end": v(295.5, -3) * mm});
            skArc(sketch, "E19.14.15.0", {"start": v(302.5, -5) * mm, "mid": v(303.91, -4.41) * mm, "end": v(304.5, -3) * mm});
            skArc(sketch, "E19.18.15.0", {"start": v(295.5, -3) * mm, "mid": v(296.09, -4.41) * mm, "end": v(297.5, -5) * mm});
            skPoint(sketch, "E19.0.15.1", {"position": v(295.5, -39.64) * mm});
            skLineSegment(sketch, "E19.1.15.1", {"start": v(304.5, 1.53) * mm, "end": v(304.5, -37.64) * mm});
            skPoint(sketch, "E19.4.15.1", {"position": v(304.5, -39.64) * mm});
            skLineSegment(sketch, "E19.5.15.1", {"start": v(295.5, 1.53) * mm, "end": v(304.5, 1.53) * mm});
            skLineSegment(sketch, "E19.8.15.1", {"start": v(297.5, -39.64) * mm, "end": v(302.5, -39.64) * mm});
            skLineSegment(sketch, "E19.11.15.1", {"start": v(295.5, 1.53) * mm, "end": v(295.5, -37.64) * mm});
            skArc(sketch, "E19.14.15.1", {"start": v(302.5, -39.64) * mm, "mid": v(303.91, -39.06) * mm, "end": v(304.5, -37.64) * mm});
            skArc(sketch, "E19.18.15.1", {"start": v(295.5, -37.64) * mm, "mid": v(296.09, -39.06) * mm, "end": v(297.5, -39.64) * mm});
            skPoint(sketch, "E19.0.15.2", {"position": v(295.5, -74.28) * mm});
            skLineSegment(sketch, "E19.1.15.2", {"start": v(304.5, -33.1) * mm, "end": v(304.5, -72.28) * mm});
            skPoint(sketch, "E19.4.15.2", {"position": v(304.5, -74.28) * mm});
            skLineSegment(sketch, "E19.5.15.2", {"start": v(295.5, -33.1) * mm, "end": v(304.5, -33.1) * mm});
            skLineSegment(sketch, "E19.8.15.2", {"start": v(297.5, -74.28) * mm, "end": v(302.5, -74.28) * mm});
            skLineSegment(sketch, "E19.11.15.2", {"start": v(295.5, -33.1) * mm, "end": v(295.5, -72.28) * mm});
            skArc(sketch, "E19.14.15.2", {"start": v(302.5, -74.28) * mm, "mid": v(303.91, -73.7) * mm, "end": v(304.5, -72.28) * mm});
            skArc(sketch, "E19.18.15.2", {"start": v(295.5, -72.28) * mm, "mid": v(296.09, -73.7) * mm, "end": v(297.5, -74.28) * mm});
            skPoint(sketch, "E19.0.15.3", {"position": v(295.5, -108.92) * mm});
            skLineSegment(sketch, "E19.1.15.3", {"start": v(304.5, -67.75) * mm, "end": v(304.5, -106.92) * mm});
            skPoint(sketch, "E19.4.15.3", {"position": v(304.5, -108.92) * mm});
            skLineSegment(sketch, "E19.5.15.3", {"start": v(295.5, -67.75) * mm, "end": v(304.5, -67.75) * mm});
            skLineSegment(sketch, "E19.8.15.3", {"start": v(297.5, -108.92) * mm, "end": v(302.5, -108.92) * mm});
            skLineSegment(sketch, "E19.11.15.3", {"start": v(295.5, -67.75) * mm, "end": v(295.5, -106.92) * mm});
            skArc(sketch, "E19.14.15.3", {"start": v(302.5, -108.92) * mm, "mid": v(303.91, -108.34) * mm, "end": v(304.5, -106.92) * mm});
            skArc(sketch, "E19.18.15.3", {"start": v(295.5, -106.92) * mm, "mid": v(296.09, -108.34) * mm, "end": v(297.5, -108.92) * mm});
            skPoint(sketch, "E19.0.15.4", {"position": v(295.5, -143.56) * mm});
            skLineSegment(sketch, "E19.1.15.4", {"start": v(304.5, -102.4) * mm, "end": v(304.5, -141.56) * mm});
            skPoint(sketch, "E19.4.15.4", {"position": v(304.5, -143.56) * mm});
            skLineSegment(sketch, "E19.5.15.4", {"start": v(295.5, -102.4) * mm, "end": v(304.5, -102.4) * mm});
            skLineSegment(sketch, "E19.8.15.4", {"start": v(297.5, -143.56) * mm, "end": v(302.5, -143.56) * mm});
            skLineSegment(sketch, "E19.11.15.4", {"start": v(295.5, -102.4) * mm, "end": v(295.5, -141.56) * mm});
            skArc(sketch, "E19.14.15.4", {"start": v(302.5, -143.56) * mm, "mid": v(303.91, -142.98) * mm, "end": v(304.5, -141.56) * mm});
            skArc(sketch, "E19.18.15.4", {"start": v(295.5, -141.56) * mm, "mid": v(296.09, -142.98) * mm, "end": v(297.5, -143.56) * mm});
            skPoint(sketch, "E19.0.15.5", {"position": v(295.5, -178.2) * mm});
            skLineSegment(sketch, "E19.1.15.5", {"start": v(304.5, -137.03) * mm, "end": v(304.5, -176.2) * mm});
            skPoint(sketch, "E19.4.15.5", {"position": v(304.5, -178.2) * mm});
            skLineSegment(sketch, "E19.5.15.5", {"start": v(295.5, -137.03) * mm, "end": v(304.5, -137.03) * mm});
            skLineSegment(sketch, "E19.8.15.5", {"start": v(297.5, -178.2) * mm, "end": v(302.5, -178.2) * mm});
            skLineSegment(sketch, "E19.11.15.5", {"start": v(295.5, -137.03) * mm, "end": v(295.5, -176.2) * mm});
            skArc(sketch, "E19.14.15.5", {"start": v(302.5, -178.2) * mm, "mid": v(303.91, -177.62) * mm, "end": v(304.5, -176.2) * mm});
            skArc(sketch, "E19.18.15.5", {"start": v(295.5, -176.2) * mm, "mid": v(296.09, -177.62) * mm, "end": v(297.5, -178.2) * mm});
            skPoint(sketch, "E19.0.15.6", {"position": v(295.5, -212.85) * mm});
            skLineSegment(sketch, "E19.1.15.6", {"start": v(304.5, -171.67) * mm, "end": v(304.5, -210.85) * mm});
            skPoint(sketch, "E19.4.15.6", {"position": v(304.5, -212.85) * mm});
            skLineSegment(sketch, "E19.5.15.6", {"start": v(295.5, -171.67) * mm, "end": v(304.5, -171.67) * mm});
            skLineSegment(sketch, "E19.8.15.6", {"start": v(297.5, -212.85) * mm, "end": v(302.5, -212.85) * mm});
            skLineSegment(sketch, "E19.11.15.6", {"start": v(295.5, -171.67) * mm, "end": v(295.5, -210.85) * mm});
            skArc(sketch, "E19.14.15.6", {"start": v(302.5, -212.85) * mm, "mid": v(303.91, -212.26) * mm, "end": v(304.5, -210.85) * mm});
            skArc(sketch, "E19.18.15.6", {"start": v(295.5, -210.85) * mm, "mid": v(296.09, -212.26) * mm, "end": v(297.5, -212.85) * mm});
            skPoint(sketch, "E19.0.15.7", {"position": v(295.5, -247.49) * mm});
            skLineSegment(sketch, "E19.1.15.7", {"start": v(304.5, -206.31) * mm, "end": v(304.5, -245.49) * mm});
            skPoint(sketch, "E19.4.15.7", {"position": v(304.5, -247.49) * mm});
            skLineSegment(sketch, "E19.5.15.7", {"start": v(295.5, -206.31) * mm, "end": v(304.5, -206.31) * mm});
            skLineSegment(sketch, "E19.8.15.7", {"start": v(297.5, -247.49) * mm, "end": v(302.5, -247.49) * mm});
            skLineSegment(sketch, "E19.11.15.7", {"start": v(295.5, -206.31) * mm, "end": v(295.5, -245.49) * mm});
            skArc(sketch, "E19.14.15.7", {"start": v(302.5, -247.49) * mm, "mid": v(303.91, -246.9) * mm, "end": v(304.5, -245.49) * mm});
            skArc(sketch, "E19.18.15.7", {"start": v(295.5, -245.49) * mm, "mid": v(296.09, -246.9) * mm, "end": v(297.5, -247.49) * mm});
            skPoint(sketch, "E19.0.15.8", {"position": v(295.5, -282.13) * mm});
            skLineSegment(sketch, "E19.1.15.8", {"start": v(304.5, -240.95) * mm, "end": v(304.5, -280.13) * mm});
            skPoint(sketch, "E19.4.15.8", {"position": v(304.5, -282.13) * mm});
            skLineSegment(sketch, "E19.5.15.8", {"start": v(295.5, -240.95) * mm, "end": v(304.5, -240.95) * mm});
            skLineSegment(sketch, "E19.8.15.8", {"start": v(297.5, -282.13) * mm, "end": v(302.5, -282.13) * mm});
            skLineSegment(sketch, "E19.11.15.8", {"start": v(295.5, -240.95) * mm, "end": v(295.5, -280.13) * mm});
            skArc(sketch, "E19.14.15.8", {"start": v(302.5, -282.13) * mm, "mid": v(303.91, -281.54) * mm, "end": v(304.5, -280.13) * mm});
            skArc(sketch, "E19.18.15.8", {"start": v(295.5, -280.13) * mm, "mid": v(296.09, -281.54) * mm, "end": v(297.5, -282.13) * mm});
            skPoint(sketch, "E19.0.15.9", {"position": v(295.5, -316.77) * mm});
            skLineSegment(sketch, "E19.1.15.9", {"start": v(304.5, -275.6) * mm, "end": v(304.5, -314.77) * mm});
            skPoint(sketch, "E19.4.15.9", {"position": v(304.5, -316.77) * mm});
            skLineSegment(sketch, "E19.5.15.9", {"start": v(295.5, -275.6) * mm, "end": v(304.5, -275.6) * mm});
            skLineSegment(sketch, "E19.8.15.9", {"start": v(297.5, -316.77) * mm, "end": v(302.5, -316.77) * mm});
            skLineSegment(sketch, "E19.11.15.9", {"start": v(295.5, -275.6) * mm, "end": v(295.5, -314.77) * mm});
            skArc(sketch, "E19.14.15.9", {"start": v(302.5, -316.77) * mm, "mid": v(303.91, -316.18) * mm, "end": v(304.5, -314.77) * mm});
            skArc(sketch, "E19.18.15.9", {"start": v(295.5, -314.77) * mm, "mid": v(296.09, -316.18) * mm, "end": v(297.5, -316.77) * mm});
            skPoint(sketch, "E19.0.15.10", {"position": v(295.5, -351.41) * mm});
            skLineSegment(sketch, "E19.1.15.10", {"start": v(304.5, -310.24) * mm, "end": v(304.5, -349.41) * mm});
            skPoint(sketch, "E19.4.15.10", {"position": v(304.5, -351.41) * mm});
            skLineSegment(sketch, "E19.5.15.10", {"start": v(295.5, -310.24) * mm, "end": v(304.5, -310.24) * mm});
            skLineSegment(sketch, "E19.8.15.10", {"start": v(297.5, -351.41) * mm, "end": v(302.5, -351.41) * mm});
            skLineSegment(sketch, "E19.11.15.10", {"start": v(295.5, -310.24) * mm, "end": v(295.5, -349.41) * mm});
            skArc(sketch, "E19.14.15.10", {"start": v(302.5, -351.41) * mm, "mid": v(303.91, -350.82) * mm, "end": v(304.5, -349.41) * mm});
            skArc(sketch, "E19.18.15.10", {"start": v(295.5, -349.41) * mm, "mid": v(296.09, -350.82) * mm, "end": v(297.5, -351.41) * mm});
            skPoint(sketch, "E19.0.15.11", {"position": v(295.5, -386.05) * mm});
            skLineSegment(sketch, "E19.1.15.11", {"start": v(304.5, -344.88) * mm, "end": v(304.5, -384.05) * mm});
            skPoint(sketch, "E19.4.15.11", {"position": v(304.5, -386.05) * mm});
            skLineSegment(sketch, "E19.5.15.11", {"start": v(295.5, -344.88) * mm, "end": v(304.5, -344.88) * mm});
            skLineSegment(sketch, "E19.8.15.11", {"start": v(297.5, -386.05) * mm, "end": v(302.5, -386.05) * mm});
            skLineSegment(sketch, "E19.11.15.11", {"start": v(295.5, -344.88) * mm, "end": v(295.5, -384.05) * mm});
            skArc(sketch, "E19.14.15.11", {"start": v(302.5, -386.05) * mm, "mid": v(303.91, -385.47) * mm, "end": v(304.5, -384.05) * mm});
            skArc(sketch, "E19.18.15.11", {"start": v(295.5, -384.05) * mm, "mid": v(296.09, -385.47) * mm, "end": v(297.5, -386.05) * mm});
            skPoint(sketch, "E19.0.15.12", {"position": v(295.5, -420.7) * mm});
            skLineSegment(sketch, "E19.1.15.12", {"start": v(304.5, -379.52) * mm, "end": v(304.5, -418.7) * mm});
            skPoint(sketch, "E19.4.15.12", {"position": v(304.5, -420.7) * mm});
            skLineSegment(sketch, "E19.5.15.12", {"start": v(295.5, -379.52) * mm, "end": v(304.5, -379.52) * mm});
            skLineSegment(sketch, "E19.8.15.12", {"start": v(297.5, -420.7) * mm, "end": v(302.5, -420.7) * mm});
            skLineSegment(sketch, "E19.11.15.12", {"start": v(295.5, -379.52) * mm, "end": v(295.5, -418.7) * mm});
            skArc(sketch, "E19.14.15.12", {"start": v(302.5, -420.7) * mm, "mid": v(303.91, -420.1) * mm, "end": v(304.5, -418.7) * mm});
            skArc(sketch, "E19.18.15.12", {"start": v(295.5, -418.7) * mm, "mid": v(296.09, -420.1) * mm, "end": v(297.5, -420.7) * mm});
            skPoint(sketch, "E19.0.15.13", {"position": v(295.5, -455.33) * mm});
            skLineSegment(sketch, "E19.1.15.13", {"start": v(304.5, -414.16) * mm, "end": v(304.5, -453.33) * mm});
            skPoint(sketch, "E19.4.15.13", {"position": v(304.5, -455.33) * mm});
            skLineSegment(sketch, "E19.5.15.13", {"start": v(295.5, -414.16) * mm, "end": v(304.5, -414.16) * mm});
            skLineSegment(sketch, "E19.8.15.13", {"start": v(297.5, -455.33) * mm, "end": v(302.5, -455.33) * mm});
            skLineSegment(sketch, "E19.11.15.13", {"start": v(295.5, -414.16) * mm, "end": v(295.5, -453.33) * mm});
            skArc(sketch, "E19.14.15.13", {"start": v(302.5, -455.33) * mm, "mid": v(303.91, -454.75) * mm, "end": v(304.5, -453.33) * mm});
            skArc(sketch, "E19.18.15.13", {"start": v(295.5, -453.33) * mm, "mid": v(296.09, -454.75) * mm, "end": v(297.5, -455.33) * mm});
            skPoint(sketch, "E19.0.15.14", {"position": v(295.5, -489.97) * mm});
            skLineSegment(sketch, "E19.1.15.14", {"start": v(304.5, -448.8) * mm, "end": v(304.5, -487.97) * mm});
            skPoint(sketch, "E19.4.15.14", {"position": v(304.5, -489.97) * mm});
            skLineSegment(sketch, "E19.5.15.14", {"start": v(295.5, -448.8) * mm, "end": v(304.5, -448.8) * mm});
            skLineSegment(sketch, "E19.8.15.14", {"start": v(297.5, -489.97) * mm, "end": v(302.5, -489.97) * mm});
            skLineSegment(sketch, "E19.11.15.14", {"start": v(295.5, -448.8) * mm, "end": v(295.5, -487.97) * mm});
            skArc(sketch, "E19.14.15.14", {"start": v(302.5, -489.97) * mm, "mid": v(303.91, -489.39) * mm, "end": v(304.5, -487.97) * mm});
            skArc(sketch, "E19.18.15.14", {"start": v(295.5, -487.97) * mm, "mid": v(296.09, -489.39) * mm, "end": v(297.5, -489.97) * mm});
            skPoint(sketch, "E19.0.16.0", {"position": v(315.5, -5) * mm});
            skLineSegment(sketch, "E19.1.16.0", {"start": v(324.5, 36.17) * mm, "end": v(324.5, -3) * mm});
            skPoint(sketch, "E19.4.16.0", {"position": v(324.5, -5) * mm});
            skLineSegment(sketch, "E19.5.16.0", {"start": v(315.5, 36.17) * mm, "end": v(324.5, 36.17) * mm});
            skLineSegment(sketch, "E19.8.16.0", {"start": v(317.5, -5) * mm, "end": v(322.5, -5) * mm});
            skLineSegment(sketch, "E19.11.16.0", {"start": v(315.5, 36.17) * mm, "end": v(315.5, -3) * mm});
            skArc(sketch, "E19.14.16.0", {"start": v(322.5, -5) * mm, "mid": v(323.91, -4.41) * mm, "end": v(324.5, -3) * mm});
            skArc(sketch, "E19.18.16.0", {"start": v(315.5, -3) * mm, "mid": v(316.09, -4.41) * mm, "end": v(317.5, -5) * mm});
            skPoint(sketch, "E19.0.16.1", {"position": v(315.5, -39.64) * mm});
            skLineSegment(sketch, "E19.1.16.1", {"start": v(324.5, 1.53) * mm, "end": v(324.5, -37.64) * mm});
            skPoint(sketch, "E19.4.16.1", {"position": v(324.5, -39.64) * mm});
            skLineSegment(sketch, "E19.5.16.1", {"start": v(315.5, 1.53) * mm, "end": v(324.5, 1.53) * mm});
            skLineSegment(sketch, "E19.8.16.1", {"start": v(317.5, -39.64) * mm, "end": v(322.5, -39.64) * mm});
            skLineSegment(sketch, "E19.11.16.1", {"start": v(315.5, 1.53) * mm, "end": v(315.5, -37.64) * mm});
            skArc(sketch, "E19.14.16.1", {"start": v(322.5, -39.64) * mm, "mid": v(323.91, -39.06) * mm, "end": v(324.5, -37.64) * mm});
            skArc(sketch, "E19.18.16.1", {"start": v(315.5, -37.64) * mm, "mid": v(316.09, -39.06) * mm, "end": v(317.5, -39.64) * mm});
            skPoint(sketch, "E19.0.16.2", {"position": v(315.5, -74.28) * mm});
            skLineSegment(sketch, "E19.1.16.2", {"start": v(324.5, -33.1) * mm, "end": v(324.5, -72.28) * mm});
            skPoint(sketch, "E19.4.16.2", {"position": v(324.5, -74.28) * mm});
            skLineSegment(sketch, "E19.5.16.2", {"start": v(315.5, -33.1) * mm, "end": v(324.5, -33.1) * mm});
            skLineSegment(sketch, "E19.8.16.2", {"start": v(317.5, -74.28) * mm, "end": v(322.5, -74.28) * mm});
            skLineSegment(sketch, "E19.11.16.2", {"start": v(315.5, -33.1) * mm, "end": v(315.5, -72.28) * mm});
            skArc(sketch, "E19.14.16.2", {"start": v(322.5, -74.28) * mm, "mid": v(323.91, -73.7) * mm, "end": v(324.5, -72.28) * mm});
            skArc(sketch, "E19.18.16.2", {"start": v(315.5, -72.28) * mm, "mid": v(316.09, -73.7) * mm, "end": v(317.5, -74.28) * mm});
            skPoint(sketch, "E19.0.16.3", {"position": v(315.5, -108.92) * mm});
            skLineSegment(sketch, "E19.1.16.3", {"start": v(324.5, -67.75) * mm, "end": v(324.5, -106.92) * mm});
            skPoint(sketch, "E19.4.16.3", {"position": v(324.5, -108.92) * mm});
            skLineSegment(sketch, "E19.5.16.3", {"start": v(315.5, -67.75) * mm, "end": v(324.5, -67.75) * mm});
            skLineSegment(sketch, "E19.8.16.3", {"start": v(317.5, -108.92) * mm, "end": v(322.5, -108.92) * mm});
            skLineSegment(sketch, "E19.11.16.3", {"start": v(315.5, -67.75) * mm, "end": v(315.5, -106.92) * mm});
            skArc(sketch, "E19.14.16.3", {"start": v(322.5, -108.92) * mm, "mid": v(323.91, -108.34) * mm, "end": v(324.5, -106.92) * mm});
            skArc(sketch, "E19.18.16.3", {"start": v(315.5, -106.92) * mm, "mid": v(316.09, -108.34) * mm, "end": v(317.5, -108.92) * mm});
            skPoint(sketch, "E19.0.16.4", {"position": v(315.5, -143.56) * mm});
            skLineSegment(sketch, "E19.1.16.4", {"start": v(324.5, -102.4) * mm, "end": v(324.5, -141.56) * mm});
            skPoint(sketch, "E19.4.16.4", {"position": v(324.5, -143.56) * mm});
            skLineSegment(sketch, "E19.5.16.4", {"start": v(315.5, -102.4) * mm, "end": v(324.5, -102.4) * mm});
            skLineSegment(sketch, "E19.8.16.4", {"start": v(317.5, -143.56) * mm, "end": v(322.5, -143.56) * mm});
            skLineSegment(sketch, "E19.11.16.4", {"start": v(315.5, -102.4) * mm, "end": v(315.5, -141.56) * mm});
            skArc(sketch, "E19.14.16.4", {"start": v(322.5, -143.56) * mm, "mid": v(323.91, -142.98) * mm, "end": v(324.5, -141.56) * mm});
            skArc(sketch, "E19.18.16.4", {"start": v(315.5, -141.56) * mm, "mid": v(316.09, -142.98) * mm, "end": v(317.5, -143.56) * mm});
            skPoint(sketch, "E19.0.16.5", {"position": v(315.5, -178.2) * mm});
            skLineSegment(sketch, "E19.1.16.5", {"start": v(324.5, -137.03) * mm, "end": v(324.5, -176.2) * mm});
            skPoint(sketch, "E19.4.16.5", {"position": v(324.5, -178.2) * mm});
            skLineSegment(sketch, "E19.5.16.5", {"start": v(315.5, -137.03) * mm, "end": v(324.5, -137.03) * mm});
            skLineSegment(sketch, "E19.8.16.5", {"start": v(317.5, -178.2) * mm, "end": v(322.5, -178.2) * mm});
            skLineSegment(sketch, "E19.11.16.5", {"start": v(315.5, -137.03) * mm, "end": v(315.5, -176.2) * mm});
            skArc(sketch, "E19.14.16.5", {"start": v(322.5, -178.2) * mm, "mid": v(323.91, -177.62) * mm, "end": v(324.5, -176.2) * mm});
            skArc(sketch, "E19.18.16.5", {"start": v(315.5, -176.2) * mm, "mid": v(316.09, -177.62) * mm, "end": v(317.5, -178.2) * mm});
            skPoint(sketch, "E19.0.16.6", {"position": v(315.5, -212.85) * mm});
            skLineSegment(sketch, "E19.1.16.6", {"start": v(324.5, -171.67) * mm, "end": v(324.5, -210.85) * mm});
            skPoint(sketch, "E19.4.16.6", {"position": v(324.5, -212.85) * mm});
            skLineSegment(sketch, "E19.5.16.6", {"start": v(315.5, -171.67) * mm, "end": v(324.5, -171.67) * mm});
            skLineSegment(sketch, "E19.8.16.6", {"start": v(317.5, -212.85) * mm, "end": v(322.5, -212.85) * mm});
            skLineSegment(sketch, "E19.11.16.6", {"start": v(315.5, -171.67) * mm, "end": v(315.5, -210.85) * mm});
            skArc(sketch, "E19.14.16.6", {"start": v(322.5, -212.85) * mm, "mid": v(323.91, -212.26) * mm, "end": v(324.5, -210.85) * mm});
            skArc(sketch, "E19.18.16.6", {"start": v(315.5, -210.85) * mm, "mid": v(316.09, -212.26) * mm, "end": v(317.5, -212.85) * mm});
            skPoint(sketch, "E19.0.16.7", {"position": v(315.5, -247.49) * mm});
            skLineSegment(sketch, "E19.1.16.7", {"start": v(324.5, -206.31) * mm, "end": v(324.5, -245.49) * mm});
            skPoint(sketch, "E19.4.16.7", {"position": v(324.5, -247.49) * mm});
            skLineSegment(sketch, "E19.5.16.7", {"start": v(315.5, -206.31) * mm, "end": v(324.5, -206.31) * mm});
            skLineSegment(sketch, "E19.8.16.7", {"start": v(317.5, -247.49) * mm, "end": v(322.5, -247.49) * mm});
            skLineSegment(sketch, "E19.11.16.7", {"start": v(315.5, -206.31) * mm, "end": v(315.5, -245.49) * mm});
            skArc(sketch, "E19.14.16.7", {"start": v(322.5, -247.49) * mm, "mid": v(323.91, -246.9) * mm, "end": v(324.5, -245.49) * mm});
            skArc(sketch, "E19.18.16.7", {"start": v(315.5, -245.49) * mm, "mid": v(316.09, -246.9) * mm, "end": v(317.5, -247.49) * mm});
            skPoint(sketch, "E19.0.16.8", {"position": v(315.5, -282.13) * mm});
            skLineSegment(sketch, "E19.1.16.8", {"start": v(324.5, -240.95) * mm, "end": v(324.5, -280.13) * mm});
            skPoint(sketch, "E19.4.16.8", {"position": v(324.5, -282.13) * mm});
            skLineSegment(sketch, "E19.5.16.8", {"start": v(315.5, -240.95) * mm, "end": v(324.5, -240.95) * mm});
            skLineSegment(sketch, "E19.8.16.8", {"start": v(317.5, -282.13) * mm, "end": v(322.5, -282.13) * mm});
            skLineSegment(sketch, "E19.11.16.8", {"start": v(315.5, -240.95) * mm, "end": v(315.5, -280.13) * mm});
            skArc(sketch, "E19.14.16.8", {"start": v(322.5, -282.13) * mm, "mid": v(323.91, -281.54) * mm, "end": v(324.5, -280.13) * mm});
            skArc(sketch, "E19.18.16.8", {"start": v(315.5, -280.13) * mm, "mid": v(316.09, -281.54) * mm, "end": v(317.5, -282.13) * mm});
            skPoint(sketch, "E19.0.16.9", {"position": v(315.5, -316.77) * mm});
            skLineSegment(sketch, "E19.1.16.9", {"start": v(324.5, -275.6) * mm, "end": v(324.5, -314.77) * mm});
            skPoint(sketch, "E19.4.16.9", {"position": v(324.5, -316.77) * mm});
            skLineSegment(sketch, "E19.5.16.9", {"start": v(315.5, -275.6) * mm, "end": v(324.5, -275.6) * mm});
            skLineSegment(sketch, "E19.8.16.9", {"start": v(317.5, -316.77) * mm, "end": v(322.5, -316.77) * mm});
            skLineSegment(sketch, "E19.11.16.9", {"start": v(315.5, -275.6) * mm, "end": v(315.5, -314.77) * mm});
            skArc(sketch, "E19.14.16.9", {"start": v(322.5, -316.77) * mm, "mid": v(323.91, -316.18) * mm, "end": v(324.5, -314.77) * mm});
            skArc(sketch, "E19.18.16.9", {"start": v(315.5, -314.77) * mm, "mid": v(316.09, -316.18) * mm, "end": v(317.5, -316.77) * mm});
            skPoint(sketch, "E19.0.16.10", {"position": v(315.5, -351.41) * mm});
            skLineSegment(sketch, "E19.1.16.10", {"start": v(324.5, -310.24) * mm, "end": v(324.5, -349.41) * mm});
            skPoint(sketch, "E19.4.16.10", {"position": v(324.5, -351.41) * mm});
            skLineSegment(sketch, "E19.5.16.10", {"start": v(315.5, -310.24) * mm, "end": v(324.5, -310.24) * mm});
            skLineSegment(sketch, "E19.8.16.10", {"start": v(317.5, -351.41) * mm, "end": v(322.5, -351.41) * mm});
            skLineSegment(sketch, "E19.11.16.10", {"start": v(315.5, -310.24) * mm, "end": v(315.5, -349.41) * mm});
            skArc(sketch, "E19.14.16.10", {"start": v(322.5, -351.41) * mm, "mid": v(323.91, -350.82) * mm, "end": v(324.5, -349.41) * mm});
            skArc(sketch, "E19.18.16.10", {"start": v(315.5, -349.41) * mm, "mid": v(316.09, -350.82) * mm, "end": v(317.5, -351.41) * mm});
            skPoint(sketch, "E19.0.16.11", {"position": v(315.5, -386.05) * mm});
            skLineSegment(sketch, "E19.1.16.11", {"start": v(324.5, -344.88) * mm, "end": v(324.5, -384.05) * mm});
            skPoint(sketch, "E19.4.16.11", {"position": v(324.5, -386.05) * mm});
            skLineSegment(sketch, "E19.5.16.11", {"start": v(315.5, -344.88) * mm, "end": v(324.5, -344.88) * mm});
            skLineSegment(sketch, "E19.8.16.11", {"start": v(317.5, -386.05) * mm, "end": v(322.5, -386.05) * mm});
            skLineSegment(sketch, "E19.11.16.11", {"start": v(315.5, -344.88) * mm, "end": v(315.5, -384.05) * mm});
            skArc(sketch, "E19.14.16.11", {"start": v(322.5, -386.05) * mm, "mid": v(323.91, -385.47) * mm, "end": v(324.5, -384.05) * mm});
            skArc(sketch, "E19.18.16.11", {"start": v(315.5, -384.05) * mm, "mid": v(316.09, -385.47) * mm, "end": v(317.5, -386.05) * mm});
            skPoint(sketch, "E19.0.16.12", {"position": v(315.5, -420.7) * mm});
            skLineSegment(sketch, "E19.1.16.12", {"start": v(324.5, -379.52) * mm, "end": v(324.5, -418.7) * mm});
            skPoint(sketch, "E19.4.16.12", {"position": v(324.5, -420.7) * mm});
            skLineSegment(sketch, "E19.5.16.12", {"start": v(315.5, -379.52) * mm, "end": v(324.5, -379.52) * mm});
            skLineSegment(sketch, "E19.8.16.12", {"start": v(317.5, -420.7) * mm, "end": v(322.5, -420.7) * mm});
            skLineSegment(sketch, "E19.11.16.12", {"start": v(315.5, -379.52) * mm, "end": v(315.5, -418.7) * mm});
            skArc(sketch, "E19.14.16.12", {"start": v(322.5, -420.7) * mm, "mid": v(323.91, -420.1) * mm, "end": v(324.5, -418.7) * mm});
            skArc(sketch, "E19.18.16.12", {"start": v(315.5, -418.7) * mm, "mid": v(316.09, -420.1) * mm, "end": v(317.5, -420.7) * mm});
            skPoint(sketch, "E19.0.16.13", {"position": v(315.5, -455.33) * mm});
            skLineSegment(sketch, "E19.1.16.13", {"start": v(324.5, -414.16) * mm, "end": v(324.5, -453.33) * mm});
            skPoint(sketch, "E19.4.16.13", {"position": v(324.5, -455.33) * mm});
            skLineSegment(sketch, "E19.5.16.13", {"start": v(315.5, -414.16) * mm, "end": v(324.5, -414.16) * mm});
            skLineSegment(sketch, "E19.8.16.13", {"start": v(317.5, -455.33) * mm, "end": v(322.5, -455.33) * mm});
            skLineSegment(sketch, "E19.11.16.13", {"start": v(315.5, -414.16) * mm, "end": v(315.5, -453.33) * mm});
            skArc(sketch, "E19.14.16.13", {"start": v(322.5, -455.33) * mm, "mid": v(323.91, -454.75) * mm, "end": v(324.5, -453.33) * mm});
            skArc(sketch, "E19.18.16.13", {"start": v(315.5, -453.33) * mm, "mid": v(316.09, -454.75) * mm, "end": v(317.5, -455.33) * mm});
            skPoint(sketch, "E19.0.16.14", {"position": v(315.5, -489.97) * mm});
            skLineSegment(sketch, "E19.1.16.14", {"start": v(324.5, -448.8) * mm, "end": v(324.5, -487.97) * mm});
            skPoint(sketch, "E19.4.16.14", {"position": v(324.5, -489.97) * mm});
            skLineSegment(sketch, "E19.5.16.14", {"start": v(315.5, -448.8) * mm, "end": v(324.5, -448.8) * mm});
            skLineSegment(sketch, "E19.8.16.14", {"start": v(317.5, -489.97) * mm, "end": v(322.5, -489.97) * mm});
            skLineSegment(sketch, "E19.11.16.14", {"start": v(315.5, -448.8) * mm, "end": v(315.5, -487.97) * mm});
            skArc(sketch, "E19.14.16.14", {"start": v(322.5, -489.97) * mm, "mid": v(323.91, -489.39) * mm, "end": v(324.5, -487.97) * mm});
            skArc(sketch, "E19.18.16.14", {"start": v(315.5, -487.97) * mm, "mid": v(316.09, -489.39) * mm, "end": v(317.5, -489.97) * mm});
            skPoint(sketch, "E19.0.17.0", {"position": v(335.5, -5) * mm});
            skLineSegment(sketch, "E19.1.17.0", {"start": v(344.5, 36.17) * mm, "end": v(344.5, -3) * mm});
            skPoint(sketch, "E19.4.17.0", {"position": v(344.5, -5) * mm});
            skLineSegment(sketch, "E19.5.17.0", {"start": v(335.5, 36.17) * mm, "end": v(344.5, 36.17) * mm});
            skLineSegment(sketch, "E19.8.17.0", {"start": v(337.5, -5) * mm, "end": v(342.5, -5) * mm});
            skLineSegment(sketch, "E19.11.17.0", {"start": v(335.5, 36.17) * mm, "end": v(335.5, -3) * mm});
            skArc(sketch, "E19.14.17.0", {"start": v(342.5, -5) * mm, "mid": v(343.91, -4.41) * mm, "end": v(344.5, -3) * mm});
            skArc(sketch, "E19.18.17.0", {"start": v(335.5, -3) * mm, "mid": v(336.09, -4.41) * mm, "end": v(337.5, -5) * mm});
            skPoint(sketch, "E19.0.17.1", {"position": v(335.5, -39.64) * mm});
            skLineSegment(sketch, "E19.1.17.1", {"start": v(344.5, 1.53) * mm, "end": v(344.5, -37.64) * mm});
            skPoint(sketch, "E19.4.17.1", {"position": v(344.5, -39.64) * mm});
            skLineSegment(sketch, "E19.5.17.1", {"start": v(335.5, 1.53) * mm, "end": v(344.5, 1.53) * mm});
            skLineSegment(sketch, "E19.8.17.1", {"start": v(337.5, -39.64) * mm, "end": v(342.5, -39.64) * mm});
            skLineSegment(sketch, "E19.11.17.1", {"start": v(335.5, 1.53) * mm, "end": v(335.5, -37.64) * mm});
            skArc(sketch, "E19.14.17.1", {"start": v(342.5, -39.64) * mm, "mid": v(343.91, -39.06) * mm, "end": v(344.5, -37.64) * mm});
            skArc(sketch, "E19.18.17.1", {"start": v(335.5, -37.64) * mm, "mid": v(336.09, -39.06) * mm, "end": v(337.5, -39.64) * mm});
            skPoint(sketch, "E19.0.17.2", {"position": v(335.5, -74.28) * mm});
            skLineSegment(sketch, "E19.1.17.2", {"start": v(344.5, -33.1) * mm, "end": v(344.5, -72.28) * mm});
            skPoint(sketch, "E19.4.17.2", {"position": v(344.5, -74.28) * mm});
            skLineSegment(sketch, "E19.5.17.2", {"start": v(335.5, -33.1) * mm, "end": v(344.5, -33.1) * mm});
            skLineSegment(sketch, "E19.8.17.2", {"start": v(337.5, -74.28) * mm, "end": v(342.5, -74.28) * mm});
            skLineSegment(sketch, "E19.11.17.2", {"start": v(335.5, -33.1) * mm, "end": v(335.5, -72.28) * mm});
            skArc(sketch, "E19.14.17.2", {"start": v(342.5, -74.28) * mm, "mid": v(343.91, -73.7) * mm, "end": v(344.5, -72.28) * mm});
            skArc(sketch, "E19.18.17.2", {"start": v(335.5, -72.28) * mm, "mid": v(336.09, -73.7) * mm, "end": v(337.5, -74.28) * mm});
            skPoint(sketch, "E19.0.17.3", {"position": v(335.5, -108.92) * mm});
            skLineSegment(sketch, "E19.1.17.3", {"start": v(344.5, -67.75) * mm, "end": v(344.5, -106.92) * mm});
            skPoint(sketch, "E19.4.17.3", {"position": v(344.5, -108.92) * mm});
            skLineSegment(sketch, "E19.5.17.3", {"start": v(335.5, -67.75) * mm, "end": v(344.5, -67.75) * mm});
            skLineSegment(sketch, "E19.8.17.3", {"start": v(337.5, -108.92) * mm, "end": v(342.5, -108.92) * mm});
            skLineSegment(sketch, "E19.11.17.3", {"start": v(335.5, -67.75) * mm, "end": v(335.5, -106.92) * mm});
            skArc(sketch, "E19.14.17.3", {"start": v(342.5, -108.92) * mm, "mid": v(343.91, -108.34) * mm, "end": v(344.5, -106.92) * mm});
            skArc(sketch, "E19.18.17.3", {"start": v(335.5, -106.92) * mm, "mid": v(336.09, -108.34) * mm, "end": v(337.5, -108.92) * mm});
            skPoint(sketch, "E19.0.17.4", {"position": v(335.5, -143.56) * mm});
            skLineSegment(sketch, "E19.1.17.4", {"start": v(344.5, -102.4) * mm, "end": v(344.5, -141.56) * mm});
            skPoint(sketch, "E19.4.17.4", {"position": v(344.5, -143.56) * mm});
            skLineSegment(sketch, "E19.5.17.4", {"start": v(335.5, -102.4) * mm, "end": v(344.5, -102.4) * mm});
            skLineSegment(sketch, "E19.8.17.4", {"start": v(337.5, -143.56) * mm, "end": v(342.5, -143.56) * mm});
            skLineSegment(sketch, "E19.11.17.4", {"start": v(335.5, -102.4) * mm, "end": v(335.5, -141.56) * mm});
            skArc(sketch, "E19.14.17.4", {"start": v(342.5, -143.56) * mm, "mid": v(343.91, -142.98) * mm, "end": v(344.5, -141.56) * mm});
            skArc(sketch, "E19.18.17.4", {"start": v(335.5, -141.56) * mm, "mid": v(336.09, -142.98) * mm, "end": v(337.5, -143.56) * mm});
            skPoint(sketch, "E19.0.17.5", {"position": v(335.5, -178.2) * mm});
            skLineSegment(sketch, "E19.1.17.5", {"start": v(344.5, -137.03) * mm, "end": v(344.5, -176.2) * mm});
            skPoint(sketch, "E19.4.17.5", {"position": v(344.5, -178.2) * mm});
            skLineSegment(sketch, "E19.5.17.5", {"start": v(335.5, -137.03) * mm, "end": v(344.5, -137.03) * mm});
            skLineSegment(sketch, "E19.8.17.5", {"start": v(337.5, -178.2) * mm, "end": v(342.5, -178.2) * mm});
            skLineSegment(sketch, "E19.11.17.5", {"start": v(335.5, -137.03) * mm, "end": v(335.5, -176.2) * mm});
            skArc(sketch, "E19.14.17.5", {"start": v(342.5, -178.2) * mm, "mid": v(343.91, -177.62) * mm, "end": v(344.5, -176.2) * mm});
            skArc(sketch, "E19.18.17.5", {"start": v(335.5, -176.2) * mm, "mid": v(336.09, -177.62) * mm, "end": v(337.5, -178.2) * mm});
            skPoint(sketch, "E19.0.17.6", {"position": v(335.5, -212.85) * mm});
            skLineSegment(sketch, "E19.1.17.6", {"start": v(344.5, -171.67) * mm, "end": v(344.5, -210.85) * mm});
            skPoint(sketch, "E19.4.17.6", {"position": v(344.5, -212.85) * mm});
            skLineSegment(sketch, "E19.5.17.6", {"start": v(335.5, -171.67) * mm, "end": v(344.5, -171.67) * mm});
            skLineSegment(sketch, "E19.8.17.6", {"start": v(337.5, -212.85) * mm, "end": v(342.5, -212.85) * mm});
            skLineSegment(sketch, "E19.11.17.6", {"start": v(335.5, -171.67) * mm, "end": v(335.5, -210.85) * mm});
            skArc(sketch, "E19.14.17.6", {"start": v(342.5, -212.85) * mm, "mid": v(343.91, -212.26) * mm, "end": v(344.5, -210.85) * mm});
            skArc(sketch, "E19.18.17.6", {"start": v(335.5, -210.85) * mm, "mid": v(336.09, -212.26) * mm, "end": v(337.5, -212.85) * mm});
            skPoint(sketch, "E19.0.17.7", {"position": v(335.5, -247.49) * mm});
            skLineSegment(sketch, "E19.1.17.7", {"start": v(344.5, -206.31) * mm, "end": v(344.5, -245.49) * mm});
            skPoint(sketch, "E19.4.17.7", {"position": v(344.5, -247.49) * mm});
            skLineSegment(sketch, "E19.5.17.7", {"start": v(335.5, -206.31) * mm, "end": v(344.5, -206.31) * mm});
            skLineSegment(sketch, "E19.8.17.7", {"start": v(337.5, -247.49) * mm, "end": v(342.5, -247.49) * mm});
            skLineSegment(sketch, "E19.11.17.7", {"start": v(335.5, -206.31) * mm, "end": v(335.5, -245.49) * mm});
            skArc(sketch, "E19.14.17.7", {"start": v(342.5, -247.49) * mm, "mid": v(343.91, -246.9) * mm, "end": v(344.5, -245.49) * mm});
            skArc(sketch, "E19.18.17.7", {"start": v(335.5, -245.49) * mm, "mid": v(336.09, -246.9) * mm, "end": v(337.5, -247.49) * mm});
            skPoint(sketch, "E19.0.17.8", {"position": v(335.5, -282.13) * mm});
            skLineSegment(sketch, "E19.1.17.8", {"start": v(344.5, -240.95) * mm, "end": v(344.5, -280.13) * mm});
            skPoint(sketch, "E19.4.17.8", {"position": v(344.5, -282.13) * mm});
            skLineSegment(sketch, "E19.5.17.8", {"start": v(335.5, -240.95) * mm, "end": v(344.5, -240.95) * mm});
            skLineSegment(sketch, "E19.8.17.8", {"start": v(337.5, -282.13) * mm, "end": v(342.5, -282.13) * mm});
            skLineSegment(sketch, "E19.11.17.8", {"start": v(335.5, -240.95) * mm, "end": v(335.5, -280.13) * mm});
            skArc(sketch, "E19.14.17.8", {"start": v(342.5, -282.13) * mm, "mid": v(343.91, -281.54) * mm, "end": v(344.5, -280.13) * mm});
            skArc(sketch, "E19.18.17.8", {"start": v(335.5, -280.13) * mm, "mid": v(336.09, -281.54) * mm, "end": v(337.5, -282.13) * mm});
            skPoint(sketch, "E19.0.17.9", {"position": v(335.5, -316.77) * mm});
            skLineSegment(sketch, "E19.1.17.9", {"start": v(344.5, -275.6) * mm, "end": v(344.5, -314.77) * mm});
            skPoint(sketch, "E19.4.17.9", {"position": v(344.5, -316.77) * mm});
            skLineSegment(sketch, "E19.5.17.9", {"start": v(335.5, -275.6) * mm, "end": v(344.5, -275.6) * mm});
            skLineSegment(sketch, "E19.8.17.9", {"start": v(337.5, -316.77) * mm, "end": v(342.5, -316.77) * mm});
            skLineSegment(sketch, "E19.11.17.9", {"start": v(335.5, -275.6) * mm, "end": v(335.5, -314.77) * mm});
            skArc(sketch, "E19.14.17.9", {"start": v(342.5, -316.77) * mm, "mid": v(343.91, -316.18) * mm, "end": v(344.5, -314.77) * mm});
            skArc(sketch, "E19.18.17.9", {"start": v(335.5, -314.77) * mm, "mid": v(336.09, -316.18) * mm, "end": v(337.5, -316.77) * mm});
            skPoint(sketch, "E19.0.17.10", {"position": v(335.5, -351.41) * mm});
            skLineSegment(sketch, "E19.1.17.10", {"start": v(344.5, -310.24) * mm, "end": v(344.5, -349.41) * mm});
            skPoint(sketch, "E19.4.17.10", {"position": v(344.5, -351.41) * mm});
            skLineSegment(sketch, "E19.5.17.10", {"start": v(335.5, -310.24) * mm, "end": v(344.5, -310.24) * mm});
            skLineSegment(sketch, "E19.8.17.10", {"start": v(337.5, -351.41) * mm, "end": v(342.5, -351.41) * mm});
            skLineSegment(sketch, "E19.11.17.10", {"start": v(335.5, -310.24) * mm, "end": v(335.5, -349.41) * mm});
            skArc(sketch, "E19.14.17.10", {"start": v(342.5, -351.41) * mm, "mid": v(343.91, -350.82) * mm, "end": v(344.5, -349.41) * mm});
            skArc(sketch, "E19.18.17.10", {"start": v(335.5, -349.41) * mm, "mid": v(336.09, -350.82) * mm, "end": v(337.5, -351.41) * mm});
            skPoint(sketch, "E19.0.17.11", {"position": v(335.5, -386.05) * mm});
            skLineSegment(sketch, "E19.1.17.11", {"start": v(344.5, -344.88) * mm, "end": v(344.5, -384.05) * mm});
            skPoint(sketch, "E19.4.17.11", {"position": v(344.5, -386.05) * mm});
            skLineSegment(sketch, "E19.5.17.11", {"start": v(335.5, -344.88) * mm, "end": v(344.5, -344.88) * mm});
            skLineSegment(sketch, "E19.8.17.11", {"start": v(337.5, -386.05) * mm, "end": v(342.5, -386.05) * mm});
            skLineSegment(sketch, "E19.11.17.11", {"start": v(335.5, -344.88) * mm, "end": v(335.5, -384.05) * mm});
            skArc(sketch, "E19.14.17.11", {"start": v(342.5, -386.05) * mm, "mid": v(343.91, -385.47) * mm, "end": v(344.5, -384.05) * mm});
            skArc(sketch, "E19.18.17.11", {"start": v(335.5, -384.05) * mm, "mid": v(336.09, -385.47) * mm, "end": v(337.5, -386.05) * mm});
            skPoint(sketch, "E19.0.17.12", {"position": v(335.5, -420.7) * mm});
            skLineSegment(sketch, "E19.1.17.12", {"start": v(344.5, -379.52) * mm, "end": v(344.5, -418.7) * mm});
            skPoint(sketch, "E19.4.17.12", {"position": v(344.5, -420.7) * mm});
            skLineSegment(sketch, "E19.5.17.12", {"start": v(335.5, -379.52) * mm, "end": v(344.5, -379.52) * mm});
            skLineSegment(sketch, "E19.8.17.12", {"start": v(337.5, -420.7) * mm, "end": v(342.5, -420.7) * mm});
            skLineSegment(sketch, "E19.11.17.12", {"start": v(335.5, -379.52) * mm, "end": v(335.5, -418.7) * mm});
            skArc(sketch, "E19.14.17.12", {"start": v(342.5, -420.7) * mm, "mid": v(343.91, -420.1) * mm, "end": v(344.5, -418.7) * mm});
            skArc(sketch, "E19.18.17.12", {"start": v(335.5, -418.7) * mm, "mid": v(336.09, -420.1) * mm, "end": v(337.5, -420.7) * mm});
            skPoint(sketch, "E19.0.17.13", {"position": v(335.5, -455.33) * mm});
            skLineSegment(sketch, "E19.1.17.13", {"start": v(344.5, -414.16) * mm, "end": v(344.5, -453.33) * mm});
            skPoint(sketch, "E19.4.17.13", {"position": v(344.5, -455.33) * mm});
            skLineSegment(sketch, "E19.5.17.13", {"start": v(335.5, -414.16) * mm, "end": v(344.5, -414.16) * mm});
            skLineSegment(sketch, "E19.8.17.13", {"start": v(337.5, -455.33) * mm, "end": v(342.5, -455.33) * mm});
            skLineSegment(sketch, "E19.11.17.13", {"start": v(335.5, -414.16) * mm, "end": v(335.5, -453.33) * mm});
            skArc(sketch, "E19.14.17.13", {"start": v(342.5, -455.33) * mm, "mid": v(343.91, -454.75) * mm, "end": v(344.5, -453.33) * mm});
            skArc(sketch, "E19.18.17.13", {"start": v(335.5, -453.33) * mm, "mid": v(336.09, -454.75) * mm, "end": v(337.5, -455.33) * mm});
            skPoint(sketch, "E19.0.17.14", {"position": v(335.5, -489.97) * mm});
            skLineSegment(sketch, "E19.1.17.14", {"start": v(344.5, -448.8) * mm, "end": v(344.5, -487.97) * mm});
            skPoint(sketch, "E19.4.17.14", {"position": v(344.5, -489.97) * mm});
            skLineSegment(sketch, "E19.5.17.14", {"start": v(335.5, -448.8) * mm, "end": v(344.5, -448.8) * mm});
            skLineSegment(sketch, "E19.8.17.14", {"start": v(337.5, -489.97) * mm, "end": v(342.5, -489.97) * mm});
            skLineSegment(sketch, "E19.11.17.14", {"start": v(335.5, -448.8) * mm, "end": v(335.5, -487.97) * mm});
            skArc(sketch, "E19.14.17.14", {"start": v(342.5, -489.97) * mm, "mid": v(343.91, -489.39) * mm, "end": v(344.5, -487.97) * mm});
            skArc(sketch, "E19.18.17.14", {"start": v(335.5, -487.97) * mm, "mid": v(336.09, -489.39) * mm, "end": v(337.5, -489.97) * mm});
            skPoint(sketch, "E19.0.18.0", {"position": v(355.5, -5) * mm});
            skLineSegment(sketch, "E19.1.18.0", {"start": v(364.5, 36.17) * mm, "end": v(364.5, -3) * mm});
            skPoint(sketch, "E19.4.18.0", {"position": v(364.5, -5) * mm});
            skLineSegment(sketch, "E19.5.18.0", {"start": v(355.5, 36.17) * mm, "end": v(364.5, 36.17) * mm});
            skLineSegment(sketch, "E19.8.18.0", {"start": v(357.5, -5) * mm, "end": v(362.5, -5) * mm});
            skLineSegment(sketch, "E19.11.18.0", {"start": v(355.5, 36.17) * mm, "end": v(355.5, -3) * mm});
            skArc(sketch, "E19.14.18.0", {"start": v(362.5, -5) * mm, "mid": v(363.91, -4.41) * mm, "end": v(364.5, -3) * mm});
            skArc(sketch, "E19.18.18.0", {"start": v(355.5, -3) * mm, "mid": v(356.09, -4.41) * mm, "end": v(357.5, -5) * mm});
            skPoint(sketch, "E19.0.18.1", {"position": v(355.5, -39.64) * mm});
            skLineSegment(sketch, "E19.1.18.1", {"start": v(364.5, 1.53) * mm, "end": v(364.5, -37.64) * mm});
            skPoint(sketch, "E19.4.18.1", {"position": v(364.5, -39.64) * mm});
            skLineSegment(sketch, "E19.5.18.1", {"start": v(355.5, 1.53) * mm, "end": v(364.5, 1.53) * mm});
            skLineSegment(sketch, "E19.8.18.1", {"start": v(357.5, -39.64) * mm, "end": v(362.5, -39.64) * mm});
            skLineSegment(sketch, "E19.11.18.1", {"start": v(355.5, 1.53) * mm, "end": v(355.5, -37.64) * mm});
            skArc(sketch, "E19.14.18.1", {"start": v(362.5, -39.64) * mm, "mid": v(363.91, -39.06) * mm, "end": v(364.5, -37.64) * mm});
            skArc(sketch, "E19.18.18.1", {"start": v(355.5, -37.64) * mm, "mid": v(356.09, -39.06) * mm, "end": v(357.5, -39.64) * mm});
            skPoint(sketch, "E19.0.18.2", {"position": v(355.5, -74.28) * mm});
            skLineSegment(sketch, "E19.1.18.2", {"start": v(364.5, -33.1) * mm, "end": v(364.5, -72.28) * mm});
            skPoint(sketch, "E19.4.18.2", {"position": v(364.5, -74.28) * mm});
            skLineSegment(sketch, "E19.5.18.2", {"start": v(355.5, -33.1) * mm, "end": v(364.5, -33.1) * mm});
            skLineSegment(sketch, "E19.8.18.2", {"start": v(357.5, -74.28) * mm, "end": v(362.5, -74.28) * mm});
            skLineSegment(sketch, "E19.11.18.2", {"start": v(355.5, -33.1) * mm, "end": v(355.5, -72.28) * mm});
            skArc(sketch, "E19.14.18.2", {"start": v(362.5, -74.28) * mm, "mid": v(363.91, -73.7) * mm, "end": v(364.5, -72.28) * mm});
            skArc(sketch, "E19.18.18.2", {"start": v(355.5, -72.28) * mm, "mid": v(356.09, -73.7) * mm, "end": v(357.5, -74.28) * mm});
            skPoint(sketch, "E19.0.18.3", {"position": v(355.5, -108.92) * mm});
            skLineSegment(sketch, "E19.1.18.3", {"start": v(364.5, -67.75) * mm, "end": v(364.5, -106.92) * mm});
            skPoint(sketch, "E19.4.18.3", {"position": v(364.5, -108.92) * mm});
            skLineSegment(sketch, "E19.5.18.3", {"start": v(355.5, -67.75) * mm, "end": v(364.5, -67.75) * mm});
            skLineSegment(sketch, "E19.8.18.3", {"start": v(357.5, -108.92) * mm, "end": v(362.5, -108.92) * mm});
            skLineSegment(sketch, "E19.11.18.3", {"start": v(355.5, -67.75) * mm, "end": v(355.5, -106.92) * mm});
            skArc(sketch, "E19.14.18.3", {"start": v(362.5, -108.92) * mm, "mid": v(363.91, -108.34) * mm, "end": v(364.5, -106.92) * mm});
            skArc(sketch, "E19.18.18.3", {"start": v(355.5, -106.92) * mm, "mid": v(356.09, -108.34) * mm, "end": v(357.5, -108.92) * mm});
            skPoint(sketch, "E19.0.18.4", {"position": v(355.5, -143.56) * mm});
            skLineSegment(sketch, "E19.1.18.4", {"start": v(364.5, -102.4) * mm, "end": v(364.5, -141.56) * mm});
            skPoint(sketch, "E19.4.18.4", {"position": v(364.5, -143.56) * mm});
            skLineSegment(sketch, "E19.5.18.4", {"start": v(355.5, -102.4) * mm, "end": v(364.5, -102.4) * mm});
            skLineSegment(sketch, "E19.8.18.4", {"start": v(357.5, -143.56) * mm, "end": v(362.5, -143.56) * mm});
            skLineSegment(sketch, "E19.11.18.4", {"start": v(355.5, -102.4) * mm, "end": v(355.5, -141.56) * mm});
            skArc(sketch, "E19.14.18.4", {"start": v(362.5, -143.56) * mm, "mid": v(363.91, -142.98) * mm, "end": v(364.5, -141.56) * mm});
            skArc(sketch, "E19.18.18.4", {"start": v(355.5, -141.56) * mm, "mid": v(356.09, -142.98) * mm, "end": v(357.5, -143.56) * mm});
            skPoint(sketch, "E19.0.18.5", {"position": v(355.5, -178.2) * mm});
            skLineSegment(sketch, "E19.1.18.5", {"start": v(364.5, -137.03) * mm, "end": v(364.5, -176.2) * mm});
            skPoint(sketch, "E19.4.18.5", {"position": v(364.5, -178.2) * mm});
            skLineSegment(sketch, "E19.5.18.5", {"start": v(355.5, -137.03) * mm, "end": v(364.5, -137.03) * mm});
            skLineSegment(sketch, "E19.8.18.5", {"start": v(357.5, -178.2) * mm, "end": v(362.5, -178.2) * mm});
            skLineSegment(sketch, "E19.11.18.5", {"start": v(355.5, -137.03) * mm, "end": v(355.5, -176.2) * mm});
            skArc(sketch, "E19.14.18.5", {"start": v(362.5, -178.2) * mm, "mid": v(363.91, -177.62) * mm, "end": v(364.5, -176.2) * mm});
            skArc(sketch, "E19.18.18.5", {"start": v(355.5, -176.2) * mm, "mid": v(356.09, -177.62) * mm, "end": v(357.5, -178.2) * mm});
            skPoint(sketch, "E19.0.18.6", {"position": v(355.5, -212.85) * mm});
            skLineSegment(sketch, "E19.1.18.6", {"start": v(364.5, -171.67) * mm, "end": v(364.5, -210.85) * mm});
            skPoint(sketch, "E19.4.18.6", {"position": v(364.5, -212.85) * mm});
            skLineSegment(sketch, "E19.5.18.6", {"start": v(355.5, -171.67) * mm, "end": v(364.5, -171.67) * mm});
            skLineSegment(sketch, "E19.8.18.6", {"start": v(357.5, -212.85) * mm, "end": v(362.5, -212.85) * mm});
            skLineSegment(sketch, "E19.11.18.6", {"start": v(355.5, -171.67) * mm, "end": v(355.5, -210.85) * mm});
            skArc(sketch, "E19.14.18.6", {"start": v(362.5, -212.85) * mm, "mid": v(363.91, -212.26) * mm, "end": v(364.5, -210.85) * mm});
            skArc(sketch, "E19.18.18.6", {"start": v(355.5, -210.85) * mm, "mid": v(356.09, -212.26) * mm, "end": v(357.5, -212.85) * mm});
            skPoint(sketch, "E19.0.18.7", {"position": v(355.5, -247.49) * mm});
            skLineSegment(sketch, "E19.1.18.7", {"start": v(364.5, -206.31) * mm, "end": v(364.5, -245.49) * mm});
            skPoint(sketch, "E19.4.18.7", {"position": v(364.5, -247.49) * mm});
            skLineSegment(sketch, "E19.5.18.7", {"start": v(355.5, -206.31) * mm, "end": v(364.5, -206.31) * mm});
            skLineSegment(sketch, "E19.8.18.7", {"start": v(357.5, -247.49) * mm, "end": v(362.5, -247.49) * mm});
            skLineSegment(sketch, "E19.11.18.7", {"start": v(355.5, -206.31) * mm, "end": v(355.5, -245.49) * mm});
            skArc(sketch, "E19.14.18.7", {"start": v(362.5, -247.49) * mm, "mid": v(363.91, -246.9) * mm, "end": v(364.5, -245.49) * mm});
            skArc(sketch, "E19.18.18.7", {"start": v(355.5, -245.49) * mm, "mid": v(356.09, -246.9) * mm, "end": v(357.5, -247.49) * mm});
            skPoint(sketch, "E19.0.18.8", {"position": v(355.5, -282.13) * mm});
            skLineSegment(sketch, "E19.1.18.8", {"start": v(364.5, -240.95) * mm, "end": v(364.5, -280.13) * mm});
            skPoint(sketch, "E19.4.18.8", {"position": v(364.5, -282.13) * mm});
            skLineSegment(sketch, "E19.5.18.8", {"start": v(355.5, -240.95) * mm, "end": v(364.5, -240.95) * mm});
            skLineSegment(sketch, "E19.8.18.8", {"start": v(357.5, -282.13) * mm, "end": v(362.5, -282.13) * mm});
            skLineSegment(sketch, "E19.11.18.8", {"start": v(355.5, -240.95) * mm, "end": v(355.5, -280.13) * mm});
            skArc(sketch, "E19.14.18.8", {"start": v(362.5, -282.13) * mm, "mid": v(363.91, -281.54) * mm, "end": v(364.5, -280.13) * mm});
            skArc(sketch, "E19.18.18.8", {"start": v(355.5, -280.13) * mm, "mid": v(356.09, -281.54) * mm, "end": v(357.5, -282.13) * mm});
            skPoint(sketch, "E19.0.18.9", {"position": v(355.5, -316.77) * mm});
            skLineSegment(sketch, "E19.1.18.9", {"start": v(364.5, -275.6) * mm, "end": v(364.5, -314.77) * mm});
            skPoint(sketch, "E19.4.18.9", {"position": v(364.5, -316.77) * mm});
            skLineSegment(sketch, "E19.5.18.9", {"start": v(355.5, -275.6) * mm, "end": v(364.5, -275.6) * mm});
            skLineSegment(sketch, "E19.8.18.9", {"start": v(357.5, -316.77) * mm, "end": v(362.5, -316.77) * mm});
            skLineSegment(sketch, "E19.11.18.9", {"start": v(355.5, -275.6) * mm, "end": v(355.5, -314.77) * mm});
            skArc(sketch, "E19.14.18.9", {"start": v(362.5, -316.77) * mm, "mid": v(363.91, -316.18) * mm, "end": v(364.5, -314.77) * mm});
            skArc(sketch, "E19.18.18.9", {"start": v(355.5, -314.77) * mm, "mid": v(356.09, -316.18) * mm, "end": v(357.5, -316.77) * mm});
            skPoint(sketch, "E19.0.18.10", {"position": v(355.5, -351.41) * mm});
            skLineSegment(sketch, "E19.1.18.10", {"start": v(364.5, -310.24) * mm, "end": v(364.5, -349.41) * mm});
            skPoint(sketch, "E19.4.18.10", {"position": v(364.5, -351.41) * mm});
            skLineSegment(sketch, "E19.5.18.10", {"start": v(355.5, -310.24) * mm, "end": v(364.5, -310.24) * mm});
            skLineSegment(sketch, "E19.8.18.10", {"start": v(357.5, -351.41) * mm, "end": v(362.5, -351.41) * mm});
            skLineSegment(sketch, "E19.11.18.10", {"start": v(355.5, -310.24) * mm, "end": v(355.5, -349.41) * mm});
            skArc(sketch, "E19.14.18.10", {"start": v(362.5, -351.41) * mm, "mid": v(363.91, -350.82) * mm, "end": v(364.5, -349.41) * mm});
            skArc(sketch, "E19.18.18.10", {"start": v(355.5, -349.41) * mm, "mid": v(356.09, -350.82) * mm, "end": v(357.5, -351.41) * mm});
            skPoint(sketch, "E19.0.18.11", {"position": v(355.5, -386.05) * mm});
            skLineSegment(sketch, "E19.1.18.11", {"start": v(364.5, -344.88) * mm, "end": v(364.5, -384.05) * mm});
            skPoint(sketch, "E19.4.18.11", {"position": v(364.5, -386.05) * mm});
            skLineSegment(sketch, "E19.5.18.11", {"start": v(355.5, -344.88) * mm, "end": v(364.5, -344.88) * mm});
            skLineSegment(sketch, "E19.8.18.11", {"start": v(357.5, -386.05) * mm, "end": v(362.5, -386.05) * mm});
            skLineSegment(sketch, "E19.11.18.11", {"start": v(355.5, -344.88) * mm, "end": v(355.5, -384.05) * mm});
            skArc(sketch, "E19.14.18.11", {"start": v(362.5, -386.05) * mm, "mid": v(363.91, -385.47) * mm, "end": v(364.5, -384.05) * mm});
            skArc(sketch, "E19.18.18.11", {"start": v(355.5, -384.05) * mm, "mid": v(356.09, -385.47) * mm, "end": v(357.5, -386.05) * mm});
            skPoint(sketch, "E19.0.18.12", {"position": v(355.5, -420.7) * mm});
            skLineSegment(sketch, "E19.1.18.12", {"start": v(364.5, -379.52) * mm, "end": v(364.5, -418.7) * mm});
            skPoint(sketch, "E19.4.18.12", {"position": v(364.5, -420.7) * mm});
            skLineSegment(sketch, "E19.5.18.12", {"start": v(355.5, -379.52) * mm, "end": v(364.5, -379.52) * mm});
            skLineSegment(sketch, "E19.8.18.12", {"start": v(357.5, -420.7) * mm, "end": v(362.5, -420.7) * mm});
            skLineSegment(sketch, "E19.11.18.12", {"start": v(355.5, -379.52) * mm, "end": v(355.5, -418.7) * mm});
            skArc(sketch, "E19.14.18.12", {"start": v(362.5, -420.7) * mm, "mid": v(363.91, -420.1) * mm, "end": v(364.5, -418.7) * mm});
            skArc(sketch, "E19.18.18.12", {"start": v(355.5, -418.7) * mm, "mid": v(356.09, -420.1) * mm, "end": v(357.5, -420.7) * mm});
            skPoint(sketch, "E19.0.18.13", {"position": v(355.5, -455.33) * mm});
            skLineSegment(sketch, "E19.1.18.13", {"start": v(364.5, -414.16) * mm, "end": v(364.5, -453.33) * mm});
            skPoint(sketch, "E19.4.18.13", {"position": v(364.5, -455.33) * mm});
            skLineSegment(sketch, "E19.5.18.13", {"start": v(355.5, -414.16) * mm, "end": v(364.5, -414.16) * mm});
            skLineSegment(sketch, "E19.8.18.13", {"start": v(357.5, -455.33) * mm, "end": v(362.5, -455.33) * mm});
            skLineSegment(sketch, "E19.11.18.13", {"start": v(355.5, -414.16) * mm, "end": v(355.5, -453.33) * mm});
            skArc(sketch, "E19.14.18.13", {"start": v(362.5, -455.33) * mm, "mid": v(363.91, -454.75) * mm, "end": v(364.5, -453.33) * mm});
            skArc(sketch, "E19.18.18.13", {"start": v(355.5, -453.33) * mm, "mid": v(356.09, -454.75) * mm, "end": v(357.5, -455.33) * mm});
            skPoint(sketch, "E19.0.18.14", {"position": v(355.5, -489.97) * mm});
            skLineSegment(sketch, "E19.1.18.14", {"start": v(364.5, -448.8) * mm, "end": v(364.5, -487.97) * mm});
            skPoint(sketch, "E19.4.18.14", {"position": v(364.5, -489.97) * mm});
            skLineSegment(sketch, "E19.5.18.14", {"start": v(355.5, -448.8) * mm, "end": v(364.5, -448.8) * mm});
            skLineSegment(sketch, "E19.8.18.14", {"start": v(357.5, -489.97) * mm, "end": v(362.5, -489.97) * mm});
            skLineSegment(sketch, "E19.11.18.14", {"start": v(355.5, -448.8) * mm, "end": v(355.5, -487.97) * mm});
            skArc(sketch, "E19.14.18.14", {"start": v(362.5, -489.97) * mm, "mid": v(363.91, -489.39) * mm, "end": v(364.5, -487.97) * mm});
            skArc(sketch, "E19.18.18.14", {"start": v(355.5, -487.97) * mm, "mid": v(356.09, -489.39) * mm, "end": v(357.5, -489.97) * mm});
            skPoint(sketch, "E19.0.19.0", {"position": v(375.5, -5) * mm});
            skLineSegment(sketch, "E19.1.19.0", {"start": v(384.5, 36.17) * mm, "end": v(384.5, -3) * mm});
            skPoint(sketch, "E19.4.19.0", {"position": v(384.5, -5) * mm});
            skLineSegment(sketch, "E19.5.19.0", {"start": v(375.5, 36.17) * mm, "end": v(384.5, 36.17) * mm});
            skLineSegment(sketch, "E19.8.19.0", {"start": v(377.5, -5) * mm, "end": v(382.5, -5) * mm});
            skLineSegment(sketch, "E19.11.19.0", {"start": v(375.5, 36.17) * mm, "end": v(375.5, -3) * mm});
            skArc(sketch, "E19.14.19.0", {"start": v(382.5, -5) * mm, "mid": v(383.91, -4.41) * mm, "end": v(384.5, -3) * mm});
            skArc(sketch, "E19.18.19.0", {"start": v(375.5, -3) * mm, "mid": v(376.09, -4.41) * mm, "end": v(377.5, -5) * mm});
            skPoint(sketch, "E19.0.19.1", {"position": v(375.5, -39.64) * mm});
            skLineSegment(sketch, "E19.1.19.1", {"start": v(384.5, 1.53) * mm, "end": v(384.5, -37.64) * mm});
            skPoint(sketch, "E19.4.19.1", {"position": v(384.5, -39.64) * mm});
            skLineSegment(sketch, "E19.5.19.1", {"start": v(375.5, 1.53) * mm, "end": v(384.5, 1.53) * mm});
            skLineSegment(sketch, "E19.8.19.1", {"start": v(377.5, -39.64) * mm, "end": v(382.5, -39.64) * mm});
            skLineSegment(sketch, "E19.11.19.1", {"start": v(375.5, 1.53) * mm, "end": v(375.5, -37.64) * mm});
            skArc(sketch, "E19.14.19.1", {"start": v(382.5, -39.64) * mm, "mid": v(383.91, -39.06) * mm, "end": v(384.5, -37.64) * mm});
            skArc(sketch, "E19.18.19.1", {"start": v(375.5, -37.64) * mm, "mid": v(376.09, -39.06) * mm, "end": v(377.5, -39.64) * mm});
            skPoint(sketch, "E19.0.19.2", {"position": v(375.5, -74.28) * mm});
            skLineSegment(sketch, "E19.1.19.2", {"start": v(384.5, -33.1) * mm, "end": v(384.5, -72.28) * mm});
            skPoint(sketch, "E19.4.19.2", {"position": v(384.5, -74.28) * mm});
            skLineSegment(sketch, "E19.5.19.2", {"start": v(375.5, -33.1) * mm, "end": v(384.5, -33.1) * mm});
            skLineSegment(sketch, "E19.8.19.2", {"start": v(377.5, -74.28) * mm, "end": v(382.5, -74.28) * mm});
            skLineSegment(sketch, "E19.11.19.2", {"start": v(375.5, -33.1) * mm, "end": v(375.5, -72.28) * mm});
            skArc(sketch, "E19.14.19.2", {"start": v(382.5, -74.28) * mm, "mid": v(383.91, -73.7) * mm, "end": v(384.5, -72.28) * mm});
            skArc(sketch, "E19.18.19.2", {"start": v(375.5, -72.28) * mm, "mid": v(376.09, -73.7) * mm, "end": v(377.5, -74.28) * mm});
            skPoint(sketch, "E19.0.19.3", {"position": v(375.5, -108.92) * mm});
            skLineSegment(sketch, "E19.1.19.3", {"start": v(384.5, -67.75) * mm, "end": v(384.5, -106.92) * mm});
            skPoint(sketch, "E19.4.19.3", {"position": v(384.5, -108.92) * mm});
            skLineSegment(sketch, "E19.5.19.3", {"start": v(375.5, -67.75) * mm, "end": v(384.5, -67.75) * mm});
            skLineSegment(sketch, "E19.8.19.3", {"start": v(377.5, -108.92) * mm, "end": v(382.5, -108.92) * mm});
            skLineSegment(sketch, "E19.11.19.3", {"start": v(375.5, -67.75) * mm, "end": v(375.5, -106.92) * mm});
            skArc(sketch, "E19.14.19.3", {"start": v(382.5, -108.92) * mm, "mid": v(383.91, -108.34) * mm, "end": v(384.5, -106.92) * mm});
            skArc(sketch, "E19.18.19.3", {"start": v(375.5, -106.92) * mm, "mid": v(376.09, -108.34) * mm, "end": v(377.5, -108.92) * mm});
            skPoint(sketch, "E19.0.19.4", {"position": v(375.5, -143.56) * mm});
            skLineSegment(sketch, "E19.1.19.4", {"start": v(384.5, -102.4) * mm, "end": v(384.5, -141.56) * mm});
            skPoint(sketch, "E19.4.19.4", {"position": v(384.5, -143.56) * mm});
            skLineSegment(sketch, "E19.5.19.4", {"start": v(375.5, -102.4) * mm, "end": v(384.5, -102.4) * mm});
            skLineSegment(sketch, "E19.8.19.4", {"start": v(377.5, -143.56) * mm, "end": v(382.5, -143.56) * mm});
            skLineSegment(sketch, "E19.11.19.4", {"start": v(375.5, -102.4) * mm, "end": v(375.5, -141.56) * mm});
            skArc(sketch, "E19.14.19.4", {"start": v(382.5, -143.56) * mm, "mid": v(383.91, -142.98) * mm, "end": v(384.5, -141.56) * mm});
            skArc(sketch, "E19.18.19.4", {"start": v(375.5, -141.56) * mm, "mid": v(376.09, -142.98) * mm, "end": v(377.5, -143.56) * mm});
            skPoint(sketch, "E19.0.19.5", {"position": v(375.5, -178.2) * mm});
            skLineSegment(sketch, "E19.1.19.5", {"start": v(384.5, -137.03) * mm, "end": v(384.5, -176.2) * mm});
            skPoint(sketch, "E19.4.19.5", {"position": v(384.5, -178.2) * mm});
            skLineSegment(sketch, "E19.5.19.5", {"start": v(375.5, -137.03) * mm, "end": v(384.5, -137.03) * mm});
            skLineSegment(sketch, "E19.8.19.5", {"start": v(377.5, -178.2) * mm, "end": v(382.5, -178.2) * mm});
            skLineSegment(sketch, "E19.11.19.5", {"start": v(375.5, -137.03) * mm, "end": v(375.5, -176.2) * mm});
            skArc(sketch, "E19.14.19.5", {"start": v(382.5, -178.2) * mm, "mid": v(383.91, -177.62) * mm, "end": v(384.5, -176.2) * mm});
            skArc(sketch, "E19.18.19.5", {"start": v(375.5, -176.2) * mm, "mid": v(376.09, -177.62) * mm, "end": v(377.5, -178.2) * mm});
            skPoint(sketch, "E19.0.19.6", {"position": v(375.5, -212.85) * mm});
            skLineSegment(sketch, "E19.1.19.6", {"start": v(384.5, -171.67) * mm, "end": v(384.5, -210.85) * mm});
            skPoint(sketch, "E19.4.19.6", {"position": v(384.5, -212.85) * mm});
            skLineSegment(sketch, "E19.5.19.6", {"start": v(375.5, -171.67) * mm, "end": v(384.5, -171.67) * mm});
            skLineSegment(sketch, "E19.8.19.6", {"start": v(377.5, -212.85) * mm, "end": v(382.5, -212.85) * mm});
            skLineSegment(sketch, "E19.11.19.6", {"start": v(375.5, -171.67) * mm, "end": v(375.5, -210.85) * mm});
            skArc(sketch, "E19.14.19.6", {"start": v(382.5, -212.85) * mm, "mid": v(383.91, -212.26) * mm, "end": v(384.5, -210.85) * mm});
            skArc(sketch, "E19.18.19.6", {"start": v(375.5, -210.85) * mm, "mid": v(376.09, -212.26) * mm, "end": v(377.5, -212.85) * mm});
            skPoint(sketch, "E19.0.19.7", {"position": v(375.5, -247.49) * mm});
            skLineSegment(sketch, "E19.1.19.7", {"start": v(384.5, -206.31) * mm, "end": v(384.5, -245.49) * mm});
            skPoint(sketch, "E19.4.19.7", {"position": v(384.5, -247.49) * mm});
            skLineSegment(sketch, "E19.5.19.7", {"start": v(375.5, -206.31) * mm, "end": v(384.5, -206.31) * mm});
            skLineSegment(sketch, "E19.8.19.7", {"start": v(377.5, -247.49) * mm, "end": v(382.5, -247.49) * mm});
            skLineSegment(sketch, "E19.11.19.7", {"start": v(375.5, -206.31) * mm, "end": v(375.5, -245.49) * mm});
            skArc(sketch, "E19.14.19.7", {"start": v(382.5, -247.49) * mm, "mid": v(383.91, -246.9) * mm, "end": v(384.5, -245.49) * mm});
            skArc(sketch, "E19.18.19.7", {"start": v(375.5, -245.49) * mm, "mid": v(376.09, -246.9) * mm, "end": v(377.5, -247.49) * mm});
            skPoint(sketch, "E19.0.19.8", {"position": v(375.5, -282.13) * mm});
            skLineSegment(sketch, "E19.1.19.8", {"start": v(384.5, -240.95) * mm, "end": v(384.5, -280.13) * mm});
            skPoint(sketch, "E19.4.19.8", {"position": v(384.5, -282.13) * mm});
            skLineSegment(sketch, "E19.5.19.8", {"start": v(375.5, -240.95) * mm, "end": v(384.5, -240.95) * mm});
            skLineSegment(sketch, "E19.8.19.8", {"start": v(377.5, -282.13) * mm, "end": v(382.5, -282.13) * mm});
            skLineSegment(sketch, "E19.11.19.8", {"start": v(375.5, -240.95) * mm, "end": v(375.5, -280.13) * mm});
            skArc(sketch, "E19.14.19.8", {"start": v(382.5, -282.13) * mm, "mid": v(383.91, -281.54) * mm, "end": v(384.5, -280.13) * mm});
            skArc(sketch, "E19.18.19.8", {"start": v(375.5, -280.13) * mm, "mid": v(376.09, -281.54) * mm, "end": v(377.5, -282.13) * mm});
            skPoint(sketch, "E19.0.19.9", {"position": v(375.5, -316.77) * mm});
            skLineSegment(sketch, "E19.1.19.9", {"start": v(384.5, -275.6) * mm, "end": v(384.5, -314.77) * mm});
            skPoint(sketch, "E19.4.19.9", {"position": v(384.5, -316.77) * mm});
            skLineSegment(sketch, "E19.5.19.9", {"start": v(375.5, -275.6) * mm, "end": v(384.5, -275.6) * mm});
            skLineSegment(sketch, "E19.8.19.9", {"start": v(377.5, -316.77) * mm, "end": v(382.5, -316.77) * mm});
            skLineSegment(sketch, "E19.11.19.9", {"start": v(375.5, -275.6) * mm, "end": v(375.5, -314.77) * mm});
            skArc(sketch, "E19.14.19.9", {"start": v(382.5, -316.77) * mm, "mid": v(383.91, -316.18) * mm, "end": v(384.5, -314.77) * mm});
            skArc(sketch, "E19.18.19.9", {"start": v(375.5, -314.77) * mm, "mid": v(376.09, -316.18) * mm, "end": v(377.5, -316.77) * mm});
            skPoint(sketch, "E19.0.19.10", {"position": v(375.5, -351.41) * mm});
            skLineSegment(sketch, "E19.1.19.10", {"start": v(384.5, -310.24) * mm, "end": v(384.5, -349.41) * mm});
            skPoint(sketch, "E19.4.19.10", {"position": v(384.5, -351.41) * mm});
            skLineSegment(sketch, "E19.5.19.10", {"start": v(375.5, -310.24) * mm, "end": v(384.5, -310.24) * mm});
            skLineSegment(sketch, "E19.8.19.10", {"start": v(377.5, -351.41) * mm, "end": v(382.5, -351.41) * mm});
            skLineSegment(sketch, "E19.11.19.10", {"start": v(375.5, -310.24) * mm, "end": v(375.5, -349.41) * mm});
            skArc(sketch, "E19.14.19.10", {"start": v(382.5, -351.41) * mm, "mid": v(383.91, -350.82) * mm, "end": v(384.5, -349.41) * mm});
            skArc(sketch, "E19.18.19.10", {"start": v(375.5, -349.41) * mm, "mid": v(376.09, -350.82) * mm, "end": v(377.5, -351.41) * mm});
            skPoint(sketch, "E19.0.19.11", {"position": v(375.5, -386.05) * mm});
            skLineSegment(sketch, "E19.1.19.11", {"start": v(384.5, -344.88) * mm, "end": v(384.5, -384.05) * mm});
            skPoint(sketch, "E19.4.19.11", {"position": v(384.5, -386.05) * mm});
            skLineSegment(sketch, "E19.5.19.11", {"start": v(375.5, -344.88) * mm, "end": v(384.5, -344.88) * mm});
            skLineSegment(sketch, "E19.8.19.11", {"start": v(377.5, -386.05) * mm, "end": v(382.5, -386.05) * mm});
            skLineSegment(sketch, "E19.11.19.11", {"start": v(375.5, -344.88) * mm, "end": v(375.5, -384.05) * mm});
            skArc(sketch, "E19.14.19.11", {"start": v(382.5, -386.05) * mm, "mid": v(383.91, -385.47) * mm, "end": v(384.5, -384.05) * mm});
            skArc(sketch, "E19.18.19.11", {"start": v(375.5, -384.05) * mm, "mid": v(376.09, -385.47) * mm, "end": v(377.5, -386.05) * mm});
            skPoint(sketch, "E19.0.19.12", {"position": v(375.5, -420.7) * mm});
            skLineSegment(sketch, "E19.1.19.12", {"start": v(384.5, -379.52) * mm, "end": v(384.5, -418.7) * mm});
            skPoint(sketch, "E19.4.19.12", {"position": v(384.5, -420.7) * mm});
            skLineSegment(sketch, "E19.5.19.12", {"start": v(375.5, -379.52) * mm, "end": v(384.5, -379.52) * mm});
            skLineSegment(sketch, "E19.8.19.12", {"start": v(377.5, -420.7) * mm, "end": v(382.5, -420.7) * mm});
            skLineSegment(sketch, "E19.11.19.12", {"start": v(375.5, -379.52) * mm, "end": v(375.5, -418.7) * mm});
            skArc(sketch, "E19.14.19.12", {"start": v(382.5, -420.7) * mm, "mid": v(383.91, -420.1) * mm, "end": v(384.5, -418.7) * mm});
            skArc(sketch, "E19.18.19.12", {"start": v(375.5, -418.7) * mm, "mid": v(376.09, -420.1) * mm, "end": v(377.5, -420.7) * mm});
            skPoint(sketch, "E19.0.19.13", {"position": v(375.5, -455.33) * mm});
            skLineSegment(sketch, "E19.1.19.13", {"start": v(384.5, -414.16) * mm, "end": v(384.5, -453.33) * mm});
            skPoint(sketch, "E19.4.19.13", {"position": v(384.5, -455.33) * mm});
            skLineSegment(sketch, "E19.5.19.13", {"start": v(375.5, -414.16) * mm, "end": v(384.5, -414.16) * mm});
            skLineSegment(sketch, "E19.8.19.13", {"start": v(377.5, -455.33) * mm, "end": v(382.5, -455.33) * mm});
            skLineSegment(sketch, "E19.11.19.13", {"start": v(375.5, -414.16) * mm, "end": v(375.5, -453.33) * mm});
            skArc(sketch, "E19.14.19.13", {"start": v(382.5, -455.33) * mm, "mid": v(383.91, -454.75) * mm, "end": v(384.5, -453.33) * mm});
            skArc(sketch, "E19.18.19.13", {"start": v(375.5, -453.33) * mm, "mid": v(376.09, -454.75) * mm, "end": v(377.5, -455.33) * mm});
            skPoint(sketch, "E19.0.19.14", {"position": v(375.5, -489.97) * mm});
            skLineSegment(sketch, "E19.1.19.14", {"start": v(384.5, -448.8) * mm, "end": v(384.5, -487.97) * mm});
            skPoint(sketch, "E19.4.19.14", {"position": v(384.5, -489.97) * mm});
            skLineSegment(sketch, "E19.5.19.14", {"start": v(375.5, -448.8) * mm, "end": v(384.5, -448.8) * mm});
            skLineSegment(sketch, "E19.8.19.14", {"start": v(377.5, -489.97) * mm, "end": v(382.5, -489.97) * mm});
            skLineSegment(sketch, "E19.11.19.14", {"start": v(375.5, -448.8) * mm, "end": v(375.5, -487.97) * mm});
            skArc(sketch, "E19.14.19.14", {"start": v(382.5, -489.97) * mm, "mid": v(383.91, -489.39) * mm, "end": v(384.5, -487.97) * mm});
            skArc(sketch, "E19.18.19.14", {"start": v(375.5, -487.97) * mm, "mid": v(376.09, -489.39) * mm, "end": v(377.5, -489.97) * mm});
            skPoint(sketch, "E19.0.20.0", {"position": v(395.5, -5) * mm});
            skLineSegment(sketch, "E19.1.20.0", {"start": v(404.5, 36.17) * mm, "end": v(404.5, -3) * mm});
            skPoint(sketch, "E19.4.20.0", {"position": v(404.5, -5) * mm});
            skLineSegment(sketch, "E19.5.20.0", {"start": v(395.5, 36.17) * mm, "end": v(404.5, 36.17) * mm});
            skLineSegment(sketch, "E19.8.20.0", {"start": v(397.5, -5) * mm, "end": v(402.5, -5) * mm});
            skLineSegment(sketch, "E19.11.20.0", {"start": v(395.5, 36.17) * mm, "end": v(395.5, -3) * mm});
            skArc(sketch, "E19.14.20.0", {"start": v(402.5, -5) * mm, "mid": v(403.91, -4.41) * mm, "end": v(404.5, -3) * mm});
            skArc(sketch, "E19.18.20.0", {"start": v(395.5, -3) * mm, "mid": v(396.09, -4.41) * mm, "end": v(397.5, -5) * mm});
            skPoint(sketch, "E19.0.20.1", {"position": v(395.5, -39.64) * mm});
            skLineSegment(sketch, "E19.1.20.1", {"start": v(404.5, 1.53) * mm, "end": v(404.5, -37.64) * mm});
            skPoint(sketch, "E19.4.20.1", {"position": v(404.5, -39.64) * mm});
            skLineSegment(sketch, "E19.5.20.1", {"start": v(395.5, 1.53) * mm, "end": v(404.5, 1.53) * mm});
            skLineSegment(sketch, "E19.8.20.1", {"start": v(397.5, -39.64) * mm, "end": v(402.5, -39.64) * mm});
            skLineSegment(sketch, "E19.11.20.1", {"start": v(395.5, 1.53) * mm, "end": v(395.5, -37.64) * mm});
            skArc(sketch, "E19.14.20.1", {"start": v(402.5, -39.64) * mm, "mid": v(403.91, -39.06) * mm, "end": v(404.5, -37.64) * mm});
            skArc(sketch, "E19.18.20.1", {"start": v(395.5, -37.64) * mm, "mid": v(396.09, -39.06) * mm, "end": v(397.5, -39.64) * mm});
            skPoint(sketch, "E19.0.20.2", {"position": v(395.5, -74.28) * mm});
            skLineSegment(sketch, "E19.1.20.2", {"start": v(404.5, -33.1) * mm, "end": v(404.5, -72.28) * mm});
            skPoint(sketch, "E19.4.20.2", {"position": v(404.5, -74.28) * mm});
            skLineSegment(sketch, "E19.5.20.2", {"start": v(395.5, -33.1) * mm, "end": v(404.5, -33.1) * mm});
            skLineSegment(sketch, "E19.8.20.2", {"start": v(397.5, -74.28) * mm, "end": v(402.5, -74.28) * mm});
            skLineSegment(sketch, "E19.11.20.2", {"start": v(395.5, -33.1) * mm, "end": v(395.5, -72.28) * mm});
            skArc(sketch, "E19.14.20.2", {"start": v(402.5, -74.28) * mm, "mid": v(403.91, -73.7) * mm, "end": v(404.5, -72.28) * mm});
            skArc(sketch, "E19.18.20.2", {"start": v(395.5, -72.28) * mm, "mid": v(396.09, -73.7) * mm, "end": v(397.5, -74.28) * mm});
            skPoint(sketch, "E19.0.20.3", {"position": v(395.5, -108.92) * mm});
            skLineSegment(sketch, "E19.1.20.3", {"start": v(404.5, -67.75) * mm, "end": v(404.5, -106.92) * mm});
            skPoint(sketch, "E19.4.20.3", {"position": v(404.5, -108.92) * mm});
            skLineSegment(sketch, "E19.5.20.3", {"start": v(395.5, -67.75) * mm, "end": v(404.5, -67.75) * mm});
            skLineSegment(sketch, "E19.8.20.3", {"start": v(397.5, -108.92) * mm, "end": v(402.5, -108.92) * mm});
            skLineSegment(sketch, "E19.11.20.3", {"start": v(395.5, -67.75) * mm, "end": v(395.5, -106.92) * mm});
            skArc(sketch, "E19.14.20.3", {"start": v(402.5, -108.92) * mm, "mid": v(403.91, -108.34) * mm, "end": v(404.5, -106.92) * mm});
            skArc(sketch, "E19.18.20.3", {"start": v(395.5, -106.92) * mm, "mid": v(396.09, -108.34) * mm, "end": v(397.5, -108.92) * mm});
            skPoint(sketch, "E19.0.20.4", {"position": v(395.5, -143.56) * mm});
            skLineSegment(sketch, "E19.1.20.4", {"start": v(404.5, -102.4) * mm, "end": v(404.5, -141.56) * mm});
            skPoint(sketch, "E19.4.20.4", {"position": v(404.5, -143.56) * mm});
            skLineSegment(sketch, "E19.5.20.4", {"start": v(395.5, -102.4) * mm, "end": v(404.5, -102.4) * mm});
            skLineSegment(sketch, "E19.8.20.4", {"start": v(397.5, -143.56) * mm, "end": v(402.5, -143.56) * mm});
            skLineSegment(sketch, "E19.11.20.4", {"start": v(395.5, -102.4) * mm, "end": v(395.5, -141.56) * mm});
            skArc(sketch, "E19.14.20.4", {"start": v(402.5, -143.56) * mm, "mid": v(403.91, -142.98) * mm, "end": v(404.5, -141.56) * mm});
            skArc(sketch, "E19.18.20.4", {"start": v(395.5, -141.56) * mm, "mid": v(396.09, -142.98) * mm, "end": v(397.5, -143.56) * mm});
            skPoint(sketch, "E19.0.20.5", {"position": v(395.5, -178.2) * mm});
            skLineSegment(sketch, "E19.1.20.5", {"start": v(404.5, -137.03) * mm, "end": v(404.5, -176.2) * mm});
            skPoint(sketch, "E19.4.20.5", {"position": v(404.5, -178.2) * mm});
            skLineSegment(sketch, "E19.5.20.5", {"start": v(395.5, -137.03) * mm, "end": v(404.5, -137.03) * mm});
            skLineSegment(sketch, "E19.8.20.5", {"start": v(397.5, -178.2) * mm, "end": v(402.5, -178.2) * mm});
            skLineSegment(sketch, "E19.11.20.5", {"start": v(395.5, -137.03) * mm, "end": v(395.5, -176.2) * mm});
            skArc(sketch, "E19.14.20.5", {"start": v(402.5, -178.2) * mm, "mid": v(403.91, -177.62) * mm, "end": v(404.5, -176.2) * mm});
            skArc(sketch, "E19.18.20.5", {"start": v(395.5, -176.2) * mm, "mid": v(396.09, -177.62) * mm, "end": v(397.5, -178.2) * mm});
            skPoint(sketch, "E19.0.20.6", {"position": v(395.5, -212.85) * mm});
            skLineSegment(sketch, "E19.1.20.6", {"start": v(404.5, -171.67) * mm, "end": v(404.5, -210.85) * mm});
            skPoint(sketch, "E19.4.20.6", {"position": v(404.5, -212.85) * mm});
            skLineSegment(sketch, "E19.5.20.6", {"start": v(395.5, -171.67) * mm, "end": v(404.5, -171.67) * mm});
            skLineSegment(sketch, "E19.8.20.6", {"start": v(397.5, -212.85) * mm, "end": v(402.5, -212.85) * mm});
            skLineSegment(sketch, "E19.11.20.6", {"start": v(395.5, -171.67) * mm, "end": v(395.5, -210.85) * mm});
            skArc(sketch, "E19.14.20.6", {"start": v(402.5, -212.85) * mm, "mid": v(403.91, -212.26) * mm, "end": v(404.5, -210.85) * mm});
            skArc(sketch, "E19.18.20.6", {"start": v(395.5, -210.85) * mm, "mid": v(396.09, -212.26) * mm, "end": v(397.5, -212.85) * mm});
            skPoint(sketch, "E19.0.20.7", {"position": v(395.5, -247.49) * mm});
            skLineSegment(sketch, "E19.1.20.7", {"start": v(404.5, -206.31) * mm, "end": v(404.5, -245.49) * mm});
            skPoint(sketch, "E19.4.20.7", {"position": v(404.5, -247.49) * mm});
            skLineSegment(sketch, "E19.5.20.7", {"start": v(395.5, -206.31) * mm, "end": v(404.5, -206.31) * mm});
            skLineSegment(sketch, "E19.8.20.7", {"start": v(397.5, -247.49) * mm, "end": v(402.5, -247.49) * mm});
            skLineSegment(sketch, "E19.11.20.7", {"start": v(395.5, -206.31) * mm, "end": v(395.5, -245.49) * mm});
            skArc(sketch, "E19.14.20.7", {"start": v(402.5, -247.49) * mm, "mid": v(403.91, -246.9) * mm, "end": v(404.5, -245.49) * mm});
            skArc(sketch, "E19.18.20.7", {"start": v(395.5, -245.49) * mm, "mid": v(396.09, -246.9) * mm, "end": v(397.5, -247.49) * mm});
            skPoint(sketch, "E19.0.20.8", {"position": v(395.5, -282.13) * mm});
            skLineSegment(sketch, "E19.1.20.8", {"start": v(404.5, -240.95) * mm, "end": v(404.5, -280.13) * mm});
            skPoint(sketch, "E19.4.20.8", {"position": v(404.5, -282.13) * mm});
            skLineSegment(sketch, "E19.5.20.8", {"start": v(395.5, -240.95) * mm, "end": v(404.5, -240.95) * mm});
            skLineSegment(sketch, "E19.8.20.8", {"start": v(397.5, -282.13) * mm, "end": v(402.5, -282.13) * mm});
            skLineSegment(sketch, "E19.11.20.8", {"start": v(395.5, -240.95) * mm, "end": v(395.5, -280.13) * mm});
            skArc(sketch, "E19.14.20.8", {"start": v(402.5, -282.13) * mm, "mid": v(403.91, -281.54) * mm, "end": v(404.5, -280.13) * mm});
            skArc(sketch, "E19.18.20.8", {"start": v(395.5, -280.13) * mm, "mid": v(396.09, -281.54) * mm, "end": v(397.5, -282.13) * mm});
            skPoint(sketch, "E19.0.20.9", {"position": v(395.5, -316.77) * mm});
            skLineSegment(sketch, "E19.1.20.9", {"start": v(404.5, -275.6) * mm, "end": v(404.5, -314.77) * mm});
            skPoint(sketch, "E19.4.20.9", {"position": v(404.5, -316.77) * mm});
            skLineSegment(sketch, "E19.5.20.9", {"start": v(395.5, -275.6) * mm, "end": v(404.5, -275.6) * mm});
            skLineSegment(sketch, "E19.8.20.9", {"start": v(397.5, -316.77) * mm, "end": v(402.5, -316.77) * mm});
            skLineSegment(sketch, "E19.11.20.9", {"start": v(395.5, -275.6) * mm, "end": v(395.5, -314.77) * mm});
            skArc(sketch, "E19.14.20.9", {"start": v(402.5, -316.77) * mm, "mid": v(403.91, -316.18) * mm, "end": v(404.5, -314.77) * mm});
            skArc(sketch, "E19.18.20.9", {"start": v(395.5, -314.77) * mm, "mid": v(396.09, -316.18) * mm, "end": v(397.5, -316.77) * mm});
            skPoint(sketch, "E19.0.20.10", {"position": v(395.5, -351.41) * mm});
            skLineSegment(sketch, "E19.1.20.10", {"start": v(404.5, -310.24) * mm, "end": v(404.5, -349.41) * mm});
            skPoint(sketch, "E19.4.20.10", {"position": v(404.5, -351.41) * mm});
            skLineSegment(sketch, "E19.5.20.10", {"start": v(395.5, -310.24) * mm, "end": v(404.5, -310.24) * mm});
            skLineSegment(sketch, "E19.8.20.10", {"start": v(397.5, -351.41) * mm, "end": v(402.5, -351.41) * mm});
            skLineSegment(sketch, "E19.11.20.10", {"start": v(395.5, -310.24) * mm, "end": v(395.5, -349.41) * mm});
            skArc(sketch, "E19.14.20.10", {"start": v(402.5, -351.41) * mm, "mid": v(403.91, -350.82) * mm, "end": v(404.5, -349.41) * mm});
            skArc(sketch, "E19.18.20.10", {"start": v(395.5, -349.41) * mm, "mid": v(396.09, -350.82) * mm, "end": v(397.5, -351.41) * mm});
            skPoint(sketch, "E19.0.20.11", {"position": v(395.5, -386.05) * mm});
            skLineSegment(sketch, "E19.1.20.11", {"start": v(404.5, -344.88) * mm, "end": v(404.5, -384.05) * mm});
            skPoint(sketch, "E19.4.20.11", {"position": v(404.5, -386.05) * mm});
            skLineSegment(sketch, "E19.5.20.11", {"start": v(395.5, -344.88) * mm, "end": v(404.5, -344.88) * mm});
            skLineSegment(sketch, "E19.8.20.11", {"start": v(397.5, -386.05) * mm, "end": v(402.5, -386.05) * mm});
            skLineSegment(sketch, "E19.11.20.11", {"start": v(395.5, -344.88) * mm, "end": v(395.5, -384.05) * mm});
            skArc(sketch, "E19.14.20.11", {"start": v(402.5, -386.05) * mm, "mid": v(403.91, -385.47) * mm, "end": v(404.5, -384.05) * mm});
            skArc(sketch, "E19.18.20.11", {"start": v(395.5, -384.05) * mm, "mid": v(396.09, -385.47) * mm, "end": v(397.5, -386.05) * mm});
            skPoint(sketch, "E19.0.20.12", {"position": v(395.5, -420.7) * mm});
            skLineSegment(sketch, "E19.1.20.12", {"start": v(404.5, -379.52) * mm, "end": v(404.5, -418.7) * mm});
            skPoint(sketch, "E19.4.20.12", {"position": v(404.5, -420.7) * mm});
            skLineSegment(sketch, "E19.5.20.12", {"start": v(395.5, -379.52) * mm, "end": v(404.5, -379.52) * mm});
            skLineSegment(sketch, "E19.8.20.12", {"start": v(397.5, -420.7) * mm, "end": v(402.5, -420.7) * mm});
            skLineSegment(sketch, "E19.11.20.12", {"start": v(395.5, -379.52) * mm, "end": v(395.5, -418.7) * mm});
            skArc(sketch, "E19.14.20.12", {"start": v(402.5, -420.7) * mm, "mid": v(403.91, -420.1) * mm, "end": v(404.5, -418.7) * mm});
            skArc(sketch, "E19.18.20.12", {"start": v(395.5, -418.7) * mm, "mid": v(396.09, -420.1) * mm, "end": v(397.5, -420.7) * mm});
            skPoint(sketch, "E19.0.20.13", {"position": v(395.5, -455.33) * mm});
            skLineSegment(sketch, "E19.1.20.13", {"start": v(404.5, -414.16) * mm, "end": v(404.5, -453.33) * mm});
            skPoint(sketch, "E19.4.20.13", {"position": v(404.5, -455.33) * mm});
            skLineSegment(sketch, "E19.5.20.13", {"start": v(395.5, -414.16) * mm, "end": v(404.5, -414.16) * mm});
            skLineSegment(sketch, "E19.8.20.13", {"start": v(397.5, -455.33) * mm, "end": v(402.5, -455.33) * mm});
            skLineSegment(sketch, "E19.11.20.13", {"start": v(395.5, -414.16) * mm, "end": v(395.5, -453.33) * mm});
            skArc(sketch, "E19.14.20.13", {"start": v(402.5, -455.33) * mm, "mid": v(403.91, -454.75) * mm, "end": v(404.5, -453.33) * mm});
            skArc(sketch, "E19.18.20.13", {"start": v(395.5, -453.33) * mm, "mid": v(396.09, -454.75) * mm, "end": v(397.5, -455.33) * mm});
            skPoint(sketch, "E19.0.20.14", {"position": v(395.5, -489.97) * mm});
            skLineSegment(sketch, "E19.1.20.14", {"start": v(404.5, -448.8) * mm, "end": v(404.5, -487.97) * mm});
            skPoint(sketch, "E19.4.20.14", {"position": v(404.5, -489.97) * mm});
            skLineSegment(sketch, "E19.5.20.14", {"start": v(395.5, -448.8) * mm, "end": v(404.5, -448.8) * mm});
            skLineSegment(sketch, "E19.8.20.14", {"start": v(397.5, -489.97) * mm, "end": v(402.5, -489.97) * mm});
            skLineSegment(sketch, "E19.11.20.14", {"start": v(395.5, -448.8) * mm, "end": v(395.5, -487.97) * mm});
            skArc(sketch, "E19.14.20.14", {"start": v(402.5, -489.97) * mm, "mid": v(403.91, -489.39) * mm, "end": v(404.5, -487.97) * mm});
            skArc(sketch, "E19.18.20.14", {"start": v(395.5, -487.97) * mm, "mid": v(396.09, -489.39) * mm, "end": v(397.5, -489.97) * mm});
            skPoint(sketch, "E19.0.21.0", {"position": v(415.5, -5) * mm});
            skLineSegment(sketch, "E19.1.21.0", {"start": v(424.5, 36.17) * mm, "end": v(424.5, -3) * mm});
            skPoint(sketch, "E19.4.21.0", {"position": v(424.5, -5) * mm});
            skLineSegment(sketch, "E19.5.21.0", {"start": v(415.5, 36.17) * mm, "end": v(424.5, 36.17) * mm});
            skLineSegment(sketch, "E19.8.21.0", {"start": v(417.5, -5) * mm, "end": v(422.5, -5) * mm});
            skLineSegment(sketch, "E19.11.21.0", {"start": v(415.5, 36.17) * mm, "end": v(415.5, -3) * mm});
            skArc(sketch, "E19.14.21.0", {"start": v(422.5, -5) * mm, "mid": v(423.91, -4.41) * mm, "end": v(424.5, -3) * mm});
            skArc(sketch, "E19.18.21.0", {"start": v(415.5, -3) * mm, "mid": v(416.09, -4.41) * mm, "end": v(417.5, -5) * mm});
            skPoint(sketch, "E19.0.21.1", {"position": v(415.5, -39.64) * mm});
            skLineSegment(sketch, "E19.1.21.1", {"start": v(424.5, 1.53) * mm, "end": v(424.5, -37.64) * mm});
            skPoint(sketch, "E19.4.21.1", {"position": v(424.5, -39.64) * mm});
            skLineSegment(sketch, "E19.5.21.1", {"start": v(415.5, 1.53) * mm, "end": v(424.5, 1.53) * mm});
            skLineSegment(sketch, "E19.8.21.1", {"start": v(417.5, -39.64) * mm, "end": v(422.5, -39.64) * mm});
            skLineSegment(sketch, "E19.11.21.1", {"start": v(415.5, 1.53) * mm, "end": v(415.5, -37.64) * mm});
            skArc(sketch, "E19.14.21.1", {"start": v(422.5, -39.64) * mm, "mid": v(423.91, -39.06) * mm, "end": v(424.5, -37.64) * mm});
            skArc(sketch, "E19.18.21.1", {"start": v(415.5, -37.64) * mm, "mid": v(416.09, -39.06) * mm, "end": v(417.5, -39.64) * mm});
            skPoint(sketch, "E19.0.21.2", {"position": v(415.5, -74.28) * mm});
            skLineSegment(sketch, "E19.1.21.2", {"start": v(424.5, -33.1) * mm, "end": v(424.5, -72.28) * mm});
            skPoint(sketch, "E19.4.21.2", {"position": v(424.5, -74.28) * mm});
            skLineSegment(sketch, "E19.5.21.2", {"start": v(415.5, -33.1) * mm, "end": v(424.5, -33.1) * mm});
            skLineSegment(sketch, "E19.8.21.2", {"start": v(417.5, -74.28) * mm, "end": v(422.5, -74.28) * mm});
            skLineSegment(sketch, "E19.11.21.2", {"start": v(415.5, -33.1) * mm, "end": v(415.5, -72.28) * mm});
            skArc(sketch, "E19.14.21.2", {"start": v(422.5, -74.28) * mm, "mid": v(423.91, -73.7) * mm, "end": v(424.5, -72.28) * mm});
            skArc(sketch, "E19.18.21.2", {"start": v(415.5, -72.28) * mm, "mid": v(416.09, -73.7) * mm, "end": v(417.5, -74.28) * mm});
            skPoint(sketch, "E19.0.21.3", {"position": v(415.5, -108.92) * mm});
            skLineSegment(sketch, "E19.1.21.3", {"start": v(424.5, -67.75) * mm, "end": v(424.5, -106.92) * mm});
            skPoint(sketch, "E19.4.21.3", {"position": v(424.5, -108.92) * mm});
            skLineSegment(sketch, "E19.5.21.3", {"start": v(415.5, -67.75) * mm, "end": v(424.5, -67.75) * mm});
            skLineSegment(sketch, "E19.8.21.3", {"start": v(417.5, -108.92) * mm, "end": v(422.5, -108.92) * mm});
            skLineSegment(sketch, "E19.11.21.3", {"start": v(415.5, -67.75) * mm, "end": v(415.5, -106.92) * mm});
            skArc(sketch, "E19.14.21.3", {"start": v(422.5, -108.92) * mm, "mid": v(423.91, -108.34) * mm, "end": v(424.5, -106.92) * mm});
            skArc(sketch, "E19.18.21.3", {"start": v(415.5, -106.92) * mm, "mid": v(416.09, -108.34) * mm, "end": v(417.5, -108.92) * mm});
            skPoint(sketch, "E19.0.21.4", {"position": v(415.5, -143.56) * mm});
            skLineSegment(sketch, "E19.1.21.4", {"start": v(424.5, -102.4) * mm, "end": v(424.5, -141.56) * mm});
            skPoint(sketch, "E19.4.21.4", {"position": v(424.5, -143.56) * mm});
            skLineSegment(sketch, "E19.5.21.4", {"start": v(415.5, -102.4) * mm, "end": v(424.5, -102.4) * mm});
            skLineSegment(sketch, "E19.8.21.4", {"start": v(417.5, -143.56) * mm, "end": v(422.5, -143.56) * mm});
            skLineSegment(sketch, "E19.11.21.4", {"start": v(415.5, -102.4) * mm, "end": v(415.5, -141.56) * mm});
            skArc(sketch, "E19.14.21.4", {"start": v(422.5, -143.56) * mm, "mid": v(423.91, -142.98) * mm, "end": v(424.5, -141.56) * mm});
            skArc(sketch, "E19.18.21.4", {"start": v(415.5, -141.56) * mm, "mid": v(416.09, -142.98) * mm, "end": v(417.5, -143.56) * mm});
            skPoint(sketch, "E19.0.21.5", {"position": v(415.5, -178.2) * mm});
            skLineSegment(sketch, "E19.1.21.5", {"start": v(424.5, -137.03) * mm, "end": v(424.5, -176.2) * mm});
            skPoint(sketch, "E19.4.21.5", {"position": v(424.5, -178.2) * mm});
            skLineSegment(sketch, "E19.5.21.5", {"start": v(415.5, -137.03) * mm, "end": v(424.5, -137.03) * mm});
            skLineSegment(sketch, "E19.8.21.5", {"start": v(417.5, -178.2) * mm, "end": v(422.5, -178.2) * mm});
            skLineSegment(sketch, "E19.11.21.5", {"start": v(415.5, -137.03) * mm, "end": v(415.5, -176.2) * mm});
            skArc(sketch, "E19.14.21.5", {"start": v(422.5, -178.2) * mm, "mid": v(423.91, -177.62) * mm, "end": v(424.5, -176.2) * mm});
            skArc(sketch, "E19.18.21.5", {"start": v(415.5, -176.2) * mm, "mid": v(416.09, -177.62) * mm, "end": v(417.5, -178.2) * mm});
            skPoint(sketch, "E19.0.21.6", {"position": v(415.5, -212.85) * mm});
            skLineSegment(sketch, "E19.1.21.6", {"start": v(424.5, -171.67) * mm, "end": v(424.5, -210.85) * mm});
            skPoint(sketch, "E19.4.21.6", {"position": v(424.5, -212.85) * mm});
            skLineSegment(sketch, "E19.5.21.6", {"start": v(415.5, -171.67) * mm, "end": v(424.5, -171.67) * mm});
            skLineSegment(sketch, "E19.8.21.6", {"start": v(417.5, -212.85) * mm, "end": v(422.5, -212.85) * mm});
            skLineSegment(sketch, "E19.11.21.6", {"start": v(415.5, -171.67) * mm, "end": v(415.5, -210.85) * mm});
            skArc(sketch, "E19.14.21.6", {"start": v(422.5, -212.85) * mm, "mid": v(423.91, -212.26) * mm, "end": v(424.5, -210.85) * mm});
            skArc(sketch, "E19.18.21.6", {"start": v(415.5, -210.85) * mm, "mid": v(416.09, -212.26) * mm, "end": v(417.5, -212.85) * mm});
            skPoint(sketch, "E19.0.21.7", {"position": v(415.5, -247.49) * mm});
            skLineSegment(sketch, "E19.1.21.7", {"start": v(424.5, -206.31) * mm, "end": v(424.5, -245.49) * mm});
            skPoint(sketch, "E19.4.21.7", {"position": v(424.5, -247.49) * mm});
            skLineSegment(sketch, "E19.5.21.7", {"start": v(415.5, -206.31) * mm, "end": v(424.5, -206.31) * mm});
            skLineSegment(sketch, "E19.8.21.7", {"start": v(417.5, -247.49) * mm, "end": v(422.5, -247.49) * mm});
            skLineSegment(sketch, "E19.11.21.7", {"start": v(415.5, -206.31) * mm, "end": v(415.5, -245.49) * mm});
            skArc(sketch, "E19.14.21.7", {"start": v(422.5, -247.49) * mm, "mid": v(423.91, -246.9) * mm, "end": v(424.5, -245.49) * mm});
            skArc(sketch, "E19.18.21.7", {"start": v(415.5, -245.49) * mm, "mid": v(416.09, -246.9) * mm, "end": v(417.5, -247.49) * mm});
            skPoint(sketch, "E19.0.21.8", {"position": v(415.5, -282.13) * mm});
            skLineSegment(sketch, "E19.1.21.8", {"start": v(424.5, -240.95) * mm, "end": v(424.5, -280.13) * mm});
            skPoint(sketch, "E19.4.21.8", {"position": v(424.5, -282.13) * mm});
            skLineSegment(sketch, "E19.5.21.8", {"start": v(415.5, -240.95) * mm, "end": v(424.5, -240.95) * mm});
            skLineSegment(sketch, "E19.8.21.8", {"start": v(417.5, -282.13) * mm, "end": v(422.5, -282.13) * mm});
            skLineSegment(sketch, "E19.11.21.8", {"start": v(415.5, -240.95) * mm, "end": v(415.5, -280.13) * mm});
            skArc(sketch, "E19.14.21.8", {"start": v(422.5, -282.13) * mm, "mid": v(423.91, -281.54) * mm, "end": v(424.5, -280.13) * mm});
            skArc(sketch, "E19.18.21.8", {"start": v(415.5, -280.13) * mm, "mid": v(416.09, -281.54) * mm, "end": v(417.5, -282.13) * mm});
            skPoint(sketch, "E19.0.21.9", {"position": v(415.5, -316.77) * mm});
            skLineSegment(sketch, "E19.1.21.9", {"start": v(424.5, -275.6) * mm, "end": v(424.5, -314.77) * mm});
            skPoint(sketch, "E19.4.21.9", {"position": v(424.5, -316.77) * mm});
            skLineSegment(sketch, "E19.5.21.9", {"start": v(415.5, -275.6) * mm, "end": v(424.5, -275.6) * mm});
            skLineSegment(sketch, "E19.8.21.9", {"start": v(417.5, -316.77) * mm, "end": v(422.5, -316.77) * mm});
            skLineSegment(sketch, "E19.11.21.9", {"start": v(415.5, -275.6) * mm, "end": v(415.5, -314.77) * mm});
            skArc(sketch, "E19.14.21.9", {"start": v(422.5, -316.77) * mm, "mid": v(423.91, -316.18) * mm, "end": v(424.5, -314.77) * mm});
            skArc(sketch, "E19.18.21.9", {"start": v(415.5, -314.77) * mm, "mid": v(416.09, -316.18) * mm, "end": v(417.5, -316.77) * mm});
            skPoint(sketch, "E19.0.21.10", {"position": v(415.5, -351.41) * mm});
            skLineSegment(sketch, "E19.1.21.10", {"start": v(424.5, -310.24) * mm, "end": v(424.5, -349.41) * mm});
            skPoint(sketch, "E19.4.21.10", {"position": v(424.5, -351.41) * mm});
            skLineSegment(sketch, "E19.5.21.10", {"start": v(415.5, -310.24) * mm, "end": v(424.5, -310.24) * mm});
            skLineSegment(sketch, "E19.8.21.10", {"start": v(417.5, -351.41) * mm, "end": v(422.5, -351.41) * mm});
            skLineSegment(sketch, "E19.11.21.10", {"start": v(415.5, -310.24) * mm, "end": v(415.5, -349.41) * mm});
            skArc(sketch, "E19.14.21.10", {"start": v(422.5, -351.41) * mm, "mid": v(423.91, -350.82) * mm, "end": v(424.5, -349.41) * mm});
            skArc(sketch, "E19.18.21.10", {"start": v(415.5, -349.41) * mm, "mid": v(416.09, -350.82) * mm, "end": v(417.5, -351.41) * mm});
            skPoint(sketch, "E19.0.21.11", {"position": v(415.5, -386.05) * mm});
            skLineSegment(sketch, "E19.1.21.11", {"start": v(424.5, -344.88) * mm, "end": v(424.5, -384.05) * mm});
            skPoint(sketch, "E19.4.21.11", {"position": v(424.5, -386.05) * mm});
            skLineSegment(sketch, "E19.5.21.11", {"start": v(415.5, -344.88) * mm, "end": v(424.5, -344.88) * mm});
            skLineSegment(sketch, "E19.8.21.11", {"start": v(417.5, -386.05) * mm, "end": v(422.5, -386.05) * mm});
            skLineSegment(sketch, "E19.11.21.11", {"start": v(415.5, -344.88) * mm, "end": v(415.5, -384.05) * mm});
            skArc(sketch, "E19.14.21.11", {"start": v(422.5, -386.05) * mm, "mid": v(423.91, -385.47) * mm, "end": v(424.5, -384.05) * mm});
            skArc(sketch, "E19.18.21.11", {"start": v(415.5, -384.05) * mm, "mid": v(416.09, -385.47) * mm, "end": v(417.5, -386.05) * mm});
            skPoint(sketch, "E19.0.21.12", {"position": v(415.5, -420.7) * mm});
            skLineSegment(sketch, "E19.1.21.12", {"start": v(424.5, -379.52) * mm, "end": v(424.5, -418.7) * mm});
            skPoint(sketch, "E19.4.21.12", {"position": v(424.5, -420.7) * mm});
            skLineSegment(sketch, "E19.5.21.12", {"start": v(415.5, -379.52) * mm, "end": v(424.5, -379.52) * mm});
            skLineSegment(sketch, "E19.8.21.12", {"start": v(417.5, -420.7) * mm, "end": v(422.5, -420.7) * mm});
            skLineSegment(sketch, "E19.11.21.12", {"start": v(415.5, -379.52) * mm, "end": v(415.5, -418.7) * mm});
            skArc(sketch, "E19.14.21.12", {"start": v(422.5, -420.7) * mm, "mid": v(423.91, -420.1) * mm, "end": v(424.5, -418.7) * mm});
            skArc(sketch, "E19.18.21.12", {"start": v(415.5, -418.7) * mm, "mid": v(416.09, -420.1) * mm, "end": v(417.5, -420.7) * mm});
            skPoint(sketch, "E19.0.21.13", {"position": v(415.5, -455.33) * mm});
            skLineSegment(sketch, "E19.1.21.13", {"start": v(424.5, -414.16) * mm, "end": v(424.5, -453.33) * mm});
            skPoint(sketch, "E19.4.21.13", {"position": v(424.5, -455.33) * mm});
            skLineSegment(sketch, "E19.5.21.13", {"start": v(415.5, -414.16) * mm, "end": v(424.5, -414.16) * mm});
            skLineSegment(sketch, "E19.8.21.13", {"start": v(417.5, -455.33) * mm, "end": v(422.5, -455.33) * mm});
            skLineSegment(sketch, "E19.11.21.13", {"start": v(415.5, -414.16) * mm, "end": v(415.5, -453.33) * mm});
            skArc(sketch, "E19.14.21.13", {"start": v(422.5, -455.33) * mm, "mid": v(423.91, -454.75) * mm, "end": v(424.5, -453.33) * mm});
            skArc(sketch, "E19.18.21.13", {"start": v(415.5, -453.33) * mm, "mid": v(416.09, -454.75) * mm, "end": v(417.5, -455.33) * mm});
            skPoint(sketch, "E19.0.21.14", {"position": v(415.5, -489.97) * mm});
            skLineSegment(sketch, "E19.1.21.14", {"start": v(424.5, -448.8) * mm, "end": v(424.5, -487.97) * mm});
            skPoint(sketch, "E19.4.21.14", {"position": v(424.5, -489.97) * mm});
            skLineSegment(sketch, "E19.5.21.14", {"start": v(415.5, -448.8) * mm, "end": v(424.5, -448.8) * mm});
            skLineSegment(sketch, "E19.8.21.14", {"start": v(417.5, -489.97) * mm, "end": v(422.5, -489.97) * mm});
            skLineSegment(sketch, "E19.11.21.14", {"start": v(415.5, -448.8) * mm, "end": v(415.5, -487.97) * mm});
            skArc(sketch, "E19.14.21.14", {"start": v(422.5, -489.97) * mm, "mid": v(423.91, -489.39) * mm, "end": v(424.5, -487.97) * mm});
            skArc(sketch, "E19.18.21.14", {"start": v(415.5, -487.97) * mm, "mid": v(416.09, -489.39) * mm, "end": v(417.5, -489.97) * mm});
            skPoint(sketch, "E19.0.22.0", {"position": v(435.5, -5) * mm});
            skLineSegment(sketch, "E19.1.22.0", {"start": v(444.5, 36.17) * mm, "end": v(444.5, -3) * mm});
            skPoint(sketch, "E19.4.22.0", {"position": v(444.5, -5) * mm});
            skLineSegment(sketch, "E19.5.22.0", {"start": v(435.5, 36.17) * mm, "end": v(444.5, 36.17) * mm});
            skLineSegment(sketch, "E19.8.22.0", {"start": v(437.5, -5) * mm, "end": v(442.5, -5) * mm});
            skLineSegment(sketch, "E19.11.22.0", {"start": v(435.5, 36.17) * mm, "end": v(435.5, -3) * mm});
            skArc(sketch, "E19.14.22.0", {"start": v(442.5, -5) * mm, "mid": v(443.91, -4.41) * mm, "end": v(444.5, -3) * mm});
            skArc(sketch, "E19.18.22.0", {"start": v(435.5, -3) * mm, "mid": v(436.09, -4.41) * mm, "end": v(437.5, -5) * mm});
            skPoint(sketch, "E19.0.22.1", {"position": v(435.5, -39.64) * mm});
            skLineSegment(sketch, "E19.1.22.1", {"start": v(444.5, 1.53) * mm, "end": v(444.5, -37.64) * mm});
            skPoint(sketch, "E19.4.22.1", {"position": v(444.5, -39.64) * mm});
            skLineSegment(sketch, "E19.5.22.1", {"start": v(435.5, 1.53) * mm, "end": v(444.5, 1.53) * mm});
            skLineSegment(sketch, "E19.8.22.1", {"start": v(437.5, -39.64) * mm, "end": v(442.5, -39.64) * mm});
            skLineSegment(sketch, "E19.11.22.1", {"start": v(435.5, 1.53) * mm, "end": v(435.5, -37.64) * mm});
            skArc(sketch, "E19.14.22.1", {"start": v(442.5, -39.64) * mm, "mid": v(443.91, -39.06) * mm, "end": v(444.5, -37.64) * mm});
            skArc(sketch, "E19.18.22.1", {"start": v(435.5, -37.64) * mm, "mid": v(436.09, -39.06) * mm, "end": v(437.5, -39.64) * mm});
            skPoint(sketch, "E19.0.22.2", {"position": v(435.5, -74.28) * mm});
            skLineSegment(sketch, "E19.1.22.2", {"start": v(444.5, -33.1) * mm, "end": v(444.5, -72.28) * mm});
            skPoint(sketch, "E19.4.22.2", {"position": v(444.5, -74.28) * mm});
            skLineSegment(sketch, "E19.5.22.2", {"start": v(435.5, -33.1) * mm, "end": v(444.5, -33.1) * mm});
            skLineSegment(sketch, "E19.8.22.2", {"start": v(437.5, -74.28) * mm, "end": v(442.5, -74.28) * mm});
            skLineSegment(sketch, "E19.11.22.2", {"start": v(435.5, -33.1) * mm, "end": v(435.5, -72.28) * mm});
            skArc(sketch, "E19.14.22.2", {"start": v(442.5, -74.28) * mm, "mid": v(443.91, -73.7) * mm, "end": v(444.5, -72.28) * mm});
            skArc(sketch, "E19.18.22.2", {"start": v(435.5, -72.28) * mm, "mid": v(436.09, -73.7) * mm, "end": v(437.5, -74.28) * mm});
            skPoint(sketch, "E19.0.22.3", {"position": v(435.5, -108.92) * mm});
            skLineSegment(sketch, "E19.1.22.3", {"start": v(444.5, -67.75) * mm, "end": v(444.5, -106.92) * mm});
            skPoint(sketch, "E19.4.22.3", {"position": v(444.5, -108.92) * mm});
            skLineSegment(sketch, "E19.5.22.3", {"start": v(435.5, -67.75) * mm, "end": v(444.5, -67.75) * mm});
            skLineSegment(sketch, "E19.8.22.3", {"start": v(437.5, -108.92) * mm, "end": v(442.5, -108.92) * mm});
            skLineSegment(sketch, "E19.11.22.3", {"start": v(435.5, -67.75) * mm, "end": v(435.5, -106.92) * mm});
            skArc(sketch, "E19.14.22.3", {"start": v(442.5, -108.92) * mm, "mid": v(443.91, -108.34) * mm, "end": v(444.5, -106.92) * mm});
            skArc(sketch, "E19.18.22.3", {"start": v(435.5, -106.92) * mm, "mid": v(436.09, -108.34) * mm, "end": v(437.5, -108.92) * mm});
            skPoint(sketch, "E19.0.22.4", {"position": v(435.5, -143.56) * mm});
            skLineSegment(sketch, "E19.1.22.4", {"start": v(444.5, -102.4) * mm, "end": v(444.5, -141.56) * mm});
            skPoint(sketch, "E19.4.22.4", {"position": v(444.5, -143.56) * mm});
            skLineSegment(sketch, "E19.5.22.4", {"start": v(435.5, -102.4) * mm, "end": v(444.5, -102.4) * mm});
            skLineSegment(sketch, "E19.8.22.4", {"start": v(437.5, -143.56) * mm, "end": v(442.5, -143.56) * mm});
            skLineSegment(sketch, "E19.11.22.4", {"start": v(435.5, -102.4) * mm, "end": v(435.5, -141.56) * mm});
            skArc(sketch, "E19.14.22.4", {"start": v(442.5, -143.56) * mm, "mid": v(443.91, -142.98) * mm, "end": v(444.5, -141.56) * mm});
            skArc(sketch, "E19.18.22.4", {"start": v(435.5, -141.56) * mm, "mid": v(436.09, -142.98) * mm, "end": v(437.5, -143.56) * mm});
            skPoint(sketch, "E19.0.22.5", {"position": v(435.5, -178.2) * mm});
            skLineSegment(sketch, "E19.1.22.5", {"start": v(444.5, -137.03) * mm, "end": v(444.5, -176.2) * mm});
            skPoint(sketch, "E19.4.22.5", {"position": v(444.5, -178.2) * mm});
            skLineSegment(sketch, "E19.5.22.5", {"start": v(435.5, -137.03) * mm, "end": v(444.5, -137.03) * mm});
            skLineSegment(sketch, "E19.8.22.5", {"start": v(437.5, -178.2) * mm, "end": v(442.5, -178.2) * mm});
            skLineSegment(sketch, "E19.11.22.5", {"start": v(435.5, -137.03) * mm, "end": v(435.5, -176.2) * mm});
            skArc(sketch, "E19.14.22.5", {"start": v(442.5, -178.2) * mm, "mid": v(443.91, -177.62) * mm, "end": v(444.5, -176.2) * mm});
            skArc(sketch, "E19.18.22.5", {"start": v(435.5, -176.2) * mm, "mid": v(436.09, -177.62) * mm, "end": v(437.5, -178.2) * mm});
            skPoint(sketch, "E19.0.22.6", {"position": v(435.5, -212.85) * mm});
            skLineSegment(sketch, "E19.1.22.6", {"start": v(444.5, -171.67) * mm, "end": v(444.5, -210.85) * mm});
            skPoint(sketch, "E19.4.22.6", {"position": v(444.5, -212.85) * mm});
            skLineSegment(sketch, "E19.5.22.6", {"start": v(435.5, -171.67) * mm, "end": v(444.5, -171.67) * mm});
            skLineSegment(sketch, "E19.8.22.6", {"start": v(437.5, -212.85) * mm, "end": v(442.5, -212.85) * mm});
            skLineSegment(sketch, "E19.11.22.6", {"start": v(435.5, -171.67) * mm, "end": v(435.5, -210.85) * mm});
            skArc(sketch, "E19.14.22.6", {"start": v(442.5, -212.85) * mm, "mid": v(443.91, -212.26) * mm, "end": v(444.5, -210.85) * mm});
            skArc(sketch, "E19.18.22.6", {"start": v(435.5, -210.85) * mm, "mid": v(436.09, -212.26) * mm, "end": v(437.5, -212.85) * mm});
            skPoint(sketch, "E19.0.22.7", {"position": v(435.5, -247.49) * mm});
            skLineSegment(sketch, "E19.1.22.7", {"start": v(444.5, -206.31) * mm, "end": v(444.5, -245.49) * mm});
            skPoint(sketch, "E19.4.22.7", {"position": v(444.5, -247.49) * mm});
            skLineSegment(sketch, "E19.5.22.7", {"start": v(435.5, -206.31) * mm, "end": v(444.5, -206.31) * mm});
            skLineSegment(sketch, "E19.8.22.7", {"start": v(437.5, -247.49) * mm, "end": v(442.5, -247.49) * mm});
            skLineSegment(sketch, "E19.11.22.7", {"start": v(435.5, -206.31) * mm, "end": v(435.5, -245.49) * mm});
            skArc(sketch, "E19.14.22.7", {"start": v(442.5, -247.49) * mm, "mid": v(443.91, -246.9) * mm, "end": v(444.5, -245.49) * mm});
            skArc(sketch, "E19.18.22.7", {"start": v(435.5, -245.49) * mm, "mid": v(436.09, -246.9) * mm, "end": v(437.5, -247.49) * mm});
            skPoint(sketch, "E19.0.22.8", {"position": v(435.5, -282.13) * mm});
            skLineSegment(sketch, "E19.1.22.8", {"start": v(444.5, -240.95) * mm, "end": v(444.5, -280.13) * mm});
            skPoint(sketch, "E19.4.22.8", {"position": v(444.5, -282.13) * mm});
            skLineSegment(sketch, "E19.5.22.8", {"start": v(435.5, -240.95) * mm, "end": v(444.5, -240.95) * mm});
            skLineSegment(sketch, "E19.8.22.8", {"start": v(437.5, -282.13) * mm, "end": v(442.5, -282.13) * mm});
            skLineSegment(sketch, "E19.11.22.8", {"start": v(435.5, -240.95) * mm, "end": v(435.5, -280.13) * mm});
            skArc(sketch, "E19.14.22.8", {"start": v(442.5, -282.13) * mm, "mid": v(443.91, -281.54) * mm, "end": v(444.5, -280.13) * mm});
            skArc(sketch, "E19.18.22.8", {"start": v(435.5, -280.13) * mm, "mid": v(436.09, -281.54) * mm, "end": v(437.5, -282.13) * mm});
            skPoint(sketch, "E19.0.22.9", {"position": v(435.5, -316.77) * mm});
            skLineSegment(sketch, "E19.1.22.9", {"start": v(444.5, -275.6) * mm, "end": v(444.5, -314.77) * mm});
            skPoint(sketch, "E19.4.22.9", {"position": v(444.5, -316.77) * mm});
            skLineSegment(sketch, "E19.5.22.9", {"start": v(435.5, -275.6) * mm, "end": v(444.5, -275.6) * mm});
            skLineSegment(sketch, "E19.8.22.9", {"start": v(437.5, -316.77) * mm, "end": v(442.5, -316.77) * mm});
            skLineSegment(sketch, "E19.11.22.9", {"start": v(435.5, -275.6) * mm, "end": v(435.5, -314.77) * mm});
            skArc(sketch, "E19.14.22.9", {"start": v(442.5, -316.77) * mm, "mid": v(443.91, -316.18) * mm, "end": v(444.5, -314.77) * mm});
            skArc(sketch, "E19.18.22.9", {"start": v(435.5, -314.77) * mm, "mid": v(436.09, -316.18) * mm, "end": v(437.5, -316.77) * mm});
            skPoint(sketch, "E19.0.22.10", {"position": v(435.5, -351.41) * mm});
            skLineSegment(sketch, "E19.1.22.10", {"start": v(444.5, -310.24) * mm, "end": v(444.5, -349.41) * mm});
            skPoint(sketch, "E19.4.22.10", {"position": v(444.5, -351.41) * mm});
            skLineSegment(sketch, "E19.5.22.10", {"start": v(435.5, -310.24) * mm, "end": v(444.5, -310.24) * mm});
            skLineSegment(sketch, "E19.8.22.10", {"start": v(437.5, -351.41) * mm, "end": v(442.5, -351.41) * mm});
            skLineSegment(sketch, "E19.11.22.10", {"start": v(435.5, -310.24) * mm, "end": v(435.5, -349.41) * mm});
            skArc(sketch, "E19.14.22.10", {"start": v(442.5, -351.41) * mm, "mid": v(443.91, -350.82) * mm, "end": v(444.5, -349.41) * mm});
            skArc(sketch, "E19.18.22.10", {"start": v(435.5, -349.41) * mm, "mid": v(436.09, -350.82) * mm, "end": v(437.5, -351.41) * mm});
            skPoint(sketch, "E19.0.22.11", {"position": v(435.5, -386.05) * mm});
            skLineSegment(sketch, "E19.1.22.11", {"start": v(444.5, -344.88) * mm, "end": v(444.5, -384.05) * mm});
            skPoint(sketch, "E19.4.22.11", {"position": v(444.5, -386.05) * mm});
            skLineSegment(sketch, "E19.5.22.11", {"start": v(435.5, -344.88) * mm, "end": v(444.5, -344.88) * mm});
            skLineSegment(sketch, "E19.8.22.11", {"start": v(437.5, -386.05) * mm, "end": v(442.5, -386.05) * mm});
            skLineSegment(sketch, "E19.11.22.11", {"start": v(435.5, -344.88) * mm, "end": v(435.5, -384.05) * mm});
            skArc(sketch, "E19.14.22.11", {"start": v(442.5, -386.05) * mm, "mid": v(443.91, -385.47) * mm, "end": v(444.5, -384.05) * mm});
            skArc(sketch, "E19.18.22.11", {"start": v(435.5, -384.05) * mm, "mid": v(436.09, -385.47) * mm, "end": v(437.5, -386.05) * mm});
            skPoint(sketch, "E19.0.22.12", {"position": v(435.5, -420.7) * mm});
            skLineSegment(sketch, "E19.1.22.12", {"start": v(444.5, -379.52) * mm, "end": v(444.5, -418.7) * mm});
            skPoint(sketch, "E19.4.22.12", {"position": v(444.5, -420.7) * mm});
            skLineSegment(sketch, "E19.5.22.12", {"start": v(435.5, -379.52) * mm, "end": v(444.5, -379.52) * mm});
            skLineSegment(sketch, "E19.8.22.12", {"start": v(437.5, -420.7) * mm, "end": v(442.5, -420.7) * mm});
            skLineSegment(sketch, "E19.11.22.12", {"start": v(435.5, -379.52) * mm, "end": v(435.5, -418.7) * mm});
            skArc(sketch, "E19.14.22.12", {"start": v(442.5, -420.7) * mm, "mid": v(443.91, -420.1) * mm, "end": v(444.5, -418.7) * mm});
            skArc(sketch, "E19.18.22.12", {"start": v(435.5, -418.7) * mm, "mid": v(436.09, -420.1) * mm, "end": v(437.5, -420.7) * mm});
            skPoint(sketch, "E19.0.22.13", {"position": v(435.5, -455.33) * mm});
            skLineSegment(sketch, "E19.1.22.13", {"start": v(444.5, -414.16) * mm, "end": v(444.5, -453.33) * mm});
            skPoint(sketch, "E19.4.22.13", {"position": v(444.5, -455.33) * mm});
            skLineSegment(sketch, "E19.5.22.13", {"start": v(435.5, -414.16) * mm, "end": v(444.5, -414.16) * mm});
            skLineSegment(sketch, "E19.8.22.13", {"start": v(437.5, -455.33) * mm, "end": v(442.5, -455.33) * mm});
            skLineSegment(sketch, "E19.11.22.13", {"start": v(435.5, -414.16) * mm, "end": v(435.5, -453.33) * mm});
            skArc(sketch, "E19.14.22.13", {"start": v(442.5, -455.33) * mm, "mid": v(443.91, -454.75) * mm, "end": v(444.5, -453.33) * mm});
            skArc(sketch, "E19.18.22.13", {"start": v(435.5, -453.33) * mm, "mid": v(436.09, -454.75) * mm, "end": v(437.5, -455.33) * mm});
            skPoint(sketch, "E19.0.22.14", {"position": v(435.5, -489.97) * mm});
            skLineSegment(sketch, "E19.1.22.14", {"start": v(444.5, -448.8) * mm, "end": v(444.5, -487.97) * mm});
            skPoint(sketch, "E19.4.22.14", {"position": v(444.5, -489.97) * mm});
            skLineSegment(sketch, "E19.5.22.14", {"start": v(435.5, -448.8) * mm, "end": v(444.5, -448.8) * mm});
            skLineSegment(sketch, "E19.8.22.14", {"start": v(437.5, -489.97) * mm, "end": v(442.5, -489.97) * mm});
            skLineSegment(sketch, "E19.11.22.14", {"start": v(435.5, -448.8) * mm, "end": v(435.5, -487.97) * mm});
            skArc(sketch, "E19.14.22.14", {"start": v(442.5, -489.97) * mm, "mid": v(443.91, -489.39) * mm, "end": v(444.5, -487.97) * mm});
            skArc(sketch, "E19.18.22.14", {"start": v(435.5, -487.97) * mm, "mid": v(436.09, -489.39) * mm, "end": v(437.5, -489.97) * mm});
            skPoint(sketch, "E19.0.23.0", {"position": v(455.5, -5) * mm});
            skLineSegment(sketch, "E19.1.23.0", {"start": v(464.5, 36.17) * mm, "end": v(464.5, -3) * mm});
            skPoint(sketch, "E19.4.23.0", {"position": v(464.5, -5) * mm});
            skLineSegment(sketch, "E19.5.23.0", {"start": v(455.5, 36.17) * mm, "end": v(464.5, 36.17) * mm});
            skLineSegment(sketch, "E19.8.23.0", {"start": v(457.5, -5) * mm, "end": v(462.5, -5) * mm});
            skLineSegment(sketch, "E19.11.23.0", {"start": v(455.5, 36.17) * mm, "end": v(455.5, -3) * mm});
            skArc(sketch, "E19.14.23.0", {"start": v(462.5, -5) * mm, "mid": v(463.91, -4.41) * mm, "end": v(464.5, -3) * mm});
            skArc(sketch, "E19.18.23.0", {"start": v(455.5, -3) * mm, "mid": v(456.09, -4.41) * mm, "end": v(457.5, -5) * mm});
            skPoint(sketch, "E19.0.23.1", {"position": v(455.5, -39.64) * mm});
            skLineSegment(sketch, "E19.1.23.1", {"start": v(464.5, 1.53) * mm, "end": v(464.5, -37.64) * mm});
            skPoint(sketch, "E19.4.23.1", {"position": v(464.5, -39.64) * mm});
            skLineSegment(sketch, "E19.5.23.1", {"start": v(455.5, 1.53) * mm, "end": v(464.5, 1.53) * mm});
            skLineSegment(sketch, "E19.8.23.1", {"start": v(457.5, -39.64) * mm, "end": v(462.5, -39.64) * mm});
            skLineSegment(sketch, "E19.11.23.1", {"start": v(455.5, 1.53) * mm, "end": v(455.5, -37.64) * mm});
            skArc(sketch, "E19.14.23.1", {"start": v(462.5, -39.64) * mm, "mid": v(463.91, -39.06) * mm, "end": v(464.5, -37.64) * mm});
            skArc(sketch, "E19.18.23.1", {"start": v(455.5, -37.64) * mm, "mid": v(456.09, -39.06) * mm, "end": v(457.5, -39.64) * mm});
            skPoint(sketch, "E19.0.23.2", {"position": v(455.5, -74.28) * mm});
            skLineSegment(sketch, "E19.1.23.2", {"start": v(464.5, -33.1) * mm, "end": v(464.5, -72.28) * mm});
            skPoint(sketch, "E19.4.23.2", {"position": v(464.5, -74.28) * mm});
            skLineSegment(sketch, "E19.5.23.2", {"start": v(455.5, -33.1) * mm, "end": v(464.5, -33.1) * mm});
            skLineSegment(sketch, "E19.8.23.2", {"start": v(457.5, -74.28) * mm, "end": v(462.5, -74.28) * mm});
            skLineSegment(sketch, "E19.11.23.2", {"start": v(455.5, -33.1) * mm, "end": v(455.5, -72.28) * mm});
            skArc(sketch, "E19.14.23.2", {"start": v(462.5, -74.28) * mm, "mid": v(463.91, -73.7) * mm, "end": v(464.5, -72.28) * mm});
            skArc(sketch, "E19.18.23.2", {"start": v(455.5, -72.28) * mm, "mid": v(456.09, -73.7) * mm, "end": v(457.5, -74.28) * mm});
            skPoint(sketch, "E19.0.23.3", {"position": v(455.5, -108.92) * mm});
            skLineSegment(sketch, "E19.1.23.3", {"start": v(464.5, -67.75) * mm, "end": v(464.5, -106.92) * mm});
            skPoint(sketch, "E19.4.23.3", {"position": v(464.5, -108.92) * mm});
            skLineSegment(sketch, "E19.5.23.3", {"start": v(455.5, -67.75) * mm, "end": v(464.5, -67.75) * mm});
            skLineSegment(sketch, "E19.8.23.3", {"start": v(457.5, -108.92) * mm, "end": v(462.5, -108.92) * mm});
            skLineSegment(sketch, "E19.11.23.3", {"start": v(455.5, -67.75) * mm, "end": v(455.5, -106.92) * mm});
            skArc(sketch, "E19.14.23.3", {"start": v(462.5, -108.92) * mm, "mid": v(463.91, -108.34) * mm, "end": v(464.5, -106.92) * mm});
            skArc(sketch, "E19.18.23.3", {"start": v(455.5, -106.92) * mm, "mid": v(456.09, -108.34) * mm, "end": v(457.5, -108.92) * mm});
            skPoint(sketch, "E19.0.23.4", {"position": v(455.5, -143.56) * mm});
            skLineSegment(sketch, "E19.1.23.4", {"start": v(464.5, -102.4) * mm, "end": v(464.5, -141.56) * mm});
            skPoint(sketch, "E19.4.23.4", {"position": v(464.5, -143.56) * mm});
            skLineSegment(sketch, "E19.5.23.4", {"start": v(455.5, -102.4) * mm, "end": v(464.5, -102.4) * mm});
            skLineSegment(sketch, "E19.8.23.4", {"start": v(457.5, -143.56) * mm, "end": v(462.5, -143.56) * mm});
            skLineSegment(sketch, "E19.11.23.4", {"start": v(455.5, -102.4) * mm, "end": v(455.5, -141.56) * mm});
            skArc(sketch, "E19.14.23.4", {"start": v(462.5, -143.56) * mm, "mid": v(463.91, -142.98) * mm, "end": v(464.5, -141.56) * mm});
            skArc(sketch, "E19.18.23.4", {"start": v(455.5, -141.56) * mm, "mid": v(456.09, -142.98) * mm, "end": v(457.5, -143.56) * mm});
            skPoint(sketch, "E19.0.23.5", {"position": v(455.5, -178.2) * mm});
            skLineSegment(sketch, "E19.1.23.5", {"start": v(464.5, -137.03) * mm, "end": v(464.5, -176.2) * mm});
            skPoint(sketch, "E19.4.23.5", {"position": v(464.5, -178.2) * mm});
            skLineSegment(sketch, "E19.5.23.5", {"start": v(455.5, -137.03) * mm, "end": v(464.5, -137.03) * mm});
            skLineSegment(sketch, "E19.8.23.5", {"start": v(457.5, -178.2) * mm, "end": v(462.5, -178.2) * mm});
            skLineSegment(sketch, "E19.11.23.5", {"start": v(455.5, -137.03) * mm, "end": v(455.5, -176.2) * mm});
            skArc(sketch, "E19.14.23.5", {"start": v(462.5, -178.2) * mm, "mid": v(463.91, -177.62) * mm, "end": v(464.5, -176.2) * mm});
            skArc(sketch, "E19.18.23.5", {"start": v(455.5, -176.2) * mm, "mid": v(456.09, -177.62) * mm, "end": v(457.5, -178.2) * mm});
            skPoint(sketch, "E19.0.23.6", {"position": v(455.5, -212.85) * mm});
            skLineSegment(sketch, "E19.1.23.6", {"start": v(464.5, -171.67) * mm, "end": v(464.5, -210.85) * mm});
            skPoint(sketch, "E19.4.23.6", {"position": v(464.5, -212.85) * mm});
            skLineSegment(sketch, "E19.5.23.6", {"start": v(455.5, -171.67) * mm, "end": v(464.5, -171.67) * mm});
            skLineSegment(sketch, "E19.8.23.6", {"start": v(457.5, -212.85) * mm, "end": v(462.5, -212.85) * mm});
            skLineSegment(sketch, "E19.11.23.6", {"start": v(455.5, -171.67) * mm, "end": v(455.5, -210.85) * mm});
            skArc(sketch, "E19.14.23.6", {"start": v(462.5, -212.85) * mm, "mid": v(463.91, -212.26) * mm, "end": v(464.5, -210.85) * mm});
            skArc(sketch, "E19.18.23.6", {"start": v(455.5, -210.85) * mm, "mid": v(456.09, -212.26) * mm, "end": v(457.5, -212.85) * mm});
            skPoint(sketch, "E19.0.23.7", {"position": v(455.5, -247.49) * mm});
            skLineSegment(sketch, "E19.1.23.7", {"start": v(464.5, -206.31) * mm, "end": v(464.5, -245.49) * mm});
            skPoint(sketch, "E19.4.23.7", {"position": v(464.5, -247.49) * mm});
            skLineSegment(sketch, "E19.5.23.7", {"start": v(455.5, -206.31) * mm, "end": v(464.5, -206.31) * mm});
            skLineSegment(sketch, "E19.8.23.7", {"start": v(457.5, -247.49) * mm, "end": v(462.5, -247.49) * mm});
            skLineSegment(sketch, "E19.11.23.7", {"start": v(455.5, -206.31) * mm, "end": v(455.5, -245.49) * mm});
            skArc(sketch, "E19.14.23.7", {"start": v(462.5, -247.49) * mm, "mid": v(463.91, -246.9) * mm, "end": v(464.5, -245.49) * mm});
            skArc(sketch, "E19.18.23.7", {"start": v(455.5, -245.49) * mm, "mid": v(456.09, -246.9) * mm, "end": v(457.5, -247.49) * mm});
            skPoint(sketch, "E19.0.23.8", {"position": v(455.5, -282.13) * mm});
            skLineSegment(sketch, "E19.1.23.8", {"start": v(464.5, -240.95) * mm, "end": v(464.5, -280.13) * mm});
            skPoint(sketch, "E19.4.23.8", {"position": v(464.5, -282.13) * mm});
            skLineSegment(sketch, "E19.5.23.8", {"start": v(455.5, -240.95) * mm, "end": v(464.5, -240.95) * mm});
            skLineSegment(sketch, "E19.8.23.8", {"start": v(457.5, -282.13) * mm, "end": v(462.5, -282.13) * mm});
            skLineSegment(sketch, "E19.11.23.8", {"start": v(455.5, -240.95) * mm, "end": v(455.5, -280.13) * mm});
            skArc(sketch, "E19.14.23.8", {"start": v(462.5, -282.13) * mm, "mid": v(463.91, -281.54) * mm, "end": v(464.5, -280.13) * mm});
            skArc(sketch, "E19.18.23.8", {"start": v(455.5, -280.13) * mm, "mid": v(456.09, -281.54) * mm, "end": v(457.5, -282.13) * mm});
            skPoint(sketch, "E19.0.23.9", {"position": v(455.5, -316.77) * mm});
            skLineSegment(sketch, "E19.1.23.9", {"start": v(464.5, -275.6) * mm, "end": v(464.5, -314.77) * mm});
            skPoint(sketch, "E19.4.23.9", {"position": v(464.5, -316.77) * mm});
            skLineSegment(sketch, "E19.5.23.9", {"start": v(455.5, -275.6) * mm, "end": v(464.5, -275.6) * mm});
            skLineSegment(sketch, "E19.8.23.9", {"start": v(457.5, -316.77) * mm, "end": v(462.5, -316.77) * mm});
            skLineSegment(sketch, "E19.11.23.9", {"start": v(455.5, -275.6) * mm, "end": v(455.5, -314.77) * mm});
            skArc(sketch, "E19.14.23.9", {"start": v(462.5, -316.77) * mm, "mid": v(463.91, -316.18) * mm, "end": v(464.5, -314.77) * mm});
            skArc(sketch, "E19.18.23.9", {"start": v(455.5, -314.77) * mm, "mid": v(456.09, -316.18) * mm, "end": v(457.5, -316.77) * mm});
            skPoint(sketch, "E19.0.23.10", {"position": v(455.5, -351.41) * mm});
            skLineSegment(sketch, "E19.1.23.10", {"start": v(464.5, -310.24) * mm, "end": v(464.5, -349.41) * mm});
            skPoint(sketch, "E19.4.23.10", {"position": v(464.5, -351.41) * mm});
            skLineSegment(sketch, "E19.5.23.10", {"start": v(455.5, -310.24) * mm, "end": v(464.5, -310.24) * mm});
            skLineSegment(sketch, "E19.8.23.10", {"start": v(457.5, -351.41) * mm, "end": v(462.5, -351.41) * mm});
            skLineSegment(sketch, "E19.11.23.10", {"start": v(455.5, -310.24) * mm, "end": v(455.5, -349.41) * mm});
            skArc(sketch, "E19.14.23.10", {"start": v(462.5, -351.41) * mm, "mid": v(463.91, -350.82) * mm, "end": v(464.5, -349.41) * mm});
            skArc(sketch, "E19.18.23.10", {"start": v(455.5, -349.41) * mm, "mid": v(456.09, -350.82) * mm, "end": v(457.5, -351.41) * mm});
            skPoint(sketch, "E19.0.23.11", {"position": v(455.5, -386.05) * mm});
            skLineSegment(sketch, "E19.1.23.11", {"start": v(464.5, -344.88) * mm, "end": v(464.5, -384.05) * mm});
            skPoint(sketch, "E19.4.23.11", {"position": v(464.5, -386.05) * mm});
            skLineSegment(sketch, "E19.5.23.11", {"start": v(455.5, -344.88) * mm, "end": v(464.5, -344.88) * mm});
            skLineSegment(sketch, "E19.8.23.11", {"start": v(457.5, -386.05) * mm, "end": v(462.5, -386.05) * mm});
            skLineSegment(sketch, "E19.11.23.11", {"start": v(455.5, -344.88) * mm, "end": v(455.5, -384.05) * mm});
            skArc(sketch, "E19.14.23.11", {"start": v(462.5, -386.05) * mm, "mid": v(463.91, -385.47) * mm, "end": v(464.5, -384.05) * mm});
            skArc(sketch, "E19.18.23.11", {"start": v(455.5, -384.05) * mm, "mid": v(456.09, -385.47) * mm, "end": v(457.5, -386.05) * mm});
            skPoint(sketch, "E19.0.23.12", {"position": v(455.5, -420.7) * mm});
            skLineSegment(sketch, "E19.1.23.12", {"start": v(464.5, -379.52) * mm, "end": v(464.5, -418.7) * mm});
            skPoint(sketch, "E19.4.23.12", {"position": v(464.5, -420.7) * mm});
            skLineSegment(sketch, "E19.5.23.12", {"start": v(455.5, -379.52) * mm, "end": v(464.5, -379.52) * mm});
            skLineSegment(sketch, "E19.8.23.12", {"start": v(457.5, -420.7) * mm, "end": v(462.5, -420.7) * mm});
            skLineSegment(sketch, "E19.11.23.12", {"start": v(455.5, -379.52) * mm, "end": v(455.5, -418.7) * mm});
            skArc(sketch, "E19.14.23.12", {"start": v(462.5, -420.7) * mm, "mid": v(463.91, -420.1) * mm, "end": v(464.5, -418.7) * mm});
            skArc(sketch, "E19.18.23.12", {"start": v(455.5, -418.7) * mm, "mid": v(456.09, -420.1) * mm, "end": v(457.5, -420.7) * mm});
            skPoint(sketch, "E19.0.23.13", {"position": v(455.5, -455.33) * mm});
            skLineSegment(sketch, "E19.1.23.13", {"start": v(464.5, -414.16) * mm, "end": v(464.5, -453.33) * mm});
            skPoint(sketch, "E19.4.23.13", {"position": v(464.5, -455.33) * mm});
            skLineSegment(sketch, "E19.5.23.13", {"start": v(455.5, -414.16) * mm, "end": v(464.5, -414.16) * mm});
            skLineSegment(sketch, "E19.8.23.13", {"start": v(457.5, -455.33) * mm, "end": v(462.5, -455.33) * mm});
            skLineSegment(sketch, "E19.11.23.13", {"start": v(455.5, -414.16) * mm, "end": v(455.5, -453.33) * mm});
            skArc(sketch, "E19.14.23.13", {"start": v(462.5, -455.33) * mm, "mid": v(463.91, -454.75) * mm, "end": v(464.5, -453.33) * mm});
            skArc(sketch, "E19.18.23.13", {"start": v(455.5, -453.33) * mm, "mid": v(456.09, -454.75) * mm, "end": v(457.5, -455.33) * mm});
            skPoint(sketch, "E19.0.23.14", {"position": v(455.5, -489.97) * mm});
            skLineSegment(sketch, "E19.1.23.14", {"start": v(464.5, -448.8) * mm, "end": v(464.5, -487.97) * mm});
            skPoint(sketch, "E19.4.23.14", {"position": v(464.5, -489.97) * mm});
            skLineSegment(sketch, "E19.5.23.14", {"start": v(455.5, -448.8) * mm, "end": v(464.5, -448.8) * mm});
            skLineSegment(sketch, "E19.8.23.14", {"start": v(457.5, -489.97) * mm, "end": v(462.5, -489.97) * mm});
            skLineSegment(sketch, "E19.11.23.14", {"start": v(455.5, -448.8) * mm, "end": v(455.5, -487.97) * mm});
            skArc(sketch, "E19.14.23.14", {"start": v(462.5, -489.97) * mm, "mid": v(463.91, -489.39) * mm, "end": v(464.5, -487.97) * mm});
            skArc(sketch, "E19.18.23.14", {"start": v(455.5, -487.97) * mm, "mid": v(456.09, -489.39) * mm, "end": v(457.5, -489.97) * mm});
            skSolve(sketch);
        }
        {
            var Q0;
            Q0=qSketchRegion(id+"F6",true);
            extrude(context, id + "F7", {"entities" : qUnion([Q0]), "operationType" : NewBodyOperationType.REMOVE, "oppositeDirection" : true, "depth" : 2 * mm});
        }
    });
